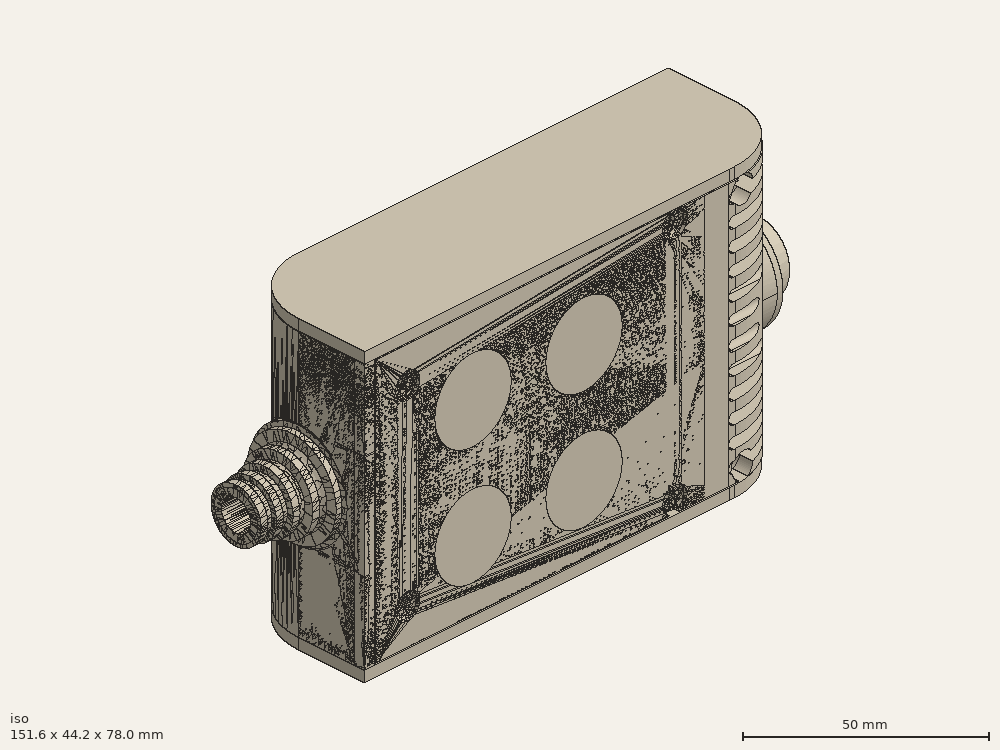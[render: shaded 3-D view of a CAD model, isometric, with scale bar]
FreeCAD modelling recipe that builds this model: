
FCSTD DOCUMENT  (FreeCAD 0.19R0.19.2)
Label: enclosure_186FCStd
License: All rights reserved
LicenseURL: http://en.wikipedia.org/wiki/All_rights_reserved
objects: Part::Revolution×152, Part::MultiFuse×146, Part::Feature×146, Sketcher::SketchObject×84, Part::Cut×70, Part::Cylinder×70, Part::Extrusion×67, Part::Fillet×58, Part::Box×36, App::MeasureDistance×4, PartDesign::Body×2, Image::ImagePlane×1
note: 831 computed .brp shape members not serialized (recipe doc carries the construction recipe); baked Part::Feature solids carry a one-line shape summary decoded from their .brp

FEATURE [Sketcher::SketchObject] Sketch  label="topSketch"
  FullyConstrained = true
  sketch-geometry (20):
    g0: LineSegment StartX=5.21097e-06 StartY=3 StartZ=0 EndX=5.21097e-06 EndY=19 EndZ=0
    g1: ArcOfCircle CenterX=19 CenterY=19 CenterZ=0 NormalX=0 NormalY=0 NormalZ=1 AngleXU=0 Radius=19 StartAngle=1.5708 EndAngle=3.14159
    g2: ArcOfCircle CenterX=19 CenterY=19 CenterZ=0 NormalX=0 NormalY=0 NormalZ=1 AngleXU=0 Radius=16 StartAngle=1.5708 EndAngle=3.14159
    g3: LineSegment StartX=114 StartY=35 StartZ=0 EndX=19 EndY=35 EndZ=0
    g4: LineSegment StartX=5.21097e-06 StartY=3 StartZ=0 EndX=5.21097e-06 EndY=0 EndZ=0
    g5: LineSegment StartX=3 StartY=0 StartZ=0 EndX=5.21097e-06 EndY=0 EndZ=0
    g6: LineSegment StartX=3 StartY=19 StartZ=0 EndX=3 EndY=0 EndZ=0
    g7: LineSegment StartX=19 StartY=38 StartZ=0 EndX=124 EndY=38 EndZ=0
    g8: Circle CenterX=119 CenterY=35 CenterZ=0 NormalX=0 NormalY=0 NormalZ=1 AngleXU=0 Radius=1
    g9: Circle CenterX=121 CenterY=35 CenterZ=0 NormalX=0 NormalY=0 NormalZ=1 AngleXU=0 Radius=1
    g10: Circle CenterX=121 CenterY=33 CenterZ=0 NormalX=0 NormalY=0 NormalZ=1 AngleXU=0 Radius=1
    g11: BSplineCurve PolesCount=3 KnotsCount=2 Degree=2 IsPeriodic=0
    g12: GeomPoint X=119 Y=35 Z=0
    g13: GeomPoint X=121 Y=33 Z=0
    g14: LineSegment StartX=119 StartY=35 StartZ=0 EndX=114 EndY=35 EndZ=0
    g15: ArcOfCircle CenterX=105 CenterY=19 CenterZ=0 NormalX=0 NormalY=0 NormalZ=1 AngleXU=0 Radius=19 StartAngle=5.7297 EndAngle=6.28319
    g16: ArcOfCircle CenterX=105 CenterY=19 CenterZ=0 NormalX=0 NormalY=0 NormalZ=1 AngleXU=0 Radius=16 StartAngle=5.60905 EndAngle=6.28319
    g17: LineSegment StartX=121 StartY=33 StartZ=0 EndX=121 EndY=19 EndZ=0
    g18: LineSegment StartX=124 StartY=38 StartZ=0 EndX=124 EndY=19 EndZ=0
    g19: LineSegment StartX=117.5 StartY=9.01251 StartZ=0 EndX=121.163 EndY=9.0125 EndZ=0
  constraints (46):
    c: Vertical(g0)
    c: Block(g0)
    c: Coincident(g1,g0)
    c: Block(g1)
    c: Coincident(g2,g1)
    c: Block(g2)
    c: Coincident(g3,g2)
    c: Horizontal(g3)
    c: Tangent(g3,g2)
    c: Coincident(g4,g0)
    c: Distance(g4) = 3
    c: Vertical(g4)
    c: Coincident(g5,g4)
    c: Horizontal(g5)
    c: Coincident(g6,g2)
    c: Coincident(g6,g5)
    c: Vertical(g6)
    c: Horizontal(g7)
    c: Distance(g7) = 105
    c: Coincident(g7,g1)
    c: Block(g3)
    c: Weight(g8) = 1
    c: Equal(g8,g9)
    c: Equal(g8,g10)
    c: InternalAlignment(g8,g11)
    c: InternalAlignment(g9,g11)
    c: InternalAlignment(g10,g11)
    c: InternalAlignment(g12,g11)
    c: InternalAlignment(g13,g11)
    c: Block(g11)
    c: Coincident(g14,g11)
    c: Coincident(g14,g3)
    c: Horizontal(g14)
    c: Block(g15)
    c: Coincident(g16,g15)
    c: Block(g16)
    c: Coincident(g17,g11)
    c: Coincident(g17,g16)
    c: Vertical(g17)
    c: Distance(g17) = 14
    c: Coincident(g18,g7)
    c: Coincident(g18,g15)
    c: Vertical(g18)
    c: Distance(g18) = 19
    c: Coincident(g19,g16)
    c: Coincident(g19,g15)
FEATURE [Sketcher::SketchObject] Sketch001  label="bottomSketch"
  FullyConstrained = true
  sketch-geometry (32):
    g0: LineSegment StartX=3.3 StartY=-6.03275e-07 StartZ=0 EndX=98 EndY=-6.03275e-07 EndZ=0
    g1: ArcOfCircle CenterX=98 CenterY=19 CenterZ=0 NormalX=0 NormalY=0 NormalZ=1 AngleXU=0 Radius=19 StartAngle=4.71239 EndAngle=5.71103
    g2: LineSegment StartX=6.3 StartY=8 StartZ=0 EndX=3.3 EndY=8 EndZ=0
    g3: LineSegment StartX=3.3 StartY=8 StartZ=0 EndX=3.3 EndY=-6.03275e-07 EndZ=0
    g4: ArcOfCircle CenterX=8.3 CenterY=5 CenterZ=0 NormalX=0 NormalY=0 NormalZ=1 AngleXU=0 Radius=2 StartAngle=3.14159 EndAngle=4.71239
    g5: LineSegment StartX=6.3 StartY=8 StartZ=0 EndX=6.3 EndY=5 EndZ=0
    g6: ArcOfCircle CenterX=98 CenterY=19 CenterZ=0 NormalX=0 NormalY=0 NormalZ=1 AngleXU=0 Radius=12.7 StartAngle=4.71239 EndAngle=6.28319
    g7: LineSegment StartX=94.7 StartY=3 StartZ=0 EndX=8.3 EndY=3 EndZ=0
    g8-g12: Circle x5 (B-spline internal-alignment scaffolding for g13; pole/knot coordinates omitted)
    g13: BSplineCurve PolesCount=5 KnotsCount=3 Degree=3 IsPeriodic=0
    g14: GeomPoint X=98 Y=6.3 Z=0
    g15: GeomPoint X=96.3938 Y=4.71946 Z=0
    g16: GeomPoint X=94.7 Y=3 Z=0
    g17-g23: Circle x7 (B-spline internal-alignment scaffolding for g24; pole/knot coordinates omitted)
    g24: BSplineCurve PolesCount=7 KnotsCount=5 Degree=3 IsPeriodic=0
    g25-g29: GeomPoint x5 (B-spline internal-alignment scaffolding for g24; pole/knot coordinates omitted)
    g30: ArcOfCircle CenterX=98 CenterY=19 CenterZ=0 NormalX=0 NormalY=0 NormalZ=1 AngleXU=0 Radius=15.7 StartAngle=5.81226 EndAngle=6.28319
    g31: LineSegment StartX=110.7 StartY=19 StartZ=0 EndX=113.7 EndY=19 EndZ=0
  constraints (41):
    c: Horizontal(g0)
    c: Coincident(g1,g0)
    c: Block(g1)
    c: Horizontal(g2)
    c: Distance(g2) = 3
    c: Coincident(g3,g2)
    c: Vertical(g3)
    c: Coincident(g3,g0)
    c: Block(g4)
    c: Block(g2)
    c: Coincident(g5,g2)
    c: Coincident(g5,g4)
    c: Vertical(g5)
    c: Coincident(g6,g1)
    c: Block(g6)
    c: Coincident(g7,g4)
    c: Horizontal(g7)
    c: Block(g0)
    c: Block(g7)
    c: Block(g3)
    c: Coincident(g13,g6)
    c: Weight(g8) = 1
    c: Equal(g8, g9-g12) x4
    c: Coincident(g13,g7)
    c: InternalAlignment(g8-g12 -> g13) x5
    c: InternalAlignment(g14,g13)
    c: InternalAlignment(g15,g13)
    c: InternalAlignment(g16,g13)
    c: Block(g13)
    c: Weight(g17) = 1
    c: Equal(g17, g18-g23) x6
    c: Coincident(g24,g1)
    c: InternalAlignment(g17-g23 -> g24) x7
    c: InternalAlignment(g25-g29 -> g24) x5
    c: Block(g24)
    c: Coincident(g30,g24)
    c: Coincident(g31,g6)
    c: Coincident(g31,g30)
    c: Horizontal(g31)
    c: Block(g31)
    c: Block(g30)
FEATURE [Part::Extrusion] Extrude  label="top"
  Base = -> Sketch
  Dir = (0,0,1)
  DirMode = 2
  FaceMakerClass = Part::FaceMakerBullseye
  LengthFwd = 72
  LengthRev = 0
  Solid = true
  Symmetric = false
FEATURE [Part::Extrusion] Extrude001  label="bottom"
  Base = -> Sketch001
  Dir = (0,0,1)
  DirMode = 2
  FaceMakerClass = Part::FaceMakerBullseye
  LengthFwd = 71.4
  LengthRev = 0
  Placement = pos=(0,0,0.3) rot=(0,0,1;0rad)
  Solid = true
  Symmetric = false
FEATURE [Sketcher::SketchObject] Sketch002  label="topSketch001"
  FullyConstrained = true
  sketch-geometry (8):
    g0: ArcOfCircle CenterX=19 CenterY=19.0975 CenterZ=0 NormalX=0 NormalY=0 NormalZ=1 AngleXU=0 Radius=18.9025 StartAngle=1.5708 EndAngle=3.14674
    g1: LineSegment StartX=0.0977805 StartY=19.0003 StartZ=0 EndX=0.0977805 EndY=0.000251602 EndZ=0
    g2: LineSegment StartX=19 StartY=38 StartZ=0 EndX=124 EndY=38 EndZ=0
    g3: LineSegment StartX=0.0977805 StartY=0.000251602 StartZ=0 EndX=105.098 EndY=0.000251602 EndZ=0
    g4: LineSegment StartX=124 StartY=38 StartZ=0 EndX=125.616 EndY=38 EndZ=0
    g5: LineSegment StartX=105.098 StartY=0.000251602 StartZ=0 EndX=106.713 EndY=0.000251602 EndZ=0
    g6: ArcOfCircle CenterX=106.616 CenterY=19 CenterZ=0 NormalX=0 NormalY=0 NormalZ=1 AngleXU=0 Radius=19 StartAngle=4.71754 EndAngle=6.28319
    g7: LineSegment StartX=125.616 StartY=38 StartZ=0 EndX=125.616 EndY=19 EndZ=0
  constraints (21):
    c: Block(g0)
    c: Coincident(g1,g0)
    c: Vertical(g1)
    c: Horizontal(g2)
    c: Distance(g2) = 105
    c: Coincident(g2,g0)
    c: Distance(g1) = 19
    c: Coincident(g3,g1)
    c: Horizontal(g3)
    c: Distance(g3) = 105
    c: Coincident(g4,g2)
    c: Horizontal(g4)
    c: Distance(g4) = 1.61553
    c: Horizontal(g5)
    c: Equal(g4,g5) = 1.61553
    c: Coincident(g5,g3)
    c: Block(g6)
    c: Coincident(g6,g5)
    c: Coincident(g7,g4)
    c: Coincident(g7,g6)
    c: Vertical(g7)
FEATURE [Part::Extrusion] Extrude002  label="sideA"
  Base = -> Sketch002
  Dir = (0,0,1)
  DirMode = 2
  FaceMakerClass = Part::FaceMakerBullseye
  LengthFwd = 3
  LengthRev = 0
  Placement = pos=(0,0,-3) rot=(0,0,1;0rad)
  Solid = true
  Symmetric = false
FEATURE [Sketcher::SketchObject] Sketch003  label="topSketch002"
  FullyConstrained = true
  sketch-geometry (6):
    g0: LineSegment StartX=19 StartY=38 StartZ=0 EndX=117 EndY=38 EndZ=0
    g1: ArcOfCircle CenterX=19 CenterY=19 CenterZ=0 NormalX=0 NormalY=0 NormalZ=1 AngleXU=0 Radius=19 StartAngle=1.5708 EndAngle=3.14159
    g2: LineSegment StartX=117 StartY=38 StartZ=0 EndX=117 EndY=19 EndZ=0
    g3: LineSegment StartX=98 StartY=1.0161e-12 StartZ=0 EndX=5.22862e-06 EndY=1.0161e-12 EndZ=0
    g4: LineSegment StartX=5.22862e-06 StartY=19 StartZ=0 EndX=5.22862e-06 EndY=1.0161e-12 EndZ=0
    g5: ArcOfCircle CenterX=98 CenterY=19 CenterZ=0 NormalX=0 NormalY=0 NormalZ=1 AngleXU=0 Radius=19 StartAngle=4.71239 EndAngle=6.28319
  constraints (16):
    c: Horizontal(g0)
    c: Distance(g0) = 98
    c: Coincident(g1,g0)
    c: Block(g1)
    c: Coincident(g2,g0)
    c: Vertical(g2)
    c: Distance(g2) = 19
    c: Horizontal(g3)
    c: Coincident(g4,g1)
    c: Vertical(g4)
    c: Coincident(g3,g4)
    c: Block(g3)
    c: Coincident(g5,g2)
    c: Coincident(g5,g3)
    c: Block(g0)
    c: Block(g5)
FEATURE [Sketcher::SketchObject] Sketch004
  FullyConstrained = true
  MapMode = 3
  Placement = pos=(0,0,0) rot=(1,0,0;1.5708rad)
  Support = -> [Extrude]
  sketch-geometry (8):
    g0: Circle CenterX=80.351 CenterY=-67.6202 CenterZ=0 NormalX=0 NormalY=0 NormalZ=1 AngleXU=0 Radius=2
    g1: Circle CenterX=80.351 CenterY=-67.6202 CenterZ=0 NormalX=0 NormalY=0 NormalZ=1 AngleXU=0 Radius=3
    g2: Circle CenterX=80.351 CenterY=-4.92017 CenterZ=0 NormalX=0 NormalY=0 NormalZ=1 AngleXU=0 Radius=2
    g3: Circle CenterX=80.351 CenterY=-4.92017 CenterZ=0 NormalX=0 NormalY=0 NormalZ=1 AngleXU=0 Radius=3
    g4: Circle CenterX=23.851 CenterY=-4.92017 CenterZ=0 NormalX=0 NormalY=0 NormalZ=1 AngleXU=0 Radius=2
    g5: Circle CenterX=23.851 CenterY=-4.92017 CenterZ=0 NormalX=0 NormalY=0 NormalZ=1 AngleXU=0 Radius=3
    g6: Circle CenterX=23.851 CenterY=-67.6202 CenterZ=0 NormalX=0 NormalY=0 NormalZ=1 AngleXU=0 Radius=2
    g7: Circle CenterX=23.851 CenterY=-67.6202 CenterZ=0 NormalX=0 NormalY=0 NormalZ=1 AngleXU=0 Radius=3
  constraints (8):
    c: Block(g3)
    c: Block(g2)
    c: Block(g1)
    c: Block(g0)
    c: Block(g6)
    c: Block(g7)
    c: Block(g4)
    c: Block(g5)
FEATURE [Part::Extrusion] Extrude004
  Base = -> Sketch004
  Dir = (0,-1,2e-16)
  DirMode = 2
  FaceMakerClass = Part::FaceMakerBullseye
  LengthFwd = 6
  LengthRev = 0
  Placement = pos=(0,9,0) rot=(0,0,1;0rad)
  Solid = true
  Symmetric = false
FEATURE [Sketcher::SketchObject] Sketch005
  FullyConstrained = true
  MapMode = 3
  Placement = pos=(0,0,0) rot=(1,0,0;1.5708rad)
  Support = -> [Extrude]
  sketch-geometry (8):
    g0: Circle CenterX=80.351 CenterY=-67.6202 CenterZ=0 NormalX=0 NormalY=0 NormalZ=1 AngleXU=0 Radius=3
    g1: Circle CenterX=80.351 CenterY=-4.92017 CenterZ=0 NormalX=0 NormalY=0 NormalZ=1 AngleXU=0 Radius=3
    g2: Circle CenterX=23.851 CenterY=-4.92017 CenterZ=0 NormalX=0 NormalY=0 NormalZ=1 AngleXU=0 Radius=3
    g3: Circle CenterX=23.851 CenterY=-67.6202 CenterZ=0 NormalX=0 NormalY=0 NormalZ=1 AngleXU=0 Radius=3
    g4: Circle CenterX=23.851 CenterY=-67.6202 CenterZ=0 NormalX=0 NormalY=0 NormalZ=1 AngleXU=0 Radius=5
    g5: Circle CenterX=80.351 CenterY=-67.6202 CenterZ=0 NormalX=0 NormalY=0 NormalZ=1 AngleXU=0 Radius=5
    g6: Circle CenterX=23.851 CenterY=-4.92017 CenterZ=0 NormalX=0 NormalY=0 NormalZ=1 AngleXU=0 Radius=5
    g7: Circle CenterX=80.351 CenterY=-4.92017 CenterZ=0 NormalX=0 NormalY=0 NormalZ=1 AngleXU=0 Radius=5
  constraints (8):
    c: Block(g1)
    c: Block(g0)
    c: Block(g3)
    c: Block(g2)
    c: Block(g5)
    c: Block(g4)
    c: Block(g6)
    c: Block(g7)
FEATURE [Part::Extrusion] Extrude005
  Base = -> Sketch005
  Dir = (0,-1,2e-16)
  DirMode = 2
  FaceMakerClass = Part::FaceMakerBullseye
  LengthFwd = 2
  LengthRev = 0
  Solid = true
  Symmetric = false
FEATURE [Sketcher::SketchObject] Sketch006
  FullyConstrained = true
  MapMode = 3
  Placement = pos=(0,0,0) rot=(1,0,0;1.5708rad)
  sketch-geometry (8):
    g0: Circle CenterX=80.351 CenterY=-67.6202 CenterZ=0 NormalX=0 NormalY=0 NormalZ=1 AngleXU=0 Radius=3
    g1: Circle CenterX=80.351 CenterY=-4.92017 CenterZ=0 NormalX=0 NormalY=0 NormalZ=1 AngleXU=0 Radius=3
    g2: Circle CenterX=23.851 CenterY=-4.92017 CenterZ=0 NormalX=0 NormalY=0 NormalZ=1 AngleXU=0 Radius=3
    g3: Circle CenterX=23.851 CenterY=-67.6202 CenterZ=0 NormalX=0 NormalY=0 NormalZ=1 AngleXU=0 Radius=3
    g4: Circle CenterX=23.851 CenterY=-67.6202 CenterZ=0 NormalX=0 NormalY=0 NormalZ=1 AngleXU=0 Radius=5
    g5: Circle CenterX=80.351 CenterY=-67.6202 CenterZ=0 NormalX=0 NormalY=0 NormalZ=1 AngleXU=0 Radius=5
    g6: Circle CenterX=23.851 CenterY=-4.92017 CenterZ=0 NormalX=0 NormalY=0 NormalZ=1 AngleXU=0 Radius=5
    g7: Circle CenterX=80.351 CenterY=-4.92017 CenterZ=0 NormalX=0 NormalY=0 NormalZ=1 AngleXU=0 Radius=5
  constraints (8):
    c: Block(g1)
    c: Block(g0)
    c: Block(g3)
    c: Block(g2)
    c: Block(g5)
    c: Block(g4)
    c: Block(g6)
    c: Block(g7)
FEATURE [Part::Extrusion] Extrude007
  Base = -> Sketch006
  Dir = (0,-1,2e-16)
  DirMode = 2
  FaceMakerClass = Part::FaceMakerBullseye
  LengthFwd = 2
  LengthRev = 0
  Solid = true
  Symmetric = false
FEATURE [Part::Fillet] Fillet
  Base = -> Extrude007
  Edges = 4 edges r=1.99: [Edge6,Edge12,Edge18,Edge24]
FEATURE [Part::Cut] Cut
  Base = -> Extrude005
  Placement = pos=(0,5,0) rot=(0,0,1;0rad)
  Tool = -> Fillet
FEATURE [Part::MultiFuse] Fusion  label="pCBScrews"
  Placement = pos=(-2.5,0,72.3) rot=(0,0,1;0rad)
  Shapes = -> [Extrude004,Cut]
FEATURE [App::MeasureDistance] Distance  label="Distance: 0.69 mm"
  Distance = 0.685967
  P1 = (24.0138,2.9647,0.3)
  P2 = (23.8901,3,-0.373787)
FEATURE [App::MeasureDistance] Distance001  label="Distance: 0.53 mm"
  Distance = 0.533607
  P1 = (80.2939,3,72.2334)
  P2 = (80.281,2.99661,71.7)
FEATURE [Part::Fillet] Fillet001
  Base = -> Extrude001
  Edges = 1 edges r=2.4: [Edge17]
FEATURE [Part::Fillet] Fillet002  label="bottom001"
  Base = -> Fillet001
  Edges = 1 edges r=2.4: [Edge36]
FEATURE [Part::Fillet] Fillet003  label="top001"
  Base = -> Extrude
  Edges = 1 edges r=2: [Edge1]
FEATURE [Sketcher::SketchObject] Sketch007
  FullyConstrained = true
  sketch-geometry (16):
    g0: LineSegment StartX=4 StartY=0 StartZ=0 EndX=4 EndY=2.4 EndZ=0
    g1: LineSegment StartX=4 StartY=2.4 StartZ=0 EndX=7 EndY=2.4 EndZ=0
    g2: LineSegment StartX=4 StartY=0 StartZ=0 EndX=5.7 EndY=0 EndZ=0
    g3: LineSegment StartX=5.7 StartY=0 StartZ=0 EndX=5.7 EndY=-5.6 EndZ=0
    g4-g8: Circle x5 (B-spline internal-alignment scaffolding for g9; pole/knot coordinates omitted)
    g9: BSplineCurve PolesCount=5 KnotsCount=3 Degree=3 IsPeriodic=0
    g10: GeomPoint X=7 Y=2.4 Z=0
    g11: GeomPoint X=10.4582 Y=-1.55472 Z=0
    g12: GeomPoint X=14 Y=-5.6 Z=0
    g13: LineSegment StartX=14 StartY=-5.6 StartZ=0 EndX=14 EndY=-14.1 EndZ=0
    g14: LineSegment StartX=14 StartY=-14.1 StartZ=0 EndX=6.5 EndY=-14.1 EndZ=0
    g15: LineSegment StartX=5.7 StartY=-5.6 StartZ=0 EndX=6.5 EndY=-14.1 EndZ=0
  constraints (28):
    c: Distance(g0) = 2.4
    c: Vertical(g0)
    c: Block(g0)
    c: Coincident(g1,g0)
    c: Horizontal(g1)
    c: Distance(g1) = 3
    c: Coincident(g2,g0)
    c: Horizontal(g2)
    c: Distance(g2) = 1.7
    c: Coincident(g3,g2)
    c: Vertical(g3)
    c: Distance(g3) = 5.6
    c: Coincident(g9,g1)
    c: Weight(g4) = 1
    c: Equal(g4, g5-g8) x4
    c: InternalAlignment(g4-g8 -> g9) x5
    c: InternalAlignment(g10,g9)
    c: InternalAlignment(g11,g9)
    c: InternalAlignment(g12,g9)
    c: Block(g9)
    c: Coincident(g13,g9)
    c: Vertical(g13)
    c: Distance(g13) = 8.5
    c: Coincident(g14,g13)
    c: Horizontal(g14)
    c: Distance(g14) = 7.5
    c: Coincident(g15,g3)
    c: Coincident(g15,g14)
FEATURE [Part::Feature] Face
  shape: bbox 10 x 16.5 x 2e-07 mm, 1 faces, 0 solids (baked)
FEATURE [Part::Revolution] Revolve  label="plugHousing"
  Angle = 360
  Axis = (0,1,0)
  Base = (0,0,0)
  FaceMakerClass = Part::FaceMakerBullseye
  Placement = pos=(0,0,36.15) rot=(0,0,1;0rad)
  Solid = false
  Source = -> Face
  Symmetric = false
FEATURE [Part::Feature] Face001
  shape: bbox 10 x 16.5 x 2e-07 mm, 1 faces, 0 solids (baked)
FEATURE [Part::Revolution] Revolve001  label="plugHousing001"
  Angle = 360
  Axis = (0,1,0)
  Base = (0,0,0)
  FaceMakerClass = Part::FaceMakerBullseye
  Placement = pos=(0,0,36.15) rot=(0,0,1;0rad)
  Solid = false
  Source = -> Face001
  Symmetric = false
FEATURE [Part::MultiFuse] Fusion001  label="plugHousing002"
  Placement = pos=(0,0,0) rot=(0,0,1;1.5708rad)
  Shapes = -> [Revolve001,Revolve]
FEATURE [Part::Feature] Face002
  shape: bbox 10 x 16.5 x 2e-07 mm, 1 faces, 0 solids (baked)
FEATURE [Part::Revolution] Revolve003  label="plugHousing005"
  Angle = 360
  Axis = (0,1,0)
  Base = (0,0,0)
  FaceMakerClass = Part::FaceMakerBullseye
  Placement = pos=(0,0,36.15) rot=(0,0,1;0rad)
  Solid = false
  Source = -> Face002
  Symmetric = false
FEATURE [Part::Feature] Face003
  shape: bbox 10 x 16.5 x 2e-07 mm, 1 faces, 0 solids (baked)
FEATURE [Part::Revolution] Revolve002  label="plugHousing003"
  Angle = 360
  Axis = (0,1,0)
  Base = (0,0,0)
  FaceMakerClass = Part::FaceMakerBullseye
  Placement = pos=(0,0,36.15) rot=(0,0,1;0rad)
  Solid = false
  Source = -> Face003
  Symmetric = false
FEATURE [Part::MultiFuse] Fusion002  label="plugHousing004"
  Placement = pos=(0,0,0) rot=(0,0,1;1.5708rad)
  Shapes = -> [Revolve002,Revolve003]
FEATURE [Part::MultiFuse] Fusion003  label="plugHousing006"
  Placement = pos=(0,19,0) rot=(0,0,1;3.14159rad)
  Shapes = -> [Fusion002,Fusion001]
FEATURE [Part::Feature] Face004
  shape: bbox 10 x 16.5 x 2e-07 mm, 1 faces, 0 solids (baked)
FEATURE [Part::Revolution] Revolve006  label="plugHousing010"
  Angle = 360
  Axis = (0,1,0)
  Base = (0,0,0)
  FaceMakerClass = Part::FaceMakerBullseye
  Placement = pos=(0,0,36.15) rot=(0,0,1;0rad)
  Solid = false
  Source = -> Face004
  Symmetric = false
FEATURE [Part::Feature] Face005
  shape: bbox 10 x 16.5 x 2e-07 mm, 1 faces, 0 solids (baked)
FEATURE [Part::Revolution] Revolve007  label="plugHousing011"
  Angle = 360
  Axis = (0,1,0)
  Base = (0,0,0)
  FaceMakerClass = Part::FaceMakerBullseye
  Placement = pos=(0,0,36.15) rot=(0,0,1;0rad)
  Solid = false
  Source = -> Face005
  Symmetric = false
FEATURE [Part::Feature] Face006
  shape: bbox 10 x 16.5 x 2e-07 mm, 1 faces, 0 solids (baked)
FEATURE [Part::Revolution] Revolve004  label="plugHousing007"
  Angle = 360
  Axis = (0,1,0)
  Base = (0,0,0)
  FaceMakerClass = Part::FaceMakerBullseye
  Placement = pos=(0,0,36.15) rot=(0,0,1;0rad)
  Solid = false
  Source = -> Face006
  Symmetric = false
FEATURE [Part::MultiFuse] Fusion004  label="plugHousing009"
  Placement = pos=(0,0,0) rot=(0,0,1;1.5708rad)
  Shapes = -> [Revolve004,Revolve007]
FEATURE [Part::Feature] Face007
  shape: bbox 10 x 16.5 x 2e-07 mm, 1 faces, 0 solids (baked)
FEATURE [Part::Revolution] Revolve005  label="plugHousing008"
  Angle = 360
  Axis = (0,1,0)
  Base = (0,0,0)
  FaceMakerClass = Part::FaceMakerBullseye
  Placement = pos=(0,0,36.15) rot=(0,0,1;0rad)
  Solid = false
  Source = -> Face007
  Symmetric = false
FEATURE [Part::MultiFuse] Fusion005  label="plugHousing012"
  Placement = pos=(0,0,0) rot=(0,0,1;1.5708rad)
  Shapes = -> [Revolve006,Revolve005]
FEATURE [Part::MultiFuse] Fusion006  label="plugHousing013"
  Placement = pos=(0,19,0) rot=(0,0,1;3.14159rad)
  Shapes = -> [Fusion005,Fusion004]
FEATURE [Part::MultiFuse] Fusion007  label="plugHousing014"
  Placement = pos=(122.621,0,-0.15) rot=(0,0,1;0rad)
  Shapes = -> [Fusion003,Fusion006]
FEATURE [Part::Cylinder] Cylinder002
  Angle = 360
  AttacherType = Attacher::AttachEngine3D
  Height = 20
  Placement = pos=(0,0,36.15) rot=(0,0,1;0rad)
  Radius = 4
FEATURE [Part::Cylinder] Cylinder003
  Angle = 360
  AttacherType = Attacher::AttachEngine3D
  Height = 10
  Placement = pos=(0,0,36.15) rot=(0,0,1;0rad)
  Radius = 4
FEATURE [Part::MultiFuse] Fusion009  label="removeToCreateHoleForPlugHousing"
  Placement = pos=(70,19,36.15) rot=(0,1,0;1.5708rad)
  Shapes = -> [Cylinder002,Cylinder003]
FEATURE [Part::Cylinder] Cylinder004
  Angle = 360
  AttacherType = Attacher::AttachEngine3D
  Height = 20
  Placement = pos=(0,0,36.15) rot=(0,0,1;0rad)
  Radius = 4
FEATURE [Part::Cylinder] Cylinder005
  Angle = 360
  AttacherType = Attacher::AttachEngine3D
  Height = 10
  Placement = pos=(0,0,36.15) rot=(0,0,1;0rad)
  Radius = 4
FEATURE [Part::MultiFuse] Fusion010  label="removeToCreateHoleForPlugHousing001"
  Placement = pos=(70,19,36.15) rot=(0,1,0;1.5708rad)
  Shapes = -> [Cylinder004,Cylinder005]
FEATURE [Part::Cut] Cut001
  Base = -> Fillet003
  Tool = -> Fusion010
FEATURE [Part::Cut] Cut002  label="Bottom"
  Base = -> Fillet002
  Tool = -> Fusion009
FEATURE [Part::Feature] Face008
  shape: bbox 10 x 16.5 x 2e-07 mm, 1 faces, 0 solids (baked)
FEATURE [Part::Revolution] Revolve011  label="plugHousing021"
  Angle = 360
  Axis = (0,1,0)
  Base = (0,0,0)
  FaceMakerClass = Part::FaceMakerBullseye
  Placement = pos=(0,0,36.15) rot=(0,0,1;0rad)
  Solid = false
  Source = -> Face008
  Symmetric = false
FEATURE [Part::Feature] Face009
  shape: bbox 10 x 16.5 x 2e-07 mm, 1 faces, 0 solids (baked)
FEATURE [Part::Revolution] Revolve012  label="plugHousing022"
  Angle = 360
  Axis = (0,1,0)
  Base = (0,0,0)
  FaceMakerClass = Part::FaceMakerBullseye
  Placement = pos=(0,0,36.15) rot=(0,0,1;0rad)
  Solid = false
  Source = -> Face009
  Symmetric = false
FEATURE [Part::Feature] Face010 .. Face013  x4 (patterned run collapsed; names and placements below)
  shape: bbox 10 x 16.5 x 2e-07 mm, 1 faces, 0 solids (baked)
FEATURE [Part::Revolution] Revolve015  label="plugHousing027"
  Angle = 360
  Axis = (0,1,0)
  Base = (0,0,0)
  FaceMakerClass = Part::FaceMakerBullseye
  Placement = pos=(0,0,36.15) rot=(0,0,1;0rad)
  Solid = false
  Source = -> Face013
  Symmetric = false
FEATURE [Part::Feature] Face014
  shape: bbox 10 x 16.5 x 2e-07 mm, 1 faces, 0 solids (baked)
FEATURE [Part::Feature] Face015
  shape: bbox 10 x 16.5 x 2e-07 mm, 1 faces, 0 solids (baked)
FEATURE [Part::Feature] Face016
  shape: bbox 10 x 16.5 x 2e-07 mm, 1 faces, 0 solids (baked)
FEATURE [Part::Revolution] Revolve019  label="plugHousing033"
  Angle = 360
  Axis = (0,1,0)
  Base = (0,0,0)
  FaceMakerClass = Part::FaceMakerBullseye
  Placement = pos=(0,0,36.15) rot=(0,0,1;0rad)
  Solid = false
  Source = -> Face016
  Symmetric = false
FEATURE [Part::Feature] Face017
  shape: bbox 10 x 16.5 x 2e-07 mm, 1 faces, 0 solids (baked)
FEATURE [Part::Revolution] Revolve020  label="plugHousing034"
  Angle = 360
  Axis = (0,1,0)
  Base = (0,0,0)
  FaceMakerClass = Part::FaceMakerBullseye
  Placement = pos=(0,0,36.15) rot=(0,0,1;0rad)
  Solid = false
  Source = -> Face017
  Symmetric = false
FEATURE [Part::Feature] Face018
  shape: bbox 10 x 16.5 x 2e-07 mm, 1 faces, 0 solids (baked)
FEATURE [Part::Revolution] Revolve016  label="plugHousing030"
  Angle = 360
  Axis = (0,1,0)
  Base = (0,0,0)
  FaceMakerClass = Part::FaceMakerBullseye
  Placement = pos=(0,0,36.15) rot=(0,0,1;0rad)
  Solid = false
  Source = -> Face018
  Symmetric = false
FEATURE [Part::MultiFuse] Fusion020  label="plugHousing038"
  Placement = pos=(0,0,0) rot=(0,0,1;1.5708rad)
  Shapes = -> [Revolve016,Revolve020]
FEATURE [Part::Feature] Face019
  shape: bbox 10 x 16.5 x 2e-07 mm, 1 faces, 0 solids (baked)
FEATURE [Part::Feature] Face020
  shape: bbox 10 x 16.5 x 2e-07 mm, 1 faces, 0 solids (baked)
FEATURE [Part::Revolution] Revolve017  label="plugHousing031"
  Angle = 360
  Axis = (0,1,0)
  Base = (0,0,0)
  FaceMakerClass = Part::FaceMakerBullseye
  Placement = pos=(0,0,36.15) rot=(0,0,1;0rad)
  Solid = false
  Source = -> Face020
  Symmetric = false
FEATURE [Part::MultiFuse] Fusion021  label="plugHousing039"
  Placement = pos=(0,0,0) rot=(0,0,1;1.5708rad)
  Shapes = -> [Revolve019,Revolve017]
FEATURE [Part::MultiFuse] Fusion023  label="plugHousing041"
  Placement = pos=(0,19,0) rot=(0,0,1;3.14159rad)
  Shapes = -> [Fusion021,Fusion020]
FEATURE [Part::Revolution] Revolve022  label="plugHousing043"
  Angle = 360
  Axis = (0,1,0)
  Base = (0,0,0)
  FaceMakerClass = Part::FaceMakerBullseye
  Placement = pos=(0,0,36.15) rot=(0,0,1;0rad)
  Solid = false
  Source = -> Face019
  Symmetric = false
FEATURE [Part::Feature] Face021
  shape: bbox 10 x 16.5 x 2e-07 mm, 1 faces, 0 solids (baked)
FEATURE [Part::Revolution] Revolve023  label="plugHousing044"
  Angle = 360
  Axis = (0,1,0)
  Base = (0,0,0)
  FaceMakerClass = Part::FaceMakerBullseye
  Placement = pos=(0,0,36.15) rot=(0,0,1;0rad)
  Solid = false
  Source = -> Face021
  Symmetric = false
FEATURE [Part::Feature] Face022
  shape: bbox 10 x 16.5 x 2e-07 mm, 1 faces, 0 solids (baked)
FEATURE [Part::Revolution] Revolve018  label="plugHousing032"
  Angle = 360
  Axis = (0,1,0)
  Base = (0,0,0)
  FaceMakerClass = Part::FaceMakerBullseye
  Placement = pos=(0,0,36.15) rot=(0,0,1;0rad)
  Solid = false
  Source = -> Face022
  Symmetric = false
FEATURE [Part::MultiFuse] Fusion022  label="plugHousing040"
  Placement = pos=(0,0,0) rot=(0,0,1;1.5708rad)
  Shapes = -> [Revolve018,Revolve023]
FEATURE [Part::Feature] Face023
  shape: bbox 10 x 16.5 x 2e-07 mm, 1 faces, 0 solids (baked)
FEATURE [Part::Revolution] Revolve021  label="plugHousing035"
  Angle = 360
  Axis = (0,1,0)
  Base = (0,0,0)
  FaceMakerClass = Part::FaceMakerBullseye
  Placement = pos=(0,0,36.15) rot=(0,0,1;0rad)
  Solid = false
  Source = -> Face023
  Symmetric = false
FEATURE [Part::MultiFuse] Fusion018  label="plugHousing036"
  Placement = pos=(0,0,0) rot=(0,0,1;1.5708rad)
  Shapes = -> [Revolve022,Revolve021]
FEATURE [Part::MultiFuse] Fusion019  label="plugHousing037"
  Placement = pos=(0,19,0) rot=(0,0,1;3.14159rad)
  Shapes = -> [Fusion018,Fusion022]
FEATURE [Part::MultiFuse] Fusion024  label="plugHousing042"
  Placement = pos=(122.621,0,-0.15) rot=(0,0,1;0rad)
  Shapes = -> [Fusion023,Fusion019]
FEATURE [Part::Cylinder] Cylinder006
  Angle = 360
  AttacherType = Attacher::AttachEngine3D
  Height = 20
  Placement = pos=(0,0,36.15) rot=(0,0,1;0rad)
  Radius = 14.3
FEATURE [Part::Cylinder] Cylinder007
  Angle = 360
  AttacherType = Attacher::AttachEngine3D
  Height = 10
  Placement = pos=(0,0,36.15) rot=(0,0,1;0rad)
  Radius = 4
FEATURE [Part::MultiFuse] Fusion026  label="removeToCreteHoleForPlugHousing"
  Placement = pos=(70,19,36) rot=(0,1,0;1.5708rad)
  Shapes = -> [Cylinder006,Cylinder007]
FEATURE [Part::Box] Box001  label="Cube001"
  AttacherType = Attacher::AttachEngine3D
  Height = 28
  Length = 3
  Placement = pos=(110.7,19,22) rot=(0,0,1;0rad)
  Width = 15.7
FEATURE [Part::Cut] Cut003  label="top002"
  Base = -> Cut001
  Tool = -> Fusion007
FEATURE [Part::Revolution] Revolve008  label="plugHousing015"
  Angle = 360
  Axis = (0,1,0)
  Base = (0,0,0)
  FaceMakerClass = Part::FaceMakerBullseye
  Placement = pos=(0,0,36.15) rot=(0,0,1;0rad)
  Solid = false
  Source = -> Face010
  Symmetric = false
FEATURE [Part::MultiFuse] Fusion013  label="plugHousing020"
  Placement = pos=(0,0,0) rot=(0,0,1;1.5708rad)
  Shapes = -> [Revolve008,Revolve012]
FEATURE [Part::Cut] Cut004  label="top003"
  Base = -> Cut003
  Placement = pos=(1,0,0) rot=(0,0,1;0rad)
  Tool = -> Fusion026
FEATURE [Part::Cylinder] Cylinder008
  Angle = 360
  AttacherType = Attacher::AttachEngine3D
  Height = 20
  Placement = pos=(0,0,36.15) rot=(0,0,1;0rad)
  Radius = 10.3
FEATURE [Part::Cylinder] Cylinder009
  Angle = 360
  AttacherType = Attacher::AttachEngine3D
  Height = 10
  Placement = pos=(0,0,36.15) rot=(0,0,1;0rad)
  Radius = 4
FEATURE [Part::MultiFuse] Fusion027  label="removeToCreteHoleForPlugHousing001"
  Placement = pos=(70,19,36) rot=(0,1,0;1.5708rad)
  Shapes = -> [Cylinder008,Cylinder009]
FEATURE [Part::Cut] Cut005  label="plugHousingTab"
  Base = -> Box001
  Tool = -> Fusion027
FEATURE [Part::MultiFuse] Fusion028  label="plugHousing045"
  Shapes = -> [Fusion024,Cut005]
FEATURE [Part::Box] Box002  label="Cube002"
  AttacherType = Attacher::AttachEngine3D
  Height = 28.8
  Length = 3
  Placement = pos=(107.3,28,21.6) rot=(0,0,1;0rad)
  Width = 7
FEATURE [Part::Box] Box003  label="Cube003"
  AttacherType = Attacher::AttachEngine3D
  Height = 3
  Length = 6.4
  Placement = pos=(107.3,28,18.6) rot=(0,0,1;0rad)
  Width = 7
FEATURE [Part::Box] Box004  label="Cube004"
  AttacherType = Attacher::AttachEngine3D
  Height = 3
  Length = 6.4
  Placement = pos=(107.3,28,50.4) rot=(0,0,1;0rad)
  Width = 7
FEATURE [Part::MultiFuse] Fusion029  label="plugHousingBracketHolder"
  Shapes = -> [Box004,Box002,Box003]
FEATURE [Part::Cylinder] Cylinder010
  Angle = 360
  AttacherType = Attacher::AttachEngine3D
  Height = 20
  Placement = pos=(0,0,36.15) rot=(0,0,1;0rad)
  Radius = 14.3
FEATURE [Part::Cylinder] Cylinder011
  Angle = 360
  AttacherType = Attacher::AttachEngine3D
  Height = 10
  Placement = pos=(0,0,36.15) rot=(0,0,1;0rad)
  Radius = 4
FEATURE [Part::MultiFuse] Fusion030  label="removeToCreteHoleForPlugHousing002"
  Placement = pos=(70,19,36) rot=(0,1,0;1.5708rad)
  Shapes = -> [Cylinder010,Cylinder011]
FEATURE [Part::Cut] Cut006  label="plugHousingBracketHolder001"
  Base = -> Fusion029
  Tool = -> Fusion030
FEATURE [Part::Cylinder] Cylinder012
  Angle = 360
  AttacherType = Attacher::AttachEngine3D
  Height = 20
  Placement = pos=(0,0,36.15) rot=(0,0,1;0rad)
  Radius = 7
FEATURE [Part::Cylinder] Cylinder013
  Angle = 360
  AttacherType = Attacher::AttachEngine3D
  Height = 10
  Placement = pos=(0,0,36.15) rot=(0,0,1;0rad)
  Radius = 4
FEATURE [Part::MultiFuse] Fusion032  label="removeToCreteHoleForPlugHousing003"
  Placement = pos=(70,19,36) rot=(0,1,0;1.5708rad)
  Shapes = -> [Cylinder012,Cylinder013]
FEATURE [Part::Cut] Cut007  label="bottom002"
  Base = -> Cut002
  Tool = -> Fusion032
FEATURE [Sketcher::SketchObject] Sketch008
  FullyConstrained = true
  sketch-geometry (54):
    g0: LineSegment StartX=-4.2 StartY=0 StartZ=0 EndX=-6.2 EndY=0 EndZ=0
    g1: LineSegment StartX=-14 StartY=-18 StartZ=0 EndX=-14 EndY=-26.5 EndZ=0
    g2: LineSegment StartX=-4.2 StartY=0 StartZ=0 EndX=-4.2 EndY=-13.4877 EndZ=0
    g3: Circle CenterX=-4.2 CenterY=-13.4877 CenterZ=0 NormalX=0 NormalY=0 NormalZ=1 AngleXU=0 Radius=1
    g4: Circle CenterX=-4.2 CenterY=-26.5 CenterZ=0 NormalX=0 NormalY=0 NormalZ=1 AngleXU=0 Radius=1
    g5: Circle CenterX=-8.2 CenterY=-26.5 CenterZ=0 NormalX=0 NormalY=0 NormalZ=1 AngleXU=0 Radius=1
    g6: BSplineCurve PolesCount=3 KnotsCount=2 Degree=2 IsPeriodic=0
    g7: GeomPoint X=-4.2 Y=-13.4877 Z=0
    g8: GeomPoint X=-8.2 Y=-26.5 Z=0
    g9: LineSegment StartX=-14 StartY=-26.5 StartZ=0 EndX=-8.2 EndY=-26.5 EndZ=0
    g10: LineSegment StartX=-10.15 StartY=-12 StartZ=0 EndX=-10.15 EndY=-14 EndZ=0
    g11: LineSegment StartX=-12.8401 StartY=-16 StartZ=0 EndX=-10.1571 EndY=-16 EndZ=0
    g12: LineSegment StartX=-10.15 StartY=-14 StartZ=0 EndX=-8.70761 EndY=-14 EndZ=0
    g13: LineSegment StartX=-12.8401 StartY=-16 StartZ=0 EndX=-12.8401 EndY=-17.6958 EndZ=0
    g14: LineSegment StartX=-10.15 StartY=-12 StartZ=0 EndX=-7.79258 EndY=-12 EndZ=0
    g15: Circle CenterX=-6.2215 CenterY=-2 CenterZ=0 NormalX=0 NormalY=0 NormalZ=1 AngleXU=0 Radius=1
    g16: Circle CenterX=-6.22762 CenterY=-2.58724 CenterZ=0 NormalX=0 NormalY=0 NormalZ=1 AngleXU=0 Radius=1
    g17: Circle CenterX=-6.32538 CenterY=-4 CenterZ=0 NormalX=0 NormalY=0 NormalZ=1 AngleXU=0 Radius=1
    g18: BSplineCurve PolesCount=3 KnotsCount=2 Degree=2 IsPeriodic=0
    g19: GeomPoint X=-6.2215 Y=-2 Z=0
    g20: GeomPoint X=-6.32538 Y=-4 Z=0
    g21: Circle CenterX=-6.48644 CenterY=-5.99526 CenterZ=0 NormalX=0 NormalY=0 NormalZ=1 AngleXU=0 Radius=1
    g22: Circle CenterX=-6.58486 CenterY=-6.99526 CenterZ=0 NormalX=0 NormalY=0 NormalZ=1 AngleXU=0 Radius=1
    g23: Circle CenterX=-6.77343 CenterY=-8 CenterZ=0 NormalX=0 NormalY=0 NormalZ=1 AngleXU=0 Radius=1
    g24: BSplineCurve PolesCount=3 KnotsCount=2 Degree=2 IsPeriodic=0
    g25: GeomPoint X=-6.48644 Y=-5.99526 Z=0
    g26: GeomPoint X=-6.77343 Y=-8 Z=0
    g27: Circle CenterX=-7.19003 CenterY=-10 CenterZ=0 NormalX=0 NormalY=0 NormalZ=1 AngleXU=0 Radius=1
    g28: Circle CenterX=-7.44407 CenterY=-11.0915 CenterZ=0 NormalX=0 NormalY=0 NormalZ=1 AngleXU=0 Radius=1
    g29: Circle CenterX=-7.79258 CenterY=-12 CenterZ=0 NormalX=0 NormalY=0 NormalZ=1 AngleXU=0 Radius=1
    g30: BSplineCurve PolesCount=3 KnotsCount=2 Degree=2 IsPeriodic=0
    g31: GeomPoint X=-7.19003 Y=-10 Z=0
    g32: GeomPoint X=-7.79258 Y=-12 Z=0
    g33: Circle CenterX=-8.70761 CenterY=-14 CenterZ=0 NormalX=0 NormalY=0 NormalZ=1 AngleXU=0 Radius=1
    g34: Circle CenterX=-9.33087 CenterY=-15.1837 CenterZ=0 NormalX=0 NormalY=0 NormalZ=1 AngleXU=0 Radius=1
    g35: Circle CenterX=-10.1571 CenterY=-16 CenterZ=0 NormalX=0 NormalY=0 NormalZ=1 AngleXU=0 Radius=1
    g36: BSplineCurve PolesCount=3 KnotsCount=2 Degree=2 IsPeriodic=0
    g37: GeomPoint X=-8.70761 Y=-14 Z=0
    g38: GeomPoint X=-10.1571 Y=-16 Z=0
    g39: Circle CenterX=-12.8401 CenterY=-17.6958 CenterZ=0 NormalX=0 NormalY=0 NormalZ=1 AngleXU=0 Radius=1
    g40: Circle CenterX=-13.3521 CenterY=-17.9027 CenterZ=0 NormalX=0 NormalY=0 NormalZ=1 AngleXU=0 Radius=1
    g41: Circle CenterX=-14 CenterY=-18 CenterZ=0 NormalX=0 NormalY=0 NormalZ=1 AngleXU=0 Radius=1
    g42: BSplineCurve PolesCount=3 KnotsCount=2 Degree=2 IsPeriodic=0
    g43: GeomPoint X=-12.8401 Y=-17.6958 Z=0
    g44: GeomPoint X=-14 Y=-18 Z=0
    g45: LineSegment StartX=-6.2 StartY=0 StartZ=0 EndX=-7.2 EndY=0 EndZ=0
    g46: LineSegment StartX=-7.2 StartY=0 StartZ=0 EndX=-7.2 EndY=-2 EndZ=0
    g47: LineSegment StartX=-7.2 StartY=-2 StartZ=0 EndX=-6.2215 EndY=-2 EndZ=0
    g48: LineSegment StartX=-6.32538 StartY=-4 StartZ=0 EndX=-7.65538 EndY=-4 EndZ=0
    g49: LineSegment StartX=-7.65538 StartY=-4 StartZ=0 EndX=-7.65538 EndY=-5.99526 EndZ=0
    g50: LineSegment StartX=-7.65538 StartY=-5.99526 StartZ=0 EndX=-6.48644 EndY=-5.99526 EndZ=0
    g51: LineSegment StartX=-6.77343 StartY=-8 StartZ=0 EndX=-8.43343 EndY=-8 EndZ=0
    g52: LineSegment StartX=-8.43343 StartY=-8 StartZ=0 EndX=-8.43343 EndY=-10 EndZ=0
    g53: LineSegment StartX=-8.43343 StartY=-10 StartZ=0 EndX=-7.19003 EndY=-10 EndZ=0
  constraints (112):
    c: Horizontal(g0)
    c: Distance(g0) = 2
    c: Block(g0)
    c: Vertical(g1)
    c: Coincident(g2,g0)
    c: Vertical(g2)
    c: Block(g2)
    c: Coincident(g6,g2)
    c: Weight(g3) = 1
    c: Equal(g3,g4)
    c: Equal(g3,g5)
    c: InternalAlignment(g3,g6)
    c: InternalAlignment(g4,g6)
    c: InternalAlignment(g5,g6)
    c: InternalAlignment(g7,g6)
    c: InternalAlignment(g8,g6)
    c: Block(g6)
    c: Coincident(g9,g1)
    c: Coincident(g9,g6)
    c: Horizontal(g9)
    c: Vertical(g10)
    c: Block(g10)
    c: Horizontal(g11)
    c: Block(g11)
    c: Coincident(g12,g10)
    c: Horizontal(g12)
    c: Block(g12)
    c: Coincident(g13,g11)
    c: Vertical(g13)
    c: Block(g13)
    c: Coincident(g14,g10)
    c: Horizontal(g14)
    c: Block(g14)
    c: Block(g9)
    c: Block(g1)
    c: Weight(g15) = 1
    c: Equal(g15,g16)
    c: Equal(g15,g17)
    c: InternalAlignment(g15,g18)
    c: InternalAlignment(g16,g18)
    c: InternalAlignment(g17,g18)
    c: InternalAlignment(g19,g18)
    c: InternalAlignment(g20,g18)
    c: Weight(g21) = 1
    c: Equal(g21,g22)
    c: Equal(g21,g23)
    c: InternalAlignment(g21,g24)
    c: InternalAlignment(g22,g24)
    c: InternalAlignment(g23,g24)
    c: InternalAlignment(g25,g24)
    c: InternalAlignment(g26,g24)
    c: Weight(g27) = 1
    c: Equal(g27,g28)
    c: Equal(g27,g29)
    c: Coincident(g30,g14)
    c: InternalAlignment(g27,g30)
    c: InternalAlignment(g28,g30)
    c: InternalAlignment(g29,g30)
    c: InternalAlignment(g31,g30)
    c: InternalAlignment(g32,g30)
    c: Coincident(g36,g12)
    c: Weight(g33) = 1
    c: Equal(g33,g34)
    c: Equal(g33,g35)
    c: Coincident(g36,g11)
    c: InternalAlignment(g33,g36)
    c: InternalAlignment(g34,g36)
    c: InternalAlignment(g35,g36)
    c: InternalAlignment(g37,g36)
    c: InternalAlignment(g38,g36)
    c: Coincident(g42,g13)
    c: Weight(g39) = 1
    c: Equal(g39,g40)
    c: Equal(g39,g41)
    c: Coincident(g42,g1)
    c: InternalAlignment(g39,g42)
    c: InternalAlignment(g40,g42)
    c: InternalAlignment(g41,g42)
    c: InternalAlignment(g43,g42)
    c: InternalAlignment(g44,g42)
    c: Block(g18)
    c: Block(g24)
    c: Block(g30)
    c: Block(g36)
    c: Block(g42)
    c: Horizontal(g45)
    c: Coincident(g45,g0)
    c: Vertical(g46)
    c: Coincident(g46,g45)
    c: Coincident(g47,g46)
    c: Coincident(g47,g18)
    c: Horizontal(g47)
    c: Block(g46)
    c: Coincident(g48,g18)
    c: Horizontal(g48)
    c: Distance(g48) = 1.33
    c: Vertical(g49)
    c: Coincident(g49,g48)
    c: Coincident(g50,g49)
    c: Coincident(g50,g24)
    c: Horizontal(g50)
    c: Tangent(g50,g22)
    c: Horizontal(g51)
    c: Coincident(g51,g24)
    c: Block(g51)
    c: Vertical(g52)
    c: Block(g52)
    c: Coincident(g52,g51)
    c: Coincident(g53,g52)
    c: Coincident(g53,g30)
    c: Horizontal(g53)
    c: Distance(g1) = 8.5
FEATURE [Part::Feature] Face024
  shape: bbox 9.8 x 26.5 x 2e-07 mm, 1 faces, 0 solids (baked)
FEATURE [Part::Revolution] Revolve024
  Angle = 360
  Axis = (0,1,0)
  Base = (0,0,0)
  FaceMakerClass = Part::FaceMakerBullseye
  Placement = pos=(0,0,0) rot=(0,0,1;1.5708rad)
  Solid = false
  Source = -> Face024
  Symmetric = false
FEATURE [Part::Feature] Face025
  shape: bbox 9.8 x 26.5 x 2e-07 mm, 1 faces, 0 solids (baked)
FEATURE [Part::Revolution] Revolve025
  Angle = 360
  Axis = (0,1,0)
  Base = (0,0,0)
  FaceMakerClass = Part::FaceMakerBullseye
  Placement = pos=(0,0,0) rot=(0,0,1;1.5708rad)
  Solid = false
  Source = -> Face025
  Symmetric = false
FEATURE [Part::MultiFuse] Fusion033
  Placement = pos=(-18,19,36) rot=(0,0,1;0rad)
  Shapes = -> [Revolve025,Revolve024]
FEATURE [Part::Cylinder] Cylinder014
  Angle = 360
  AttacherType = Attacher::AttachEngine3D
  Height = 20
  Placement = pos=(0,0,36.15) rot=(0,0,1;0rad)
  Radius = 14.3
FEATURE [Part::Cylinder] Cylinder015
  Angle = 360
  AttacherType = Attacher::AttachEngine3D
  Height = 10
  Placement = pos=(0,0,36.15) rot=(0,0,1;0rad)
  Radius = 4
FEATURE [Part::MultiFuse] Fusion034  label="removeToCreteHoleForPlugHousing004"
  Placement = pos=(-42,19,36) rot=(0,1,0;1.5708rad)
  Shapes = -> [Cylinder014,Cylinder015]
FEATURE [Part::Cut] Cut008  label="top004"
  Base = -> Cut004
  Placement = pos=(-1,0,0) rot=(0,0,1;0rad)
  Tool = -> Fusion034
FEATURE [Part::Box] Box005  label="Cube005"
  AttacherType = Attacher::AttachEngine3D
  Height = 28
  Length = 3
  Placement = pos=(110.7,19,22) rot=(0,0,1;0rad)
  Width = 15.7
FEATURE [Part::Cylinder] Cylinder016
  Angle = 360
  AttacherType = Attacher::AttachEngine3D
  Height = 10
  Placement = pos=(0,0,36.15) rot=(0,0,1;0rad)
  Radius = 4
FEATURE [Part::Cylinder] Cylinder017
  Angle = 360
  AttacherType = Attacher::AttachEngine3D
  Height = 20
  Placement = pos=(0,0,36.15) rot=(0,0,1;0rad)
  Radius = 10.3
FEATURE [Part::MultiFuse] Fusion035  label="removeToCreteHoleForPlugHousing005"
  Placement = pos=(70,19,36) rot=(0,1,0;1.5708rad)
  Shapes = -> [Cylinder017,Cylinder016]
FEATURE [Part::Cut] Cut009  label="plugHousingTab001"
  Base = -> Box005
  Placement = pos=(-107.4,-14,0) rot=(0,0,1;0rad)
  Tool = -> Fusion035
FEATURE [Part::Box] Box006  label="Cube006"
  AttacherType = Attacher::AttachEngine3D
  Height = 28
  Length = 3
  Placement = pos=(110.7,19,22) rot=(0,0,1;0rad)
  Width = 15.7
FEATURE [Part::Cylinder] Cylinder018
  Angle = 360
  AttacherType = Attacher::AttachEngine3D
  Height = 10
  Placement = pos=(0,0,36.15) rot=(0,0,1;0rad)
  Radius = 4
FEATURE [Part::Cylinder] Cylinder019
  Angle = 360
  AttacherType = Attacher::AttachEngine3D
  Height = 20
  Placement = pos=(0,0,36.15) rot=(0,0,1;0rad)
  Radius = 10.3
FEATURE [Part::MultiFuse] Fusion036  label="removeToCreteHoleForPlugHousing006"
  Placement = pos=(70,19,36) rot=(0,1,0;1.5708rad)
  Shapes = -> [Cylinder019,Cylinder018]
FEATURE [Part::Cut] Cut010  label="plugHousingTab002"
  Base = -> Box006
  Placement = pos=(-107.4,-14,0) rot=(0,0,1;0rad)
  Tool = -> Fusion036
FEATURE [Part::MultiFuse] Fusion037
  Placement = pos=(9.6,23,0) rot=(0,0,1;3.14159rad)
  Shapes = -> [Cut009,Cut010]
FEATURE [Part::Box] Box  label="Cube"
  AttacherType = Attacher::AttachEngine3D
  Height = 10
  Length = 3
  Placement = pos=(3.3,4,12) rot=(0,0,1;0rad)
  Width = 10
FEATURE [Part::Fillet] Fillet004
  Base = -> Fusion028
  Edges = 1 edges r=2: [Edge25]
FEATURE [Part::Fillet] Fillet005  label="plugHousing046"
  Base = -> Fillet004
  Edges = 1 edges r=2: [Edge8]
FEATURE [Part::Fillet] Fillet006
  Base = -> Box
  Edges = 1 edges r=2: [Edge11]
FEATURE [Part::Box] Box007  label="Cube007"
  AttacherType = Attacher::AttachEngine3D
  Height = 10
  Length = 3
  Placement = pos=(3.3,4,50) rot=(0,0,1;0rad)
  Width = 10
FEATURE [Part::Fillet] Fillet007
  Base = -> Box007
  Edges = 1 edges r=2: [Edge12]
FEATURE [Part::Box] Box008  label="Cube008"
  AttacherType = Attacher::AttachEngine3D
  Height = 28
  Length = 4
  Placement = pos=(5,0,22) rot=(0,0,1;0rad)
  Width = 10
FEATURE [Part::Fillet] Fillet008
  Base = -> Box008
  Edges = 1 edges r=1: [Edge7]
FEATURE [Part::Fillet] Fillet009
  Base = -> Fillet008
  Edges = 1 edges r=2: [Edge5]
FEATURE [Part::Fillet] Fillet010
  Base = -> Fillet009
  Edges = 1 edges r=2: [Edge2]
FEATURE [Sketcher::SketchObject] Sketch009  label="topSketch003"
  FullyConstrained = true
  sketch-geometry (4):
    g0: LineSegment StartX=16.8446 StartY=31.512 StartZ=0 EndX=16.3251 EndY=34.4666 EndZ=0
    g1: ArcOfCircle CenterX=19 CenterY=19.2524 CenterZ=0 NormalX=0 NormalY=0 NormalZ=1 AngleXU=0 Radius=15.4476 StartAngle=1.74483 EndAngle=2.72717
    g2: ArcOfCircle CenterX=19 CenterY=19.2524 CenterZ=0 NormalX=0 NormalY=0 NormalZ=1 AngleXU=0 Radius=12.4476 StartAngle=1.74483 EndAngle=2.73189
    g3: LineSegment StartX=4.86004 StartY=25.4725 StartZ=0 EndX=7.58253 EndY=24.2107 EndZ=0
  constraints (7):
    c: Block(g0)
    c: Coincident(g1,g0)
    c: Coincident(g2,g0)
    c: Coincident(g3,g1)
    c: Coincident(g3,g2)
    c: Block(g1)
    c: Block(g2)
FEATURE [Part::Extrusion] Extrude008
  Base = -> Sketch009
  Dir = (0,0,1)
  DirMode = 2
  FaceMakerClass = Part::FaceMakerBullseye
  LengthFwd = 10
  LengthRev = 0
  Placement = pos=(0,0,31) rot=(0,0,1;0rad)
  Solid = true
  Symmetric = false
FEATURE [Part::Cylinder] Cylinder020
  Angle = 360
  AttacherType = Attacher::AttachEngine3D
  Height = 20
  Placement = pos=(0,0,36.15) rot=(0,0,1;0rad)
  Radius = 8.2
FEATURE [Part::Cylinder] Cylinder021
  Angle = 360
  AttacherType = Attacher::AttachEngine3D
  Height = 10
  Placement = pos=(0,0,36.15) rot=(0,0,1;0rad)
  Radius = 4
FEATURE [Part::MultiFuse] Fusion038  label="removeToCreteHoleForPlugHousing007"
  Placement = pos=(-42,19,36) rot=(0,1,0;1.5708rad)
  Shapes = -> [Cylinder020,Cylinder021]
FEATURE [Part::Cut] Cut011
  Base = -> Extrude008
  Tool = -> Fusion038
FEATURE [Part::Fillet] Fillet011
  Base = -> Cut011
  Edges = 1 edges r=2: [Edge1]
FEATURE [Part::Fillet] Fillet012
  Base = -> Fillet011
  Edges = 1 edges r=2.5: [Edge1]
FEATURE [Part::Fillet] Fillet013
  Base = -> Fillet012
  Edges = 1 edges r=2.5: [Edge2]
FEATURE [Part::Box] Box010  label="Cube010"
  AttacherType = Attacher::AttachEngine3D
  Height = 16
  Length = 8
  Placement = pos=(12.7,31.52,28) rot=(0,0,1;0rad)
  Width = 4
FEATURE [Sketcher::SketchObject] Sketch010  label="topSketch004"
  FullyConstrained = true
  sketch-geometry (4):
    g0: LineSegment StartX=16.8446 StartY=31.512 StartZ=0 EndX=16.3251 EndY=34.4666 EndZ=0
    g1: ArcOfCircle CenterX=19 CenterY=19.2524 CenterZ=0 NormalX=0 NormalY=0 NormalZ=1 AngleXU=0 Radius=15.4476 StartAngle=1.74483 EndAngle=2.72717
    g2: ArcOfCircle CenterX=19 CenterY=19.2524 CenterZ=0 NormalX=0 NormalY=0 NormalZ=1 AngleXU=0 Radius=12.4476 StartAngle=1.74483 EndAngle=2.73189
    g3: LineSegment StartX=4.86004 StartY=25.4725 StartZ=0 EndX=7.58253 EndY=24.2107 EndZ=0
  constraints (7):
    c: Block(g0)
    c: Coincident(g1,g0)
    c: Coincident(g2,g0)
    c: Coincident(g3,g1)
    c: Coincident(g3,g2)
    c: Block(g1)
    c: Block(g2)
FEATURE [Part::Cylinder] Cylinder022
  Angle = 360
  AttacherType = Attacher::AttachEngine3D
  Height = 10
  Placement = pos=(0,0,36.15) rot=(0,0,1;0rad)
  Radius = 4
FEATURE [Sketcher::SketchObject] Sketch011  label="topSketch005"
  FullyConstrained = true
  sketch-geometry (4):
    g0: LineSegment StartX=16.8446 StartY=31.512 StartZ=0 EndX=16.3251 EndY=34.4666 EndZ=0
    g1: ArcOfCircle CenterX=19 CenterY=19.2524 CenterZ=0 NormalX=0 NormalY=0 NormalZ=1 AngleXU=0 Radius=15.4476 StartAngle=1.74483 EndAngle=2.72717
    g2: ArcOfCircle CenterX=19 CenterY=19.2524 CenterZ=0 NormalX=0 NormalY=0 NormalZ=1 AngleXU=0 Radius=12.4476 StartAngle=1.74483 EndAngle=2.73189
    g3: LineSegment StartX=4.86004 StartY=25.4725 StartZ=0 EndX=7.58253 EndY=24.2107 EndZ=0
  constraints (7):
    c: Block(g0)
    c: Coincident(g1,g0)
    c: Coincident(g2,g0)
    c: Coincident(g3,g1)
    c: Coincident(g3,g2)
    c: Block(g1)
    c: Block(g2)
FEATURE [Part::Extrusion] Extrude010
  Base = -> Sketch011
  Dir = (0,0,1)
  DirMode = 2
  FaceMakerClass = Part::FaceMakerBullseye
  LengthFwd = 10.6
  LengthRev = 0
  Placement = pos=(0,0,31) rot=(0,0,1;0rad)
  Solid = true
  Symmetric = false
FEATURE [Part::Cylinder] Cylinder023
  Angle = 360
  AttacherType = Attacher::AttachEngine3D
  Height = 20
  Placement = pos=(0,0,36.15) rot=(0,0,1;0rad)
  Radius = 8.2
FEATURE [Part::MultiFuse] Fusion039  label="removeToCreteHoleForPlugHousing008"
  Placement = pos=(-42,19,36) rot=(0,1,0;1.5708rad)
  Shapes = -> [Cylinder023,Cylinder022]
FEATURE [Part::Cut] Cut012
  Base = -> Extrude010
  Placement = pos=(0,0,-0.3) rot=(0,0,1;0rad)
  Tool = -> Fusion039
FEATURE [Part::Cut] Cut013
  Base = -> Box010
  Tool = -> Cut012
FEATURE [Part::Fillet] Fillet014
  Base = -> Cut013
  Edges = 1 edges r=0.7: [Edge13]
FEATURE [Part::Fillet] Fillet015
  Base = -> Fillet014
  Edges = 1 edges r=0.7: [Edge13]
FEATURE [Part::Fillet] Fillet016
  Base = -> Fillet015
  Edges = 1 edges r=0.7: [Edge16]
FEATURE [Part::Fillet] Fillet017
  Base = -> Fillet016
  Edges = 1 edges r=0.7: [Edge11]
FEATURE [Part::Fillet] Fillet018
  Base = -> Fillet017
  Edges = 1 edges r=0.7: [Edge10]
FEATURE [Part::Fillet] Fillet019
  Base = -> Fillet018
  Edges = 1 edges r=1.2: [Edge5]
FEATURE [Part::Fillet] Fillet020
  Base = -> Fillet019
  Edges = 1 edges r=1.2: [Edge12]
FEATURE [Part::Fillet] Fillet021
  Base = -> Fillet020
  Edges = 1 edges r=2: [Edge1]
  Placement = pos=(0.3,0,0) rot=(0,0,1;0rad)
FEATURE [Part::MultiFuse] Fusion040  label="top005"
  Shapes = -> [Cut008,Fillet021]
FEATURE [Part::MultiFuse] Fusion041  label="wireHolder"
  Shapes = -> [Fusion033,Fillet013]
FEATURE [Part::MultiFuse] Fusion042
  Shapes = -> [Fillet007,Fusion041]
FEATURE [Part::MultiFuse] Fusion043  label="wireHolder001"
  Shapes = -> [Fusion042,Fillet010]
FEATURE [Part::MultiFuse] Fusion044  label="wireHolder002"
  Shapes = -> [Fillet006,Fusion037,Fusion043]
FEATURE [Part::Feature] Face026
  shape: bbox 11 x 6 x 2e-07 mm, 1 faces, 0 solids (baked)
FEATURE [Part::Revolution] Revolve026
  Angle = 360
  Axis = (0,1,0)
  Base = (0,0,0)
  FaceMakerClass = Part::FaceMakerBullseye
  Placement = pos=(30.3,-1,19.7) rot=(0,0,1;0rad)
  Solid = false
  Source = -> Face026
  Symmetric = false
FEATURE [Sketcher::SketchObject] Sketch013  label="topSketch006"
  FullyConstrained = true
  sketch-geometry (13):
    g0: LineSegment StartX=117 StartY=19 StartZ=0 EndX=117 EndY=38 EndZ=0
    g1: ArcOfCircle CenterX=98 CenterY=19 CenterZ=0 NormalX=0 NormalY=0 NormalZ=1 AngleXU=0 Radius=19 StartAngle=5.7297 EndAngle=6.28319
    g2: LineSegment StartX=0 StartY=3 StartZ=0 EndX=0 EndY=19 EndZ=0
    g3: LineSegment StartX=19 StartY=38 StartZ=0 EndX=117 EndY=38 EndZ=0
    g4: ArcOfCircle CenterX=19 CenterY=19 CenterZ=0 NormalX=0 NormalY=0 NormalZ=1 AngleXU=0 Radius=19 StartAngle=1.5708 EndAngle=3.14159
    g5: ArcOfCircle CenterX=19 CenterY=19 CenterZ=0 NormalX=0 NormalY=0 NormalZ=1 AngleXU=0 Radius=16 StartAngle=1.5708 EndAngle=3.14159
    g6: ArcOfCircle CenterX=98 CenterY=19 CenterZ=0 NormalX=0 NormalY=0 NormalZ=1 AngleXU=0 Radius=16 StartAngle=5.60905 EndAngle=6.28319
    g7: LineSegment StartX=114 StartY=19 StartZ=0 EndX=114 EndY=35 EndZ=0
    g8: LineSegment StartX=110.5 StartY=9.01251 StartZ=0 EndX=114.163 EndY=9.01251 EndZ=0
    g9: LineSegment StartX=114 StartY=35 StartZ=0 EndX=19 EndY=35 EndZ=0
    g10: LineSegment StartX=0 StartY=3 StartZ=0 EndX=0 EndY=0 EndZ=0
    g11: LineSegment StartX=3 StartY=0 StartZ=0 EndX=0 EndY=0 EndZ=0
    g12: LineSegment StartX=3 StartY=19 StartZ=0 EndX=3 EndY=0 EndZ=0
  constraints (33):
    c: Vertical(g0)
    c: Distance(g0) = 19
    c: Block(g0)
    c: Coincident(g1,g0)
    c: Block(g1)
    c: Vertical(g2)
    c: Block(g2)
    c: Coincident(g3,g0)
    c: Horizontal(g3)
    c: Distance(g3) = 98
    c: Coincident(g4,g3)
    c: Coincident(g4,g2)
    c: Block(g4)
    c: Coincident(g5,g4)
    c: Coincident(g6,g1)
    c: Block(g6)
    c: Block(g5)
    c: Coincident(g7,g6)
    c: Vertical(g7)
    c: Coincident(g8,g6)
    c: Coincident(g8,g1)
    c: Coincident(g9,g7)
    c: Coincident(g9,g5)
    c: Horizontal(g9)
    c: Tangent(g9,g5)
    c: Coincident(g10,g2)
    c: Distance(g10) = 3
    c: Vertical(g10)
    c: Coincident(g11,g10)
    c: Horizontal(g11)
    c: Coincident(g12,g5)
    c: Coincident(g12,g11)
    c: Vertical(g12)
FEATURE [Part::Extrusion] Extrude011  label="top006"
  Base = -> Sketch013
  Dir = (0,0,1)
  DirMode = 2
  FaceMakerClass = Part::FaceMakerBullseye
  LengthFwd = 72
  LengthRev = 0
  Solid = true
  Symmetric = false
FEATURE [Sketcher::SketchObject] Sketch014
  FullyConstrained = true
  MapMode = 3
  Placement = pos=(0,0,0) rot=(1,0,0;1.5708rad)
  Support = -> [Extrude011]
  sketch-geometry (8):
    g0: Circle CenterX=80.351 CenterY=-67.6202 CenterZ=0 NormalX=0 NormalY=0 NormalZ=1 AngleXU=0 Radius=2
    g1: Circle CenterX=80.351 CenterY=-67.6202 CenterZ=0 NormalX=0 NormalY=0 NormalZ=1 AngleXU=0 Radius=3
    g2: Circle CenterX=80.351 CenterY=-4.92017 CenterZ=0 NormalX=0 NormalY=0 NormalZ=1 AngleXU=0 Radius=2
    g3: Circle CenterX=80.351 CenterY=-4.92017 CenterZ=0 NormalX=0 NormalY=0 NormalZ=1 AngleXU=0 Radius=3
    g4: Circle CenterX=23.851 CenterY=-4.92017 CenterZ=0 NormalX=0 NormalY=0 NormalZ=1 AngleXU=0 Radius=2
    g5: Circle CenterX=23.851 CenterY=-4.92017 CenterZ=0 NormalX=0 NormalY=0 NormalZ=1 AngleXU=0 Radius=3
    g6: Circle CenterX=23.851 CenterY=-67.6202 CenterZ=0 NormalX=0 NormalY=0 NormalZ=1 AngleXU=0 Radius=2
    g7: Circle CenterX=23.851 CenterY=-67.6202 CenterZ=0 NormalX=0 NormalY=0 NormalZ=1 AngleXU=0 Radius=3
  constraints (8):
    c: Block(g3)
    c: Block(g2)
    c: Block(g1)
    c: Block(g0)
    c: Block(g6)
    c: Block(g7)
    c: Block(g4)
    c: Block(g5)
FEATURE [Part::Feature] Face027
  shape: bbox 11 x 6 x 2e-07 mm, 1 faces, 0 solids (baked)
FEATURE [Part::Revolution] Revolve027
  Angle = 360
  Axis = (0,1,0)
  Base = (0,0,0)
  FaceMakerClass = Part::FaceMakerBullseye
  Placement = pos=(30.3,-1,51.7) rot=(0,0,1;0rad)
  Solid = false
  Source = -> Face027
  Symmetric = false
FEATURE [Part::Feature] Face028
  shape: bbox 11 x 6 x 2e-07 mm, 1 faces, 0 solids (baked)
FEATURE [Part::Revolution] Revolve028
  Angle = 360
  Axis = (0,1,0)
  Base = (0,0,0)
  FaceMakerClass = Part::FaceMakerBullseye
  Placement = pos=(62.3,-1,19.7) rot=(0,0,1;0rad)
  Solid = false
  Source = -> Face028
  Symmetric = false
FEATURE [Part::Feature] Face029
  shape: bbox 11 x 6 x 2e-07 mm, 1 faces, 0 solids (baked)
FEATURE [Part::Revolution] Revolve029
  Angle = 360
  Axis = (0,1,0)
  Base = (0,0,0)
  FaceMakerClass = Part::FaceMakerBullseye
  Placement = pos=(62.3,-1,51.7) rot=(0,0,1;0rad)
  Solid = false
  Source = -> Face029
  Symmetric = false
FEATURE [Part::Feature] Wire
  shape: bbox 11 x 5.2 x 2e-07 mm, 0 faces, 0 solids (baked)
FEATURE [Part::Revolution] Revolve030
  Angle = 360
  Axis = (0,1,0)
  Base = (0,0,0)
  FaceMakerClass = Part::FaceMakerBullseye
  Placement = pos=(30.3,38,19.7) rot=(0,0,1;0rad)
  Solid = true
  Source = -> Wire
  Symmetric = false
FEATURE [Part::Feature] Wire001
  shape: bbox 11 x 5.2 x 2e-07 mm, 0 faces, 0 solids (baked)
FEATURE [Part::Revolution] Revolve031
  Angle = 360
  Axis = (0,1,0)
  Base = (0,0,0)
  FaceMakerClass = Part::FaceMakerBullseye
  Placement = pos=(30.3,38,51.7) rot=(0,0,1;0rad)
  Solid = true
  Source = -> Wire001
  Symmetric = false
FEATURE [Part::Feature] Wire002
  shape: bbox 11 x 5.2 x 2e-07 mm, 0 faces, 0 solids (baked)
FEATURE [Part::Revolution] Revolve032
  Angle = 360
  Axis = (0,1,0)
  Base = (0,0,0)
  FaceMakerClass = Part::FaceMakerBullseye
  Placement = pos=(62.3,38,51.7) rot=(0,0,1;0rad)
  Solid = true
  Source = -> Wire002
  Symmetric = false
FEATURE [Part::Feature] Wire003
  shape: bbox 11 x 5.2 x 2e-07 mm, 0 faces, 0 solids (baked)
FEATURE [Part::Revolution] Revolve033
  Angle = 360
  Axis = (0,1,0)
  Base = (0,0,0)
  FaceMakerClass = Part::FaceMakerBullseye
  Placement = pos=(62.3,38,19.7) rot=(0,0,1;0rad)
  Solid = true
  Source = -> Wire003
  Symmetric = false
FEATURE [Part::MultiFuse] Fusion045  label="altRandScrewHousing"
  Shapes = -> [Revolve029,Revolve027,Revolve028,Revolve026]
FEATURE [Part::MultiFuse] Fusion046  label="fanScrewHousing"
  Shapes = -> [Revolve033,Revolve032,Revolve031,Revolve030]
FEATURE [Sketcher::SketchObject] Sketch015
  FullyConstrained = true
  sketch-geometry (17):
    g0: Circle CenterX=-3.5 CenterY=23.5 CenterZ=0 NormalX=0 NormalY=0 NormalZ=1 AngleXU=0 Radius=1
    g1: Circle CenterX=-1 CenterY=15.25 CenterZ=0 NormalX=0 NormalY=0 NormalZ=1 AngleXU=0 Radius=1
    g2: Circle CenterX=-3.5 CenterY=7 CenterZ=0 NormalX=0 NormalY=0 NormalZ=1 AngleXU=0 Radius=1
    g3: BSplineCurve PolesCount=3 KnotsCount=2 Degree=2 IsPeriodic=0
    g4: GeomPoint X=-3.5 Y=23.5 Z=0
    g5: GeomPoint X=-3.5 Y=7 Z=0
    g6: Circle CenterX=-4.8 CenterY=30.5 CenterZ=0 NormalX=0 NormalY=0 NormalZ=1 AngleXU=0 Radius=1
    g7: Circle CenterX=-3.5 CenterY=30.5 CenterZ=0 NormalX=0 NormalY=0 NormalZ=1 AngleXU=0 Radius=1
    g8: Circle CenterX=-3.5 CenterY=29.2 CenterZ=0 NormalX=0 NormalY=0 NormalZ=1 AngleXU=0 Radius=1
    g9: BSplineCurve PolesCount=3 KnotsCount=2 Degree=2 IsPeriodic=0
    g10: GeomPoint X=-4.8 Y=30.5 Z=0
    g11: GeomPoint X=-3.5 Y=29.2 Z=0
    g12: LineSegment StartX=-3.5 StartY=29.2 StartZ=0 EndX=-3.5 EndY=23.5 EndZ=0
    g13: LineSegment StartX=-4.8 StartY=30.5 StartZ=0 EndX=0 EndY=30.5 EndZ=0
    g14: LineSegment StartX=-3.5 StartY=0.3 StartZ=0 EndX=0 EndY=0.3 EndZ=0
    g15: LineSegment StartX=-3.5 StartY=0.3 StartZ=0 EndX=-3.5 EndY=7 EndZ=0
    g16: LineSegment StartX=0 StartY=0.3 StartZ=0 EndX=0 EndY=30.5 EndZ=0
  constraints (33):
    c: Weight(g0) = 1
    c: Equal(g0,g1)
    c: Equal(g0,g2)
    c: InternalAlignment(g0,g3)
    c: InternalAlignment(g1,g3)
    c: InternalAlignment(g2,g3)
    c: InternalAlignment(g4,g3)
    c: InternalAlignment(g5,g3)
    c: Block(g3)
    c: Weight(g6) = 1
    c: Equal(g6,g7)
    c: Equal(g6,g8)
    c: InternalAlignment(g6,g9)
    c: InternalAlignment(g7,g9)
    c: InternalAlignment(g8,g9)
    c: InternalAlignment(g10,g9)
    c: InternalAlignment(g11,g9)
    c: Block(g9)
    c: Coincident(g12,g9)
    c: Coincident(g12,g3)
    c: Vertical(g12)
    c: Coincident(g13,g9)
    c: Horizontal(g13)
    c: Distance(g13) = 4.8
    c: Horizontal(g14)
    c: Block(g14)
    c: Coincident(g15,g14)
    c: Coincident(g15,g3)
    c: Vertical(g15)
    c: Coincident(g16,g14)
    c: Coincident(g16,g13)
    c: Vertical(g16)
    c: Tangent(g16,g1)
FEATURE [Sketcher::SketchObject] Sketch016
  FullyConstrained = true
  sketch-geometry (16):
    g0: Circle CenterX=-3.5 CenterY=23.5 CenterZ=0 NormalX=0 NormalY=0 NormalZ=1 AngleXU=0 Radius=1
    g1: Circle CenterX=-1 CenterY=15.25 CenterZ=0 NormalX=0 NormalY=0 NormalZ=1 AngleXU=0 Radius=1
    g2: Circle CenterX=-3.5 CenterY=7 CenterZ=0 NormalX=0 NormalY=0 NormalZ=1 AngleXU=0 Radius=1
    g3: BSplineCurve PolesCount=3 KnotsCount=2 Degree=2 IsPeriodic=0
    g4: GeomPoint X=-3.5 Y=23.5 Z=0
    g5: GeomPoint X=-3.5 Y=7 Z=0
    g6: LineSegment StartX=-3.5 StartY=28.2 StartZ=0 EndX=-3.5 EndY=23.5 EndZ=0
    g7: LineSegment StartX=0 StartY=29.5 StartZ=0 EndX=0 EndY=30 EndZ=0
    g8: LineSegment StartX=-3.5 StartY=28.2 StartZ=0 EndX=-3.5 EndY=30 EndZ=0
    g9: LineSegment StartX=0 StartY=30 StartZ=0 EndX=0 EndY=30.5 EndZ=0
    g10: LineSegment StartX=0 StartY=30.5 StartZ=0 EndX=-3.5 EndY=30.5 EndZ=0
    g11: LineSegment StartX=-3.5 StartY=30.5 StartZ=0 EndX=-3.5 EndY=30 EndZ=0
    g12: LineSegment StartX=0 StartY=29.5 StartZ=0 EndX=0 EndY=5 EndZ=0
    g13: LineSegment StartX=-3.5 StartY=0.3 StartZ=0 EndX=-3.5 EndY=7 EndZ=0
    g14: LineSegment StartX=-3.5 StartY=0.3 StartZ=0 EndX=0 EndY=0.3 EndZ=0
    g15: LineSegment StartX=0 StartY=5 StartZ=0 EndX=0 EndY=0.3 EndZ=0
  constraints (39):
    c: Weight(g0) = 1
    c: Equal(g0,g1)
    c: Equal(g0,g2)
    c: InternalAlignment(g0,g3)
    c: InternalAlignment(g1,g3)
    c: InternalAlignment(g2,g3)
    c: InternalAlignment(g4,g3)
    c: InternalAlignment(g5,g3)
    c: Block(g3)
    c: Coincident(g6,g3)
    c: Vertical(g6)
    c: Vertical(g7)
    c: Distance(g7) = 0.5
    c: Coincident(g8,g6)
    c: Vertical(g8)
    c: Block(g6)
    c: Block(g7)
    c: Vertical(g9)
    c: Equal(g7,g9) = 0.5
    c: Block(g9)
    c: Coincident(g9,g7)
    c: Horizontal(g10)
    c: Coincident(g10,g9)
    c: Coincident(g11,g10)
    c: Coincident(g11,g8)
    c: Vertical(g11)
    c: Block(g11)
    c: Coincident(g12,g7)
    c: Vertical(g12)
    c: Coincident(g13,g3)
    c: Vertical(g13)
    c: Distance(g13) = 6.7
    c: Coincident(g14,g13)
    c: Horizontal(g14)
    c: Block(g14)
    c: Coincident(g15,g12)
    c: Coincident(g15,g14)
    c: Vertical(g15)
    c: Block(g15)
FEATURE [Sketcher::SketchObject] Sketch017
  FullyConstrained = true
  sketch-geometry (11):
    g0: LineSegment StartX=-3.5 StartY=1e-16 StartZ=0 EndX=-1.6 EndY=1e-16 EndZ=0
    g1: LineSegment StartX=-1.6 StartY=1e-16 StartZ=0 EndX=-1.6 EndY=1.5 EndZ=0
    g2: LineSegment StartX=-3.5 StartY=1.5 StartZ=0 EndX=-1.6 EndY=1.5 EndZ=0
    g3: LineSegment StartX=-3.5 StartY=1e-16 StartZ=0 EndX=-4.8 EndY=1e-16 EndZ=0
    g4: Circle CenterX=-3.5 CenterY=1.3 CenterZ=0 NormalX=0 NormalY=0 NormalZ=1 AngleXU=0 Radius=1
    g5: Circle CenterX=-3.5 CenterY=1e-16 CenterZ=0 NormalX=0 NormalY=0 NormalZ=1 AngleXU=0 Radius=1
    g6: Circle CenterX=-4.8 CenterY=1e-16 CenterZ=0 NormalX=0 NormalY=0 NormalZ=1 AngleXU=0 Radius=1
    g7: BSplineCurve PolesCount=3 KnotsCount=2 Degree=2 IsPeriodic=0
    g8: GeomPoint X=-3.5 Y=1.3 Z=0
    g9: GeomPoint X=-4.8 Y=1e-16 Z=0
    g10: LineSegment StartX=-3.5 StartY=1.3 StartZ=0 EndX=-3.5 EndY=1.5 EndZ=0
  constraints (24):
    c: Horizontal(g0)
    c: Distance(g0) = 1.9
    c: Block(g0)
    c: Coincident(g1,g0)
    c: Vertical(g1)
    c: Coincident(g2,g1)
    c: Horizontal(g2)
    c: Coincident(g3,g0)
    c: Horizontal(g3)
    c: Distance(g3) = 1.3
    c: Weight(g4) = 1
    c: Equal(g4,g5)
    c: Coincident(g5,g0)
    c: Equal(g4,g6)
    c: Coincident(g7,g3)
    c: InternalAlignment(g4,g7)
    c: InternalAlignment(g5,g7)
    c: InternalAlignment(g6,g7)
    c: InternalAlignment(g8,g7)
    c: InternalAlignment(g9,g7)
    c: Coincident(g10,g7)
    c: Coincident(g10,g2)
    c: Vertical(g10)
    c: Block(g10)
FEATURE [Part::Feature] Face035
  shape: bbox 3.2 x 1.5 x 2e-07 mm, 1 faces, 0 solids (baked)
FEATURE [Part::Revolution] Revolve039  label="backCaseScrewRetainer"
  Angle = 360
  Axis = (0,1,0)
  Base = (0,0,0)
  FaceMakerClass = Part::FaceMakerBullseye
  Placement = pos=(12.5,3,62) rot=(0,0,1;0rad)
  Solid = false
  Source = -> Face035
  Symmetric = false
FEATURE [Part::Feature] Face036
  shape: bbox 3.2 x 1.5 x 2e-07 mm, 1 faces, 0 solids (baked)
FEATURE [Part::Feature] Face039
  shape: bbox 4.8 x 30.2 x 2e-07 mm, 1 faces, 0 solids (baked)
FEATURE [Part::Revolution] Revolve043  label="frontCaseScrewPost002"
  Angle = 360
  Axis = (0,1,0)
  Base = (0,0,0)
  FaceMakerClass = Part::FaceMakerBullseye
  Placement = pos=(89.5,4.5,3.5) rot=(0,0,1;0rad)
  Solid = false
  Source = -> Face039
  Symmetric = false
FEATURE [Part::Feature] Face042
  shape: bbox 4.8 x 30.2 x 2e-07 mm, 1 faces, 0 solids (baked)
FEATURE [Part::Revolution] Revolve046  label="frontCaseScrewPost003"
  Angle = 360
  Axis = (0,1,0)
  Base = (0,0,0)
  FaceMakerClass = Part::FaceMakerBullseye
  Placement = pos=(89.5,4.5,68.5) rot=(0,0,1;0rad)
  Solid = false
  Source = -> Face042
  Symmetric = false
FEATURE [Part::Feature] Face043
  shape: bbox 3.2 x 1.5 x 2e-07 mm, 1 faces, 0 solids (baked)
FEATURE [Part::Revolution] Revolve047  label="frontCaseScrewRetainer002"
  Angle = 360
  Axis = (0,1,0)
  Base = (0,0,0)
  FaceMakerClass = Part::FaceMakerBullseye
  Placement = pos=(89.5,3,68.5) rot=(0,0,1;0rad)
  Solid = false
  Source = -> Face043
  Symmetric = false
FEATURE [Part::Feature] Face044
  shape: bbox 3.2 x 1.5 x 2e-07 mm, 1 faces, 0 solids (baked)
FEATURE [Part::Revolution] Revolve048  label="frontCaseScrewRetainer003"
  Angle = 360
  Axis = (0,1,0)
  Base = (0,0,0)
  FaceMakerClass = Part::FaceMakerBullseye
  Placement = pos=(89.5,3,3.5) rot=(0,0,1;0rad)
  Solid = false
  Source = -> Face044
  Symmetric = false
FEATURE [App::MeasureDistance] Distance002  label="Distance: 1.67 mm"
  Distance = 1.66921
  P1 = (99.2361,4.7524,71.7)
  P2 = (99.2347,6.42161,71.7)
FEATURE [Sketcher::SketchObject] Sketch018
  FullyConstrained = true
  sketch-geometry (7):
    g0: LineSegment StartX=0 StartY=0 StartZ=0 EndX=0 EndY=6 EndZ=0
    g1: Circle CenterX=0 CenterY=0 CenterZ=0 NormalX=0 NormalY=0 NormalZ=1 AngleXU=0 Radius=1
    g2: Circle CenterX=8 CenterY=6 CenterZ=0 NormalX=0 NormalY=0 NormalZ=1 AngleXU=0 Radius=1
    g3: BSplineCurve PolesCount=3 KnotsCount=2 Degree=2 IsPeriodic=0
    g4: GeomPoint X=0 Y=0 Z=0
    g5: GeomPoint X=8 Y=6 Z=0
    g6: LineSegment StartX=0 StartY=6 StartZ=0 EndX=8 EndY=6 EndZ=0
  constraints (14):
    c: Coincident(g0,g-1)
    c: Distance(g0) = 6
    c: Vertical(g0)
    c: Coincident(g3,g0)
    c: Weight(g1) = 1
    c: Equal(g1,g2)
    c: InternalAlignment(g1,g3)
    c: InternalAlignment(g2,g3)
    c: InternalAlignment(g4,g3)
    c: InternalAlignment(g5,g3)
    c: Block(g3)
    c: Coincident(g6,g0)
    c: Coincident(g6,g3)
    c: Horizontal(g6)
FEATURE [Part::Extrusion] Extrude012  label="caseScrewPillarBracket"
  Base = -> Sketch018
  Dir = (0,0,1)
  DirMode = 2
  FaceMakerClass = Part::FaceMakerBullseye
  LengthFwd = 2.4
  LengthRev = 0
  Placement = pos=(15.76,29,8.8) rot=(0,1,0;0rad)
  Solid = true
  Symmetric = false
FEATURE [Sketcher::SketchObject] Sketch019
  FullyConstrained = true
  sketch-geometry (7):
    g0: LineSegment StartX=0 StartY=0 StartZ=0 EndX=0 EndY=6 EndZ=0
    g1: Circle CenterX=0 CenterY=0 CenterZ=0 NormalX=0 NormalY=0 NormalZ=1 AngleXU=0 Radius=1
    g2: Circle CenterX=8 CenterY=6 CenterZ=0 NormalX=0 NormalY=0 NormalZ=1 AngleXU=0 Radius=1
    g3: BSplineCurve PolesCount=3 KnotsCount=2 Degree=2 IsPeriodic=0
    g4: GeomPoint X=0 Y=0 Z=0
    g5: GeomPoint X=8 Y=6 Z=0
    g6: LineSegment StartX=0 StartY=6 StartZ=0 EndX=8 EndY=6 EndZ=0
  constraints (14):
    c: Coincident(g0,g-1)
    c: Distance(g0) = 6
    c: Vertical(g0)
    c: Coincident(g3,g0)
    c: Weight(g1) = 1
    c: Equal(g1,g2)
    c: InternalAlignment(g1,g3)
    c: InternalAlignment(g2,g3)
    c: InternalAlignment(g4,g3)
    c: InternalAlignment(g5,g3)
    c: Block(g3)
    c: Coincident(g6,g0)
    c: Coincident(g6,g3)
    c: Horizontal(g6)
FEATURE [Part::Extrusion] Extrude013  label="caseScrewPillarBracket001"
  Base = -> Sketch019
  Dir = (0,0,1)
  DirMode = 2
  FaceMakerClass = Part::FaceMakerBullseye
  LengthFwd = 2.4
  LengthRev = 0
  Placement = pos=(15.76,29,60.8) rot=(0,0,1;0rad)
  Solid = true
  Symmetric = false
FEATURE [Sketcher::SketchObject] Sketch020
  FullyConstrained = true
  sketch-geometry (7):
    g0: LineSegment StartX=0 StartY=0 StartZ=0 EndX=0 EndY=6 EndZ=0
    g1: Circle CenterX=0 CenterY=0 CenterZ=0 NormalX=0 NormalY=0 NormalZ=1 AngleXU=0 Radius=1
    g2: Circle CenterX=8 CenterY=6 CenterZ=0 NormalX=0 NormalY=0 NormalZ=1 AngleXU=0 Radius=1
    g3: BSplineCurve PolesCount=3 KnotsCount=2 Degree=2 IsPeriodic=0
    g4: GeomPoint X=0 Y=0 Z=0
    g5: GeomPoint X=8 Y=6 Z=0
    g6: LineSegment StartX=0 StartY=6 StartZ=0 EndX=8 EndY=6 EndZ=0
  constraints (14):
    c: Coincident(g0,g-1)
    c: Distance(g0) = 6
    c: Vertical(g0)
    c: Coincident(g3,g0)
    c: Weight(g1) = 1
    c: Equal(g1,g2)
    c: InternalAlignment(g1,g3)
    c: InternalAlignment(g2,g3)
    c: InternalAlignment(g4,g3)
    c: InternalAlignment(g5,g3)
    c: Block(g3)
    c: Coincident(g6,g0)
    c: Coincident(g6,g3)
    c: Horizontal(g6)
FEATURE [Part::Extrusion] Extrude014  label="caseScrewPillarBracket002"
  Base = -> Sketch020
  Dir = (0,0,1)
  DirMode = 2
  FaceMakerClass = Part::FaceMakerBullseye
  LengthFwd = 2.4
  LengthRev = 0
  Placement = pos=(13.7,29,13.26) rot=(0,-1,0;1.5708rad)
  Solid = true
  Symmetric = false
FEATURE [Sketcher::SketchObject] Sketch021
  FullyConstrained = true
  sketch-geometry (7):
    g0: LineSegment StartX=0 StartY=0 StartZ=0 EndX=0 EndY=6 EndZ=0
    g1: Circle CenterX=0 CenterY=0 CenterZ=0 NormalX=0 NormalY=0 NormalZ=1 AngleXU=0 Radius=1
    g2: Circle CenterX=8 CenterY=6 CenterZ=0 NormalX=0 NormalY=0 NormalZ=1 AngleXU=0 Radius=1
    g3: BSplineCurve PolesCount=3 KnotsCount=2 Degree=2 IsPeriodic=0
    g4: GeomPoint X=0 Y=0 Z=0
    g5: GeomPoint X=8 Y=6 Z=0
    g6: LineSegment StartX=0 StartY=6 StartZ=0 EndX=8 EndY=6 EndZ=0
  constraints (14):
    c: Coincident(g0,g-1)
    c: Distance(g0) = 6
    c: Vertical(g0)
    c: Coincident(g3,g0)
    c: Weight(g1) = 1
    c: Equal(g1,g2)
    c: InternalAlignment(g1,g3)
    c: InternalAlignment(g2,g3)
    c: InternalAlignment(g4,g3)
    c: InternalAlignment(g5,g3)
    c: Block(g3)
    c: Coincident(g6,g0)
    c: Coincident(g6,g3)
    c: Horizontal(g6)
FEATURE [Part::Extrusion] Extrude015  label="caseScrewPillarBracket003"
  Base = -> Sketch021
  Dir = (0,0,1)
  DirMode = 2
  FaceMakerClass = Part::FaceMakerBullseye
  LengthFwd = 2.4
  LengthRev = 0
  Placement = pos=(11.3,29,58.74) rot=(0,1,0;1.5708rad)
  Solid = true
  Symmetric = false
FEATURE [Sketcher::SketchObject] Sketch022
  FullyConstrained = true
  sketch-geometry (7):
    g0: LineSegment StartX=0 StartY=0 StartZ=0 EndX=0 EndY=6 EndZ=0
    g1: Circle CenterX=0 CenterY=0 CenterZ=0 NormalX=0 NormalY=0 NormalZ=1 AngleXU=0 Radius=1
    g2: Circle CenterX=8 CenterY=6 CenterZ=0 NormalX=0 NormalY=0 NormalZ=1 AngleXU=0 Radius=1
    g3: BSplineCurve PolesCount=3 KnotsCount=2 Degree=2 IsPeriodic=0
    g4: GeomPoint X=0 Y=0 Z=0
    g5: GeomPoint X=8 Y=6 Z=0
    g6: LineSegment StartX=0 StartY=6 StartZ=0 EndX=8 EndY=6 EndZ=0
  constraints (14):
    c: Coincident(g0,g-1)
    c: Distance(g0) = 6
    c: Vertical(g0)
    c: Coincident(g3,g0)
    c: Weight(g1) = 1
    c: Equal(g1,g2)
    c: InternalAlignment(g1,g3)
    c: InternalAlignment(g2,g3)
    c: InternalAlignment(g4,g3)
    c: InternalAlignment(g5,g3)
    c: Block(g3)
    c: Coincident(g6,g0)
    c: Coincident(g6,g3)
    c: Horizontal(g6)
FEATURE [Part::Extrusion] Extrude016  label="caseScrewPillarBracket004"
  Base = -> Sketch022
  Dir = (0,0,1)
  DirMode = 2
  FaceMakerClass = Part::FaceMakerBullseye
  LengthFwd = 2.4
  LengthRev = 0
  Placement = pos=(88.3,29,65.23) rot=(0,1,0;1.5708rad)
  Solid = true
  Symmetric = false
FEATURE [Sketcher::SketchObject] Sketch023
  FullyConstrained = true
  sketch-geometry (7):
    g0: LineSegment StartX=0 StartY=0 StartZ=0 EndX=0 EndY=6 EndZ=0
    g1: Circle CenterX=0 CenterY=0 CenterZ=0 NormalX=0 NormalY=0 NormalZ=1 AngleXU=0 Radius=1
    g2: Circle CenterX=8 CenterY=6 CenterZ=0 NormalX=0 NormalY=0 NormalZ=1 AngleXU=0 Radius=1
    g3: BSplineCurve PolesCount=3 KnotsCount=2 Degree=2 IsPeriodic=0
    g4: GeomPoint X=0 Y=0 Z=0
    g5: GeomPoint X=8 Y=6 Z=0
    g6: LineSegment StartX=0 StartY=6 StartZ=0 EndX=8 EndY=6 EndZ=0
  constraints (14):
    c: Coincident(g0,g-1)
    c: Distance(g0) = 6
    c: Vertical(g0)
    c: Coincident(g3,g0)
    c: Weight(g1) = 1
    c: Equal(g1,g2)
    c: InternalAlignment(g1,g3)
    c: InternalAlignment(g2,g3)
    c: InternalAlignment(g4,g3)
    c: InternalAlignment(g5,g3)
    c: Block(g3)
    c: Coincident(g6,g0)
    c: Coincident(g6,g3)
    c: Horizontal(g6)
FEATURE [Part::Extrusion] Extrude017  label="caseScrewPillarBracket005"
  Base = -> Sketch023
  Dir = (0,0,1)
  DirMode = 2
  FaceMakerClass = Part::FaceMakerBullseye
  LengthFwd = 2.4
  LengthRev = 0
  Placement = pos=(90.7,29,6.77) rot=(0,-1,0;1.5708rad)
  Solid = true
  Symmetric = false
FEATURE [Sketcher::SketchObject] Sketch024
  FullyConstrained = true
  sketch-geometry (7):
    g0: LineSegment StartX=0 StartY=0 StartZ=0 EndX=0 EndY=6 EndZ=0
    g1: Circle CenterX=0 CenterY=0 CenterZ=0 NormalX=0 NormalY=0 NormalZ=1 AngleXU=0 Radius=1
    g2: Circle CenterX=8 CenterY=6 CenterZ=0 NormalX=0 NormalY=0 NormalZ=1 AngleXU=0 Radius=1
    g3: BSplineCurve PolesCount=3 KnotsCount=2 Degree=2 IsPeriodic=0
    g4: GeomPoint X=0 Y=0 Z=0
    g5: GeomPoint X=8 Y=6 Z=0
    g6: LineSegment StartX=0 StartY=6 StartZ=0 EndX=8 EndY=6 EndZ=0
  constraints (14):
    c: Coincident(g0,g-1)
    c: Distance(g0) = 6
    c: Vertical(g0)
    c: Coincident(g3,g0)
    c: Weight(g1) = 1
    c: Equal(g1,g2)
    c: InternalAlignment(g1,g3)
    c: InternalAlignment(g2,g3)
    c: InternalAlignment(g4,g3)
    c: InternalAlignment(g5,g3)
    c: Block(g3)
    c: Coincident(g6,g0)
    c: Coincident(g6,g3)
    c: Horizontal(g6)
FEATURE [Part::Extrusion] Extrude018  label="caseScrewPillarBracket006"
  Base = -> Sketch024
  Dir = (0,0,1)
  DirMode = 2
  FaceMakerClass = Part::FaceMakerBullseye
  LengthFwd = 2.4
  LengthRev = 0
  Placement = pos=(103.7,29,6.77) rot=(0,-1,0;1.5708rad)
  Solid = true
  Symmetric = false
FEATURE [Sketcher::SketchObject] Sketch025
  FullyConstrained = true
  sketch-geometry (7):
    g0: LineSegment StartX=0 StartY=0 StartZ=0 EndX=0 EndY=6 EndZ=0
    g1: Circle CenterX=0 CenterY=0 CenterZ=0 NormalX=0 NormalY=0 NormalZ=1 AngleXU=0 Radius=1
    g2: Circle CenterX=8 CenterY=6 CenterZ=0 NormalX=0 NormalY=0 NormalZ=1 AngleXU=0 Radius=1
    g3: BSplineCurve PolesCount=3 KnotsCount=2 Degree=2 IsPeriodic=0
    g4: GeomPoint X=0 Y=0 Z=0
    g5: GeomPoint X=8 Y=6 Z=0
    g6: LineSegment StartX=0 StartY=6 StartZ=0 EndX=8 EndY=6 EndZ=0
  constraints (14):
    c: Coincident(g0,g-1)
    c: Distance(g0) = 6
    c: Vertical(g0)
    c: Coincident(g3,g0)
    c: Weight(g1) = 1
    c: Equal(g1,g2)
    c: InternalAlignment(g1,g3)
    c: InternalAlignment(g2,g3)
    c: InternalAlignment(g4,g3)
    c: InternalAlignment(g5,g3)
    c: Block(g3)
    c: Coincident(g6,g0)
    c: Coincident(g6,g3)
    c: Horizontal(g6)
FEATURE [Part::Extrusion] Extrude019  label="caseScrewPillarBracket007"
  Base = -> Sketch025
  Dir = (0,0,1)
  DirMode = 2
  FaceMakerClass = Part::FaceMakerBullseye
  LengthFwd = 2.4
  LengthRev = 0
  Placement = pos=(101.3,29,65.23) rot=(0,1,0;1.5708rad)
  Solid = true
  Symmetric = false
FEATURE [Part::Box] Box011  label="frontCaseScrewPillarBracket"
  AttacherType = Attacher::AttachEngine3D
  Height = 2.4
  Length = 16
  Placement = pos=(87,28,2.3) rot=(0,0,1;0rad)
  Width = 7
FEATURE [Part::Box] Box012  label="frontCaseScrewPillarBracket001"
  AttacherType = Attacher::AttachEngine3D
  Height = 2.4
  Length = 16
  Placement = pos=(87,28,67.3) rot=(0,0,1;0rad)
  Width = 7
FEATURE [Sketcher::SketchObject] Sketch026
  FullyConstrained = true
  sketch-geometry (17):
    g0: Circle CenterX=-3.5 CenterY=23.5 CenterZ=0 NormalX=0 NormalY=0 NormalZ=1 AngleXU=0 Radius=1
    g1: Circle CenterX=-1 CenterY=15.25 CenterZ=0 NormalX=0 NormalY=0 NormalZ=1 AngleXU=0 Radius=1
    g2: Circle CenterX=-3.5 CenterY=7 CenterZ=0 NormalX=0 NormalY=0 NormalZ=1 AngleXU=0 Radius=1
    g3: BSplineCurve PolesCount=3 KnotsCount=2 Degree=2 IsPeriodic=0
    g4: GeomPoint X=-3.5 Y=23.5 Z=0
    g5: GeomPoint X=-3.5 Y=7 Z=0
    g6: Circle CenterX=-4.8 CenterY=30.5 CenterZ=0 NormalX=0 NormalY=0 NormalZ=1 AngleXU=0 Radius=1
    g7: Circle CenterX=-3.5 CenterY=30.5 CenterZ=0 NormalX=0 NormalY=0 NormalZ=1 AngleXU=0 Radius=1
    g8: Circle CenterX=-3.5 CenterY=29.2 CenterZ=0 NormalX=0 NormalY=0 NormalZ=1 AngleXU=0 Radius=1
    g9: BSplineCurve PolesCount=3 KnotsCount=2 Degree=2 IsPeriodic=0
    g10: GeomPoint X=-4.8 Y=30.5 Z=0
    g11: GeomPoint X=-3.5 Y=29.2 Z=0
    g12: LineSegment StartX=-3.5 StartY=29.2 StartZ=0 EndX=-3.5 EndY=23.5 EndZ=0
    g13: LineSegment StartX=-4.8 StartY=30.5 StartZ=0 EndX=0 EndY=30.5 EndZ=0
    g14: LineSegment StartX=-3.5 StartY=5 StartZ=0 EndX=-3.5 EndY=7 EndZ=0
    g15: LineSegment StartX=0 StartY=5 StartZ=0 EndX=0 EndY=30.5 EndZ=0
    g16: LineSegment StartX=-3.5 StartY=5 StartZ=0 EndX=0 EndY=5 EndZ=0
  constraints (33):
    c: Weight(g0) = 1
    c: Equal(g0,g1)
    c: Equal(g0,g2)
    c: InternalAlignment(g0,g3)
    c: InternalAlignment(g1,g3)
    c: InternalAlignment(g2,g3)
    c: InternalAlignment(g4,g3)
    c: InternalAlignment(g5,g3)
    c: Block(g3)
    c: Weight(g6) = 1
    c: Equal(g6,g7)
    c: Equal(g6,g8)
    c: InternalAlignment(g6,g9)
    c: InternalAlignment(g7,g9)
    c: InternalAlignment(g8,g9)
    c: InternalAlignment(g10,g9)
    c: InternalAlignment(g11,g9)
    c: Block(g9)
    c: Coincident(g12,g9)
    c: Coincident(g12,g3)
    c: Vertical(g12)
    c: Coincident(g13,g9)
    c: Horizontal(g13)
    c: Distance(g13) = 4.8
    c: Coincident(g14,g3)
    c: Vertical(g14)
    c: Coincident(g15,g13)
    c: Vertical(g15)
    c: Tangent(g15,g1)
    c: Distance(g14) = 2
    c: Coincident(g16,g14)
    c: Horizontal(g16)
    c: Coincident(g15,g16)
FEATURE [Part::Feature] Face050
  shape: bbox 4.8 x 25.5 x 2e-07 mm, 1 faces, 0 solids (baked)
FEATURE [Part::Revolution] Revolve054  label="moreFrontCaseScrewPost001"
  Angle = 360
  Axis = (0,1,0)
  Base = (0,0,0)
  FaceMakerClass = Part::FaceMakerBullseye
  Placement = pos=(102.5,4.5,3.5) rot=(0,0,1;0rad)
  Solid = false
  Source = -> Face050
  Symmetric = false
FEATURE [Part::Feature] Face051
  shape: bbox 4.8 x 25.5 x 2e-07 mm, 1 faces, 0 solids (baked)
FEATURE [Part::Revolution] Revolve055  label="moreFrontCaseScrewPost002"
  Angle = 360
  Axis = (0,1,0)
  Base = (0,0,0)
  FaceMakerClass = Part::FaceMakerBullseye
  Placement = pos=(102.5,4.5,68.5) rot=(0,0,1;0rad)
  Solid = false
  Source = -> Face051
  Symmetric = false
FEATURE [Sketcher::SketchObject] Sketch027
  FullyConstrained = true
  sketch-geometry (10):
    g0: LineSegment StartX=-1.6 StartY=4.7 StartZ=0 EndX=-1.6 EndY=1.7 EndZ=0
    g1: LineSegment StartX=-3.5 StartY=4.7 StartZ=0 EndX=-1.6 EndY=4.7 EndZ=0
    g2: LineSegment StartX=-1.6 StartY=1.7 StartZ=0 EndX=-1.6 EndY=1.5 EndZ=0
    g3: LineSegment StartX=-1.6 StartY=1.5 StartZ=0 EndX=-5.2 EndY=1.5 EndZ=0
    g4: Circle CenterX=-3.5 CenterY=4.7 CenterZ=0 NormalX=0 NormalY=0 NormalZ=1 AngleXU=0 Radius=1
    g5: Circle CenterX=-3.59627 CenterY=2.99743 CenterZ=0 NormalX=0 NormalY=0 NormalZ=1 AngleXU=0 Radius=1
    g6: Circle CenterX=-5.2 CenterY=1.5 CenterZ=0 NormalX=0 NormalY=0 NormalZ=1 AngleXU=0 Radius=1
    g7: BSplineCurve PolesCount=3 KnotsCount=2 Degree=2 IsPeriodic=0
    g8: GeomPoint X=-3.5 Y=4.7 Z=0
    g9: GeomPoint X=-5.2 Y=1.5 Z=0
  constraints (23):
    c: Vertical(g0)
    c: Distance(g0) = 3
    c: Coincident(g1,g0)
    c: Horizontal(g1)
    c: Block(g0)
    c: Block(g1)
    c: Coincident(g2,g0)
    c: Vertical(g2)
    c: Distance(g2) = 0.2
    c: Coincident(g3,g2)
    c: Horizontal(g3)
    c: Block(g3)
    c: Coincident(g7,g1)
    c: Weight(g4) = 1
    c: Equal(g4,g5)
    c: Equal(g4,g6)
    c: Coincident(g7,g3)
    c: InternalAlignment(g4,g7)
    c: InternalAlignment(g5,g7)
    c: InternalAlignment(g6,g7)
    c: InternalAlignment(g8,g7)
    c: InternalAlignment(g9,g7)
    c: Block(g7)
FEATURE [Sketcher::SketchObject] Sketch028
  FullyConstrained = true
  sketch-geometry (18):
    g0: LineSegment StartX=0 StartY=3e-16 StartZ=0 EndX=0 EndY=1.7 EndZ=0
    g1: LineSegment StartX=-3.5 StartY=0 StartZ=0 EndX=-3.5 EndY=0.9 EndZ=0
    g2: Circle CenterX=-2.7 CenterY=1.7 CenterZ=0 NormalX=0 NormalY=0 NormalZ=1 AngleXU=0 Radius=1
    g3: Circle CenterX=-3.5 CenterY=1.7 CenterZ=0 NormalX=0 NormalY=0 NormalZ=1 AngleXU=0 Radius=1
    g4: Circle CenterX=-3.5 CenterY=0.9 CenterZ=0 NormalX=0 NormalY=0 NormalZ=1 AngleXU=0 Radius=1
    g5: BSplineCurve PolesCount=3 KnotsCount=2 Degree=2 IsPeriodic=0
    g6: GeomPoint X=-2.7 Y=1.7 Z=0
    g7: GeomPoint X=-3.5 Y=0.9 Z=0
    g8: LineSegment StartX=-3.5 StartY=0 StartZ=0 EndX=-3.5 EndY=-7 EndZ=0
    g9: LineSegment StartX=0 StartY=3e-16 StartZ=0 EndX=0 EndY=-7 EndZ=0
    g10: LineSegment StartX=-3.5 StartY=-7 StartZ=0 EndX=0 EndY=-7 EndZ=0
    g11: LineSegment StartX=-2.7 StartY=1.7 StartZ=0 EndX=-1.6 EndY=1.7 EndZ=0
    g12: LineSegment StartX=0 StartY=1.7 StartZ=0 EndX=0 EndY=4.5 EndZ=0
    g13: LineSegment StartX=0 StartY=4.5 StartZ=0 EndX=0 EndY=10.8 EndZ=0
    g14: LineSegment StartX=0 StartY=10.8 StartZ=0 EndX=-2 EndY=10.8 EndZ=0
    g15: LineSegment StartX=-1.6 StartY=4.7 StartZ=0 EndX=-1.6 EndY=1.7 EndZ=0
    g16: LineSegment StartX=-1.6 StartY=4.7 StartZ=0 EndX=-2 EndY=4.7 EndZ=0
    g17: LineSegment StartX=-2 StartY=4.7 StartZ=0 EndX=-2 EndY=10.8 EndZ=0
  constraints (44):
    c: Vertical(g0)
    c: Vertical(g1)
    c: Distance(g1) = 0.9
    c: Block(g0)
    c: Distance(g0) = 1.7
    c: Weight(g2) = 1
    c: Equal(g2,g3)
    c: Equal(g2,g4)
    c: Coincident(g5,g1)
    c: InternalAlignment(g2,g5)
    c: InternalAlignment(g3,g5)
    c: InternalAlignment(g4,g5)
    c: InternalAlignment(g6,g5)
    c: InternalAlignment(g7,g5)
    c: Block(g5)
    c: Coincident(g8,g1)
    c: Vertical(g8)
    c: Distance(g8) = 7
    c: Vertical(g9)
    c: Equal(g8,g9) = 7
    c: Coincident(g9,g0)
    c: Coincident(g10,g8)
    c: Coincident(g10,g9)
    c: Horizontal(g10)
    c: Coincident(g11,g5)
    c: Horizontal(g11)
    c: Coincident(g12,g0)
    c: Vertical(g12)
    c: Distance(g12) = 2.8
    c: Coincident(g13,g12)
    c: Vertical(g13)
    c: Distance(g13) = 6.3
    c: Coincident(g14,g13)
    c: Horizontal(g14)
    c: Distance(g14) = 2
    c: Vertical(g15)
    c: Distance(g15) = 3
    c: Block(g11)
    c: Coincident(g15,g11)
    c: Coincident(g16,g15)
    c: Horizontal(g16)
    c: Coincident(g17,g16)
    c: Coincident(g17,g14)
    c: Vertical(g17)
FEATURE [Part::Revolution] Revolve040  label="backCaseScrewRetainer001"
  Angle = 360
  Axis = (0,1,0)
  Base = (0,0,0)
  FaceMakerClass = Part::FaceMakerBullseye
  Placement = pos=(12.5,3,10) rot=(0,0,1;0rad)
  Solid = false
  Source = -> Face036
  Symmetric = false
FEATURE [Part::Feature] Face055
  shape: bbox 3.5 x 30.2 x 2e-07 mm, 1 faces, 0 solids (baked)
FEATURE [Part::Revolution] Revolve059  label="backCaseScrewPost"
  Angle = 360
  Axis = (0,1,0)
  Base = (0,0,0)
  FaceMakerClass = Part::FaceMakerBullseye
  Placement = pos=(12.5,4.5,10) rot=(0,0,1;0rad)
  Solid = false
  Source = -> Face055
  Symmetric = false
FEATURE [Part::Feature] Face056
  shape: bbox 3.5 x 30.2 x 2e-07 mm, 1 faces, 0 solids (baked)
FEATURE [Part::Revolution] Revolve060  label="backCaseScrewPost001"
  Angle = 360
  Axis = (0,1,0)
  Base = (0,0,0)
  FaceMakerClass = Part::FaceMakerBullseye
  Placement = pos=(12.5,4.5,62) rot=(0,0,1;0rad)
  Solid = false
  Source = -> Face056
  Symmetric = false
FEATURE [Part::Feature] Face057
  shape: bbox 3.5 x 17.8 x 2e-07 mm, 1 faces, 0 solids (baked)
FEATURE [Part::Revolution] Revolve061  label="removeToCreateScrewAndThreadedInsertHole"
  Angle = 360
  Axis = (0,1,0)
  Base = (0,0,0)
  FaceMakerClass = Part::FaceMakerBullseye
  Placement = pos=(12.5,0,10) rot=(0,0,1;0rad)
  Solid = false
  Source = -> Face057
  Symmetric = false
FEATURE [Part::Feature] Face058
  shape: bbox 3.5 x 17.8 x 2e-07 mm, 1 faces, 0 solids (baked)
FEATURE [Part::Revolution] Revolve062  label="removeToCreateScrewAndThreadedInsertHole001"
  Angle = 360
  Axis = (0,1,0)
  Base = (0,0,0)
  FaceMakerClass = Part::FaceMakerBullseye
  Placement = pos=(12.5,0,62) rot=(0,0,1;0rad)
  Solid = false
  Source = -> Face058
  Symmetric = false
FEATURE [Part::Feature] Face059
  shape: bbox 3.5 x 17.8 x 2e-07 mm, 1 faces, 0 solids (baked)
FEATURE [Part::Revolution] Revolve063  label="removeToCreateScrewAndThreadedInsertHole002"
  Angle = 360
  Axis = (0,1,0)
  Base = (0,0,0)
  FaceMakerClass = Part::FaceMakerBullseye
  Placement = pos=(89.5,0,68.5) rot=(0,0,1;0rad)
  Solid = false
  Source = -> Face059
  Symmetric = false
FEATURE [Part::Feature] Face060
  shape: bbox 3.5 x 17.8 x 2e-07 mm, 1 faces, 0 solids (baked)
FEATURE [Part::Revolution] Revolve064  label="removeToCreateScrewAndThreadedInsertHole003"
  Angle = 360
  Axis = (0,1,0)
  Base = (0,0,0)
  FaceMakerClass = Part::FaceMakerBullseye
  Placement = pos=(89.5,0,3.5) rot=(0,0,1;0rad)
  Solid = false
  Source = -> Face060
  Symmetric = false
FEATURE [Part::Feature] Face061
  shape: bbox 3.5 x 17.8 x 2e-07 mm, 1 faces, 0 solids (baked)
FEATURE [Part::Revolution] Revolve065  label="removeToCreateScrewAndThreadedInsertHole004"
  Angle = 360
  Axis = (0,1,0)
  Base = (0,0,0)
  FaceMakerClass = Part::FaceMakerBullseye
  Placement = pos=(102.5,4.7,3.5) rot=(0,0,1;0rad)
  Solid = false
  Source = -> Face061
  Symmetric = false
FEATURE [Part::Feature] Face062
  shape: bbox 3.5 x 17.8 x 2e-07 mm, 1 faces, 0 solids (baked)
FEATURE [Part::Revolution] Revolve066  label="removeToCreateScrewAndThreadedInsertHole005"
  Angle = 360
  Axis = (0,1,0)
  Base = (0,0,0)
  FaceMakerClass = Part::FaceMakerBullseye
  Placement = pos=(102.5,4.7,68.5) rot=(0,0,1;0rad)
  Solid = false
  Source = -> Face062
  Symmetric = false
FEATURE [Part::MultiFuse] Fusion047  label="makeHoles"
  Shapes = -> [Revolve066,Revolve065,Revolve064,Revolve063,Revolve062,Revolve061]
FEATURE [Part::Feature] Face063
  shape: bbox 3.6 x 3.2 x 2e-07 mm, 1 faces, 0 solids (baked)
FEATURE [Part::Revolution] Revolve067  label="moreFrontCaseScrewRetainer002"
  Angle = 360
  Axis = (0,1,0)
  Base = (0,0,0)
  FaceMakerClass = Part::FaceMakerBullseye
  Placement = pos=(102.5,4.5,68.5) rot=(0,0,1;0rad)
  Solid = false
  Source = -> Face063
  Symmetric = false
FEATURE [Part::Feature] Face064
  shape: bbox 3.6 x 3.2 x 2e-07 mm, 1 faces, 0 solids (baked)
FEATURE [Part::Revolution] Revolve068  label="moreFrontCaseScrewRetainer003"
  Angle = 360
  Axis = (0,1,0)
  Base = (0,0,0)
  FaceMakerClass = Part::FaceMakerBullseye
  Placement = pos=(102.5,4.5,3.5) rot=(0,0,1;0rad)
  Solid = false
  Source = -> Face064
  Symmetric = false
FEATURE [Part::Feature] Face065
  shape: bbox 3.5 x 17.8 x 2e-07 mm, 1 faces, 0 solids (baked)
FEATURE [Part::Revolution] Revolve069  label="removeToCreateScrewAndThreadedInsertHole006"
  Angle = 360
  Axis = (0,1,0)
  Base = (0,0,0)
  FaceMakerClass = Part::FaceMakerBullseye
  Placement = pos=(12.5,0,10) rot=(0,0,1;0rad)
  Solid = false
  Source = -> Face065
  Symmetric = false
FEATURE [Part::Feature] Face066
  shape: bbox 3.5 x 17.8 x 2e-07 mm, 1 faces, 0 solids (baked)
FEATURE [Part::Revolution] Revolve070  label="removeToCreateScrewAndThreadedInsertHole007"
  Angle = 360
  Axis = (0,1,0)
  Base = (0,0,0)
  FaceMakerClass = Part::FaceMakerBullseye
  Placement = pos=(12.5,0,62) rot=(0,0,1;0rad)
  Solid = false
  Source = -> Face066
  Symmetric = false
FEATURE [Part::Feature] Face067
  shape: bbox 3.5 x 17.8 x 2e-07 mm, 1 faces, 0 solids (baked)
FEATURE [Part::Revolution] Revolve071  label="removeToCreateScrewAndThreadedInsertHole008"
  Angle = 360
  Axis = (0,1,0)
  Base = (0,0,0)
  FaceMakerClass = Part::FaceMakerBullseye
  Placement = pos=(89.5,0,68.5) rot=(0,0,1;0rad)
  Solid = false
  Source = -> Face067
  Symmetric = false
FEATURE [Part::Feature] Face068
  shape: bbox 3.5 x 17.8 x 2e-07 mm, 1 faces, 0 solids (baked)
FEATURE [Part::Revolution] Revolve072  label="removeToCreateScrewAndThreadedInsertHole009"
  Angle = 360
  Axis = (0,1,0)
  Base = (0,0,0)
  FaceMakerClass = Part::FaceMakerBullseye
  Placement = pos=(89.5,0,3.5) rot=(0,0,1;0rad)
  Solid = false
  Source = -> Face068
  Symmetric = false
FEATURE [Part::Feature] Face069
  shape: bbox 3.5 x 17.8 x 2e-07 mm, 1 faces, 0 solids (baked)
FEATURE [Part::Feature] Face070
  shape: bbox 3.5 x 17.8 x 2e-07 mm, 1 faces, 0 solids (baked)
FEATURE [Part::Revolution] Revolve073  label="removeToCreateScrewAndThreadedInsertHole010"
  Angle = 360
  Axis = (0,1,0)
  Base = (0,0,0)
  FaceMakerClass = Part::FaceMakerBullseye
  Placement = pos=(102.5,4.7,3.5) rot=(0,0,1;0rad)
  Solid = false
  Source = -> Face069
  Symmetric = false
FEATURE [Part::Revolution] Revolve074  label="removeToCreateScrewAndThreadedInsertHole011"
  Angle = 360
  Axis = (0,1,0)
  Base = (0,0,0)
  FaceMakerClass = Part::FaceMakerBullseye
  Placement = pos=(102.5,4.7,68.5) rot=(0,0,1;0rad)
  Solid = false
  Source = -> Face070
  Symmetric = false
FEATURE [Part::MultiFuse] Fusion048  label="makeHoles001"
  Shapes = -> [Revolve074,Revolve073,Revolve072,Revolve071,Revolve070,Revolve069]
FEATURE [Part::MultiFuse] Fusion049  label="caseScrewRetainers"
  Shapes = -> [Revolve067,Revolve068,Revolve048,Revolve047,Revolve039,Revolve040]
FEATURE [Part::Cut] Cut015  label="caseScrewRetainers001"
  Base = -> Fusion049
  Tool = -> Fusion048
FEATURE [Part::MultiFuse] Fusion050  label="casePillars"
  Shapes = -> [Revolve055,Revolve054,Revolve043,Revolve046,Revolve059,Revolve060]
FEATURE [Part::Feature] Face071 .. Face076  x6 (patterned run collapsed; names and placements below)
  shape: bbox 3.5 x 17.8 x 2e-07 mm, 1 faces, 0 solids (baked)
FEATURE [Part::Revolution] Revolve075  label="removeToCreateScrewAndThreadedInsertHole012"
  Angle = 360
  Axis = (0,1,0)
  Base = (0,0,0)
  FaceMakerClass = Part::FaceMakerBullseye
  Placement = pos=(12.5,0,10) rot=(0,0,1;0rad)
  Solid = false
  Source = -> Face071
  Symmetric = false
FEATURE [Part::Revolution] Revolve076  label="removeToCreateScrewAndThreadedInsertHole013"
  Angle = 360
  Axis = (0,1,0)
  Base = (0,0,0)
  FaceMakerClass = Part::FaceMakerBullseye
  Placement = pos=(12.5,0,62) rot=(0,0,1;0rad)
  Solid = false
  Source = -> Face072
  Symmetric = false
FEATURE [Part::Revolution] Revolve077  label="removeToCreateScrewAndThreadedInsertHole014"
  Angle = 360
  Axis = (0,1,0)
  Base = (0,0,0)
  FaceMakerClass = Part::FaceMakerBullseye
  Placement = pos=(89.5,0,68.5) rot=(0,0,1;0rad)
  Solid = false
  Source = -> Face073
  Symmetric = false
FEATURE [Part::Revolution] Revolve078  label="removeToCreateScrewAndThreadedInsertHole015"
  Angle = 360
  Axis = (0,1,0)
  Base = (0,0,0)
  FaceMakerClass = Part::FaceMakerBullseye
  Placement = pos=(89.5,0,3.5) rot=(0,0,1;0rad)
  Solid = false
  Source = -> Face074
  Symmetric = false
FEATURE [Part::Revolution] Revolve079  label="removeToCreateScrewAndThreadedInsertHole016"
  Angle = 360
  Axis = (0,1,0)
  Base = (0,0,0)
  FaceMakerClass = Part::FaceMakerBullseye
  Placement = pos=(102.5,4.7,3.5) rot=(0,0,1;0rad)
  Solid = false
  Source = -> Face075
  Symmetric = false
FEATURE [Part::Revolution] Revolve080  label="removeToCreateScrewAndThreadedInsertHole017"
  Angle = 360
  Axis = (0,1,0)
  Base = (0,0,0)
  FaceMakerClass = Part::FaceMakerBullseye
  Placement = pos=(102.5,4.7,68.5) rot=(0,0,1;0rad)
  Solid = false
  Source = -> Face076
  Symmetric = false
FEATURE [Part::MultiFuse] Fusion051  label="makeHoles002"
  Shapes = -> [Revolve080,Revolve079,Revolve078,Revolve077,Revolve076,Revolve075]
FEATURE [Part::Cut] Cut016  label="caesPillars"
  Base = -> Fusion050
  Tool = -> Fusion051
FEATURE [Part::Revolution] Revolve009  label="plugHousing016"
  Angle = 360
  Axis = (0,1,0)
  Base = (0,0,0)
  FaceMakerClass = Part::FaceMakerBullseye
  Placement = pos=(0,0,36.15) rot=(0,0,1;0rad)
  Solid = false
  Source = -> Face012
  Symmetric = false
FEATURE [Part::MultiFuse] Fusion014  label="plugHousing023"
  Placement = pos=(0,0,0) rot=(0,0,1;1.5708rad)
  Shapes = -> [Revolve011,Revolve009]
FEATURE [Part::Revolution] Revolve010  label="plugHousing017"
  Angle = 360
  Axis = (0,1,0)
  Base = (0,0,0)
  FaceMakerClass = Part::FaceMakerBullseye
  Placement = pos=(0,0,36.15) rot=(0,0,1;0rad)
  Solid = false
  Source = -> Face014
  Symmetric = false
FEATURE [Part::MultiFuse] Fusion015  label="plugHousing024"
  Placement = pos=(0,0,0) rot=(0,0,1;1.5708rad)
  Shapes = -> [Revolve010,Revolve015]
FEATURE [Part::Revolution] Revolve014  label="plugHousing026"
  Angle = 360
  Axis = (0,1,0)
  Base = (0,0,0)
  FaceMakerClass = Part::FaceMakerBullseye
  Placement = pos=(0,0,36.15) rot=(0,0,1;0rad)
  Solid = false
  Source = -> Face011
  Symmetric = false
FEATURE [Part::Revolution] Revolve013  label="plugHousing025"
  Angle = 360
  Axis = (0,1,0)
  Base = (0,0,0)
  FaceMakerClass = Part::FaceMakerBullseye
  Placement = pos=(0,0,36.15) rot=(0,0,1;0rad)
  Solid = false
  Source = -> Face015
  Symmetric = false
FEATURE [Part::MultiFuse] Fusion016  label="plugHousing028"
  Placement = pos=(0,19,0) rot=(0,0,1;3.14159rad)
  Shapes = -> [Fusion014,Fusion013]
FEATURE [Part::MultiFuse] Fusion011  label="plugHousing018"
  Placement = pos=(0,0,0) rot=(0,0,1;1.5708rad)
  Shapes = -> [Revolve014,Revolve013]
FEATURE [Part::MultiFuse] Fusion012  label="plugHousing019"
  Placement = pos=(0,19,0) rot=(0,0,1;3.14159rad)
  Shapes = -> [Fusion011,Fusion015]
FEATURE [Part::MultiFuse] Fusion017  label="plugHousing029"
  Placement = pos=(122.621,0,-0.15) rot=(0,0,1;0rad)
  Shapes = -> [Fusion016,Fusion012]
FEATURE [Part::MultiFuse] Fusion052  label="casePillarRetainers"
  Shapes = -> [Extrude012,Extrude013,Extrude014,Extrude015,Extrude016,Extrude017,Extrude018,Extrude019,Box011,Box012]
FEATURE [Part::Feature] Face077
  shape: bbox 3.5 x 17.8 x 2e-07 mm, 1 faces, 0 solids (baked)
FEATURE [Part::Revolution] Revolve081  label="removeToCreateScrewAndThreadedInsertHole018"
  Angle = 360
  Axis = (0,1,0)
  Base = (0,0,0)
  FaceMakerClass = Part::FaceMakerBullseye
  Placement = pos=(62.3,30.3,19.7) rot=(0,0,1;0rad)
  Solid = false
  Source = -> Face077
  Symmetric = false
FEATURE [Part::Feature] Face078
  shape: bbox 3.5 x 17.8 x 2e-07 mm, 1 faces, 0 solids (baked)
FEATURE [Part::Revolution] Revolve082  label="removeToCreateScrewAndThreadedInsertHole019"
  Angle = 360
  Axis = (0,1,0)
  Base = (0,0,0)
  FaceMakerClass = Part::FaceMakerBullseye
  Placement = pos=(62.3,30.3,51.7) rot=(0,0,1;0rad)
  Solid = false
  Source = -> Face078
  Symmetric = false
FEATURE [Part::Feature] Face079
  shape: bbox 3.5 x 17.8 x 2e-07 mm, 1 faces, 0 solids (baked)
FEATURE [Part::Revolution] Revolve083  label="removeToCreateScrewAndThreadedInsertHole020"
  Angle = 360
  Axis = (0,1,0)
  Base = (0,0,0)
  FaceMakerClass = Part::FaceMakerBullseye
  Placement = pos=(30.3,30.3,19.7) rot=(0,0,1;0rad)
  Solid = false
  Source = -> Face079
  Symmetric = false
FEATURE [Part::Feature] Face080
  shape: bbox 3.5 x 17.8 x 2e-07 mm, 1 faces, 0 solids (baked)
FEATURE [Part::Revolution] Revolve084  label="removeToCreateScrewAndThreadedInsertHole021"
  Angle = 360
  Axis = (0,1,0)
  Base = (0,0,0)
  FaceMakerClass = Part::FaceMakerBullseye
  Placement = pos=(30.3,30.3,51.7) rot=(0,0,1;0rad)
  Solid = false
  Source = -> Face080
  Symmetric = false
FEATURE [Part::MultiFuse] Fusion053  label="createThreadedInsertHolesForFan"
  Shapes = -> [Revolve081,Revolve082,Revolve083,Revolve084]
FEATURE [Part::Cut] Cut017  label="fanScrewHousing001"
  Base = -> Fusion046
  Tool = -> Fusion053
FEATURE [Part::Feature] Face081
  shape: bbox 3.5 x 17.8 x 2e-07 mm, 1 faces, 0 solids (baked)
FEATURE [Part::Revolution] Revolve085  label="removeToCreateScrewAndThreadedInsertHole022"
  Angle = 360
  Axis = (0,1,0)
  Base = (0,0,0)
  FaceMakerClass = Part::FaceMakerBullseye
  Placement = pos=(62.3,30.3,19.7) rot=(0,0,1;0rad)
  Solid = false
  Source = -> Face081
  Symmetric = false
FEATURE [Part::Feature] Face082
  shape: bbox 3.5 x 17.8 x 2e-07 mm, 1 faces, 0 solids (baked)
FEATURE [Part::Revolution] Revolve086  label="removeToCreateScrewAndThreadedInsertHole023"
  Angle = 360
  Axis = (0,1,0)
  Base = (0,0,0)
  FaceMakerClass = Part::FaceMakerBullseye
  Placement = pos=(62.3,30.3,51.7) rot=(0,0,1;0rad)
  Solid = false
  Source = -> Face082
  Symmetric = false
FEATURE [Part::Feature] Face083
  shape: bbox 3.5 x 17.8 x 2e-07 mm, 1 faces, 0 solids (baked)
FEATURE [Part::Revolution] Revolve087  label="removeToCreateScrewAndThreadedInsertHole024"
  Angle = 360
  Axis = (0,1,0)
  Base = (0,0,0)
  FaceMakerClass = Part::FaceMakerBullseye
  Placement = pos=(30.3,30.3,19.7) rot=(0,0,1;0rad)
  Solid = false
  Source = -> Face083
  Symmetric = false
FEATURE [Part::Feature] Face084
  shape: bbox 3.5 x 17.8 x 2e-07 mm, 1 faces, 0 solids (baked)
FEATURE [Part::Revolution] Revolve088  label="removeToCreateScrewAndThreadedInsertHole025"
  Angle = 360
  Axis = (0,1,0)
  Base = (0,0,0)
  FaceMakerClass = Part::FaceMakerBullseye
  Placement = pos=(30.3,30.3,51.7) rot=(0,0,1;0rad)
  Solid = false
  Source = -> Face084
  Symmetric = false
FEATURE [Part::MultiFuse] Fusion054  label="createThreadedInsertHolesForFan001"
  Shapes = -> [Revolve085,Revolve086,Revolve087,Revolve088]
FEATURE [Part::Cut] Cut018  label="top007"
  Base = -> Fusion040
  Tool = -> Fusion054
FEATURE [Sketcher::SketchObject] Sketch029
  FullyConstrained = false
  Placement = pos=(0,0,0) rot=(1,0,0;1.5708rad)
  sketch-geometry (24):
    g0: ArcOfCircle CenterX=-4 CenterY=-10.5 CenterZ=0 NormalX=0 NormalY=0 NormalZ=1 AngleXU=0 Radius=1.5 StartAngle=6e-16 EndAngle=3.14159
    g1: ArcOfCircle CenterX=-34.2 CenterY=-10.5 CenterZ=0 NormalX=0 NormalY=0 NormalZ=1 AngleXU=0 Radius=1.5 StartAngle=0 EndAngle=3.14159
    g2: ArcOfCircle CenterX=-34.2 CenterY=-27.7 CenterZ=0 NormalX=0 NormalY=0 NormalZ=1 AngleXU=0 Radius=1.5 StartAngle=3.14159 EndAngle=6.28319
    g3: ArcOfCircle CenterX=-4 CenterY=-27.7 CenterZ=0 NormalX=0 NormalY=0 NormalZ=1 AngleXU=0 Radius=1.5 StartAngle=3.1416 EndAngle=6.28319
    g4: ArcOfCircle CenterX=-10 CenterY=-4.3 CenterZ=0 NormalX=0 NormalY=0 NormalZ=1 AngleXU=0 Radius=1.5 StartAngle=2e-16 EndAngle=3.14159
    g5: ArcOfCircle CenterX=-16.1 CenterY=-1.8 CenterZ=0 NormalX=0 NormalY=0 NormalZ=1 AngleXU=0 Radius=1.5 StartAngle=5e-16 EndAngle=3.14159
    g6: ArcOfCircle CenterX=-22.1 CenterY=-1.8 CenterZ=0 NormalX=0 NormalY=0 NormalZ=1 AngleXU=0 Radius=1.5 StartAngle=5e-16 EndAngle=3.14159
    g7: ArcOfCircle CenterX=-28.2 CenterY=-4.3 CenterZ=0 NormalX=0 NormalY=0 NormalZ=1 AngleXU=0 Radius=1.5 StartAngle=2e-16 EndAngle=3.14159
    g8: ArcOfCircle CenterX=-10 CenterY=-33.9 CenterZ=0 NormalX=0 NormalY=0 NormalZ=1 AngleXU=0 Radius=1.5 StartAngle=3.14159 EndAngle=6.28319
    g9: ArcOfCircle CenterX=-16.1 CenterY=-36.4 CenterZ=0 NormalX=0 NormalY=0 NormalZ=1 AngleXU=0 Radius=1.5 StartAngle=3.14159 EndAngle=6.28319
    g10: ArcOfCircle CenterX=-22.1 CenterY=-36.4 CenterZ=0 NormalX=0 NormalY=0 NormalZ=1 AngleXU=0 Radius=1.5 StartAngle=3.14159 EndAngle=6.28319
    g11: ArcOfCircle CenterX=-28.2 CenterY=-33.9 CenterZ=0 NormalX=0 NormalY=0 NormalZ=1 AngleXU=0 Radius=1.5 StartAngle=3.14159 EndAngle=6.28319
    g12: LineSegment StartX=-35.7 StartY=-10.5 StartZ=0 EndX=-35.7 EndY=-27.7 EndZ=0
    g13: LineSegment StartX=-32.7 StartY=-10.5 StartZ=0 EndX=-32.7 EndY=-27.7 EndZ=0
    g14: LineSegment StartX=-29.7 StartY=-33.9 StartZ=0 EndX=-29.7 EndY=-4.3 EndZ=0
    g15: LineSegment StartX=-26.7 StartY=-33.9 StartZ=0 EndX=-26.7 EndY=-4.3 EndZ=0
    g16: LineSegment StartX=-2.5 StartY=-10.5 StartZ=0 EndX=-2.5 EndY=-27.7 EndZ=0
    g17: LineSegment StartX=-8.5 StartY=-4.3 StartZ=0 EndX=-8.5 EndY=-33.9 EndZ=0
    g18: LineSegment StartX=-5.5 StartY=-10.5 StartZ=0 EndX=-5.5 EndY=-27.7 EndZ=0
    g19: LineSegment StartX=-11.5 StartY=-4.3 StartZ=0 EndX=-11.5 EndY=-33.9 EndZ=0
    g20: LineSegment StartX=-14.6 StartY=-1.8 StartZ=0 EndX=-14.6 EndY=-36.4 EndZ=0
    g21: LineSegment StartX=-17.6 StartY=-1.8 StartZ=0 EndX=-17.6 EndY=-36.4 EndZ=0
    g22: LineSegment StartX=-20.6 StartY=-36.4 StartZ=0 EndX=-20.6 EndY=-1.8 EndZ=0
    g23: LineSegment StartX=-23.6 StartY=-1.8 StartZ=0 EndX=-23.6 EndY=-36.4 EndZ=0
  constraints (48):
    c: Block(g0)
    c: Block(g1)
    c: Block(g2)
    c: Block(g3)
    c: Block(g4)
    c: Block(g5)
    c: Block(g6)
    c: Block(g7)
    c: Block(g8)
    c: Block(g9)
    c: Block(g10)
    c: Block(g11)
    c: Coincident(g12,g1)
    c: Coincident(g12,g2)
    c: Vertical(g12)
    c: Coincident(g13,g1)
    c: Coincident(g13,g2)
    c: Vertical(g13)
    c: Coincident(g14,g11)
    c: Coincident(g14,g7)
    c: Vertical(g14)
    c: Coincident(g15,g11)
    c: Coincident(g15,g7)
    c: Vertical(g15)
    c: Coincident(g16,g0)
    c: Coincident(g16,g3)
    c: Vertical(g16)
    c: Coincident(g17,g4)
    c: Coincident(g17,g8)
    c: Vertical(g17)
    c: Coincident(g18,g0)
    c: Coincident(g18,g3)
    c: Vertical(g18)
    c: Coincident(g19,g4)
    c: Coincident(g19,g8)
    c: Vertical(g19)
    c: Coincident(g20,g5)
    c: Coincident(g20,g9)
    c: Vertical(g20)
    c: Coincident(g21,g5)
    c: Coincident(g21,g9)
    c: Vertical(g21)
    c: Coincident(g22,g10)
    c: Coincident(g22,g6)
    c: Vertical(g22)
    c: Coincident(g23,g6)
    c: Coincident(g23,g10)
    c: Vertical(g23)
FEATURE [Part::Extrusion] Extrude020  label="removeToCreateFanGrillHoles"
  Base = -> Sketch029
  Dir = (0,-1,6e-16)
  DirMode = 2
  FaceMakerClass = Part::FaceMakerBullseye
  LengthFwd = 10
  LengthRev = 0
  Placement = pos=(65.4,44,54.82) rot=(0,0,1;0rad)
  Solid = true
  Symmetric = false
FEATURE [Part::MultiFuse] Fusion055  label="top008"
  Shapes = -> [Cut017,Cut018]
FEATURE [Part::Cut] Cut019  label="top009"
  Base = -> Fusion055
  Tool = -> Extrude020
FEATURE [App::MeasureDistance] Distance003  label="Distance: 71.95 mm"
  Distance = 71.9513
  P1 = (117,38,72)
  P2 = (117,38,0.0487319)
FEATURE [Sketcher::SketchObject] Sketch030
  FullyConstrained = true
  Placement = pos=(117,19,0) rot=(0.57735,0.57735,0.57735;2.0944rad)
  sketch-geometry (48):
    g0: LineSegment StartX=-49.19 StartY=69.25 StartZ=0 EndX=-49.19 EndY=66.25 EndZ=0
    g1: LineSegment StartX=-49.19 StartY=63.5 StartZ=0 EndX=-49.19 EndY=60.5 EndZ=0
    g2: LineSegment StartX=-49.19 StartY=57.75 StartZ=0 EndX=-49.19 EndY=54.75 EndZ=0
    g3: LineSegment StartX=-49.19 StartY=52 StartZ=0 EndX=-49.19 EndY=49 EndZ=0
    g4: LineSegment StartX=-49.19 StartY=46.25 StartZ=0 EndX=-49.19 EndY=43.25 EndZ=0
    g5: LineSegment StartX=-49.19 StartY=40.5 StartZ=0 EndX=-49.19 EndY=37.5 EndZ=0
    g6: LineSegment StartX=-49.19 StartY=34.5 StartZ=0 EndX=-49.19 EndY=31.5 EndZ=0
    g7: LineSegment StartX=-49.19 StartY=28.75 StartZ=0 EndX=-49.19 EndY=25.75 EndZ=0
    g8: LineSegment StartX=-49.19 StartY=23 StartZ=0 EndX=-49.19 EndY=20 EndZ=0
    g9: LineSegment StartX=-49.19 StartY=17.25 StartZ=0 EndX=-49.19 EndY=14.25 EndZ=0
    g10: LineSegment StartX=-49.19 StartY=11.5 StartZ=0 EndX=-49.19 EndY=8.5 EndZ=0
    g11: LineSegment StartX=-49.19 StartY=5.75 StartZ=0 EndX=-49.19 EndY=2.75 EndZ=0
    g12: ArcOfCircle CenterX=-1.5 CenterY=67.75 CenterZ=0 NormalX=0 NormalY=0 NormalZ=1 AngleXU=0 Radius=1.5 StartAngle=4.71239 EndAngle=7.85398
    g13: ArcOfCircle CenterX=-1.5 CenterY=62 CenterZ=0 NormalX=0 NormalY=0 NormalZ=1 AngleXU=0 Radius=1.5 StartAngle=4.71239 EndAngle=7.85398
    g14: ArcOfCircle CenterX=-1.5 CenterY=56.25 CenterZ=0 NormalX=0 NormalY=0 NormalZ=1 AngleXU=0 Radius=1.5 StartAngle=4.71239 EndAngle=7.85398
    g15: ArcOfCircle CenterX=-11.49 CenterY=50.5 CenterZ=0 NormalX=0 NormalY=0 NormalZ=1 AngleXU=0 Radius=1.5 StartAngle=4.71239 EndAngle=7.85398
    g16: ArcOfCircle CenterX=-16.28 CenterY=44.75 CenterZ=0 NormalX=0 NormalY=0 NormalZ=1 AngleXU=0 Radius=1.5 StartAngle=4.71239 EndAngle=7.85398
    g17: ArcOfCircle CenterX=-18.2337 CenterY=39 CenterZ=0 NormalX=0 NormalY=0 NormalZ=1 AngleXU=0 Radius=1.5 StartAngle=4.71485 EndAngle=7.85398
    g18: ArcOfCircle CenterX=-16.2837 CenterY=27.25 CenterZ=0 NormalX=0 NormalY=0 NormalZ=1 AngleXU=0 Radius=1.5 StartAngle=4.71485 EndAngle=7.85398
    g19: ArcOfCircle CenterX=-18.2337 CenterY=33 CenterZ=0 NormalX=0 NormalY=0 NormalZ=1 AngleXU=0 Radius=1.5 StartAngle=4.71485 EndAngle=7.85398
    g20: ArcOfCircle CenterX=-11.49 CenterY=21.5 CenterZ=0 NormalX=0 NormalY=0 NormalZ=1 AngleXU=0 Radius=1.5 StartAngle=4.71239 EndAngle=7.85398
    g21: ArcOfCircle CenterX=-1.5 CenterY=4.25 CenterZ=0 NormalX=0 NormalY=0 NormalZ=1 AngleXU=0 Radius=1.5 StartAngle=4.71239 EndAngle=7.85398
    g22: ArcOfCircle CenterX=-1.5 CenterY=10 CenterZ=0 NormalX=0 NormalY=0 NormalZ=1 AngleXU=0 Radius=1.5 StartAngle=4.71239 EndAngle=7.85398
    g23: ArcOfCircle CenterX=-1.5 CenterY=15.75 CenterZ=0 NormalX=0 NormalY=0 NormalZ=1 AngleXU=0 Radius=1.5 StartAngle=4.71239 EndAngle=7.85398
    g24: LineSegment StartX=-49.19 StartY=69.25 StartZ=0 EndX=-1.5 EndY=69.25 EndZ=0
    g25: LineSegment StartX=-49.19 StartY=66.25 StartZ=0 EndX=-1.5 EndY=66.25 EndZ=0
    g26: LineSegment StartX=-49.19 StartY=63.5 StartZ=0 EndX=-1.5 EndY=63.5 EndZ=0
    g27: LineSegment StartX=-49.19 StartY=60.5 StartZ=0 EndX=-1.5 EndY=60.5 EndZ=0
    g28: LineSegment StartX=-49.19 StartY=57.75 StartZ=0 EndX=-1.5 EndY=57.75 EndZ=0
    g29: LineSegment StartX=-49.19 StartY=54.75 StartZ=0 EndX=-1.5 EndY=54.75 EndZ=0
    g30: LineSegment StartX=-49.19 StartY=52 StartZ=0 EndX=-11.49 EndY=52 EndZ=0
    g31: LineSegment StartX=-49.19 StartY=49 StartZ=0 EndX=-11.49 EndY=49 EndZ=0
    g32: LineSegment StartX=-49.19 StartY=46.25 StartZ=0 EndX=-16.28 EndY=46.25 EndZ=0
    g33: LineSegment StartX=-49.19 StartY=43.25 StartZ=0 EndX=-16.28 EndY=43.25 EndZ=0
    g34: LineSegment StartX=-49.19 StartY=40.5 StartZ=0 EndX=-18.2337 EndY=40.5 EndZ=0
    g35: LineSegment StartX=-49.19 StartY=37.5 StartZ=0 EndX=-18.23 EndY=37.5 EndZ=0
    g36: LineSegment StartX=-49.19 StartY=34.5 StartZ=0 EndX=-18.2337 EndY=34.5 EndZ=0
    g37: LineSegment StartX=-49.19 StartY=31.5 StartZ=0 EndX=-18.23 EndY=31.5 EndZ=0
    g38: LineSegment StartX=-49.19 StartY=28.75 StartZ=0 EndX=-16.2837 EndY=28.75 EndZ=0
    g39: LineSegment StartX=-49.19 StartY=25.75 StartZ=0 EndX=-16.28 EndY=25.75 EndZ=0
    g40: LineSegment StartX=-49.19 StartY=23 StartZ=0 EndX=-11.49 EndY=23 EndZ=0
    g41: LineSegment StartX=-49.19 StartY=20 StartZ=0 EndX=-11.49 EndY=20 EndZ=0
    g42: LineSegment StartX=-49.19 StartY=17.25 StartZ=0 EndX=-1.5 EndY=17.25 EndZ=0
    g43: LineSegment StartX=-49.19 StartY=14.25 StartZ=0 EndX=-1.5 EndY=14.25 EndZ=0
    g44: LineSegment StartX=-49.19 StartY=11.5 StartZ=0 EndX=-1.5 EndY=11.5 EndZ=0
    g45: LineSegment StartX=-49.19 StartY=8.5 StartZ=0 EndX=-1.5 EndY=8.5 EndZ=0
    g46: LineSegment StartX=-49.19 StartY=5.75 StartZ=0 EndX=-1.5 EndY=5.75 EndZ=0
    g47: LineSegment StartX=-49.19 StartY=2.75 StartZ=0 EndX=-1.5 EndY=2.75 EndZ=0
  constraints (120):
    c: Vertical(g0)
    c: Distance(g0) = 3
    c: Block(g0)
    c: Vertical(g1)
    c: Distance(g1) = 3
    c: Vertical(g2)
    c: Equal(g0,g2) = 3
    c: Block(g2)
    c: Vertical(g3)
    c: Equal(g1,g3) = 3
    c: Vertical(g4)
    c: Equal(g0,g4) = 3
    c: Block(g4)
    c: Vertical(g5)
    c: Equal(g1,g5) = 3
    c: Vertical(g6)
    c: Equal(g0,g6) = 3
    c: Block(g6)
    c: Vertical(g7)
    c: Equal(g1,g7) = 3
    c: Vertical(g8)
    c: Equal(g0,g8) = 3
    c: Block(g8)
    c: Vertical(g9)
    c: Equal(g1,g9) = 3
    c: Vertical(g10)
    c: Equal(g0,g10) = 3
    c: Block(g10)
    c: Vertical(g11)
    c: Equal(g1,g11) = 3
    c: Block(g12)
    c: Block(g13)
    c: Block(g14)
    c: Block(g15)
    c: Block(g16)
    c: Block(g17)
    c: Block(g18)
    c: Block(g19)
    c: Block(g20)
    c: Block(g21)
    c: Block(g22)
    c: Block(g23)
    c: Block(g11)
    c: Block(g9)
    c: Block(g7)
    c: Block(g5)
    c: Block(g3)
    c: Block(g1)
    c: Coincident(g24,g0)
    c: Coincident(g24,g12)
    c: Horizontal(g24)
    c: Coincident(g25,g0)
    c: Coincident(g25,g12)
    c: Horizontal(g25)
    c: Coincident(g26,g1)
    c: Coincident(g26,g13)
    c: Horizontal(g26)
    c: Coincident(g27,g1)
    c: Coincident(g27,g13)
    c: Horizontal(g27)
    c: Coincident(g28,g2)
    c: Coincident(g28,g14)
    c: Horizontal(g28)
    c: Coincident(g29,g2)
    c: Coincident(g29,g14)
    c: Horizontal(g29)
    c: Coincident(g30,g3)
    c: Coincident(g30,g15)
    c: Horizontal(g30)
    c: Coincident(g31,g3)
    c: Coincident(g31,g15)
    c: Horizontal(g31)
    c: Coincident(g32,g4)
    c: Coincident(g32,g16)
    c: Horizontal(g32)
    c: Coincident(g33,g4)
    c: Coincident(g33,g16)
    c: Horizontal(g33)
    c: Coincident(g34,g5)
    c: Coincident(g34,g17)
    c: Horizontal(g34)
    c: Coincident(g35,g5)
    c: Coincident(g35,g17)
    c: Horizontal(g35)
    c: Coincident(g36,g6)
    c: Coincident(g36,g19)
    c: Horizontal(g36)
    c: Coincident(g37,g6)
    c: Coincident(g37,g19)
    c: Horizontal(g37)
    c: Coincident(g38,g7)
    c: Coincident(g38,g18)
    c: Horizontal(g38)
    c: Coincident(g39,g7)
    c: Coincident(g39,g18)
    c: Horizontal(g39)
    c: Coincident(g40,g8)
    c: Coincident(g40,g20)
    c: Horizontal(g40)
    c: Coincident(g41,g8)
    c: Coincident(g41,g20)
    c: Horizontal(g41)
    c: Coincident(g42,g9)
    c: Coincident(g42,g23)
    c: Horizontal(g42)
    c: Coincident(g43,g9)
    c: Coincident(g43,g23)
    c: Horizontal(g43)
    c: Coincident(g44,g10)
    c: Coincident(g44,g22)
    c: Horizontal(g44)
    c: Coincident(g45,g10)
    c: Coincident(g45,g22)
    c: Horizontal(g45)
    c: Coincident(g46,g11)
    c: Coincident(g46,g21)
    c: Horizontal(g46)
    c: Coincident(g47,g11)
    c: Coincident(g47,g21)
    c: Horizontal(g47)
FEATURE [Sketcher::SketchObject] Sketch031
  FullyConstrained = true
  Placement = pos=(117,19,0) rot=(0.57735,0.57735,0.57735;2.0944rad)
  sketch-geometry (24):
    g0: ArcOfCircle CenterX=-49.19 CenterY=67.75 CenterZ=0 NormalX=0 NormalY=0 NormalZ=1 AngleXU=0 Radius=1.5 StartAngle=1.5708 EndAngle=4.71239
    g1: ArcOfCircle CenterX=-49.19 CenterY=62 CenterZ=0 NormalX=0 NormalY=0 NormalZ=1 AngleXU=0 Radius=1.5 StartAngle=1.5708 EndAngle=4.71239
    g2: ArcOfCircle CenterX=-49.19 CenterY=56.25 CenterZ=0 NormalX=0 NormalY=0 NormalZ=1 AngleXU=0 Radius=1.5 StartAngle=1.5708 EndAngle=4.71239
    g3: ArcOfCircle CenterX=-49.19 CenterY=50.5 CenterZ=0 NormalX=0 NormalY=0 NormalZ=1 AngleXU=0 Radius=1.5 StartAngle=1.5708 EndAngle=4.71239
    g4: ArcOfCircle CenterX=-49.19 CenterY=44.75 CenterZ=0 NormalX=0 NormalY=0 NormalZ=1 AngleXU=0 Radius=1.5 StartAngle=1.5708 EndAngle=4.71239
    g5: ArcOfCircle CenterX=-49.19 CenterY=39 CenterZ=0 NormalX=0 NormalY=0 NormalZ=1 AngleXU=0 Radius=1.5 StartAngle=1.5708 EndAngle=4.71239
    g6: ArcOfCircle CenterX=-49.19 CenterY=33 CenterZ=0 NormalX=0 NormalY=0 NormalZ=1 AngleXU=0 Radius=1.5 StartAngle=1.5708 EndAngle=4.71239
    g7: ArcOfCircle CenterX=-49.19 CenterY=27.25 CenterZ=0 NormalX=0 NormalY=0 NormalZ=1 AngleXU=0 Radius=1.5 StartAngle=1.5708 EndAngle=4.71239
    g8: ArcOfCircle CenterX=-49.19 CenterY=21.5 CenterZ=0 NormalX=0 NormalY=0 NormalZ=1 AngleXU=0 Radius=1.5 StartAngle=1.5708 EndAngle=4.71239
    g9: ArcOfCircle CenterX=-49.19 CenterY=15.75 CenterZ=0 NormalX=0 NormalY=0 NormalZ=1 AngleXU=0 Radius=1.5 StartAngle=1.5708 EndAngle=4.71239
    g10: ArcOfCircle CenterX=-49.19 CenterY=10 CenterZ=0 NormalX=0 NormalY=0 NormalZ=1 AngleXU=0 Radius=1.5 StartAngle=1.5708 EndAngle=4.71239
    g11: ArcOfCircle CenterX=-49.19 CenterY=4.25 CenterZ=0 NormalX=0 NormalY=0 NormalZ=1 AngleXU=0 Radius=1.5 StartAngle=1.5708 EndAngle=4.71239
    g12: LineSegment StartX=-49.19 StartY=69.25 StartZ=0 EndX=-49.19 EndY=66.25 EndZ=0
    g13: LineSegment StartX=-49.19 StartY=63.5 StartZ=0 EndX=-49.19 EndY=60.5 EndZ=0
    g14: LineSegment StartX=-49.19 StartY=57.75 StartZ=0 EndX=-49.19 EndY=54.75 EndZ=0
    g15: LineSegment StartX=-49.19 StartY=52 StartZ=0 EndX=-49.19 EndY=49 EndZ=0
    g16: LineSegment StartX=-49.19 StartY=46.25 StartZ=0 EndX=-49.19 EndY=43.25 EndZ=0
    g17: LineSegment StartX=-49.19 StartY=40.5 StartZ=0 EndX=-49.19 EndY=37.5 EndZ=0
    g18: LineSegment StartX=-49.19 StartY=34.5 StartZ=0 EndX=-49.19 EndY=31.5 EndZ=0
    g19: LineSegment StartX=-49.19 StartY=28.75 StartZ=0 EndX=-49.19 EndY=25.75 EndZ=0
    g20: LineSegment StartX=-49.19 StartY=23 StartZ=0 EndX=-49.19 EndY=20 EndZ=0
    g21: LineSegment StartX=-49.19 StartY=17.25 StartZ=0 EndX=-49.19 EndY=14.25 EndZ=0
    g22: LineSegment StartX=-49.19 StartY=11.5 StartZ=0 EndX=-49.19 EndY=8.5 EndZ=0
    g23: LineSegment StartX=-49.19 StartY=5.75 StartZ=0 EndX=-49.19 EndY=2.75 EndZ=0
  constraints (48):
    c: Block(g0)
    c: Block(g1)
    c: Block(g2)
    c: Block(g3)
    c: Block(g4)
    c: Block(g5)
    c: Block(g6)
    c: Block(g7)
    c: Block(g8)
    c: Block(g9)
    c: Block(g10)
    c: Block(g11)
    c: Coincident(g12,g0)
    c: Coincident(g12,g0)
    c: Vertical(g12)
    c: Vertical(g13)
    c: Coincident(g13,g1)
    c: Vertical(g14)
    c: Coincident(g14,g2)
    c: Vertical(g15)
    c: Coincident(g15,g3)
    c: Vertical(g16)
    c: Coincident(g16,g4)
    c: Vertical(g17)
    c: Coincident(g17,g5)
    c: Vertical(g18)
    c: Coincident(g18,g6)
    c: Vertical(g19)
    c: Coincident(g19,g7)
    c: Vertical(g20)
    c: Coincident(g20,g8)
    c: Vertical(g21)
    c: Coincident(g21,g9)
    c: Vertical(g22)
    c: Coincident(g22,g10)
    c: Vertical(g23)
    c: Coincident(g23,g11)
    c: Block(g23)
    c: Block(g22)
    c: Block(g21)
    c: Block(g20)
    c: Block(g13)
    c: Block(g14)
    c: Block(g15)
    c: Block(g16)
    c: Block(g17)
    c: Block(g18)
    c: Block(g19)
FEATURE [Part::Extrusion] Extrude022
  Base = -> Sketch030
  Dir = (1,-2e-16,2e-16)
  DirMode = 2
  FaceMakerClass = Part::FaceMakerBullseye
  LengthFwd = 19
  LengthRev = 0
  Placement = pos=(-19,0,0) rot=(0,0,1;0rad)
  Solid = true
  Symmetric = false
FEATURE [Part::Fillet] Fillet022
  Base = -> Extrude022
  Edges = 24 edges r=1.49: [Edge6,Edge11,Edge18,Edge23,Edge30,Edge35,Edge42,Edge47,Edge54,Edge59,Edge66,Edge71,Edge78,Edge83,Edge90,Edge95,Edge102,Edge107,Edge114,Edge119,Edge126,Edge131,Edge138,Edge143]
FEATURE [Part::Cut] Cut020  label="top010"
  Base = -> Cut019
  Tool = -> Fillet022
FEATURE [Sketcher::SketchObject] Sketch032
  FullyConstrained = true
  Placement = pos=(117,19,0) rot=(0.57735,0.57735,0.57735;2.0944rad)
  sketch-geometry (48):
    g0: LineSegment StartX=-49.19 StartY=69.25 StartZ=0 EndX=-49.19 EndY=66.25 EndZ=0
    g1: LineSegment StartX=-49.19 StartY=63.5 StartZ=0 EndX=-49.19 EndY=60.5 EndZ=0
    g2: LineSegment StartX=-49.19 StartY=57.75 StartZ=0 EndX=-49.19 EndY=54.75 EndZ=0
    g3: LineSegment StartX=-49.19 StartY=52 StartZ=0 EndX=-49.19 EndY=49 EndZ=0
    g4: LineSegment StartX=-49.19 StartY=46.25 StartZ=0 EndX=-49.19 EndY=43.25 EndZ=0
    g5: LineSegment StartX=-49.19 StartY=40.5 StartZ=0 EndX=-49.19 EndY=37.5 EndZ=0
    g6: LineSegment StartX=-49.19 StartY=34.5 StartZ=0 EndX=-49.19 EndY=31.5 EndZ=0
    g7: LineSegment StartX=-49.19 StartY=28.75 StartZ=0 EndX=-49.19 EndY=25.75 EndZ=0
    g8: LineSegment StartX=-49.19 StartY=23 StartZ=0 EndX=-49.19 EndY=20 EndZ=0
    g9: LineSegment StartX=-49.19 StartY=17.25 StartZ=0 EndX=-49.19 EndY=14.25 EndZ=0
    g10: LineSegment StartX=-49.19 StartY=11.5 StartZ=0 EndX=-49.19 EndY=8.5 EndZ=0
    g11: LineSegment StartX=-49.19 StartY=5.75 StartZ=0 EndX=-49.19 EndY=2.75 EndZ=0
    g12: ArcOfCircle CenterX=-1.5 CenterY=67.75 CenterZ=0 NormalX=0 NormalY=0 NormalZ=1 AngleXU=0 Radius=1.5 StartAngle=4.71239 EndAngle=7.85398
    g13: ArcOfCircle CenterX=-1.5 CenterY=62 CenterZ=0 NormalX=0 NormalY=0 NormalZ=1 AngleXU=0 Radius=1.5 StartAngle=4.71239 EndAngle=7.85398
    g14: ArcOfCircle CenterX=-1.5 CenterY=56.25 CenterZ=0 NormalX=0 NormalY=0 NormalZ=1 AngleXU=0 Radius=1.5 StartAngle=4.71239 EndAngle=7.85398
    g15: ArcOfCircle CenterX=-11.49 CenterY=50.5 CenterZ=0 NormalX=0 NormalY=0 NormalZ=1 AngleXU=0 Radius=1.5 StartAngle=4.71239 EndAngle=7.85398
    g16: ArcOfCircle CenterX=-16.28 CenterY=44.75 CenterZ=0 NormalX=0 NormalY=0 NormalZ=1 AngleXU=0 Radius=1.5 StartAngle=4.71239 EndAngle=7.85398
    g17: ArcOfCircle CenterX=-18.2337 CenterY=39 CenterZ=0 NormalX=0 NormalY=0 NormalZ=1 AngleXU=0 Radius=1.5 StartAngle=4.71485 EndAngle=7.85398
    g18: ArcOfCircle CenterX=-16.2837 CenterY=27.25 CenterZ=0 NormalX=0 NormalY=0 NormalZ=1 AngleXU=0 Radius=1.5 StartAngle=4.71485 EndAngle=7.85398
    g19: ArcOfCircle CenterX=-18.2337 CenterY=33 CenterZ=0 NormalX=0 NormalY=0 NormalZ=1 AngleXU=0 Radius=1.5 StartAngle=4.71485 EndAngle=7.85398
    g20: ArcOfCircle CenterX=-11.49 CenterY=21.5 CenterZ=0 NormalX=0 NormalY=0 NormalZ=1 AngleXU=0 Radius=1.5 StartAngle=4.71239 EndAngle=7.85398
    g21: ArcOfCircle CenterX=-1.5 CenterY=4.25 CenterZ=0 NormalX=0 NormalY=0 NormalZ=1 AngleXU=0 Radius=1.5 StartAngle=4.71239 EndAngle=7.85398
    g22: ArcOfCircle CenterX=-1.5 CenterY=10 CenterZ=0 NormalX=0 NormalY=0 NormalZ=1 AngleXU=0 Radius=1.5 StartAngle=4.71239 EndAngle=7.85398
    g23: ArcOfCircle CenterX=-1.5 CenterY=15.75 CenterZ=0 NormalX=0 NormalY=0 NormalZ=1 AngleXU=0 Radius=1.5 StartAngle=4.71239 EndAngle=7.85398
    g24: LineSegment StartX=-49.19 StartY=69.25 StartZ=0 EndX=-1.5 EndY=69.25 EndZ=0
    g25: LineSegment StartX=-49.19 StartY=66.25 StartZ=0 EndX=-1.5 EndY=66.25 EndZ=0
    g26: LineSegment StartX=-49.19 StartY=63.5 StartZ=0 EndX=-1.5 EndY=63.5 EndZ=0
    g27: LineSegment StartX=-49.19 StartY=60.5 StartZ=0 EndX=-1.5 EndY=60.5 EndZ=0
    g28: LineSegment StartX=-49.19 StartY=57.75 StartZ=0 EndX=-1.5 EndY=57.75 EndZ=0
    g29: LineSegment StartX=-49.19 StartY=54.75 StartZ=0 EndX=-1.5 EndY=54.75 EndZ=0
    g30: LineSegment StartX=-49.19 StartY=52 StartZ=0 EndX=-11.49 EndY=52 EndZ=0
    g31: LineSegment StartX=-49.19 StartY=49 StartZ=0 EndX=-11.49 EndY=49 EndZ=0
    g32: LineSegment StartX=-49.19 StartY=46.25 StartZ=0 EndX=-16.28 EndY=46.25 EndZ=0
    g33: LineSegment StartX=-49.19 StartY=43.25 StartZ=0 EndX=-16.28 EndY=43.25 EndZ=0
    g34: LineSegment StartX=-49.19 StartY=40.5 StartZ=0 EndX=-18.2337 EndY=40.5 EndZ=0
    g35: LineSegment StartX=-49.19 StartY=37.5 StartZ=0 EndX=-18.23 EndY=37.5 EndZ=0
    g36: LineSegment StartX=-49.19 StartY=34.5 StartZ=0 EndX=-18.2337 EndY=34.5 EndZ=0
    g37: LineSegment StartX=-49.19 StartY=31.5 StartZ=0 EndX=-18.23 EndY=31.5 EndZ=0
    g38: LineSegment StartX=-49.19 StartY=28.75 StartZ=0 EndX=-16.2837 EndY=28.75 EndZ=0
    g39: LineSegment StartX=-49.19 StartY=25.75 StartZ=0 EndX=-16.28 EndY=25.75 EndZ=0
    g40: LineSegment StartX=-49.19 StartY=23 StartZ=0 EndX=-11.49 EndY=23 EndZ=0
    g41: LineSegment StartX=-49.19 StartY=20 StartZ=0 EndX=-11.49 EndY=20 EndZ=0
    g42: LineSegment StartX=-49.19 StartY=17.25 StartZ=0 EndX=-1.5 EndY=17.25 EndZ=0
    g43: LineSegment StartX=-49.19 StartY=14.25 StartZ=0 EndX=-1.5 EndY=14.25 EndZ=0
    g44: LineSegment StartX=-49.19 StartY=11.5 StartZ=0 EndX=-1.5 EndY=11.5 EndZ=0
    g45: LineSegment StartX=-49.19 StartY=8.5 StartZ=0 EndX=-1.5 EndY=8.5 EndZ=0
    g46: LineSegment StartX=-49.19 StartY=5.75 StartZ=0 EndX=-1.5 EndY=5.75 EndZ=0
    g47: LineSegment StartX=-49.19 StartY=2.75 StartZ=0 EndX=-1.5 EndY=2.75 EndZ=0
  constraints (120):
    c: Vertical(g0)
    c: Distance(g0) = 3
    c: Block(g0)
    c: Vertical(g1)
    c: Distance(g1) = 3
    c: Vertical(g2)
    c: Equal(g0,g2) = 3
    c: Block(g2)
    c: Vertical(g3)
    c: Equal(g1,g3) = 3
    c: Vertical(g4)
    c: Equal(g0,g4) = 3
    c: Block(g4)
    c: Vertical(g5)
    c: Equal(g1,g5) = 3
    c: Vertical(g6)
    c: Equal(g0,g6) = 3
    c: Block(g6)
    c: Vertical(g7)
    c: Equal(g1,g7) = 3
    c: Vertical(g8)
    c: Equal(g0,g8) = 3
    c: Block(g8)
    c: Vertical(g9)
    c: Equal(g1,g9) = 3
    c: Vertical(g10)
    c: Equal(g0,g10) = 3
    c: Block(g10)
    c: Vertical(g11)
    c: Equal(g1,g11) = 3
    c: Block(g12)
    c: Block(g13)
    c: Block(g14)
    c: Block(g15)
    c: Block(g16)
    c: Block(g17)
    c: Block(g18)
    c: Block(g19)
    c: Block(g20)
    c: Block(g21)
    c: Block(g22)
    c: Block(g23)
    c: Block(g11)
    c: Block(g9)
    c: Block(g7)
    c: Block(g5)
    c: Block(g3)
    c: Block(g1)
    c: Coincident(g24,g0)
    c: Coincident(g24,g12)
    c: Horizontal(g24)
    c: Coincident(g25,g0)
    c: Coincident(g25,g12)
    c: Horizontal(g25)
    c: Coincident(g26,g1)
    c: Coincident(g26,g13)
    c: Horizontal(g26)
    c: Coincident(g27,g1)
    c: Coincident(g27,g13)
    c: Horizontal(g27)
    c: Coincident(g28,g2)
    c: Coincident(g28,g14)
    c: Horizontal(g28)
    c: Coincident(g29,g2)
    c: Coincident(g29,g14)
    c: Horizontal(g29)
    c: Coincident(g30,g3)
    c: Coincident(g30,g15)
    c: Horizontal(g30)
    c: Coincident(g31,g3)
    c: Coincident(g31,g15)
    c: Horizontal(g31)
    c: Coincident(g32,g4)
    c: Coincident(g32,g16)
    c: Horizontal(g32)
    c: Coincident(g33,g4)
    c: Coincident(g33,g16)
    c: Horizontal(g33)
    c: Coincident(g34,g5)
    c: Coincident(g34,g17)
    c: Horizontal(g34)
    c: Coincident(g35,g5)
    c: Coincident(g35,g17)
    c: Horizontal(g35)
    c: Coincident(g36,g6)
    c: Coincident(g36,g19)
    c: Horizontal(g36)
    c: Coincident(g37,g6)
    c: Coincident(g37,g19)
    c: Horizontal(g37)
    c: Coincident(g38,g7)
    c: Coincident(g38,g18)
    c: Horizontal(g38)
    c: Coincident(g39,g7)
    c: Coincident(g39,g18)
    c: Horizontal(g39)
    c: Coincident(g40,g8)
    c: Coincident(g40,g20)
    c: Horizontal(g40)
    c: Coincident(g41,g8)
    c: Coincident(g41,g20)
    c: Horizontal(g41)
    c: Coincident(g42,g9)
    c: Coincident(g42,g23)
    c: Horizontal(g42)
    c: Coincident(g43,g9)
    c: Coincident(g43,g23)
    c: Horizontal(g43)
    c: Coincident(g44,g10)
    c: Coincident(g44,g22)
    c: Horizontal(g44)
    c: Coincident(g45,g10)
    c: Coincident(g45,g22)
    c: Horizontal(g45)
    c: Coincident(g46,g11)
    c: Coincident(g46,g21)
    c: Horizontal(g46)
    c: Coincident(g47,g11)
    c: Coincident(g47,g21)
    c: Horizontal(g47)
FEATURE [Part::Extrusion] Extrude023
  Base = -> Sketch032
  Dir = (1,-2e-16,2e-16)
  DirMode = 2
  FaceMakerClass = Part::FaceMakerBullseye
  LengthFwd = 19
  LengthRev = 0
  Placement = pos=(-19,0,0) rot=(0,0,1;0rad)
  Solid = true
  Symmetric = false
FEATURE [Part::Fillet] Fillet023
  Base = -> Extrude023
  Edges = <same value as first occurrence — deduplicated (x6 in doc)>
  Placement = pos=(0,0.05,0) rot=(0,0,1;0rad)
FEATURE [Part::Cut] Cut014  label="bottom003"
  Base = -> Cut007
  Tool = -> Fusion047
FEATURE [Part::Cut] Cut021  label="bottom004"
  Base = -> Cut014
  Tool = -> Fillet023
FEATURE [Sketcher::SketchObject] Sketch033
  FullyConstrained = true
  Placement = pos=(117,19,0) rot=(0.57735,0.57735,0.57735;2.0944rad)
  sketch-geometry (8):
    g0: LineSegment StartX=-49.19 StartY=69.25 StartZ=0 EndX=-49.19 EndY=66.25 EndZ=0
    g1: LineSegment StartX=-49.19 StartY=5.75 StartZ=0 EndX=-49.19 EndY=2.75 EndZ=0
    g2: ArcOfCircle CenterX=-1.5 CenterY=67.75 CenterZ=0 NormalX=0 NormalY=0 NormalZ=1 AngleXU=0 Radius=1.5 StartAngle=4.71239 EndAngle=7.85398
    g3: ArcOfCircle CenterX=-1.5 CenterY=4.25 CenterZ=0 NormalX=0 NormalY=0 NormalZ=1 AngleXU=0 Radius=1.5 StartAngle=4.71239 EndAngle=7.85398
    g4: LineSegment StartX=-49.19 StartY=69.25 StartZ=0 EndX=-1.5 EndY=69.25 EndZ=0
    g5: LineSegment StartX=-49.19 StartY=66.25 StartZ=0 EndX=-1.5 EndY=66.25 EndZ=0
    g6: LineSegment StartX=-49.19 StartY=5.75 StartZ=0 EndX=-1.5 EndY=5.75 EndZ=0
    g7: LineSegment StartX=-49.19 StartY=2.75 StartZ=0 EndX=-1.5 EndY=2.75 EndZ=0
  constraints (19):
    c: Vertical(g0)
    c: Distance(g0) = 3
    c: Block(g0)
    c: Vertical(g1)
    c: Block(g2)
    c: Block(g3)
    c: Block(g1)
    c: Coincident(g4,g0)
    c: Coincident(g4,g2)
    c: Horizontal(g4)
    c: Coincident(g5,g0)
    c: Coincident(g5,g2)
    c: Horizontal(g5)
    c: Coincident(g6,g1)
    c: Coincident(g6,g3)
    c: Horizontal(g6)
    c: Coincident(g7,g1)
    c: Coincident(g7,g3)
    c: Horizontal(g7)
FEATURE [Sketcher::SketchObject] Sketch034
  FullyConstrained = true
  Placement = pos=(117,19,0) rot=(0.57735,0.57735,0.57735;2.0944rad)
  sketch-geometry (8):
    g0: LineSegment StartX=-49.19 StartY=63.5 StartZ=0 EndX=-49.19 EndY=60.5 EndZ=0
    g1: LineSegment StartX=-49.19 StartY=11.5 StartZ=0 EndX=-49.19 EndY=8.5 EndZ=0
    g2: ArcOfCircle CenterX=-1.5 CenterY=62 CenterZ=0 NormalX=0 NormalY=0 NormalZ=1 AngleXU=0 Radius=1.5 StartAngle=4.71239 EndAngle=7.85398
    g3: ArcOfCircle CenterX=-1.5 CenterY=10 CenterZ=0 NormalX=0 NormalY=0 NormalZ=1 AngleXU=0 Radius=1.5 StartAngle=4.71239 EndAngle=7.85398
    g4: LineSegment StartX=-49.19 StartY=63.5 StartZ=0 EndX=-1.5 EndY=63.5 EndZ=0
    g5: LineSegment StartX=-49.19 StartY=60.5 StartZ=0 EndX=-1.5 EndY=60.5 EndZ=0
    g6: LineSegment StartX=-49.19 StartY=11.5 StartZ=0 EndX=-1.5 EndY=11.5 EndZ=0
    g7: LineSegment StartX=-49.19 StartY=8.5 StartZ=0 EndX=-1.5 EndY=8.5 EndZ=0
  constraints (19):
    c: Vertical(g0)
    c: Distance(g0) = 3
    c: Vertical(g1)
    c: Block(g1)
    c: Block(g2)
    c: Block(g3)
    c: Block(g0)
    c: Coincident(g4,g0)
    c: Coincident(g4,g2)
    c: Horizontal(g4)
    c: Coincident(g5,g0)
    c: Coincident(g5,g2)
    c: Horizontal(g5)
    c: Coincident(g6,g1)
    c: Coincident(g6,g3)
    c: Horizontal(g6)
    c: Coincident(g7,g1)
    c: Coincident(g7,g3)
    c: Horizontal(g7)
FEATURE [Part::Extrusion] Extrude024
  Base = -> Sketch033
  Dir = (1,0,0)
  DirMode = 2
  FaceMakerClass = Part::FaceMakerBullseye
  LengthFwd = 10
  LengthRev = 0
  Solid = true
  Symmetric = false
FEATURE [Part::Extrusion] Extrude025
  Base = -> Sketch034
  Dir = (1,0,0)
  DirMode = 2
  FaceMakerClass = Part::FaceMakerBullseye
  LengthFwd = 10
  LengthRev = 0
  Solid = true
  Symmetric = false
FEATURE [Part::Fillet] Fillet024  label="removeFromtMoreFrontCaseScrewRetainers"
  Base = -> Extrude024
  Edges = 4 edges r=1.49: [Edge6,Edge11,Edge18,Edge23]
  Placement = pos=(-11,0,0) rot=(0,0,1;0rad)
FEATURE [Part::Fillet] Fillet025  label="removeFromtMoreFrontCaseScrewRetainers001"
  Base = -> Extrude025
  Edges = 4 edges r=1.49: [Edge6,Edge11,Edge18,Edge23]
  Placement = pos=(-19,0,0) rot=(0,0,1;0rad)
FEATURE [Part::Cut] Cut022
  Base = -> Cut015
  Tool = -> Fillet025
FEATURE [Part::Cut] Cut023  label="screwRetainers"
  Base = -> Cut022
  Tool = -> Fillet024
FEATURE [Part::MultiFuse] Fusion056  label="bottom005"
  Shapes = -> [Fusion044,Cut021]
FEATURE [Part::MultiFuse] Fusion057  label="casePillars001"
  Shapes = -> [Cut016,Fusion052]
FEATURE [Part::MultiFuse] Fusion058  label="bottom006"
  Shapes = -> [Fusion056,Cut023]
FEATURE [Part::MultiFuse] Fusion059  label="bottom007"
  Shapes = -> [Fusion058,Fillet005]
FEATURE [Part::MultiFuse] Fusion060  label="bottom008"
  Shapes = -> [Fusion059,Fusion]
FEATURE [Part::MultiFuse] Fusion061  label="top011"
  Shapes = -> [Cut006,Cut020]
FEATURE [Part::MultiFuse] Fusion062  label="top012"
  Shapes = -> [Fusion057,Fusion061]
FEATURE [Sketcher::SketchObject] Sketch035  label="topSketch007"
  FullyConstrained = true
  sketch-geometry (6):
    g0: LineSegment StartX=19 StartY=38 StartZ=0 EndX=117 EndY=38 EndZ=0
    g1: ArcOfCircle CenterX=19 CenterY=19 CenterZ=0 NormalX=0 NormalY=0 NormalZ=1 AngleXU=0 Radius=19 StartAngle=1.5708 EndAngle=3.14159
    g2: LineSegment StartX=117 StartY=38 StartZ=0 EndX=117 EndY=19 EndZ=0
    g3: LineSegment StartX=98 StartY=1.0161e-12 StartZ=0 EndX=5.22862e-06 EndY=1.0161e-12 EndZ=0
    g4: LineSegment StartX=5.22862e-06 StartY=19 StartZ=0 EndX=5.22862e-06 EndY=1.0161e-12 EndZ=0
    g5: ArcOfCircle CenterX=98 CenterY=19 CenterZ=0 NormalX=0 NormalY=0 NormalZ=1 AngleXU=0 Radius=19 StartAngle=4.71239 EndAngle=6.28319
  constraints (16):
    c: Horizontal(g0)
    c: Distance(g0) = 98
    c: Coincident(g1,g0)
    c: Block(g1)
    c: Coincident(g2,g0)
    c: Vertical(g2)
    c: Distance(g2) = 19
    c: Horizontal(g3)
    c: Coincident(g4,g1)
    c: Vertical(g4)
    c: Coincident(g3,g4)
    c: Block(g3)
    c: Coincident(g5,g2)
    c: Coincident(g5,g3)
    c: Block(g0)
    c: Block(g5)
FEATURE [Part::Extrusion] Extrude026  label="sideA001"
  Base = -> Sketch035
  Dir = (0,0,1)
  DirMode = 2
  FaceMakerClass = Part::FaceMakerBullseye
  LengthFwd = 3
  LengthRev = 0
  Placement = pos=(0,0,-2.7) rot=(0,0,1;0rad)
  Solid = true
  Symmetric = false
FEATURE [Sketcher::SketchObject] Sketch036  label="topSketch008"
  FullyConstrained = true
  sketch-geometry (6):
    g0: LineSegment StartX=19 StartY=38 StartZ=0 EndX=117 EndY=38 EndZ=0
    g1: ArcOfCircle CenterX=19 CenterY=19 CenterZ=0 NormalX=0 NormalY=0 NormalZ=1 AngleXU=0 Radius=19 StartAngle=1.5708 EndAngle=3.14159
    g2: LineSegment StartX=117 StartY=38 StartZ=0 EndX=117 EndY=19 EndZ=0
    g3: LineSegment StartX=98 StartY=1.0161e-12 StartZ=0 EndX=5.22862e-06 EndY=1.0161e-12 EndZ=0
    g4: LineSegment StartX=5.22862e-06 StartY=19 StartZ=0 EndX=5.22862e-06 EndY=1.0161e-12 EndZ=0
    g5: ArcOfCircle CenterX=98 CenterY=19 CenterZ=0 NormalX=0 NormalY=0 NormalZ=1 AngleXU=0 Radius=19 StartAngle=4.71239 EndAngle=6.28319
  constraints (16):
    c: Horizontal(g0)
    c: Distance(g0) = 98
    c: Coincident(g1,g0)
    c: Block(g1)
    c: Coincident(g2,g0)
    c: Vertical(g2)
    c: Distance(g2) = 19
    c: Horizontal(g3)
    c: Coincident(g4,g1)
    c: Vertical(g4)
    c: Coincident(g3,g4)
    c: Block(g3)
    c: Coincident(g5,g2)
    c: Coincident(g5,g3)
    c: Block(g0)
    c: Block(g5)
FEATURE [Part::Extrusion] Extrude027  label="sideB001"
  Base = -> Sketch036
  Dir = (0,0,1)
  DirMode = 2
  FaceMakerClass = Part::FaceMakerBullseye
  LengthFwd = 3
  LengthRev = 0
  Placement = pos=(0,0,71.7) rot=(0,0,1;0rad)
  Solid = true
  Symmetric = false
FEATURE [Part::MultiFuse] Fusion064  label="removeFromBottom"
  Shapes = -> [Extrude026,Extrude027]
FEATURE [Part::Cut] Cut024  label="bottom009"
  Base = -> Fusion060
  Tool = -> Fusion064
FEATURE [Sketcher::SketchObject] Sketch037  label="topSketch009"
  FullyConstrained = true
  sketch-geometry (8):
    g0: ArcOfCircle CenterX=19 CenterY=19.1201 CenterZ=0 NormalX=0 NormalY=0 NormalZ=1 AngleXU=0 Radius=18.8799 StartAngle=1.5708 EndAngle=3.14793
    g1: LineSegment StartX=0.120501 StartY=19.0004 StartZ=0 EndX=0.120501 EndY=0.000382114 EndZ=0
    g2: LineSegment StartX=19 StartY=38 StartZ=0 EndX=124 EndY=38 EndZ=0
    g3: LineSegment StartX=0.120501 StartY=0.000382114 StartZ=0 EndX=105.121 EndY=0.000382114 EndZ=0
    g4: LineSegment StartX=124 StartY=38 StartZ=0 EndX=125.616 EndY=38 EndZ=0
    g5: LineSegment StartX=105.121 StartY=0.000382114 StartZ=0 EndX=106.736 EndY=0.000382114 EndZ=0
    g6: ArcOfCircle CenterX=106.616 CenterY=19 CenterZ=0 NormalX=0 NormalY=0 NormalZ=1 AngleXU=0 Radius=19 StartAngle=4.71873 EndAngle=6.28319
    g7: LineSegment StartX=125.616 StartY=38 StartZ=0 EndX=125.616 EndY=19 EndZ=0
  constraints (21):
    c: Block(g0)
    c: Coincident(g1,g0)
    c: Vertical(g1)
    c: Horizontal(g2)
    c: Distance(g2) = 105
    c: Coincident(g2,g0)
    c: Distance(g1) = 19
    c: Coincident(g3,g1)
    c: Horizontal(g3)
    c: Distance(g3) = 105
    c: Coincident(g4,g2)
    c: Horizontal(g4)
    c: Distance(g4) = 1.61553
    c: Horizontal(g5)
    c: Equal(g4,g5) = 1.61553
    c: Coincident(g5,g3)
    c: Block(g6)
    c: Coincident(g6,g5)
    c: Coincident(g7,g4)
    c: Coincident(g7,g6)
    c: Vertical(g7)
FEATURE [Part::Extrusion] Extrude028  label="sideB"
  Base = -> Sketch037
  Dir = (0,0,1)
  DirMode = 2
  FaceMakerClass = Part::FaceMakerBullseye
  LengthFwd = 3
  LengthRev = 0
  Placement = pos=(0,0,72) rot=(0,0,1;0rad)
  Solid = true
  Symmetric = false
FEATURE [Sketcher::SketchObject] Sketch038  label="topSketch010"
  FullyConstrained = true
  sketch-geometry (22):
    g0: LineSegment StartX=5.21097e-06 StartY=3 StartZ=0 EndX=5.21097e-06 EndY=19 EndZ=0
    g1: ArcOfCircle CenterX=19 CenterY=19 CenterZ=0 NormalX=0 NormalY=0 NormalZ=1 AngleXU=0 Radius=19 StartAngle=1.5708 EndAngle=3.14159
    g2: ArcOfCircle CenterX=19 CenterY=19 CenterZ=0 NormalX=0 NormalY=0 NormalZ=1 AngleXU=0 Radius=16 StartAngle=1.5708 EndAngle=3.14159
    g3: LineSegment StartX=114 StartY=35 StartZ=0 EndX=19 EndY=35 EndZ=0
    g4: LineSegment StartX=5.21097e-06 StartY=3 StartZ=0 EndX=5.21097e-06 EndY=0 EndZ=0
    g5: LineSegment StartX=3 StartY=0 StartZ=0 EndX=5.21097e-06 EndY=0 EndZ=0
    g6: LineSegment StartX=3 StartY=19 StartZ=0 EndX=3 EndY=0 EndZ=0
    g7: LineSegment StartX=19 StartY=38 StartZ=0 EndX=124 EndY=38 EndZ=0
    g8: Circle CenterX=119 CenterY=35 CenterZ=0 NormalX=0 NormalY=0 NormalZ=1 AngleXU=0 Radius=1
    g9: Circle CenterX=121 CenterY=35 CenterZ=0 NormalX=0 NormalY=0 NormalZ=1 AngleXU=0 Radius=1
    g10: Circle CenterX=121 CenterY=33 CenterZ=0 NormalX=0 NormalY=0 NormalZ=1 AngleXU=0 Radius=1
    g11: BSplineCurve PolesCount=3 KnotsCount=2 Degree=2 IsPeriodic=0
    g12: GeomPoint X=119 Y=35 Z=0
    g13: GeomPoint X=121 Y=33 Z=0
    g14: LineSegment StartX=119 StartY=35 StartZ=0 EndX=114 EndY=35 EndZ=0
    g15: ArcOfCircle CenterX=105 CenterY=19 CenterZ=0 NormalX=0 NormalY=0 NormalZ=1 AngleXU=0 Radius=16 StartAngle=5.60905 EndAngle=6.28319
    g16: LineSegment StartX=121 StartY=33 StartZ=0 EndX=121 EndY=19 EndZ=0
    g17: LineSegment StartX=117.5 StartY=9.01251 StartZ=0 EndX=121.163 EndY=9.0125 EndZ=0
    g18: ArcOfCircle CenterX=105 CenterY=19 CenterZ=0 NormalX=0 NormalY=0 NormalZ=1 AngleXU=0 Radius=20.6155 StartAngle=5.7297 EndAngle=6.28319
    g19: LineSegment StartX=121.163 StartY=9.0125 StartZ=0 EndX=122.538 EndY=8.16329 EndZ=0
    g20: LineSegment StartX=124 StartY=38 StartZ=0 EndX=125.616 EndY=38 EndZ=0
    g21: LineSegment StartX=125.616 StartY=19 StartZ=0 EndX=125.616 EndY=38 EndZ=0
  constraints (49):
    c: Vertical(g0)
    c: Block(g0)
    c: Coincident(g1,g0)
    c: Block(g1)
    c: Coincident(g2,g1)
    c: Block(g2)
    c: Coincident(g3,g2)
    c: Horizontal(g3)
    c: Tangent(g3,g2)
    c: Coincident(g4,g0)
    c: Distance(g4) = 3
    c: Vertical(g4)
    c: Coincident(g5,g4)
    c: Horizontal(g5)
    c: Coincident(g6,g2)
    c: Coincident(g6,g5)
    c: Vertical(g6)
    c: Horizontal(g7)
    c: Distance(g7) = 105
    c: Coincident(g7,g1)
    c: Block(g3)
    c: Weight(g8) = 1
    c: Equal(g8,g9)
    c: Equal(g8,g10)
    c: InternalAlignment(g8,g11)
    c: InternalAlignment(g9,g11)
    c: InternalAlignment(g10,g11)
    c: InternalAlignment(g12,g11)
    c: InternalAlignment(g13,g11)
    c: Block(g11)
    c: Coincident(g14,g11)
    c: Coincident(g14,g3)
    c: Horizontal(g14)
    c: Block(g15)
    c: Coincident(g16,g11)
    c: Coincident(g16,g15)
    c: Vertical(g16)
    c: Distance(g16) = 14
    c: Coincident(g17,g15)
    c: Block(g18)
    c: Coincident(g19,g18)
    c: Coincident(g20,g7)
    c: Horizontal(g20)
    c: Vertical(g21)
    c: Coincident(g20,g21)
    c: Block(g20)
    c: Block(g21)
    c: Block(g19)
    c: Block(g17)
FEATURE [Part::Extrusion] Extrude029
  Base = -> Sketch038
  Dir = (0,0,1)
  DirMode = 2
  FaceMakerClass = Part::FaceMakerBullseye
  LengthFwd = 72
  LengthRev = 0
  Solid = true
  Symmetric = false
FEATURE [Part::Feature] Face085
  shape: bbox 4.8 x 25.5 x 2e-07 mm, 1 faces, 0 solids (baked)
FEATURE [Part::Revolution] Revolve089  label="moreFrontCaseScrewPost003"
  Angle = 360
  Axis = (0,1,0)
  Base = (0,0,0)
  FaceMakerClass = Part::FaceMakerBullseye
  Placement = pos=(109.5,4.5,3.5) rot=(0,0,1;0rad)
  Solid = false
  Source = -> Face085
  Symmetric = false
FEATURE [Part::Feature] Face086
  shape: bbox 4.8 x 25.5 x 2e-07 mm, 1 faces, 0 solids (baked)
FEATURE [Part::Revolution] Revolve090  label="moreFrontCaseScrewPost004"
  Angle = 360
  Axis = (0,1,0)
  Base = (0,0,0)
  FaceMakerClass = Part::FaceMakerBullseye
  Placement = pos=(109.5,4.5,68.5) rot=(0,0,1;0rad)
  Solid = false
  Source = -> Face086
  Symmetric = false
FEATURE [Part::Fillet] Fillet026  label="top013"
  Base = -> Extrude029
  Edges = 1 edges r=2: [Edge35]
FEATURE [Sketcher::SketchObject] Sketch039
  FullyConstrained = true
  sketch-geometry (7):
    g0: LineSegment StartX=0 StartY=0 StartZ=0 EndX=0 EndY=6 EndZ=0
    g1: Circle CenterX=0 CenterY=0 CenterZ=0 NormalX=0 NormalY=0 NormalZ=1 AngleXU=0 Radius=1
    g2: Circle CenterX=8 CenterY=6 CenterZ=0 NormalX=0 NormalY=0 NormalZ=1 AngleXU=0 Radius=1
    g3: BSplineCurve PolesCount=3 KnotsCount=2 Degree=2 IsPeriodic=0
    g4: GeomPoint X=0 Y=0 Z=0
    g5: GeomPoint X=8 Y=6 Z=0
    g6: LineSegment StartX=0 StartY=6 StartZ=0 EndX=8 EndY=6 EndZ=0
  constraints (14):
    c: Coincident(g0,g-1)
    c: Distance(g0) = 6
    c: Vertical(g0)
    c: Coincident(g3,g0)
    c: Weight(g1) = 1
    c: Equal(g1,g2)
    c: InternalAlignment(g1,g3)
    c: InternalAlignment(g2,g3)
    c: InternalAlignment(g4,g3)
    c: InternalAlignment(g5,g3)
    c: Block(g3)
    c: Coincident(g6,g0)
    c: Coincident(g6,g3)
    c: Horizontal(g6)
FEATURE [Sketcher::SketchObject] Sketch040
  FullyConstrained = true
  sketch-geometry (7):
    g0: LineSegment StartX=0 StartY=0 StartZ=0 EndX=0 EndY=6 EndZ=0
    g1: Circle CenterX=0 CenterY=0 CenterZ=0 NormalX=0 NormalY=0 NormalZ=1 AngleXU=0 Radius=1
    g2: Circle CenterX=8 CenterY=6 CenterZ=0 NormalX=0 NormalY=0 NormalZ=1 AngleXU=0 Radius=1
    g3: BSplineCurve PolesCount=3 KnotsCount=2 Degree=2 IsPeriodic=0
    g4: GeomPoint X=0 Y=0 Z=0
    g5: GeomPoint X=8 Y=6 Z=0
    g6: LineSegment StartX=0 StartY=6 StartZ=0 EndX=8 EndY=6 EndZ=0
  constraints (14):
    c: Coincident(g0,g-1)
    c: Distance(g0) = 6
    c: Vertical(g0)
    c: Coincident(g3,g0)
    c: Weight(g1) = 1
    c: Equal(g1,g2)
    c: InternalAlignment(g1,g3)
    c: InternalAlignment(g2,g3)
    c: InternalAlignment(g4,g3)
    c: InternalAlignment(g5,g3)
    c: Block(g3)
    c: Coincident(g6,g0)
    c: Coincident(g6,g3)
    c: Horizontal(g6)
FEATURE [Sketcher::SketchObject] Sketch041
  FullyConstrained = true
  sketch-geometry (7):
    g0: LineSegment StartX=0 StartY=0 StartZ=0 EndX=0 EndY=6 EndZ=0
    g1: Circle CenterX=0 CenterY=0 CenterZ=0 NormalX=0 NormalY=0 NormalZ=1 AngleXU=0 Radius=1
    g2: Circle CenterX=8 CenterY=6 CenterZ=0 NormalX=0 NormalY=0 NormalZ=1 AngleXU=0 Radius=1
    g3: BSplineCurve PolesCount=3 KnotsCount=2 Degree=2 IsPeriodic=0
    g4: GeomPoint X=0 Y=0 Z=0
    g5: GeomPoint X=8 Y=6 Z=0
    g6: LineSegment StartX=0 StartY=6 StartZ=0 EndX=8 EndY=6 EndZ=0
  constraints (14):
    c: Coincident(g0,g-1)
    c: Distance(g0) = 6
    c: Vertical(g0)
    c: Coincident(g3,g0)
    c: Weight(g1) = 1
    c: Equal(g1,g2)
    c: InternalAlignment(g1,g3)
    c: InternalAlignment(g2,g3)
    c: InternalAlignment(g4,g3)
    c: InternalAlignment(g5,g3)
    c: Block(g3)
    c: Coincident(g6,g0)
    c: Coincident(g6,g3)
    c: Horizontal(g6)
FEATURE [Sketcher::SketchObject] Sketch042
  FullyConstrained = true
  sketch-geometry (7):
    g0: LineSegment StartX=0 StartY=0 StartZ=0 EndX=0 EndY=6 EndZ=0
    g1: Circle CenterX=0 CenterY=0 CenterZ=0 NormalX=0 NormalY=0 NormalZ=1 AngleXU=0 Radius=1
    g2: Circle CenterX=8 CenterY=6 CenterZ=0 NormalX=0 NormalY=0 NormalZ=1 AngleXU=0 Radius=1
    g3: BSplineCurve PolesCount=3 KnotsCount=2 Degree=2 IsPeriodic=0
    g4: GeomPoint X=0 Y=0 Z=0
    g5: GeomPoint X=8 Y=6 Z=0
    g6: LineSegment StartX=0 StartY=6 StartZ=0 EndX=8 EndY=6 EndZ=0
  constraints (14):
    c: Coincident(g0,g-1)
    c: Distance(g0) = 6
    c: Vertical(g0)
    c: Coincident(g3,g0)
    c: Weight(g1) = 1
    c: Equal(g1,g2)
    c: InternalAlignment(g1,g3)
    c: InternalAlignment(g2,g3)
    c: InternalAlignment(g4,g3)
    c: InternalAlignment(g5,g3)
    c: Block(g3)
    c: Coincident(g6,g0)
    c: Coincident(g6,g3)
    c: Horizontal(g6)
FEATURE [Part::Extrusion] Extrude030  label="caseScrewPillarBracket008"
  Base = -> Sketch039
  Dir = (0,0,1)
  DirMode = 2
  FaceMakerClass = Part::FaceMakerBullseye
  LengthFwd = 2.4
  LengthRev = 0
  Placement = pos=(15.76,29,8.8) rot=(0,1,0;0rad)
  Solid = true
  Symmetric = false
FEATURE [Part::Extrusion] Extrude031  label="caseScrewPillarBracket009"
  Base = -> Sketch040
  Dir = (0,0,1)
  DirMode = 2
  FaceMakerClass = Part::FaceMakerBullseye
  LengthFwd = 2.4
  LengthRev = 0
  Placement = pos=(15.76,29,60.8) rot=(0,0,1;0rad)
  Solid = true
  Symmetric = false
FEATURE [Part::Extrusion] Extrude032  label="caseScrewPillarBracket010"
  Base = -> Sketch041
  Dir = (0,0,1)
  DirMode = 2
  FaceMakerClass = Part::FaceMakerBullseye
  LengthFwd = 2.4
  LengthRev = 0
  Placement = pos=(13.7,29,13.26) rot=(0,-1,0;1.5708rad)
  Solid = true
  Symmetric = false
FEATURE [Part::Extrusion] Extrude033  label="caseScrewPillarBracket011"
  Base = -> Sketch042
  Dir = (0,0,1)
  DirMode = 2
  FaceMakerClass = Part::FaceMakerBullseye
  LengthFwd = 2.4
  LengthRev = 0
  Placement = pos=(11.3,29,58.74) rot=(0,1,0;1.5708rad)
  Solid = true
  Symmetric = false
FEATURE [Sketcher::SketchObject] Sketch043
  FullyConstrained = true
  sketch-geometry (7):
    g0: LineSegment StartX=0 StartY=0 StartZ=0 EndX=0 EndY=6 EndZ=0
    g1: Circle CenterX=0 CenterY=0 CenterZ=0 NormalX=0 NormalY=0 NormalZ=1 AngleXU=0 Radius=1
    g2: Circle CenterX=8 CenterY=6 CenterZ=0 NormalX=0 NormalY=0 NormalZ=1 AngleXU=0 Radius=1
    g3: BSplineCurve PolesCount=3 KnotsCount=2 Degree=2 IsPeriodic=0
    g4: GeomPoint X=0 Y=0 Z=0
    g5: GeomPoint X=8 Y=6 Z=0
    g6: LineSegment StartX=0 StartY=6 StartZ=0 EndX=8 EndY=6 EndZ=0
  constraints (14):
    c: Coincident(g0,g-1)
    c: Distance(g0) = 6
    c: Vertical(g0)
    c: Coincident(g3,g0)
    c: Weight(g1) = 1
    c: Equal(g1,g2)
    c: InternalAlignment(g1,g3)
    c: InternalAlignment(g2,g3)
    c: InternalAlignment(g4,g3)
    c: InternalAlignment(g5,g3)
    c: Block(g3)
    c: Coincident(g6,g0)
    c: Coincident(g6,g3)
    c: Horizontal(g6)
FEATURE [Part::Extrusion] Extrude034  label="caseScrewPillarBracket012"
  Base = -> Sketch043
  Dir = (0,0,1)
  DirMode = 2
  FaceMakerClass = Part::FaceMakerBullseye
  LengthFwd = 2.4
  LengthRev = 0
  Placement = pos=(88.3,29,65.23) rot=(0,1,0;1.5708rad)
  Solid = true
  Symmetric = false
FEATURE [Sketcher::SketchObject] Sketch044
  FullyConstrained = true
  sketch-geometry (7):
    g0: LineSegment StartX=0 StartY=0 StartZ=0 EndX=0 EndY=6 EndZ=0
    g1: Circle CenterX=0 CenterY=0 CenterZ=0 NormalX=0 NormalY=0 NormalZ=1 AngleXU=0 Radius=1
    g2: Circle CenterX=8 CenterY=6 CenterZ=0 NormalX=0 NormalY=0 NormalZ=1 AngleXU=0 Radius=1
    g3: BSplineCurve PolesCount=3 KnotsCount=2 Degree=2 IsPeriodic=0
    g4: GeomPoint X=0 Y=0 Z=0
    g5: GeomPoint X=8 Y=6 Z=0
    g6: LineSegment StartX=0 StartY=6 StartZ=0 EndX=8 EndY=6 EndZ=0
  constraints (14):
    c: Coincident(g0,g-1)
    c: Distance(g0) = 6
    c: Vertical(g0)
    c: Coincident(g3,g0)
    c: Weight(g1) = 1
    c: Equal(g1,g2)
    c: InternalAlignment(g1,g3)
    c: InternalAlignment(g2,g3)
    c: InternalAlignment(g4,g3)
    c: InternalAlignment(g5,g3)
    c: Block(g3)
    c: Coincident(g6,g0)
    c: Coincident(g6,g3)
    c: Horizontal(g6)
FEATURE [Part::Extrusion] Extrude035  label="caseScrewPillarBracket013"
  Base = -> Sketch044
  Dir = (0,0,1)
  DirMode = 2
  FaceMakerClass = Part::FaceMakerBullseye
  LengthFwd = 2.4
  LengthRev = 0
  Placement = pos=(90.7,29,6.77) rot=(0,-1,0;1.5708rad)
  Solid = true
  Symmetric = false
FEATURE [Sketcher::SketchObject] Sketch045
  FullyConstrained = true
  sketch-geometry (7):
    g0: LineSegment StartX=0 StartY=0 StartZ=0 EndX=0 EndY=6 EndZ=0
    g1: Circle CenterX=0 CenterY=0 CenterZ=0 NormalX=0 NormalY=0 NormalZ=1 AngleXU=0 Radius=1
    g2: Circle CenterX=8 CenterY=6 CenterZ=0 NormalX=0 NormalY=0 NormalZ=1 AngleXU=0 Radius=1
    g3: BSplineCurve PolesCount=3 KnotsCount=2 Degree=2 IsPeriodic=0
    g4: GeomPoint X=0 Y=0 Z=0
    g5: GeomPoint X=8 Y=6 Z=0
    g6: LineSegment StartX=0 StartY=6 StartZ=0 EndX=8 EndY=6 EndZ=0
  constraints (14):
    c: Coincident(g0,g-1)
    c: Distance(g0) = 6
    c: Vertical(g0)
    c: Coincident(g3,g0)
    c: Weight(g1) = 1
    c: Equal(g1,g2)
    c: InternalAlignment(g1,g3)
    c: InternalAlignment(g2,g3)
    c: InternalAlignment(g4,g3)
    c: InternalAlignment(g5,g3)
    c: Block(g3)
    c: Coincident(g6,g0)
    c: Coincident(g6,g3)
    c: Horizontal(g6)
FEATURE [Sketcher::SketchObject] Sketch046
  FullyConstrained = true
  sketch-geometry (7):
    g0: LineSegment StartX=0 StartY=0 StartZ=0 EndX=0 EndY=6 EndZ=0
    g1: Circle CenterX=0 CenterY=0 CenterZ=0 NormalX=0 NormalY=0 NormalZ=1 AngleXU=0 Radius=1
    g2: Circle CenterX=8 CenterY=6 CenterZ=0 NormalX=0 NormalY=0 NormalZ=1 AngleXU=0 Radius=1
    g3: BSplineCurve PolesCount=3 KnotsCount=2 Degree=2 IsPeriodic=0
    g4: GeomPoint X=0 Y=0 Z=0
    g5: GeomPoint X=8 Y=6 Z=0
    g6: LineSegment StartX=0 StartY=6 StartZ=0 EndX=8 EndY=6 EndZ=0
  constraints (14):
    c: Coincident(g0,g-1)
    c: Distance(g0) = 6
    c: Vertical(g0)
    c: Coincident(g3,g0)
    c: Weight(g1) = 1
    c: Equal(g1,g2)
    c: InternalAlignment(g1,g3)
    c: InternalAlignment(g2,g3)
    c: InternalAlignment(g4,g3)
    c: InternalAlignment(g5,g3)
    c: Block(g3)
    c: Coincident(g6,g0)
    c: Coincident(g6,g3)
    c: Horizontal(g6)
FEATURE [Part::Extrusion] Extrude036  label="caseScrewPillarBracket014"
  Base = -> Sketch045
  Dir = (0,0,1)
  DirMode = 2
  FaceMakerClass = Part::FaceMakerBullseye
  LengthFwd = 2.4
  LengthRev = 0
  Placement = pos=(110.7,29,6.77) rot=(0,-1,0;1.5708rad)
  Solid = true
  Symmetric = false
FEATURE [Part::Extrusion] Extrude037  label="caseScrewPillarBracket015"
  Base = -> Sketch046
  Dir = (0,0,1)
  DirMode = 2
  FaceMakerClass = Part::FaceMakerBullseye
  LengthFwd = 2.4
  LengthRev = 0
  Placement = pos=(108.3,29,65.23) rot=(0,1,0;1.5708rad)
  Solid = true
  Symmetric = false
FEATURE [Part::Box] Box013  label="frontCaseScrewPillarBracket002"
  AttacherType = Attacher::AttachEngine3D
  Height = 2.4
  Length = 22
  Placement = pos=(87,28,2.3) rot=(0,0,1;0rad)
  Width = 7
FEATURE [Part::Box] Box014  label="frontCaseScrewPillarBracket003"
  AttacherType = Attacher::AttachEngine3D
  Height = 2.4
  Length = 22
  Placement = pos=(87,28,67.3) rot=(0,0,1;0rad)
  Width = 7
FEATURE [Part::Feature] Face087
  shape: bbox 4.8 x 30.2 x 2e-07 mm, 1 faces, 0 solids (baked)
FEATURE [Part::Revolution] Revolve091  label="frontCaseScrewPost004"
  Angle = 360
  Axis = (0,1,0)
  Base = (0,0,0)
  FaceMakerClass = Part::FaceMakerBullseye
  Placement = pos=(89.5,4.5,3.5) rot=(0,0,1;0rad)
  Solid = false
  Source = -> Face087
  Symmetric = false
FEATURE [Part::Feature] Face088
  shape: bbox 4.8 x 30.2 x 2e-07 mm, 1 faces, 0 solids (baked)
FEATURE [Part::Revolution] Revolve092  label="frontCaseScrewPost005"
  Angle = 360
  Axis = (0,1,0)
  Base = (0,0,0)
  FaceMakerClass = Part::FaceMakerBullseye
  Placement = pos=(89.5,4.5,68.5) rot=(0,0,1;0rad)
  Solid = false
  Source = -> Face088
  Symmetric = false
FEATURE [Part::Feature] Face089
  shape: bbox 3.5 x 30.2 x 2e-07 mm, 1 faces, 0 solids (baked)
FEATURE [Part::Revolution] Revolve093  label="backCaseScrewPost002"
  Angle = 360
  Axis = (0,1,0)
  Base = (0,0,0)
  FaceMakerClass = Part::FaceMakerBullseye
  Placement = pos=(12.5,4.5,10) rot=(0,0,1;0rad)
  Solid = false
  Source = -> Face089
  Symmetric = false
FEATURE [Part::Feature] Face090
  shape: bbox 3.5 x 30.2 x 2e-07 mm, 1 faces, 0 solids (baked)
FEATURE [Part::Revolution] Revolve094  label="backCaseScrewPost003"
  Angle = 360
  Axis = (0,1,0)
  Base = (0,0,0)
  FaceMakerClass = Part::FaceMakerBullseye
  Placement = pos=(12.5,4.5,62) rot=(0,0,1;0rad)
  Solid = false
  Source = -> Face090
  Symmetric = false
FEATURE [Part::Box] Box015  label="Cube011"
  AttacherType = Attacher::AttachEngine3D
  Height = 28.8
  Length = 3
  Placement = pos=(107.3,28,21.6) rot=(0,0,1;0rad)
  Width = 7
FEATURE [Part::Box] Box016  label="Cube012"
  AttacherType = Attacher::AttachEngine3D
  Height = 3
  Length = 7.4
  Placement = pos=(107.3,28,18.6) rot=(0,0,1;0rad)
  Width = 7
FEATURE [Part::Box] Box017  label="Cube013"
  AttacherType = Attacher::AttachEngine3D
  Height = 3
  Length = 7.4
  Placement = pos=(107.3,28,50.4) rot=(0,0,1;0rad)
  Width = 7
FEATURE [Part::Cylinder] Cylinder024
  Angle = 360
  AttacherType = Attacher::AttachEngine3D
  Height = 20
  Placement = pos=(0,0,36.15) rot=(0,0,1;0rad)
  Radius = 14.3
FEATURE [Part::Cylinder] Cylinder025
  Angle = 360
  AttacherType = Attacher::AttachEngine3D
  Height = 10
  Placement = pos=(0,0,36.15) rot=(0,0,1;0rad)
  Radius = 4
FEATURE [Part::MultiFuse] Fusion066  label="removeToCreteHoleForPlugHousing009"
  Placement = pos=(70,19,36) rot=(0,1,0;1.5708rad)
  Shapes = -> [Cylinder024,Cylinder025]
FEATURE [Part::MultiFuse] Fusion065  label="plugHousingBracketHolder002"
  Shapes = -> [Box017,Box015,Box016]
FEATURE [Part::Cut] Cut025  label="plugHousingBracketHolder003"
  Base = -> Fusion065
  Placement = pos=(7,0,0) rot=(0,0,1;0rad)
  Tool = -> Fusion066
FEATURE [Sketcher::SketchObject] Sketch047
  FullyConstrained = false
  Placement = pos=(0,0,0) rot=(1,0,0;1.5708rad)
  sketch-geometry (24):
    g0: ArcOfCircle CenterX=-4 CenterY=-10.5 CenterZ=0 NormalX=0 NormalY=0 NormalZ=1 AngleXU=0 Radius=1.5 StartAngle=6e-16 EndAngle=3.14159
    g1: ArcOfCircle CenterX=-34.2 CenterY=-10.5 CenterZ=0 NormalX=0 NormalY=0 NormalZ=1 AngleXU=0 Radius=1.5 StartAngle=0 EndAngle=3.14159
    g2: ArcOfCircle CenterX=-34.2 CenterY=-27.7 CenterZ=0 NormalX=0 NormalY=0 NormalZ=1 AngleXU=0 Radius=1.5 StartAngle=3.14159 EndAngle=6.28319
    g3: ArcOfCircle CenterX=-4 CenterY=-27.7 CenterZ=0 NormalX=0 NormalY=0 NormalZ=1 AngleXU=0 Radius=1.5 StartAngle=3.1416 EndAngle=6.28319
    g4: ArcOfCircle CenterX=-10 CenterY=-4.3 CenterZ=0 NormalX=0 NormalY=0 NormalZ=1 AngleXU=0 Radius=1.5 StartAngle=2e-16 EndAngle=3.14159
    g5: ArcOfCircle CenterX=-16.1 CenterY=-1.8 CenterZ=0 NormalX=0 NormalY=0 NormalZ=1 AngleXU=0 Radius=1.5 StartAngle=5e-16 EndAngle=3.14159
    g6: ArcOfCircle CenterX=-22.1 CenterY=-1.8 CenterZ=0 NormalX=0 NormalY=0 NormalZ=1 AngleXU=0 Radius=1.5 StartAngle=5e-16 EndAngle=3.14159
    g7: ArcOfCircle CenterX=-28.2 CenterY=-4.3 CenterZ=0 NormalX=0 NormalY=0 NormalZ=1 AngleXU=0 Radius=1.5 StartAngle=2e-16 EndAngle=3.14159
    g8: ArcOfCircle CenterX=-10 CenterY=-33.9 CenterZ=0 NormalX=0 NormalY=0 NormalZ=1 AngleXU=0 Radius=1.5 StartAngle=3.14159 EndAngle=6.28319
    g9: ArcOfCircle CenterX=-16.1 CenterY=-36.4 CenterZ=0 NormalX=0 NormalY=0 NormalZ=1 AngleXU=0 Radius=1.5 StartAngle=3.14159 EndAngle=6.28319
    g10: ArcOfCircle CenterX=-22.1 CenterY=-36.4 CenterZ=0 NormalX=0 NormalY=0 NormalZ=1 AngleXU=0 Radius=1.5 StartAngle=3.14159 EndAngle=6.28319
    g11: ArcOfCircle CenterX=-28.2 CenterY=-33.9 CenterZ=0 NormalX=0 NormalY=0 NormalZ=1 AngleXU=0 Radius=1.5 StartAngle=3.14159 EndAngle=6.28319
    g12: LineSegment StartX=-35.7 StartY=-10.5 StartZ=0 EndX=-35.7 EndY=-27.7 EndZ=0
    g13: LineSegment StartX=-32.7 StartY=-10.5 StartZ=0 EndX=-32.7 EndY=-27.7 EndZ=0
    g14: LineSegment StartX=-29.7 StartY=-33.9 StartZ=0 EndX=-29.7 EndY=-4.3 EndZ=0
    g15: LineSegment StartX=-26.7 StartY=-33.9 StartZ=0 EndX=-26.7 EndY=-4.3 EndZ=0
    g16: LineSegment StartX=-2.5 StartY=-10.5 StartZ=0 EndX=-2.5 EndY=-27.7 EndZ=0
    g17: LineSegment StartX=-8.5 StartY=-4.3 StartZ=0 EndX=-8.5 EndY=-33.9 EndZ=0
    g18: LineSegment StartX=-5.5 StartY=-10.5 StartZ=0 EndX=-5.5 EndY=-27.7 EndZ=0
    g19: LineSegment StartX=-11.5 StartY=-4.3 StartZ=0 EndX=-11.5 EndY=-33.9 EndZ=0
    g20: LineSegment StartX=-14.6 StartY=-1.8 StartZ=0 EndX=-14.6 EndY=-36.4 EndZ=0
    g21: LineSegment StartX=-17.6 StartY=-1.8 StartZ=0 EndX=-17.6 EndY=-36.4 EndZ=0
    g22: LineSegment StartX=-20.6 StartY=-36.4 StartZ=0 EndX=-20.6 EndY=-1.8 EndZ=0
    g23: LineSegment StartX=-23.6 StartY=-1.8 StartZ=0 EndX=-23.6 EndY=-36.4 EndZ=0
  constraints (48):
    c: Block(g0)
    c: Block(g1)
    c: Block(g2)
    c: Block(g3)
    c: Block(g4)
    c: Block(g5)
    c: Block(g6)
    c: Block(g7)
    c: Block(g8)
    c: Block(g9)
    c: Block(g10)
    c: Block(g11)
    c: Coincident(g12,g1)
    c: Coincident(g12,g2)
    c: Vertical(g12)
    c: Coincident(g13,g1)
    c: Coincident(g13,g2)
    c: Vertical(g13)
    c: Coincident(g14,g11)
    c: Coincident(g14,g7)
    c: Vertical(g14)
    c: Coincident(g15,g11)
    c: Coincident(g15,g7)
    c: Vertical(g15)
    c: Coincident(g16,g0)
    c: Coincident(g16,g3)
    c: Vertical(g16)
    c: Coincident(g17,g4)
    c: Coincident(g17,g8)
    c: Vertical(g17)
    c: Coincident(g18,g0)
    c: Coincident(g18,g3)
    c: Vertical(g18)
    c: Coincident(g19,g4)
    c: Coincident(g19,g8)
    c: Vertical(g19)
    c: Coincident(g20,g5)
    c: Coincident(g20,g9)
    c: Vertical(g20)
    c: Coincident(g21,g5)
    c: Coincident(g21,g9)
    c: Vertical(g21)
    c: Coincident(g22,g10)
    c: Coincident(g22,g6)
    c: Vertical(g22)
    c: Coincident(g23,g6)
    c: Coincident(g23,g10)
    c: Vertical(g23)
FEATURE [Part::Extrusion] Extrude038  label="removeToCreateFanGrillHoles001"
  Base = -> Sketch047
  Dir = (0,-1,6e-16)
  DirMode = 2
  FaceMakerClass = Part::FaceMakerBullseye
  LengthFwd = 10
  LengthRev = 0
  Placement = pos=(65.4,44,54.82) rot=(0,0,1;0rad)
  Solid = true
  Symmetric = false
FEATURE [Part::Feature] Wire004
  shape: bbox 11 x 5.2 x 2e-07 mm, 0 faces, 0 solids (baked)
FEATURE [Part::Revolution] Revolve095
  Angle = 360
  Axis = (0,1,0)
  Base = (0,0,0)
  FaceMakerClass = Part::FaceMakerBullseye
  Placement = pos=(30.3,38,19.7) rot=(0,0,1;0rad)
  Solid = true
  Source = -> Wire004
  Symmetric = false
FEATURE [Part::Feature] Wire005
  shape: bbox 11 x 5.2 x 2e-07 mm, 0 faces, 0 solids (baked)
FEATURE [Part::Revolution] Revolve096
  Angle = 360
  Axis = (0,1,0)
  Base = (0,0,0)
  FaceMakerClass = Part::FaceMakerBullseye
  Placement = pos=(30.3,38,51.7) rot=(0,0,1;0rad)
  Solid = true
  Source = -> Wire005
  Symmetric = false
FEATURE [Part::Feature] Wire006
  shape: bbox 11 x 5.2 x 2e-07 mm, 0 faces, 0 solids (baked)
FEATURE [Part::Revolution] Revolve097
  Angle = 360
  Axis = (0,1,0)
  Base = (0,0,0)
  FaceMakerClass = Part::FaceMakerBullseye
  Placement = pos=(62.3,38,51.7) rot=(0,0,1;0rad)
  Solid = true
  Source = -> Wire006
  Symmetric = false
FEATURE [Part::Feature] Wire007
  shape: bbox 11 x 5.2 x 2e-07 mm, 0 faces, 0 solids (baked)
FEATURE [Part::Revolution] Revolve098
  Angle = 360
  Axis = (0,1,0)
  Base = (0,0,0)
  FaceMakerClass = Part::FaceMakerBullseye
  Placement = pos=(62.3,38,19.7) rot=(0,0,1;0rad)
  Solid = true
  Source = -> Wire007
  Symmetric = false
FEATURE [Part::MultiFuse] Fusion067  label="fanScrewHousing002"
  Shapes = -> [Revolve098,Revolve097,Revolve096,Revolve095]
FEATURE [Part::Feature] Face091 .. Face094  x4 (patterned run collapsed; names and placements below)
  shape: bbox 3.5 x 17.8 x 2e-07 mm, 1 faces, 0 solids (baked)
FEATURE [Part::Revolution] Revolve099  label="removeToCreateScrewAndThreadedInsertHole026"
  Angle = 360
  Axis = (0,1,0)
  Base = (0,0,0)
  FaceMakerClass = Part::FaceMakerBullseye
  Placement = pos=(62.3,30.3,19.7) rot=(0,0,1;0rad)
  Solid = false
  Source = -> Face091
  Symmetric = false
FEATURE [Part::Revolution] Revolve100  label="removeToCreateScrewAndThreadedInsertHole027"
  Angle = 360
  Axis = (0,1,0)
  Base = (0,0,0)
  FaceMakerClass = Part::FaceMakerBullseye
  Placement = pos=(62.3,30.3,51.7) rot=(0,0,1;0rad)
  Solid = false
  Source = -> Face092
  Symmetric = false
FEATURE [Part::Revolution] Revolve101  label="removeToCreateScrewAndThreadedInsertHole028"
  Angle = 360
  Axis = (0,1,0)
  Base = (0,0,0)
  FaceMakerClass = Part::FaceMakerBullseye
  Placement = pos=(30.3,30.3,19.7) rot=(0,0,1;0rad)
  Solid = false
  Source = -> Face093
  Symmetric = false
FEATURE [Part::Revolution] Revolve102  label="removeToCreateScrewAndThreadedInsertHole029"
  Angle = 360
  Axis = (0,1,0)
  Base = (0,0,0)
  FaceMakerClass = Part::FaceMakerBullseye
  Placement = pos=(30.3,30.3,51.7) rot=(0,0,1;0rad)
  Solid = false
  Source = -> Face094
  Symmetric = false
FEATURE [Part::MultiFuse] Fusion068  label="createThreadedInsertHolesForFan002"
  Shapes = -> [Revolve099,Revolve100,Revolve101,Revolve102]
FEATURE [Part::Cut] Cut026  label="fanScrewHousing003"
  Base = -> Fusion067
  Tool = -> Fusion068
FEATURE [Sketcher::SketchObject] Sketch048
  FullyConstrained = false
  Placement = pos=(0,0,0) rot=(1,0,0;1.5708rad)
  sketch-geometry (24):
    g0: ArcOfCircle CenterX=-4 CenterY=-10.5 CenterZ=0 NormalX=0 NormalY=0 NormalZ=1 AngleXU=0 Radius=1.5 StartAngle=6e-16 EndAngle=3.14159
    g1: ArcOfCircle CenterX=-34.2 CenterY=-10.5 CenterZ=0 NormalX=0 NormalY=0 NormalZ=1 AngleXU=0 Radius=1.5 StartAngle=0 EndAngle=3.14159
    g2: ArcOfCircle CenterX=-34.2 CenterY=-27.7 CenterZ=0 NormalX=0 NormalY=0 NormalZ=1 AngleXU=0 Radius=1.5 StartAngle=3.14159 EndAngle=6.28319
    g3: ArcOfCircle CenterX=-4 CenterY=-27.7 CenterZ=0 NormalX=0 NormalY=0 NormalZ=1 AngleXU=0 Radius=1.5 StartAngle=3.1416 EndAngle=6.28319
    g4: ArcOfCircle CenterX=-10 CenterY=-4.3 CenterZ=0 NormalX=0 NormalY=0 NormalZ=1 AngleXU=0 Radius=1.5 StartAngle=2e-16 EndAngle=3.14159
    g5: ArcOfCircle CenterX=-16.1 CenterY=-1.8 CenterZ=0 NormalX=0 NormalY=0 NormalZ=1 AngleXU=0 Radius=1.5 StartAngle=5e-16 EndAngle=3.14159
    g6: ArcOfCircle CenterX=-22.1 CenterY=-1.8 CenterZ=0 NormalX=0 NormalY=0 NormalZ=1 AngleXU=0 Radius=1.5 StartAngle=5e-16 EndAngle=3.14159
    g7: ArcOfCircle CenterX=-28.2 CenterY=-4.3 CenterZ=0 NormalX=0 NormalY=0 NormalZ=1 AngleXU=0 Radius=1.5 StartAngle=2e-16 EndAngle=3.14159
    g8: ArcOfCircle CenterX=-10 CenterY=-33.9 CenterZ=0 NormalX=0 NormalY=0 NormalZ=1 AngleXU=0 Radius=1.5 StartAngle=3.14159 EndAngle=6.28319
    g9: ArcOfCircle CenterX=-16.1 CenterY=-36.4 CenterZ=0 NormalX=0 NormalY=0 NormalZ=1 AngleXU=0 Radius=1.5 StartAngle=3.14159 EndAngle=6.28319
    g10: ArcOfCircle CenterX=-22.1 CenterY=-36.4 CenterZ=0 NormalX=0 NormalY=0 NormalZ=1 AngleXU=0 Radius=1.5 StartAngle=3.14159 EndAngle=6.28319
    g11: ArcOfCircle CenterX=-28.2 CenterY=-33.9 CenterZ=0 NormalX=0 NormalY=0 NormalZ=1 AngleXU=0 Radius=1.5 StartAngle=3.14159 EndAngle=6.28319
    g12: LineSegment StartX=-35.7 StartY=-10.5 StartZ=0 EndX=-35.7 EndY=-27.7 EndZ=0
    g13: LineSegment StartX=-32.7 StartY=-10.5 StartZ=0 EndX=-32.7 EndY=-27.7 EndZ=0
    g14: LineSegment StartX=-29.7 StartY=-33.9 StartZ=0 EndX=-29.7 EndY=-4.3 EndZ=0
    g15: LineSegment StartX=-26.7 StartY=-33.9 StartZ=0 EndX=-26.7 EndY=-4.3 EndZ=0
    g16: LineSegment StartX=-2.5 StartY=-10.5 StartZ=0 EndX=-2.5 EndY=-27.7 EndZ=0
    g17: LineSegment StartX=-8.5 StartY=-4.3 StartZ=0 EndX=-8.5 EndY=-33.9 EndZ=0
    g18: LineSegment StartX=-5.5 StartY=-10.5 StartZ=0 EndX=-5.5 EndY=-27.7 EndZ=0
    g19: LineSegment StartX=-11.5 StartY=-4.3 StartZ=0 EndX=-11.5 EndY=-33.9 EndZ=0
    g20: LineSegment StartX=-14.6 StartY=-1.8 StartZ=0 EndX=-14.6 EndY=-36.4 EndZ=0
    g21: LineSegment StartX=-17.6 StartY=-1.8 StartZ=0 EndX=-17.6 EndY=-36.4 EndZ=0
    g22: LineSegment StartX=-20.6 StartY=-36.4 StartZ=0 EndX=-20.6 EndY=-1.8 EndZ=0
    g23: LineSegment StartX=-23.6 StartY=-1.8 StartZ=0 EndX=-23.6 EndY=-36.4 EndZ=0
  constraints (48):
    c: Block(g0)
    c: Block(g1)
    c: Block(g2)
    c: Block(g3)
    c: Block(g4)
    c: Block(g5)
    c: Block(g6)
    c: Block(g7)
    c: Block(g8)
    c: Block(g9)
    c: Block(g10)
    c: Block(g11)
    c: Coincident(g12,g1)
    c: Coincident(g12,g2)
    c: Vertical(g12)
    c: Coincident(g13,g1)
    c: Coincident(g13,g2)
    c: Vertical(g13)
    c: Coincident(g14,g11)
    c: Coincident(g14,g7)
    c: Vertical(g14)
    c: Coincident(g15,g11)
    c: Coincident(g15,g7)
    c: Vertical(g15)
    c: Coincident(g16,g0)
    c: Coincident(g16,g3)
    c: Vertical(g16)
    c: Coincident(g17,g4)
    c: Coincident(g17,g8)
    c: Vertical(g17)
    c: Coincident(g18,g0)
    c: Coincident(g18,g3)
    c: Vertical(g18)
    c: Coincident(g19,g4)
    c: Coincident(g19,g8)
    c: Vertical(g19)
    c: Coincident(g20,g5)
    c: Coincident(g20,g9)
    c: Vertical(g20)
    c: Coincident(g21,g5)
    c: Coincident(g21,g9)
    c: Vertical(g21)
    c: Coincident(g22,g10)
    c: Coincident(g22,g6)
    c: Vertical(g22)
    c: Coincident(g23,g6)
    c: Coincident(g23,g10)
    c: Vertical(g23)
FEATURE [Part::Extrusion] Extrude039  label="removeToCreateFanGrillHoles002"
  Base = -> Sketch048
  Dir = (0,-1,6e-16)
  DirMode = 2
  FaceMakerClass = Part::FaceMakerBullseye
  LengthFwd = 10
  LengthRev = 0
  Placement = pos=(65.4,44,54.82) rot=(0,0,1;0rad)
  Solid = true
  Symmetric = false
FEATURE [Part::Cut] Cut027  label="fanScrewHousing004"
  Base = -> Cut026
  Tool = -> Extrude038
FEATURE [Part::Cut] Cut028  label="top014"
  Base = -> Fillet026
  Tool = -> Extrude039
FEATURE [Part::Feature] Face095 .. Face098  x4 (patterned run collapsed; names and placements below)
  shape: bbox 3.5 x 17.8 x 2e-07 mm, 1 faces, 0 solids (baked)
FEATURE [Part::Revolution] Revolve103  label="removeToCreateScrewAndThreadedInsertHole030"
  Angle = 360
  Axis = (0,1,0)
  Base = (0,0,0)
  FaceMakerClass = Part::FaceMakerBullseye
  Placement = pos=(62.3,30.3,19.7) rot=(0,0,1;0rad)
  Solid = false
  Source = -> Face095
  Symmetric = false
FEATURE [Part::Revolution] Revolve104  label="removeToCreateScrewAndThreadedInsertHole031"
  Angle = 360
  Axis = (0,1,0)
  Base = (0,0,0)
  FaceMakerClass = Part::FaceMakerBullseye
  Placement = pos=(62.3,30.3,51.7) rot=(0,0,1;0rad)
  Solid = false
  Source = -> Face096
  Symmetric = false
FEATURE [Part::Revolution] Revolve105  label="removeToCreateScrewAndThreadedInsertHole032"
  Angle = 360
  Axis = (0,1,0)
  Base = (0,0,0)
  FaceMakerClass = Part::FaceMakerBullseye
  Placement = pos=(30.3,30.3,19.7) rot=(0,0,1;0rad)
  Solid = false
  Source = -> Face097
  Symmetric = false
FEATURE [Part::Revolution] Revolve106  label="removeToCreateScrewAndThreadedInsertHole033"
  Angle = 360
  Axis = (0,1,0)
  Base = (0,0,0)
  FaceMakerClass = Part::FaceMakerBullseye
  Placement = pos=(30.3,30.3,51.7) rot=(0,0,1;0rad)
  Solid = false
  Source = -> Face098
  Symmetric = false
FEATURE [Part::MultiFuse] Fusion069  label="createThreadedInsertHolesForFan003"
  Shapes = -> [Revolve103,Revolve104,Revolve105,Revolve106]
FEATURE [Part::Cut] Cut029  label="top015"
  Base = -> Cut028
  Tool = -> Fusion054
FEATURE [Part::Cut] Cut030  label="fanScrewHousing005"
  Base = -> Cut027
  Tool = -> Fusion069
FEATURE [Part::Cylinder] Cylinder026  label="removeToCreteHoleForPlugHousing010"
  Angle = 360
  AttacherType = Attacher::AttachEngine3D
  Height = 20
  Placement = pos=(-2,19,36) rot=(0,1,0;1.5708rad)
  Radius = 14.3
FEATURE [Part::Box] Box018  label="removeToCreteHoleForPlugHousing011"
  AttacherType = Attacher::AttachEngine3D
  Height = 28.6
  Length = 10
  Placement = pos=(-2,0,21.7) rot=(0,0,1;0rad)
  Width = 19
FEATURE [Part::Box] Box019  label="wireHolderBottomCaseBit"
  AttacherType = Attacher::AttachEngine3D
  Height = 28
  Length = 3
  Placement = pos=(0,0,22) rot=(0,0,1;0rad)
  Width = 21
FEATURE [Part::Cylinder] Cylinder027  label="removeToCreteHoleForPlugHousing012"
  Angle = 360
  AttacherType = Attacher::AttachEngine3D
  Height = 20
  Placement = pos=(-2,19,36) rot=(0,1,0;1.5708rad)
  Radius = 14.3
FEATURE [Part::Cut] Cut031  label="wireHolderBottomCaseBit001"
  Base = -> Box019
  Tool = -> Cylinder027
FEATURE [Part::MultiFuse] Fusion070  label="removeToCreteHoleForPlugHousing013"
  Shapes = -> [Box018,Cylinder026]
FEATURE [Part::Cut] Cut032  label="top016"
  Base = -> Cut029
  Tool = -> Fusion070
FEATURE [Part::Cylinder] Cylinder028
  Angle = 360
  AttacherType = Attacher::AttachEngine3D
  Height = 20
  Placement = pos=(0,0,36.15) rot=(0,0,1;0rad)
  Radius = 14.3
FEATURE [Part::Cylinder] Cylinder029
  Angle = 360
  AttacherType = Attacher::AttachEngine3D
  Height = 10
  Placement = pos=(0,0,36.15) rot=(0,0,1;0rad)
  Radius = 4
FEATURE [Part::MultiFuse] Fusion071  label="removeToCreteHoleForPlugHousing014"
  Placement = pos=(70,19,36) rot=(0,1,0;1.5708rad)
  Shapes = -> [Cylinder028,Cylinder029]
FEATURE [Sketcher::SketchObject] Sketch049  label="topSketch011"
  FullyConstrained = true
  sketch-geometry (4):
    g0: ArcOfCircle CenterX=105 CenterY=19 CenterZ=0 NormalX=0 NormalY=0 NormalZ=1 AngleXU=0 Radius=20.6155 StartAngle=5.54125 EndAngle=6.28319
    g1: ArcOfCircle CenterX=105 CenterY=19 CenterZ=0 NormalX=0 NormalY=0 NormalZ=1 AngleXU=0 Radius=13 StartAngle=5.54125 EndAngle=6.28319
    g2: LineSegment StartX=118 StartY=19 StartZ=0 EndX=125.616 EndY=19 EndZ=0
    g3: LineSegment StartX=114.583 StartY=10.2157 StartZ=0 EndX=120.197 EndY=5.06982 EndZ=0
  constraints (7):
    c: Block(g0)
    c: Block(g1)
    c: Coincident(g2,g1)
    c: Coincident(g2,g0)
    c: Horizontal(g2)
    c: Coincident(g3,g1)
    c: Coincident(g3,g0)
FEATURE [Part::Box] Box020  label="removeToCreteHoleForPlugHousing015"
  AttacherType = Attacher::AttachEngine3D
  Height = 28.6
  Length = 20
  Placement = pos=(106.15,0,21.7) rot=(0,0,1;0rad)
  Width = 19
FEATURE [Part::MultiFuse] Fusion072  label="removeToCreteHoleForPlugHousing016"
  Shapes = -> [Box020,Fusion071]
FEATURE [Part::Cut] Cut033  label="removeToCreteHoleForPlugHousing017"
  Base = -> Cut032
  Tool = -> Fusion072
FEATURE [Part::Cylinder] Cylinder030
  Angle = 360
  AttacherType = Attacher::AttachEngine3D
  Height = 20
  Placement = pos=(0,0,36.15) rot=(0,0,1;0rad)
  Radius = 14.3
FEATURE [Part::Cylinder] Cylinder031
  Angle = 360
  AttacherType = Attacher::AttachEngine3D
  Height = 10
  Placement = pos=(0,0,36.15) rot=(0,0,1;0rad)
  Radius = 4
FEATURE [Part::Box] Box021  label="removeToCreteHoleForPlugHousing019"
  AttacherType = Attacher::AttachEngine3D
  Height = 28.6
  Length = 20
  Placement = pos=(106.15,0,21.7) rot=(0,0,1;0rad)
  Width = 19
FEATURE [Part::MultiFuse] Fusion074  label="removeToCreteHoleForPlugHousing020"
  Placement = pos=(70,19,36) rot=(0,1,0;1.5708rad)
  Shapes = -> [Cylinder030,Cylinder031]
FEATURE [Part::MultiFuse] Fusion073  label="removeToCreteHoleForPlugHousing018"
  Placement = pos=(0,0,28.3) rot=(0,0,1;0rad)
  Shapes = -> [Box021,Fusion074]
FEATURE [Part::Cylinder] Cylinder032
  Angle = 360
  AttacherType = Attacher::AttachEngine3D
  Height = 20
  Placement = pos=(0,0,36.15) rot=(0,0,1;0rad)
  Radius = 14.3
FEATURE [Part::Cylinder] Cylinder033
  Angle = 360
  AttacherType = Attacher::AttachEngine3D
  Height = 10
  Placement = pos=(0,0,36.15) rot=(0,0,1;0rad)
  Radius = 4
FEATURE [Part::Box] Box022  label="removeToCreteHoleForPlugHousing021"
  AttacherType = Attacher::AttachEngine3D
  Height = 28.6
  Length = 20
  Placement = pos=(106.15,0,21.7) rot=(0,0,1;0rad)
  Width = 19
FEATURE [Part::MultiFuse] Fusion076  label="removeToCreteHoleForPlugHousing023"
  Placement = pos=(70,19,36) rot=(0,1,0;1.5708rad)
  Shapes = -> [Cylinder032,Cylinder033]
FEATURE [Part::MultiFuse] Fusion075  label="removeToCreteHoleForPlugHousing022"
  Placement = pos=(0,0,-28.3) rot=(0,0,1;0rad)
  Shapes = -> [Box022,Fusion076]
FEATURE [Part::MultiFuse] Fusion077  label="removeToCreatePlugHousingBottomBit"
  Shapes = -> [Fusion075,Fusion073]
FEATURE [Part::Cylinder] Cylinder034
  Angle = 360
  AttacherType = Attacher::AttachEngine3D
  Height = 20
  Placement = pos=(0,0,36.15) rot=(0,0,1;0rad)
  Radius = 14
FEATURE [Part::Cylinder] Cylinder035
  Angle = 360
  AttacherType = Attacher::AttachEngine3D
  Height = 10
  Placement = pos=(0,0,36.15) rot=(0,0,1;0rad)
  Radius = 4
FEATURE [Part::MultiFuse] Fusion078  label="removeToCreteHoleForPlugHousing024"
  Placement = pos=(70,19,36) rot=(0,1,0;1.5708rad)
  Shapes = -> [Cylinder034,Cylinder035]
FEATURE [Part::MultiFuse] Fusion079  label="removeToCreatePlugHousingBottomBit001"
  Shapes = -> [Fusion078,Fusion077]
FEATURE [Part::Extrusion] Extrude040  label="bottomPlugHousingBit"
  Base = -> Sketch049
  Dir = (0,0,1)
  DirMode = 2
  FaceMakerClass = Part::FaceMakerBullseye
  LengthFwd = 72
  LengthRev = 0
  Solid = true
  Symmetric = false
FEATURE [Part::Cut] Cut034  label="bottomPlugHousingBit001"
  Base = -> Extrude040
  Placement = pos=(-0.09,0,0) rot=(0,0,1;0rad)
  Tool = -> Fusion079
FEATURE [Part::Box] Box023  label="Cube014"
  AttacherType = Attacher::AttachEngine3D
  Height = 16
  Length = 8
  Placement = pos=(12.7,31.52,28) rot=(0,0,1;0rad)
  Width = 4
FEATURE [Part::Cylinder] Cylinder036
  Angle = 360
  AttacherType = Attacher::AttachEngine3D
  Height = 10
  Placement = pos=(0,0,36.15) rot=(0,0,1;0rad)
  Radius = 4
FEATURE [Part::Cylinder] Cylinder037
  Angle = 360
  AttacherType = Attacher::AttachEngine3D
  Height = 20
  Placement = pos=(0,0,36.15) rot=(0,0,1;0rad)
  Radius = 8.2
FEATURE [Part::MultiFuse] Fusion080  label="removeToCreteHoleForPlugHousing025"
  Placement = pos=(-42,19,36) rot=(0,1,0;1.5708rad)
  Shapes = -> [Cylinder037,Cylinder036]
FEATURE [Sketcher::SketchObject] Sketch050  label="topSketch012"
  FullyConstrained = true
  sketch-geometry (4):
    g0: LineSegment StartX=16.8446 StartY=31.512 StartZ=0 EndX=16.3251 EndY=34.4666 EndZ=0
    g1: ArcOfCircle CenterX=19 CenterY=19.2524 CenterZ=0 NormalX=0 NormalY=0 NormalZ=1 AngleXU=0 Radius=15.4476 StartAngle=1.74483 EndAngle=2.72717
    g2: ArcOfCircle CenterX=19 CenterY=19.2524 CenterZ=0 NormalX=0 NormalY=0 NormalZ=1 AngleXU=0 Radius=12.4476 StartAngle=1.74483 EndAngle=2.73189
    g3: LineSegment StartX=4.86004 StartY=25.4725 StartZ=0 EndX=7.58253 EndY=24.2107 EndZ=0
  constraints (7):
    c: Block(g0)
    c: Coincident(g1,g0)
    c: Coincident(g2,g0)
    c: Coincident(g3,g1)
    c: Coincident(g3,g2)
    c: Block(g1)
    c: Block(g2)
FEATURE [Part::Extrusion] Extrude041
  Base = -> Sketch050
  Dir = (0,0,1)
  DirMode = 2
  FaceMakerClass = Part::FaceMakerBullseye
  LengthFwd = 10.6
  LengthRev = 0
  Placement = pos=(0,0,31) rot=(0,0,1;0rad)
  Solid = true
  Symmetric = false
FEATURE [Part::Cut] Cut035
  Base = -> Extrude041
  Placement = pos=(0,0,-0.3) rot=(0,0,1;0rad)
  Tool = -> Fusion080
FEATURE [Part::Cut] Cut036
  Base = -> Box023
  Tool = -> Cut035
FEATURE [Part::Fillet] Fillet027
  Base = -> Cut036
  Edges = 1 edges r=0.7: [Edge13]
FEATURE [Part::Fillet] Fillet028
  Base = -> Fillet027
  Edges = 1 edges r=0.7: [Edge13]
FEATURE [Part::Fillet] Fillet029
  Base = -> Fillet028
  Edges = 1 edges r=0.7: [Edge16]
FEATURE [Part::Fillet] Fillet030
  Base = -> Fillet029
  Edges = 1 edges r=0.7: [Edge11]
FEATURE [Part::Fillet] Fillet031
  Base = -> Fillet030
  Edges = 1 edges r=0.7: [Edge10]
FEATURE [Part::Fillet] Fillet032
  Base = -> Fillet031
  Edges = 1 edges r=1.2: [Edge5]
FEATURE [Part::Fillet] Fillet033
  Base = -> Fillet032
  Edges = 1 edges r=1.2: [Edge12]
FEATURE [Part::Fillet] Fillet034  label="wireHousingRetainer"
  Base = -> Fillet033
  Edges = 1 edges r=2: [Edge1]
  Placement = pos=(0.3,0,0) rot=(0,0,1;0rad)
FEATURE [Part::Feature] Face099
  shape: bbox 3.5 x 17.8 x 2e-07 mm, 1 faces, 0 solids (baked)
FEATURE [Part::Revolution] Revolve107  label="removeToCreateScrewAndThreadedInsertHole034"
  Angle = 360
  Axis = (0,1,0)
  Base = (0,0,0)
  FaceMakerClass = Part::FaceMakerBullseye
  Placement = pos=(12.5,0,10) rot=(0,0,1;0rad)
  Solid = false
  Source = -> Face099
  Symmetric = false
FEATURE [Part::Feature] Face100
  shape: bbox 3.5 x 17.8 x 2e-07 mm, 1 faces, 0 solids (baked)
FEATURE [Part::Revolution] Revolve108  label="removeToCreateScrewAndThreadedInsertHole035"
  Angle = 360
  Axis = (0,1,0)
  Base = (0,0,0)
  FaceMakerClass = Part::FaceMakerBullseye
  Placement = pos=(12.5,0,62) rot=(0,0,1;0rad)
  Solid = false
  Source = -> Face100
  Symmetric = false
FEATURE [Part::Feature] Face101
  shape: bbox 3.5 x 17.8 x 2e-07 mm, 1 faces, 0 solids (baked)
FEATURE [Part::Revolution] Revolve109  label="removeToCreateScrewAndThreadedInsertHole036"
  Angle = 360
  Axis = (0,1,0)
  Base = (0,0,0)
  FaceMakerClass = Part::FaceMakerBullseye
  Placement = pos=(89.5,0,68.5) rot=(0,0,1;0rad)
  Solid = false
  Source = -> Face101
  Symmetric = false
FEATURE [Part::Feature] Face102
  shape: bbox 3.5 x 17.8 x 2e-07 mm, 1 faces, 0 solids (baked)
FEATURE [Part::Revolution] Revolve110  label="removeToCreateScrewAndThreadedInsertHole037"
  Angle = 360
  Axis = (0,1,0)
  Base = (0,0,0)
  FaceMakerClass = Part::FaceMakerBullseye
  Placement = pos=(89.5,0,3.5) rot=(0,0,1;0rad)
  Solid = false
  Source = -> Face102
  Symmetric = false
FEATURE [Part::Feature] Face103
  shape: bbox 3.5 x 17.8 x 2e-07 mm, 1 faces, 0 solids (baked)
FEATURE [Part::Revolution] Revolve111  label="removeToCreateScrewAndThreadedInsertHole038"
  Angle = 360
  Axis = (0,1,0)
  Base = (0,0,0)
  FaceMakerClass = Part::FaceMakerBullseye
  Placement = pos=(109.5,4.7,3.5) rot=(0,0,1;0rad)
  Solid = false
  Source = -> Face103
  Symmetric = false
FEATURE [Part::Feature] Face104
  shape: bbox 3.5 x 17.8 x 2e-07 mm, 1 faces, 0 solids (baked)
FEATURE [Part::Revolution] Revolve112  label="removeToCreateScrewAndThreadedInsertHole039"
  Angle = 360
  Axis = (0,1,0)
  Base = (0,0,0)
  FaceMakerClass = Part::FaceMakerBullseye
  Placement = pos=(109.5,4.7,68.5) rot=(0,0,1;0rad)
  Solid = false
  Source = -> Face104
  Symmetric = false
FEATURE [Part::MultiFuse] Fusion081  label="removeToCreateScrewAndThreadedInsertHole040"
  Shapes = -> [Revolve107,Revolve108,Revolve109,Revolve110,Revolve111,Revolve112]
FEATURE [Part::MultiFuse] Fusion082  label="casePillars002"
  Shapes = -> [Revolve094,Revolve092,Revolve090,Revolve089,Revolve091,Revolve093]
FEATURE [Part::Cut] Cut037  label="casePillars003"
  Base = -> Fusion082
  Tool = -> Fusion081
FEATURE [Sketcher::SketchObject] Sketch051
  FullyConstrained = true
  Placement = pos=(117,19,0) rot=(0.57735,0.57735,0.57735;2.0944rad)
  sketch-geometry (48):
    g0: LineSegment StartX=-49.19 StartY=69.25 StartZ=0 EndX=-49.19 EndY=66.25 EndZ=0
    g1: LineSegment StartX=-49.19 StartY=63.5 StartZ=0 EndX=-49.19 EndY=60.5 EndZ=0
    g2: LineSegment StartX=-49.19 StartY=57.75 StartZ=0 EndX=-49.19 EndY=54.75 EndZ=0
    g3: LineSegment StartX=-49.19 StartY=52 StartZ=0 EndX=-49.19 EndY=49 EndZ=0
    g4: LineSegment StartX=-49.19 StartY=46.25 StartZ=0 EndX=-49.19 EndY=43.25 EndZ=0
    g5: LineSegment StartX=-49.19 StartY=40.5 StartZ=0 EndX=-49.19 EndY=37.5 EndZ=0
    g6: LineSegment StartX=-49.19 StartY=34.5 StartZ=0 EndX=-49.19 EndY=31.5 EndZ=0
    g7: LineSegment StartX=-49.19 StartY=28.75 StartZ=0 EndX=-49.19 EndY=25.75 EndZ=0
    g8: LineSegment StartX=-49.19 StartY=23 StartZ=0 EndX=-49.19 EndY=20 EndZ=0
    g9: LineSegment StartX=-49.19 StartY=17.25 StartZ=0 EndX=-49.19 EndY=14.25 EndZ=0
    g10: LineSegment StartX=-49.19 StartY=11.5 StartZ=0 EndX=-49.19 EndY=8.5 EndZ=0
    g11: LineSegment StartX=-49.19 StartY=5.75 StartZ=0 EndX=-49.19 EndY=2.75 EndZ=0
    g12: ArcOfCircle CenterX=-1.5 CenterY=67.75 CenterZ=0 NormalX=0 NormalY=0 NormalZ=1 AngleXU=0 Radius=1.5 StartAngle=4.71239 EndAngle=7.85398
    g13: ArcOfCircle CenterX=-1.5 CenterY=62 CenterZ=0 NormalX=0 NormalY=0 NormalZ=1 AngleXU=0 Radius=1.5 StartAngle=4.71239 EndAngle=7.85398
    g14: ArcOfCircle CenterX=-1.5 CenterY=56.25 CenterZ=0 NormalX=0 NormalY=0 NormalZ=1 AngleXU=0 Radius=1.5 StartAngle=4.71239 EndAngle=7.85398
    g15: ArcOfCircle CenterX=-11.49 CenterY=50.5 CenterZ=0 NormalX=0 NormalY=0 NormalZ=1 AngleXU=0 Radius=1.5 StartAngle=4.71239 EndAngle=7.85398
    g16: ArcOfCircle CenterX=-16.28 CenterY=44.75 CenterZ=0 NormalX=0 NormalY=0 NormalZ=1 AngleXU=0 Radius=1.5 StartAngle=4.71239 EndAngle=7.85398
    g17: ArcOfCircle CenterX=-18.2337 CenterY=39 CenterZ=0 NormalX=0 NormalY=0 NormalZ=1 AngleXU=0 Radius=1.5 StartAngle=4.71485 EndAngle=7.85398
    g18: ArcOfCircle CenterX=-16.2837 CenterY=27.25 CenterZ=0 NormalX=0 NormalY=0 NormalZ=1 AngleXU=0 Radius=1.5 StartAngle=4.71485 EndAngle=7.85398
    g19: ArcOfCircle CenterX=-18.2337 CenterY=33 CenterZ=0 NormalX=0 NormalY=0 NormalZ=1 AngleXU=0 Radius=1.5 StartAngle=4.71485 EndAngle=7.85398
    g20: ArcOfCircle CenterX=-11.49 CenterY=21.5 CenterZ=0 NormalX=0 NormalY=0 NormalZ=1 AngleXU=0 Radius=1.5 StartAngle=4.71239 EndAngle=7.85398
    g21: ArcOfCircle CenterX=-1.5 CenterY=4.25 CenterZ=0 NormalX=0 NormalY=0 NormalZ=1 AngleXU=0 Radius=1.5 StartAngle=4.71239 EndAngle=7.85398
    g22: ArcOfCircle CenterX=-1.5 CenterY=10 CenterZ=0 NormalX=0 NormalY=0 NormalZ=1 AngleXU=0 Radius=1.5 StartAngle=4.71239 EndAngle=7.85398
    g23: ArcOfCircle CenterX=-1.5 CenterY=15.75 CenterZ=0 NormalX=0 NormalY=0 NormalZ=1 AngleXU=0 Radius=1.5 StartAngle=4.71239 EndAngle=7.85398
    g24: LineSegment StartX=-49.19 StartY=69.25 StartZ=0 EndX=-1.5 EndY=69.25 EndZ=0
    g25: LineSegment StartX=-49.19 StartY=66.25 StartZ=0 EndX=-1.5 EndY=66.25 EndZ=0
    g26: LineSegment StartX=-49.19 StartY=63.5 StartZ=0 EndX=-1.5 EndY=63.5 EndZ=0
    g27: LineSegment StartX=-49.19 StartY=60.5 StartZ=0 EndX=-1.5 EndY=60.5 EndZ=0
    g28: LineSegment StartX=-49.19 StartY=57.75 StartZ=0 EndX=-1.5 EndY=57.75 EndZ=0
    g29: LineSegment StartX=-49.19 StartY=54.75 StartZ=0 EndX=-1.5 EndY=54.75 EndZ=0
    g30: LineSegment StartX=-49.19 StartY=52 StartZ=0 EndX=-11.49 EndY=52 EndZ=0
    g31: LineSegment StartX=-49.19 StartY=49 StartZ=0 EndX=-11.49 EndY=49 EndZ=0
    g32: LineSegment StartX=-49.19 StartY=46.25 StartZ=0 EndX=-16.28 EndY=46.25 EndZ=0
    g33: LineSegment StartX=-49.19 StartY=43.25 StartZ=0 EndX=-16.28 EndY=43.25 EndZ=0
    g34: LineSegment StartX=-49.19 StartY=40.5 StartZ=0 EndX=-18.2337 EndY=40.5 EndZ=0
    g35: LineSegment StartX=-49.19 StartY=37.5 StartZ=0 EndX=-18.23 EndY=37.5 EndZ=0
    g36: LineSegment StartX=-49.19 StartY=34.5 StartZ=0 EndX=-18.2337 EndY=34.5 EndZ=0
    g37: LineSegment StartX=-49.19 StartY=31.5 StartZ=0 EndX=-18.23 EndY=31.5 EndZ=0
    g38: LineSegment StartX=-49.19 StartY=28.75 StartZ=0 EndX=-16.2837 EndY=28.75 EndZ=0
    g39: LineSegment StartX=-49.19 StartY=25.75 StartZ=0 EndX=-16.28 EndY=25.75 EndZ=0
    g40: LineSegment StartX=-49.19 StartY=23 StartZ=0 EndX=-11.49 EndY=23 EndZ=0
    g41: LineSegment StartX=-49.19 StartY=20 StartZ=0 EndX=-11.49 EndY=20 EndZ=0
    g42: LineSegment StartX=-49.19 StartY=17.25 StartZ=0 EndX=-1.5 EndY=17.25 EndZ=0
    g43: LineSegment StartX=-49.19 StartY=14.25 StartZ=0 EndX=-1.5 EndY=14.25 EndZ=0
    g44: LineSegment StartX=-49.19 StartY=11.5 StartZ=0 EndX=-1.5 EndY=11.5 EndZ=0
    g45: LineSegment StartX=-49.19 StartY=8.5 StartZ=0 EndX=-1.5 EndY=8.5 EndZ=0
    g46: LineSegment StartX=-49.19 StartY=5.75 StartZ=0 EndX=-1.5 EndY=5.75 EndZ=0
    g47: LineSegment StartX=-49.19 StartY=2.75 StartZ=0 EndX=-1.5 EndY=2.75 EndZ=0
  constraints (120):
    c: Vertical(g0)
    c: Distance(g0) = 3
    c: Block(g0)
    c: Vertical(g1)
    c: Distance(g1) = 3
    c: Vertical(g2)
    c: Equal(g0,g2) = 3
    c: Block(g2)
    c: Vertical(g3)
    c: Equal(g1,g3) = 3
    c: Vertical(g4)
    c: Equal(g0,g4) = 3
    c: Block(g4)
    c: Vertical(g5)
    c: Equal(g1,g5) = 3
    c: Vertical(g6)
    c: Equal(g0,g6) = 3
    c: Block(g6)
    c: Vertical(g7)
    c: Equal(g1,g7) = 3
    c: Vertical(g8)
    c: Equal(g0,g8) = 3
    c: Block(g8)
    c: Vertical(g9)
    c: Equal(g1,g9) = 3
    c: Vertical(g10)
    c: Equal(g0,g10) = 3
    c: Block(g10)
    c: Vertical(g11)
    c: Equal(g1,g11) = 3
    c: Block(g12)
    c: Block(g13)
    c: Block(g14)
    c: Block(g15)
    c: Block(g16)
    c: Block(g17)
    c: Block(g18)
    c: Block(g19)
    c: Block(g20)
    c: Block(g21)
    c: Block(g22)
    c: Block(g23)
    c: Block(g11)
    c: Block(g9)
    c: Block(g7)
    c: Block(g5)
    c: Block(g3)
    c: Block(g1)
    c: Coincident(g24,g0)
    c: Coincident(g24,g12)
    c: Horizontal(g24)
    c: Coincident(g25,g0)
    c: Coincident(g25,g12)
    c: Horizontal(g25)
    c: Coincident(g26,g1)
    c: Coincident(g26,g13)
    c: Horizontal(g26)
    c: Coincident(g27,g1)
    c: Coincident(g27,g13)
    c: Horizontal(g27)
    c: Coincident(g28,g2)
    c: Coincident(g28,g14)
    c: Horizontal(g28)
    c: Coincident(g29,g2)
    c: Coincident(g29,g14)
    c: Horizontal(g29)
    c: Coincident(g30,g3)
    c: Coincident(g30,g15)
    c: Horizontal(g30)
    c: Coincident(g31,g3)
    c: Coincident(g31,g15)
    c: Horizontal(g31)
    c: Coincident(g32,g4)
    c: Coincident(g32,g16)
    c: Horizontal(g32)
    c: Coincident(g33,g4)
    c: Coincident(g33,g16)
    c: Horizontal(g33)
    c: Coincident(g34,g5)
    c: Coincident(g34,g17)
    c: Horizontal(g34)
    c: Coincident(g35,g5)
    c: Coincident(g35,g17)
    c: Horizontal(g35)
    c: Coincident(g36,g6)
    c: Coincident(g36,g19)
    c: Horizontal(g36)
    c: Coincident(g37,g6)
    c: Coincident(g37,g19)
    c: Horizontal(g37)
    c: Coincident(g38,g7)
    c: Coincident(g38,g18)
    c: Horizontal(g38)
    c: Coincident(g39,g7)
    c: Coincident(g39,g18)
    c: Horizontal(g39)
    c: Coincident(g40,g8)
    c: Coincident(g40,g20)
    c: Horizontal(g40)
    c: Coincident(g41,g8)
    c: Coincident(g41,g20)
    c: Horizontal(g41)
    c: Coincident(g42,g9)
    c: Coincident(g42,g23)
    c: Horizontal(g42)
    c: Coincident(g43,g9)
    c: Coincident(g43,g23)
    c: Horizontal(g43)
    c: Coincident(g44,g10)
    c: Coincident(g44,g22)
    c: Horizontal(g44)
    c: Coincident(g45,g10)
    c: Coincident(g45,g22)
    c: Horizontal(g45)
    c: Coincident(g46,g11)
    c: Coincident(g46,g21)
    c: Horizontal(g46)
    c: Coincident(g47,g11)
    c: Coincident(g47,g21)
    c: Horizontal(g47)
FEATURE [Part::Extrusion] Extrude042
  Base = -> Sketch051
  Dir = (1,-2e-16,2e-16)
  DirMode = 2
  FaceMakerClass = Part::FaceMakerBullseye
  LengthFwd = 19
  LengthRev = 0
  Placement = pos=(-19,0,0) rot=(0,0,1;0rad)
  Solid = true
  Symmetric = false
FEATURE [Part::Fillet] Fillet035  label="removeToCreateVentalationHoles"
  Base = -> Extrude042
  Edges = <same value as first occurrence — deduplicated (x6 in doc)>
  Placement = pos=(7,0,0) rot=(0,0,1;0rad)
FEATURE [Part::Cut] Cut038  label="top017"
  Base = -> Cut033
  Tool = -> Fillet035
FEATURE [Sketcher::SketchObject] Sketch052  label="bottomSketch001"
  FullyConstrained = true
  sketch-geometry (45):
    g0: LineSegment StartX=6.29999 StartY=8 StartZ=0 EndX=3.29999 EndY=8 EndZ=0
    g1: LineSegment StartX=3.29999 StartY=8 StartZ=0 EndX=3.29999 EndY=-6.03275e-07 EndZ=0
    g2: ArcOfCircle CenterX=8.29999 CenterY=5 CenterZ=0 NormalX=0 NormalY=0 NormalZ=1 AngleXU=0 Radius=2 StartAngle=3.14159 EndAngle=4.71239
    g3: LineSegment StartX=6.29999 StartY=8 StartZ=0 EndX=6.29999 EndY=5 EndZ=0
    g4: ArcOfCircle CenterX=105 CenterY=19 CenterZ=0 NormalX=0 NormalY=0 NormalZ=1 AngleXU=0 Radius=12.7 StartAngle=4.71239 EndAngle=5.94289
    g5-g11: Circle x7 (B-spline internal-alignment scaffolding for g12; pole/knot coordinates omitted)
    g12: BSplineCurve PolesCount=7 KnotsCount=5 Degree=3 IsPeriodic=0
    g13-g17: GeomPoint x5 (B-spline internal-alignment scaffolding for g12; pole/knot coordinates omitted)
    g18: ArcOfCircle CenterX=105 CenterY=19 CenterZ=0 NormalX=0 NormalY=0 NormalZ=1 AngleXU=0 Radius=15.7 StartAngle=5.81226 EndAngle=6.28319
    g19: BSplineCurve PolesCount=5 KnotsCount=3 Degree=3 IsPeriodic=0
    g20: LineSegment StartX=8.29999 StartY=3 StartZ=0 EndX=101.7 EndY=3 EndZ=0
    g21: LineSegment StartX=3.29999 StartY=-6.03275e-07 StartZ=0 EndX=105 EndY=-6.03275e-07 EndZ=0
    g22: LineSegment StartX=120.974 StartY=8.71251 StartZ=0 EndX=122.332 EndY=7.83778 EndZ=0
    g23: LineSegment StartX=105 StartY=-6.03274e-07 StartZ=0 EndX=113 EndY=-6.03274e-07 EndZ=0
    g24: ArcOfCircle CenterX=105 CenterY=19 CenterZ=0 NormalX=0 NormalY=0 NormalZ=1 AngleXU=0 Radius=20.6155 StartAngle=5.11091 EndAngle=5.71103
    g25: ArcOfCircle CenterX=117.7 CenterY=19 CenterZ=0 NormalX=0 NormalY=0 NormalZ=1 AngleXU=0 Radius=3 StartAngle=1.2e-15 EndAngle=2.10468
    g26: Circle CenterX=116.345 CenterY=16.3232 CenterZ=0 NormalX=0 NormalY=0 NormalZ=1 AngleXU=0 Radius=1
    g27: Circle CenterX=117.24 CenterY=15.7584 CenterZ=0 NormalX=0 NormalY=0 NormalZ=1 AngleXU=0 Radius=1
    g28: Circle CenterX=116.972 CenterY=14.7612 CenterZ=0 NormalX=0 NormalY=0 NormalZ=1 AngleXU=0 Radius=1
    g29: BSplineCurve PolesCount=3 KnotsCount=2 Degree=2 IsPeriodic=0
    g30: GeomPoint X=116.345 Y=16.3232 Z=0
    g31: GeomPoint X=116.972 Y=14.7612 Z=0
    g32: Circle CenterX=115.828 CenterY=17.157 CenterZ=0 NormalX=0 NormalY=0 NormalZ=1 AngleXU=0 Radius=1
    g33: Circle CenterX=115.841 CenterY=16.639 CenterZ=0 NormalX=0 NormalY=0 NormalZ=1 AngleXU=0 Radius=1
    g34: Circle CenterX=116.345 CenterY=16.3232 CenterZ=0 NormalX=0 NormalY=0 NormalZ=1 AngleXU=0 Radius=1
    g35: BSplineCurve PolesCount=3 KnotsCount=2 Degree=2 IsPeriodic=0
    g36: GeomPoint X=115.828 Y=17.157 Z=0
    g37: GeomPoint X=116.345 Y=16.3232 Z=0
    g38: LineSegment StartX=115.828 StartY=17.157 StartZ=0 EndX=115.828 EndY=20.8307 EndZ=0
    g39: Circle CenterX=115.828 CenterY=20.8307 CenterZ=0 NormalX=0 NormalY=0 NormalZ=1 AngleXU=0 Radius=1
    g40: Circle CenterX=115.831 CenterY=21.3396 CenterZ=0 NormalX=0 NormalY=0 NormalZ=1 AngleXU=0 Radius=1
    g41: Circle CenterX=116.173 CenterY=21.5825 CenterZ=0 NormalX=0 NormalY=0 NormalZ=1 AngleXU=0 Radius=1
    g42: BSplineCurve PolesCount=3 KnotsCount=2 Degree=2 IsPeriodic=0
    g43: GeomPoint X=115.828 Y=20.8307 Z=0
    g44: GeomPoint X=116.173 Y=21.5825 Z=0
  constraints (70):
    c: Horizontal(g0)
    c: Distance(g0) = 3
    c: Coincident(g1,g0)
    c: Vertical(g1)
    c: Block(g2)
    c: Block(g0)
    c: Coincident(g3,g0)
    c: Coincident(g3,g2)
    c: Vertical(g3)
    c: Block(g1)
    c: Block(g4)
    c: Coincident(g19,g4)
    c: Block(g19)
    c: Equal(g5, g6-g11) x6
    c: InternalAlignment(g5-g11 -> g12) x7
    c: InternalAlignment(g13-g17 -> g12) x5
    c: Block(g12)
    c: Coincident(g18,g12)
    c: Block(g18)
    c: Coincident(g20,g2)
    c: Coincident(g20,g19)
    c: Horizontal(g20)
    c: Distance(g20) = 93.4
    c: Coincident(g21,g1)
    c: Horizontal(g21)
    c: Distance(g21) = 101.7
    c: Horizontal(g23)
    c: Distance(g23) = 8
    c: Coincident(g24,g23)
    c: Block(g23)
    c: Coincident(g22,g24)
    c: Block(g24)
    c: Block(g22)
    c: Distance(g22) = 1.61553
    c: Coincident(g25,g18)
    c: Block(g25)
    c: Weight(g26) = 1
    c: Equal(g26,g27)
    c: Equal(g26,g28)
    c: Coincident(g29,g4)
    c: InternalAlignment(g26,g29)
    c: InternalAlignment(g27,g29)
    c: InternalAlignment(g28,g29)
    c: InternalAlignment(g30,g29)
    c: InternalAlignment(g31,g29)
    c: Block(g29)
    c: Weight(g32) = 1
    c: Equal(g32,g33)
    c: Equal(g32,g34)
    c: Coincident(g35,g29)
    c: InternalAlignment(g32,g35)
    c: InternalAlignment(g33,g35)
    c: InternalAlignment(g34,g35)
    c: InternalAlignment(g36,g35)
    c: InternalAlignment(g37,g35)
    c: Block(g35)
    c: Coincident(g38,g35)
    c: Vertical(g38)
    c: Block(g38)
    c: Coincident(g42,g38)
    c: Weight(g39) = 1
    c: Equal(g39,g40)
    c: Equal(g39,g41)
    c: Coincident(g42,g25)
    c: InternalAlignment(g39,g42)
    c: InternalAlignment(g40,g42)
    c: InternalAlignment(g41,g42)
    c: InternalAlignment(g43,g42)
    c: InternalAlignment(g44,g42)
    c: Block(g42)
FEATURE [Part::Extrusion] Extrude043  label="bottom010"
  Base = -> Sketch052
  Dir = (0,0,1)
  DirMode = 2
  FaceMakerClass = Part::FaceMakerBullseye
  LengthFwd = 71.4
  LengthRev = 0
  Placement = pos=(0,0,0.3) rot=(0,0,1;0rad)
  Solid = true
  Symmetric = false
FEATURE [Sketcher::SketchObject] Sketch053  label="topSketch013"
  FullyConstrained = true
  sketch-geometry (22):
    g0: LineSegment StartX=5.21097e-06 StartY=3 StartZ=0 EndX=5.21097e-06 EndY=19 EndZ=0
    g1: ArcOfCircle CenterX=19 CenterY=19 CenterZ=0 NormalX=0 NormalY=0 NormalZ=1 AngleXU=0 Radius=19 StartAngle=1.5708 EndAngle=3.14159
    g2: ArcOfCircle CenterX=19 CenterY=19 CenterZ=0 NormalX=0 NormalY=0 NormalZ=1 AngleXU=0 Radius=16 StartAngle=1.5708 EndAngle=3.14159
    g3: LineSegment StartX=114 StartY=35 StartZ=0 EndX=19 EndY=35 EndZ=0
    g4: LineSegment StartX=5.21097e-06 StartY=3 StartZ=0 EndX=5.21097e-06 EndY=0 EndZ=0
    g5: LineSegment StartX=3 StartY=0 StartZ=0 EndX=5.21097e-06 EndY=0 EndZ=0
    g6: LineSegment StartX=3 StartY=19 StartZ=0 EndX=3 EndY=0 EndZ=0
    g7: LineSegment StartX=19 StartY=38 StartZ=0 EndX=124 EndY=38 EndZ=0
    g8: Circle CenterX=119 CenterY=35 CenterZ=0 NormalX=0 NormalY=0 NormalZ=1 AngleXU=0 Radius=1
    g9: Circle CenterX=121 CenterY=35 CenterZ=0 NormalX=0 NormalY=0 NormalZ=1 AngleXU=0 Radius=1
    g10: Circle CenterX=121 CenterY=33 CenterZ=0 NormalX=0 NormalY=0 NormalZ=1 AngleXU=0 Radius=1
    g11: BSplineCurve PolesCount=3 KnotsCount=2 Degree=2 IsPeriodic=0
    g12: GeomPoint X=119 Y=35 Z=0
    g13: GeomPoint X=121 Y=33 Z=0
    g14: LineSegment StartX=119 StartY=35 StartZ=0 EndX=114 EndY=35 EndZ=0
    g15: ArcOfCircle CenterX=105 CenterY=19 CenterZ=0 NormalX=0 NormalY=0 NormalZ=1 AngleXU=0 Radius=16 StartAngle=5.60905 EndAngle=6.28319
    g16: LineSegment StartX=121 StartY=33 StartZ=0 EndX=121 EndY=19 EndZ=0
    g17: LineSegment StartX=117.5 StartY=9.01251 StartZ=0 EndX=121.163 EndY=9.0125 EndZ=0
    g18: ArcOfCircle CenterX=105 CenterY=19 CenterZ=0 NormalX=0 NormalY=0 NormalZ=1 AngleXU=0 Radius=20.6155 StartAngle=5.7297 EndAngle=6.28319
    g19: LineSegment StartX=121.163 StartY=9.0125 StartZ=0 EndX=122.538 EndY=8.16329 EndZ=0
    g20: LineSegment StartX=124 StartY=38 StartZ=0 EndX=125.616 EndY=38 EndZ=0
    g21: LineSegment StartX=125.616 StartY=19 StartZ=0 EndX=125.616 EndY=38 EndZ=0
  constraints (50):
    c: Vertical(g0)
    c: Block(g0)
    c: Coincident(g1,g0)
    c: Block(g1)
    c: Coincident(g2,g1)
    c: Block(g2)
    c: Coincident(g3,g2)
    c: Horizontal(g3)
    c: Tangent(g3,g2)
    c: Coincident(g4,g0)
    c: Distance(g4) = 3
    c: Vertical(g4)
    c: Coincident(g5,g4)
    c: Horizontal(g5)
    c: Coincident(g6,g2)
    c: Coincident(g6,g5)
    c: Vertical(g6)
    c: Horizontal(g7)
    c: Distance(g7) = 105
    c: Coincident(g7,g1)
    c: Block(g3)
    c: Weight(g8) = 1
    c: Equal(g8,g9)
    c: Equal(g8,g10)
    c: InternalAlignment(g8,g11)
    c: InternalAlignment(g9,g11)
    c: InternalAlignment(g10,g11)
    c: InternalAlignment(g12,g11)
    c: InternalAlignment(g13,g11)
    c: Block(g11)
    c: Coincident(g14,g11)
    c: Coincident(g14,g3)
    c: Horizontal(g14)
    c: Block(g15)
    c: Coincident(g16,g11)
    c: Coincident(g16,g15)
    c: Vertical(g16)
    c: Distance(g16) = 14
    c: Coincident(g17,g15)
    c: Block(g18)
    c: Coincident(g19,g18)
    c: Coincident(g20,g7)
    c: Horizontal(g20)
    c: Vertical(g21)
    c: Coincident(g20,g21)
    c: Block(g20)
    c: Block(g21)
    c: Block(g19)
    c: Block(g17)
    c: Distance(g20) = 1.61553
FEATURE [Part::Extrusion] Extrude044
  Base = -> Sketch053
  Dir = (0,0,1)
  DirMode = 2
  FaceMakerClass = Part::FaceMakerBullseye
  LengthFwd = 72
  LengthRev = 0
  Solid = true
  Symmetric = false
FEATURE [Part::Fillet] Fillet036  label="top018"
  Base = -> Extrude044
  Edges = 1 edges r=2: [Edge41]
FEATURE [Sketcher::SketchObject] Sketch054
  FullyConstrained = false
  Placement = pos=(0,0,0) rot=(1,0,0;1.5708rad)
  sketch-geometry (24):
    g0: ArcOfCircle CenterX=-4 CenterY=-10.5 CenterZ=0 NormalX=0 NormalY=0 NormalZ=1 AngleXU=0 Radius=1.5 StartAngle=6e-16 EndAngle=3.14159
    g1: ArcOfCircle CenterX=-34.2 CenterY=-10.5 CenterZ=0 NormalX=0 NormalY=0 NormalZ=1 AngleXU=0 Radius=1.5 StartAngle=0 EndAngle=3.14159
    g2: ArcOfCircle CenterX=-34.2 CenterY=-27.7 CenterZ=0 NormalX=0 NormalY=0 NormalZ=1 AngleXU=0 Radius=1.5 StartAngle=3.14159 EndAngle=6.28319
    g3: ArcOfCircle CenterX=-4 CenterY=-27.7 CenterZ=0 NormalX=0 NormalY=0 NormalZ=1 AngleXU=0 Radius=1.5 StartAngle=3.1416 EndAngle=6.28319
    g4: ArcOfCircle CenterX=-10 CenterY=-4.3 CenterZ=0 NormalX=0 NormalY=0 NormalZ=1 AngleXU=0 Radius=1.5 StartAngle=2e-16 EndAngle=3.14159
    g5: ArcOfCircle CenterX=-16.1 CenterY=-1.8 CenterZ=0 NormalX=0 NormalY=0 NormalZ=1 AngleXU=0 Radius=1.5 StartAngle=5e-16 EndAngle=3.14159
    g6: ArcOfCircle CenterX=-22.1 CenterY=-1.8 CenterZ=0 NormalX=0 NormalY=0 NormalZ=1 AngleXU=0 Radius=1.5 StartAngle=5e-16 EndAngle=3.14159
    g7: ArcOfCircle CenterX=-28.2 CenterY=-4.3 CenterZ=0 NormalX=0 NormalY=0 NormalZ=1 AngleXU=0 Radius=1.5 StartAngle=2e-16 EndAngle=3.14159
    g8: ArcOfCircle CenterX=-10 CenterY=-33.9 CenterZ=0 NormalX=0 NormalY=0 NormalZ=1 AngleXU=0 Radius=1.5 StartAngle=3.14159 EndAngle=6.28319
    g9: ArcOfCircle CenterX=-16.1 CenterY=-36.4 CenterZ=0 NormalX=0 NormalY=0 NormalZ=1 AngleXU=0 Radius=1.5 StartAngle=3.14159 EndAngle=6.28319
    g10: ArcOfCircle CenterX=-22.1 CenterY=-36.4 CenterZ=0 NormalX=0 NormalY=0 NormalZ=1 AngleXU=0 Radius=1.5 StartAngle=3.14159 EndAngle=6.28319
    g11: ArcOfCircle CenterX=-28.2 CenterY=-33.9 CenterZ=0 NormalX=0 NormalY=0 NormalZ=1 AngleXU=0 Radius=1.5 StartAngle=3.14159 EndAngle=6.28319
    g12: LineSegment StartX=-35.7 StartY=-10.5 StartZ=0 EndX=-35.7 EndY=-27.7 EndZ=0
    g13: LineSegment StartX=-32.7 StartY=-10.5 StartZ=0 EndX=-32.7 EndY=-27.7 EndZ=0
    g14: LineSegment StartX=-29.7 StartY=-33.9 StartZ=0 EndX=-29.7 EndY=-4.3 EndZ=0
    g15: LineSegment StartX=-26.7 StartY=-33.9 StartZ=0 EndX=-26.7 EndY=-4.3 EndZ=0
    g16: LineSegment StartX=-2.5 StartY=-10.5 StartZ=0 EndX=-2.5 EndY=-27.7 EndZ=0
    g17: LineSegment StartX=-8.5 StartY=-4.3 StartZ=0 EndX=-8.5 EndY=-33.9 EndZ=0
    g18: LineSegment StartX=-5.5 StartY=-10.5 StartZ=0 EndX=-5.5 EndY=-27.7 EndZ=0
    g19: LineSegment StartX=-11.5 StartY=-4.3 StartZ=0 EndX=-11.5 EndY=-33.9 EndZ=0
    g20: LineSegment StartX=-14.6 StartY=-1.8 StartZ=0 EndX=-14.6 EndY=-36.4 EndZ=0
    g21: LineSegment StartX=-17.6 StartY=-1.8 StartZ=0 EndX=-17.6 EndY=-36.4 EndZ=0
    g22: LineSegment StartX=-20.6 StartY=-36.4 StartZ=0 EndX=-20.6 EndY=-1.8 EndZ=0
    g23: LineSegment StartX=-23.6 StartY=-1.8 StartZ=0 EndX=-23.6 EndY=-36.4 EndZ=0
  constraints (48):
    c: Block(g0)
    c: Block(g1)
    c: Block(g2)
    c: Block(g3)
    c: Block(g4)
    c: Block(g5)
    c: Block(g6)
    c: Block(g7)
    c: Block(g8)
    c: Block(g9)
    c: Block(g10)
    c: Block(g11)
    c: Coincident(g12,g1)
    c: Coincident(g12,g2)
    c: Vertical(g12)
    c: Coincident(g13,g1)
    c: Coincident(g13,g2)
    c: Vertical(g13)
    c: Coincident(g14,g11)
    c: Coincident(g14,g7)
    c: Vertical(g14)
    c: Coincident(g15,g11)
    c: Coincident(g15,g7)
    c: Vertical(g15)
    c: Coincident(g16,g0)
    c: Coincident(g16,g3)
    c: Vertical(g16)
    c: Coincident(g17,g4)
    c: Coincident(g17,g8)
    c: Vertical(g17)
    c: Coincident(g18,g0)
    c: Coincident(g18,g3)
    c: Vertical(g18)
    c: Coincident(g19,g4)
    c: Coincident(g19,g8)
    c: Vertical(g19)
    c: Coincident(g20,g5)
    c: Coincident(g20,g9)
    c: Vertical(g20)
    c: Coincident(g21,g5)
    c: Coincident(g21,g9)
    c: Vertical(g21)
    c: Coincident(g22,g10)
    c: Coincident(g22,g6)
    c: Vertical(g22)
    c: Coincident(g23,g6)
    c: Coincident(g23,g10)
    c: Vertical(g23)
FEATURE [Part::Extrusion] Extrude045  label="removeToCreateFanGrillHoles003"
  Base = -> Sketch054
  Dir = (0,-1,6e-16)
  DirMode = 2
  FaceMakerClass = Part::FaceMakerBullseye
  LengthFwd = 10
  LengthRev = 0
  Placement = pos=(65.4,44,54.82) rot=(0,0,1;0rad)
  Solid = true
  Symmetric = false
FEATURE [Part::Feature] Face105 .. Face108  x4 (patterned run collapsed; names and placements below)
  shape: bbox 3.5 x 17.8 x 2e-07 mm, 1 faces, 0 solids (baked)
FEATURE [Part::Revolution] Revolve113  label="removeToCreateScrewAndThreadedInsertHole041"
  Angle = 360
  Axis = (0,1,0)
  Base = (0,0,0)
  FaceMakerClass = Part::FaceMakerBullseye
  Placement = pos=(62.3,30.3,19.7) rot=(0,0,1;0rad)
  Solid = false
  Source = -> Face105
  Symmetric = false
FEATURE [Part::Revolution] Revolve114  label="removeToCreateScrewAndThreadedInsertHole042"
  Angle = 360
  Axis = (0,1,0)
  Base = (0,0,0)
  FaceMakerClass = Part::FaceMakerBullseye
  Placement = pos=(62.3,30.3,51.7) rot=(0,0,1;0rad)
  Solid = false
  Source = -> Face106
  Symmetric = false
FEATURE [Part::Revolution] Revolve115  label="removeToCreateScrewAndThreadedInsertHole043"
  Angle = 360
  Axis = (0,1,0)
  Base = (0,0,0)
  FaceMakerClass = Part::FaceMakerBullseye
  Placement = pos=(30.3,30.3,19.7) rot=(0,0,1;0rad)
  Solid = false
  Source = -> Face107
  Symmetric = false
FEATURE [Part::Revolution] Revolve116  label="removeToCreateScrewAndThreadedInsertHole044"
  Angle = 360
  Axis = (0,1,0)
  Base = (0,0,0)
  FaceMakerClass = Part::FaceMakerBullseye
  Placement = pos=(30.3,30.3,51.7) rot=(0,0,1;0rad)
  Solid = false
  Source = -> Face108
  Symmetric = false
FEATURE [Part::MultiFuse] Fusion083  label="createThreadedInsertHolesForFan004"
  Shapes = -> [Revolve113,Revolve114,Revolve115,Revolve116]
FEATURE [Part::Box] Box024  label="removeToCreteHoleForPlugHousing026"
  AttacherType = Attacher::AttachEngine3D
  Height = 28.6
  Length = 10
  Placement = pos=(-2,0,21.7) rot=(0,0,1;0rad)
  Width = 19
FEATURE [Part::Cylinder] Cylinder038  label="removeToCreteHoleForPlugHousing027"
  Angle = 360
  AttacherType = Attacher::AttachEngine3D
  Height = 20
  Placement = pos=(-2,19,36) rot=(0,1,0;1.5708rad)
  Radius = 14.3
FEATURE [Part::MultiFuse] Fusion084  label="removeToCreteHoleForPlugHousing028"
  Shapes = -> [Box024,Cylinder038]
FEATURE [Part::Cylinder] Cylinder039
  Angle = 360
  AttacherType = Attacher::AttachEngine3D
  Height = 20
  Placement = pos=(0,0,36.15) rot=(0,0,1;0rad)
  Radius = 14.3
FEATURE [Part::Cylinder] Cylinder040
  Angle = 360
  AttacherType = Attacher::AttachEngine3D
  Height = 10
  Placement = pos=(0,0,36.15) rot=(0,0,1;0rad)
  Radius = 4
FEATURE [Part::Box] Box025  label="removeToCreteHoleForPlugHousing030"
  AttacherType = Attacher::AttachEngine3D
  Height = 28.6
  Length = 20
  Placement = pos=(106.15,0,21.7) rot=(0,0,1;0rad)
  Width = 19
FEATURE [Part::MultiFuse] Fusion086  label="removeToCreteHoleForPlugHousing031"
  Placement = pos=(70,19,36) rot=(0,1,0;1.5708rad)
  Shapes = -> [Cylinder039,Cylinder040]
FEATURE [Part::MultiFuse] Fusion085  label="removeToCreteHoleForPlugHousing029"
  Shapes = -> [Box025,Fusion086]
FEATURE [Sketcher::SketchObject] Sketch055
  FullyConstrained = true
  Placement = pos=(117,19,0) rot=(0.57735,0.57735,0.57735;2.0944rad)
  sketch-geometry (48):
    g0: LineSegment StartX=-49.19 StartY=69.25 StartZ=0 EndX=-49.19 EndY=66.25 EndZ=0
    g1: LineSegment StartX=-49.19 StartY=63.5 StartZ=0 EndX=-49.19 EndY=60.5 EndZ=0
    g2: LineSegment StartX=-49.19 StartY=57.75 StartZ=0 EndX=-49.19 EndY=54.75 EndZ=0
    g3: LineSegment StartX=-49.19 StartY=52 StartZ=0 EndX=-49.19 EndY=49 EndZ=0
    g4: LineSegment StartX=-49.19 StartY=46.25 StartZ=0 EndX=-49.19 EndY=43.25 EndZ=0
    g5: LineSegment StartX=-49.19 StartY=40.5 StartZ=0 EndX=-49.19 EndY=37.5 EndZ=0
    g6: LineSegment StartX=-49.19 StartY=34.5 StartZ=0 EndX=-49.19 EndY=31.5 EndZ=0
    g7: LineSegment StartX=-49.19 StartY=28.75 StartZ=0 EndX=-49.19 EndY=25.75 EndZ=0
    g8: LineSegment StartX=-49.19 StartY=23 StartZ=0 EndX=-49.19 EndY=20 EndZ=0
    g9: LineSegment StartX=-49.19 StartY=17.25 StartZ=0 EndX=-49.19 EndY=14.25 EndZ=0
    g10: LineSegment StartX=-49.19 StartY=11.5 StartZ=0 EndX=-49.19 EndY=8.5 EndZ=0
    g11: LineSegment StartX=-49.19 StartY=5.75 StartZ=0 EndX=-49.19 EndY=2.75 EndZ=0
    g12: ArcOfCircle CenterX=-1.5 CenterY=67.75 CenterZ=0 NormalX=0 NormalY=0 NormalZ=1 AngleXU=0 Radius=1.5 StartAngle=4.71239 EndAngle=7.85398
    g13: ArcOfCircle CenterX=-1.5 CenterY=62 CenterZ=0 NormalX=0 NormalY=0 NormalZ=1 AngleXU=0 Radius=1.5 StartAngle=4.71239 EndAngle=7.85398
    g14: ArcOfCircle CenterX=-1.5 CenterY=56.25 CenterZ=0 NormalX=0 NormalY=0 NormalZ=1 AngleXU=0 Radius=1.5 StartAngle=4.71239 EndAngle=7.85398
    g15: ArcOfCircle CenterX=-11.49 CenterY=50.5 CenterZ=0 NormalX=0 NormalY=0 NormalZ=1 AngleXU=0 Radius=1.5 StartAngle=4.71239 EndAngle=7.85398
    g16: ArcOfCircle CenterX=-16.28 CenterY=44.75 CenterZ=0 NormalX=0 NormalY=0 NormalZ=1 AngleXU=0 Radius=1.5 StartAngle=4.71239 EndAngle=7.85398
    g17: ArcOfCircle CenterX=-18.2337 CenterY=39 CenterZ=0 NormalX=0 NormalY=0 NormalZ=1 AngleXU=0 Radius=1.5 StartAngle=4.71485 EndAngle=7.85398
    g18: ArcOfCircle CenterX=-16.2837 CenterY=27.25 CenterZ=0 NormalX=0 NormalY=0 NormalZ=1 AngleXU=0 Radius=1.5 StartAngle=4.71485 EndAngle=7.85398
    g19: ArcOfCircle CenterX=-18.2337 CenterY=33 CenterZ=0 NormalX=0 NormalY=0 NormalZ=1 AngleXU=0 Radius=1.5 StartAngle=4.71485 EndAngle=7.85398
    g20: ArcOfCircle CenterX=-11.49 CenterY=21.5 CenterZ=0 NormalX=0 NormalY=0 NormalZ=1 AngleXU=0 Radius=1.5 StartAngle=4.71239 EndAngle=7.85398
    g21: ArcOfCircle CenterX=-1.5 CenterY=4.25 CenterZ=0 NormalX=0 NormalY=0 NormalZ=1 AngleXU=0 Radius=1.5 StartAngle=4.71239 EndAngle=7.85398
    g22: ArcOfCircle CenterX=-1.5 CenterY=10 CenterZ=0 NormalX=0 NormalY=0 NormalZ=1 AngleXU=0 Radius=1.5 StartAngle=4.71239 EndAngle=7.85398
    g23: ArcOfCircle CenterX=-1.5 CenterY=15.75 CenterZ=0 NormalX=0 NormalY=0 NormalZ=1 AngleXU=0 Radius=1.5 StartAngle=4.71239 EndAngle=7.85398
    g24: LineSegment StartX=-49.19 StartY=69.25 StartZ=0 EndX=-1.5 EndY=69.25 EndZ=0
    g25: LineSegment StartX=-49.19 StartY=66.25 StartZ=0 EndX=-1.5 EndY=66.25 EndZ=0
    g26: LineSegment StartX=-49.19 StartY=63.5 StartZ=0 EndX=-1.5 EndY=63.5 EndZ=0
    g27: LineSegment StartX=-49.19 StartY=60.5 StartZ=0 EndX=-1.5 EndY=60.5 EndZ=0
    g28: LineSegment StartX=-49.19 StartY=57.75 StartZ=0 EndX=-1.5 EndY=57.75 EndZ=0
    g29: LineSegment StartX=-49.19 StartY=54.75 StartZ=0 EndX=-1.5 EndY=54.75 EndZ=0
    g30: LineSegment StartX=-49.19 StartY=52 StartZ=0 EndX=-11.49 EndY=52 EndZ=0
    g31: LineSegment StartX=-49.19 StartY=49 StartZ=0 EndX=-11.49 EndY=49 EndZ=0
    g32: LineSegment StartX=-49.19 StartY=46.25 StartZ=0 EndX=-16.28 EndY=46.25 EndZ=0
    g33: LineSegment StartX=-49.19 StartY=43.25 StartZ=0 EndX=-16.28 EndY=43.25 EndZ=0
    g34: LineSegment StartX=-49.19 StartY=40.5 StartZ=0 EndX=-18.2337 EndY=40.5 EndZ=0
    g35: LineSegment StartX=-49.19 StartY=37.5 StartZ=0 EndX=-18.23 EndY=37.5 EndZ=0
    g36: LineSegment StartX=-49.19 StartY=34.5 StartZ=0 EndX=-18.2337 EndY=34.5 EndZ=0
    g37: LineSegment StartX=-49.19 StartY=31.5 StartZ=0 EndX=-18.23 EndY=31.5 EndZ=0
    g38: LineSegment StartX=-49.19 StartY=28.75 StartZ=0 EndX=-16.2837 EndY=28.75 EndZ=0
    g39: LineSegment StartX=-49.19 StartY=25.75 StartZ=0 EndX=-16.28 EndY=25.75 EndZ=0
    g40: LineSegment StartX=-49.19 StartY=23 StartZ=0 EndX=-11.49 EndY=23 EndZ=0
    g41: LineSegment StartX=-49.19 StartY=20 StartZ=0 EndX=-11.49 EndY=20 EndZ=0
    g42: LineSegment StartX=-49.19 StartY=17.25 StartZ=0 EndX=-1.5 EndY=17.25 EndZ=0
    g43: LineSegment StartX=-49.19 StartY=14.25 StartZ=0 EndX=-1.5 EndY=14.25 EndZ=0
    g44: LineSegment StartX=-49.19 StartY=11.5 StartZ=0 EndX=-1.5 EndY=11.5 EndZ=0
    g45: LineSegment StartX=-49.19 StartY=8.5 StartZ=0 EndX=-1.5 EndY=8.5 EndZ=0
    g46: LineSegment StartX=-49.19 StartY=5.75 StartZ=0 EndX=-1.5 EndY=5.75 EndZ=0
    g47: LineSegment StartX=-49.19 StartY=2.75 StartZ=0 EndX=-1.5 EndY=2.75 EndZ=0
  constraints (120):
    c: Vertical(g0)
    c: Distance(g0) = 3
    c: Block(g0)
    c: Vertical(g1)
    c: Distance(g1) = 3
    c: Vertical(g2)
    c: Equal(g0,g2) = 3
    c: Block(g2)
    c: Vertical(g3)
    c: Equal(g1,g3) = 3
    c: Vertical(g4)
    c: Equal(g0,g4) = 3
    c: Block(g4)
    c: Vertical(g5)
    c: Equal(g1,g5) = 3
    c: Vertical(g6)
    c: Equal(g0,g6) = 3
    c: Block(g6)
    c: Vertical(g7)
    c: Equal(g1,g7) = 3
    c: Vertical(g8)
    c: Equal(g0,g8) = 3
    c: Block(g8)
    c: Vertical(g9)
    c: Equal(g1,g9) = 3
    c: Vertical(g10)
    c: Equal(g0,g10) = 3
    c: Block(g10)
    c: Vertical(g11)
    c: Equal(g1,g11) = 3
    c: Block(g12)
    c: Block(g13)
    c: Block(g14)
    c: Block(g15)
    c: Block(g16)
    c: Block(g17)
    c: Block(g18)
    c: Block(g19)
    c: Block(g20)
    c: Block(g21)
    c: Block(g22)
    c: Block(g23)
    c: Block(g11)
    c: Block(g9)
    c: Block(g7)
    c: Block(g5)
    c: Block(g3)
    c: Block(g1)
    c: Coincident(g24,g0)
    c: Coincident(g24,g12)
    c: Horizontal(g24)
    c: Coincident(g25,g0)
    c: Coincident(g25,g12)
    c: Horizontal(g25)
    c: Coincident(g26,g1)
    c: Coincident(g26,g13)
    c: Horizontal(g26)
    c: Coincident(g27,g1)
    c: Coincident(g27,g13)
    c: Horizontal(g27)
    c: Coincident(g28,g2)
    c: Coincident(g28,g14)
    c: Horizontal(g28)
    c: Coincident(g29,g2)
    c: Coincident(g29,g14)
    c: Horizontal(g29)
    c: Coincident(g30,g3)
    c: Coincident(g30,g15)
    c: Horizontal(g30)
    c: Coincident(g31,g3)
    c: Coincident(g31,g15)
    c: Horizontal(g31)
    c: Coincident(g32,g4)
    c: Coincident(g32,g16)
    c: Horizontal(g32)
    c: Coincident(g33,g4)
    c: Coincident(g33,g16)
    c: Horizontal(g33)
    c: Coincident(g34,g5)
    c: Coincident(g34,g17)
    c: Horizontal(g34)
    c: Coincident(g35,g5)
    c: Coincident(g35,g17)
    c: Horizontal(g35)
    c: Coincident(g36,g6)
    c: Coincident(g36,g19)
    c: Horizontal(g36)
    c: Coincident(g37,g6)
    c: Coincident(g37,g19)
    c: Horizontal(g37)
    c: Coincident(g38,g7)
    c: Coincident(g38,g18)
    c: Horizontal(g38)
    c: Coincident(g39,g7)
    c: Coincident(g39,g18)
    c: Horizontal(g39)
    c: Coincident(g40,g8)
    c: Coincident(g40,g20)
    c: Horizontal(g40)
    c: Coincident(g41,g8)
    c: Coincident(g41,g20)
    c: Horizontal(g41)
    c: Coincident(g42,g9)
    c: Coincident(g42,g23)
    c: Horizontal(g42)
    c: Coincident(g43,g9)
    c: Coincident(g43,g23)
    c: Horizontal(g43)
    c: Coincident(g44,g10)
    c: Coincident(g44,g22)
    c: Horizontal(g44)
    c: Coincident(g45,g10)
    c: Coincident(g45,g22)
    c: Horizontal(g45)
    c: Coincident(g46,g11)
    c: Coincident(g46,g21)
    c: Horizontal(g46)
    c: Coincident(g47,g11)
    c: Coincident(g47,g21)
    c: Horizontal(g47)
FEATURE [Part::Extrusion] Extrude046
  Base = -> Sketch055
  Dir = (1,0,0)
  DirMode = 2
  FaceMakerClass = Part::FaceMakerBullseye
  LengthFwd = 23
  LengthRev = 0
  Placement = pos=(-19,0,0) rot=(0,0,1;0rad)
  Solid = true
  Symmetric = false
FEATURE [Part::Fillet] Fillet038  label="removeToCreateVentalationHoles001"
  Base = -> Extrude046
  Edges = <same value as first occurrence — deduplicated (x6 in doc)>
  Placement = pos=(7,0,0) rot=(0,0,1;0rad)
FEATURE [Sketcher::SketchObject] Sketch056  label="topSketch014"
  FullyConstrained = true
  sketch-geometry (22):
    g0: LineSegment StartX=5.21097e-06 StartY=3 StartZ=0 EndX=5.21097e-06 EndY=19 EndZ=0
    g1: ArcOfCircle CenterX=19 CenterY=19 CenterZ=0 NormalX=0 NormalY=0 NormalZ=1 AngleXU=0 Radius=19 StartAngle=1.5708 EndAngle=3.14159
    g2: ArcOfCircle CenterX=19 CenterY=19 CenterZ=0 NormalX=0 NormalY=0 NormalZ=1 AngleXU=0 Radius=16 StartAngle=1.5708 EndAngle=3.14159
    g3: LineSegment StartX=114 StartY=35 StartZ=0 EndX=19 EndY=35 EndZ=0
    g4: LineSegment StartX=5.21097e-06 StartY=3 StartZ=0 EndX=5.21097e-06 EndY=0 EndZ=0
    g5: LineSegment StartX=3 StartY=0 StartZ=0 EndX=5.21097e-06 EndY=0 EndZ=0
    g6: LineSegment StartX=3 StartY=19 StartZ=0 EndX=3 EndY=0 EndZ=0
    g7: LineSegment StartX=19 StartY=38 StartZ=0 EndX=124 EndY=38 EndZ=0
    g8: Circle CenterX=119 CenterY=35 CenterZ=0 NormalX=0 NormalY=0 NormalZ=1 AngleXU=0 Radius=1
    g9: Circle CenterX=121 CenterY=35 CenterZ=0 NormalX=0 NormalY=0 NormalZ=1 AngleXU=0 Radius=1
    g10: Circle CenterX=121 CenterY=33 CenterZ=0 NormalX=0 NormalY=0 NormalZ=1 AngleXU=0 Radius=1
    g11: BSplineCurve PolesCount=3 KnotsCount=2 Degree=2 IsPeriodic=0
    g12: GeomPoint X=119 Y=35 Z=0
    g13: GeomPoint X=121 Y=33 Z=0
    g14: LineSegment StartX=119 StartY=35 StartZ=0 EndX=114 EndY=35 EndZ=0
    g15: ArcOfCircle CenterX=105 CenterY=19 CenterZ=0 NormalX=0 NormalY=0 NormalZ=1 AngleXU=0 Radius=16 StartAngle=5.60905 EndAngle=6.28319
    g16: LineSegment StartX=121 StartY=33 StartZ=0 EndX=121 EndY=19 EndZ=0
    g17: LineSegment StartX=117.5 StartY=9.01251 StartZ=0 EndX=121.163 EndY=9.0125 EndZ=0
    g18: ArcOfCircle CenterX=105 CenterY=19 CenterZ=0 NormalX=0 NormalY=0 NormalZ=1 AngleXU=0 Radius=20.6155 StartAngle=5.7297 EndAngle=6.28319
    g19: LineSegment StartX=121.163 StartY=9.0125 StartZ=0 EndX=122.538 EndY=8.16329 EndZ=0
    g20: LineSegment StartX=124 StartY=38 StartZ=0 EndX=125.616 EndY=38 EndZ=0
    g21: LineSegment StartX=125.616 StartY=19 StartZ=0 EndX=125.616 EndY=38 EndZ=0
  constraints (49):
    c: Vertical(g0)
    c: Block(g0)
    c: Coincident(g1,g0)
    c: Block(g1)
    c: Coincident(g2,g1)
    c: Block(g2)
    c: Coincident(g3,g2)
    c: Horizontal(g3)
    c: Tangent(g3,g2)
    c: Coincident(g4,g0)
    c: Distance(g4) = 3
    c: Vertical(g4)
    c: Coincident(g5,g4)
    c: Horizontal(g5)
    c: Coincident(g6,g2)
    c: Coincident(g6,g5)
    c: Vertical(g6)
    c: Horizontal(g7)
    c: Distance(g7) = 105
    c: Coincident(g7,g1)
    c: Block(g3)
    c: Weight(g8) = 1
    c: Equal(g8,g9)
    c: Equal(g8,g10)
    c: InternalAlignment(g8,g11)
    c: InternalAlignment(g9,g11)
    c: InternalAlignment(g10,g11)
    c: InternalAlignment(g12,g11)
    c: InternalAlignment(g13,g11)
    c: Block(g11)
    c: Coincident(g14,g11)
    c: Coincident(g14,g3)
    c: Horizontal(g14)
    c: Block(g15)
    c: Coincident(g16,g11)
    c: Coincident(g16,g15)
    c: Vertical(g16)
    c: Distance(g16) = 14
    c: Coincident(g17,g15)
    c: Block(g18)
    c: Coincident(g19,g18)
    c: Coincident(g20,g7)
    c: Horizontal(g20)
    c: Vertical(g21)
    c: Coincident(g20,g21)
    c: Block(g20)
    c: Block(g21)
    c: Block(g19)
    c: Block(g17)
FEATURE [Part::Box] Box026  label="removeToCreteHoleForPlugHousing032"
  AttacherType = Attacher::AttachEngine3D
  Height = 28.6
  Length = 10
  Placement = pos=(-2,0,21.7) rot=(0,0,1;0rad)
  Width = 19
FEATURE [Part::Feature] Face109 .. Face112  x4 (patterned run collapsed; names and placements below)
  shape: bbox 3.5 x 17.8 x 2e-07 mm, 1 faces, 0 solids (baked)
FEATURE [Part::Revolution] Revolve117  label="removeToCreateScrewAndThreadedInsertHole045"
  Angle = 360
  Axis = (0,1,0)
  Base = (0,0,0)
  FaceMakerClass = Part::FaceMakerBullseye
  Placement = pos=(62.3,30.3,19.7) rot=(0,0,1;0rad)
  Solid = false
  Source = -> Face109
  Symmetric = false
FEATURE [Part::Revolution] Revolve118  label="removeToCreateScrewAndThreadedInsertHole046"
  Angle = 360
  Axis = (0,1,0)
  Base = (0,0,0)
  FaceMakerClass = Part::FaceMakerBullseye
  Placement = pos=(62.3,30.3,51.7) rot=(0,0,1;0rad)
  Solid = false
  Source = -> Face110
  Symmetric = false
FEATURE [Part::Revolution] Revolve119  label="removeToCreateScrewAndThreadedInsertHole047"
  Angle = 360
  Axis = (0,1,0)
  Base = (0,0,0)
  FaceMakerClass = Part::FaceMakerBullseye
  Placement = pos=(30.3,30.3,19.7) rot=(0,0,1;0rad)
  Solid = false
  Source = -> Face111
  Symmetric = false
FEATURE [Part::Revolution] Revolve120  label="removeToCreateScrewAndThreadedInsertHole048"
  Angle = 360
  Axis = (0,1,0)
  Base = (0,0,0)
  FaceMakerClass = Part::FaceMakerBullseye
  Placement = pos=(30.3,30.3,51.7) rot=(0,0,1;0rad)
  Solid = false
  Source = -> Face112
  Symmetric = false
FEATURE [Part::MultiFuse] Fusion087  label="createThreadedInsertHolesForFan005"
  Shapes = -> [Revolve117,Revolve118,Revolve119,Revolve120]
FEATURE [Part::Extrusion] Extrude047
  Base = -> Sketch056
  Dir = (0,0,1)
  DirMode = 2
  FaceMakerClass = Part::FaceMakerBullseye
  LengthFwd = 72
  LengthRev = 0
  Solid = true
  Symmetric = false
FEATURE [Part::Fillet] Fillet039  label="top019"
  Base = -> Extrude047
  Edges = 1 edges r=2: [Edge35]
FEATURE [Sketcher::SketchObject] Sketch057
  FullyConstrained = false
  Placement = pos=(0,0,0) rot=(1,0,0;1.5708rad)
  sketch-geometry (24):
    g0: ArcOfCircle CenterX=-4 CenterY=-10.5 CenterZ=0 NormalX=0 NormalY=0 NormalZ=1 AngleXU=0 Radius=1.5 StartAngle=6e-16 EndAngle=3.14159
    g1: ArcOfCircle CenterX=-34.2 CenterY=-10.5 CenterZ=0 NormalX=0 NormalY=0 NormalZ=1 AngleXU=0 Radius=1.5 StartAngle=0 EndAngle=3.14159
    g2: ArcOfCircle CenterX=-34.2 CenterY=-27.7 CenterZ=0 NormalX=0 NormalY=0 NormalZ=1 AngleXU=0 Radius=1.5 StartAngle=3.14159 EndAngle=6.28319
    g3: ArcOfCircle CenterX=-4 CenterY=-27.7 CenterZ=0 NormalX=0 NormalY=0 NormalZ=1 AngleXU=0 Radius=1.5 StartAngle=3.1416 EndAngle=6.28319
    g4: ArcOfCircle CenterX=-10 CenterY=-4.3 CenterZ=0 NormalX=0 NormalY=0 NormalZ=1 AngleXU=0 Radius=1.5 StartAngle=2e-16 EndAngle=3.14159
    g5: ArcOfCircle CenterX=-16.1 CenterY=-1.8 CenterZ=0 NormalX=0 NormalY=0 NormalZ=1 AngleXU=0 Radius=1.5 StartAngle=5e-16 EndAngle=3.14159
    g6: ArcOfCircle CenterX=-22.1 CenterY=-1.8 CenterZ=0 NormalX=0 NormalY=0 NormalZ=1 AngleXU=0 Radius=1.5 StartAngle=5e-16 EndAngle=3.14159
    g7: ArcOfCircle CenterX=-28.2 CenterY=-4.3 CenterZ=0 NormalX=0 NormalY=0 NormalZ=1 AngleXU=0 Radius=1.5 StartAngle=2e-16 EndAngle=3.14159
    g8: ArcOfCircle CenterX=-10 CenterY=-33.9 CenterZ=0 NormalX=0 NormalY=0 NormalZ=1 AngleXU=0 Radius=1.5 StartAngle=3.14159 EndAngle=6.28319
    g9: ArcOfCircle CenterX=-16.1 CenterY=-36.4 CenterZ=0 NormalX=0 NormalY=0 NormalZ=1 AngleXU=0 Radius=1.5 StartAngle=3.14159 EndAngle=6.28319
    g10: ArcOfCircle CenterX=-22.1 CenterY=-36.4 CenterZ=0 NormalX=0 NormalY=0 NormalZ=1 AngleXU=0 Radius=1.5 StartAngle=3.14159 EndAngle=6.28319
    g11: ArcOfCircle CenterX=-28.2 CenterY=-33.9 CenterZ=0 NormalX=0 NormalY=0 NormalZ=1 AngleXU=0 Radius=1.5 StartAngle=3.14159 EndAngle=6.28319
    g12: LineSegment StartX=-35.7 StartY=-10.5 StartZ=0 EndX=-35.7 EndY=-27.7 EndZ=0
    g13: LineSegment StartX=-32.7 StartY=-10.5 StartZ=0 EndX=-32.7 EndY=-27.7 EndZ=0
    g14: LineSegment StartX=-29.7 StartY=-33.9 StartZ=0 EndX=-29.7 EndY=-4.3 EndZ=0
    g15: LineSegment StartX=-26.7 StartY=-33.9 StartZ=0 EndX=-26.7 EndY=-4.3 EndZ=0
    g16: LineSegment StartX=-2.5 StartY=-10.5 StartZ=0 EndX=-2.5 EndY=-27.7 EndZ=0
    g17: LineSegment StartX=-8.5 StartY=-4.3 StartZ=0 EndX=-8.5 EndY=-33.9 EndZ=0
    g18: LineSegment StartX=-5.5 StartY=-10.5 StartZ=0 EndX=-5.5 EndY=-27.7 EndZ=0
    g19: LineSegment StartX=-11.5 StartY=-4.3 StartZ=0 EndX=-11.5 EndY=-33.9 EndZ=0
    g20: LineSegment StartX=-14.6 StartY=-1.8 StartZ=0 EndX=-14.6 EndY=-36.4 EndZ=0
    g21: LineSegment StartX=-17.6 StartY=-1.8 StartZ=0 EndX=-17.6 EndY=-36.4 EndZ=0
    g22: LineSegment StartX=-20.6 StartY=-36.4 StartZ=0 EndX=-20.6 EndY=-1.8 EndZ=0
    g23: LineSegment StartX=-23.6 StartY=-1.8 StartZ=0 EndX=-23.6 EndY=-36.4 EndZ=0
  constraints (48):
    c: Block(g0)
    c: Block(g1)
    c: Block(g2)
    c: Block(g3)
    c: Block(g4)
    c: Block(g5)
    c: Block(g6)
    c: Block(g7)
    c: Block(g8)
    c: Block(g9)
    c: Block(g10)
    c: Block(g11)
    c: Coincident(g12,g1)
    c: Coincident(g12,g2)
    c: Vertical(g12)
    c: Coincident(g13,g1)
    c: Coincident(g13,g2)
    c: Vertical(g13)
    c: Coincident(g14,g11)
    c: Coincident(g14,g7)
    c: Vertical(g14)
    c: Coincident(g15,g11)
    c: Coincident(g15,g7)
    c: Vertical(g15)
    c: Coincident(g16,g0)
    c: Coincident(g16,g3)
    c: Vertical(g16)
    c: Coincident(g17,g4)
    c: Coincident(g17,g8)
    c: Vertical(g17)
    c: Coincident(g18,g0)
    c: Coincident(g18,g3)
    c: Vertical(g18)
    c: Coincident(g19,g4)
    c: Coincident(g19,g8)
    c: Vertical(g19)
    c: Coincident(g20,g5)
    c: Coincident(g20,g9)
    c: Vertical(g20)
    c: Coincident(g21,g5)
    c: Coincident(g21,g9)
    c: Vertical(g21)
    c: Coincident(g22,g10)
    c: Coincident(g22,g6)
    c: Vertical(g22)
    c: Coincident(g23,g6)
    c: Coincident(g23,g10)
    c: Vertical(g23)
FEATURE [Part::Extrusion] Extrude048  label="removeToCreateFanGrillHoles004"
  Base = -> Sketch057
  Dir = (0,-1,6e-16)
  DirMode = 2
  FaceMakerClass = Part::FaceMakerBullseye
  LengthFwd = 10
  LengthRev = 0
  Placement = pos=(65.4,44,54.82) rot=(0,0,1;0rad)
  Solid = true
  Symmetric = false
FEATURE [Part::Cut] Cut040  label="top021"
  Base = -> Fillet039
  Tool = -> Extrude048
FEATURE [Part::Cylinder] Cylinder041  label="removeToCreteHoleForPlugHousing034"
  Angle = 360
  AttacherType = Attacher::AttachEngine3D
  Height = 20
  Placement = pos=(-2,19,36) rot=(0,1,0;1.5708rad)
  Radius = 14.3
FEATURE [Part::MultiFuse] Fusion089  label="removeToCreteHoleForPlugHousing035"
  Shapes = -> [Box026,Cylinder041]
FEATURE [Part::Cylinder] Cylinder042
  Angle = 360
  AttacherType = Attacher::AttachEngine3D
  Height = 20
  Placement = pos=(0,0,36.15) rot=(0,0,1;0rad)
  Radius = 14.3
FEATURE [Part::Cylinder] Cylinder043
  Angle = 360
  AttacherType = Attacher::AttachEngine3D
  Height = 10
  Placement = pos=(0,0,36.15) rot=(0,0,1;0rad)
  Radius = 4
FEATURE [Part::Box] Box027  label="removeToCreteHoleForPlugHousing036"
  AttacherType = Attacher::AttachEngine3D
  Height = 28.6
  Length = 20
  Placement = pos=(106.15,0,21.7) rot=(0,0,1;0rad)
  Width = 19
FEATURE [Part::Cut] Cut041  label="top022"
  Base = -> Cut040
  Tool = -> Fusion087
FEATURE [Part::Cut] Cut039  label="top020"
  Base = -> Cut041
  Tool = -> Fusion089
FEATURE [Part::MultiFuse] Fusion090  label="removeToCreteHoleForPlugHousing037"
  Placement = pos=(70,19,36) rot=(0,1,0;1.5708rad)
  Shapes = -> [Cylinder042,Cylinder043]
FEATURE [Part::MultiFuse] Fusion088  label="removeToCreteHoleForPlugHousing033"
  Shapes = -> [Box027,Fusion090]
FEATURE [Part::Cut] Cut042  label="removeToCreteHoleForPlugHousing038"
  Base = -> Cut039
  Tool = -> Fusion088
FEATURE [Part::MultiFuse] Fusion091  label="removeFromTop"
  Shapes = -> [Fillet038,Fusion085,Fusion084,Fusion083,Extrude045]
FEATURE [Part::Cut] Cut043  label="REAL TOP ====="
  Base = -> Fillet036
  Tool = -> Fusion091
FEATURE [Part::MultiFuse] Fusion092  label="caseScrewPillarBracket016"
  Shapes = -> [Extrude030,Extrude031,Extrude032,Extrude033,Extrude034,Extrude035,Extrude036,Extrude037,Box013,Box014]
FEATURE [Sketcher::SketchObject] Sketch058  label="topSketch015"
  FullyConstrained = true
  sketch-geometry (20):
    g0: LineSegment StartX=5.21097e-06 StartY=3 StartZ=0 EndX=5.21097e-06 EndY=19 EndZ=0
    g1: ArcOfCircle CenterX=19 CenterY=19 CenterZ=0 NormalX=0 NormalY=0 NormalZ=1 AngleXU=0 Radius=19 StartAngle=1.5708 EndAngle=3.14159
    g2: ArcOfCircle CenterX=19 CenterY=19 CenterZ=0 NormalX=0 NormalY=0 NormalZ=1 AngleXU=0 Radius=16 StartAngle=1.5708 EndAngle=3.14159
    g3: LineSegment StartX=114 StartY=35 StartZ=0 EndX=19 EndY=35 EndZ=0
    g4: LineSegment StartX=5.21097e-06 StartY=3 StartZ=0 EndX=5.21097e-06 EndY=0 EndZ=0
    g5: LineSegment StartX=3 StartY=0 StartZ=0 EndX=5.21097e-06 EndY=0 EndZ=0
    g6: LineSegment StartX=3 StartY=19 StartZ=0 EndX=3 EndY=0 EndZ=0
    g7: LineSegment StartX=19 StartY=38 StartZ=0 EndX=124 EndY=38 EndZ=0
    g8: Circle CenterX=119 CenterY=35 CenterZ=0 NormalX=0 NormalY=0 NormalZ=1 AngleXU=0 Radius=1
    g9: Circle CenterX=121 CenterY=35 CenterZ=0 NormalX=0 NormalY=0 NormalZ=1 AngleXU=0 Radius=1
    g10: Circle CenterX=121 CenterY=33 CenterZ=0 NormalX=0 NormalY=0 NormalZ=1 AngleXU=0 Radius=1
    g11: BSplineCurve PolesCount=3 KnotsCount=2 Degree=2 IsPeriodic=0
    g12: GeomPoint X=119 Y=35 Z=0
    g13: GeomPoint X=121 Y=33 Z=0
    g14: LineSegment StartX=119 StartY=35 StartZ=0 EndX=114 EndY=35 EndZ=0
    g15: ArcOfCircle CenterX=105 CenterY=19 CenterZ=0 NormalX=0 NormalY=0 NormalZ=1 AngleXU=0 Radius=19 StartAngle=5.7297 EndAngle=6.28319
    g16: ArcOfCircle CenterX=105 CenterY=19 CenterZ=0 NormalX=0 NormalY=0 NormalZ=1 AngleXU=0 Radius=16 StartAngle=5.60905 EndAngle=6.28319
    g17: LineSegment StartX=121 StartY=33 StartZ=0 EndX=121 EndY=19 EndZ=0
    g18: LineSegment StartX=124 StartY=38 StartZ=0 EndX=124 EndY=19 EndZ=0
    g19: LineSegment StartX=117.5 StartY=9.01251 StartZ=0 EndX=121.163 EndY=9.0125 EndZ=0
  constraints (46):
    c: Vertical(g0)
    c: Block(g0)
    c: Coincident(g1,g0)
    c: Block(g1)
    c: Coincident(g2,g1)
    c: Block(g2)
    c: Coincident(g3,g2)
    c: Horizontal(g3)
    c: Tangent(g3,g2)
    c: Coincident(g4,g0)
    c: Distance(g4) = 3
    c: Vertical(g4)
    c: Coincident(g5,g4)
    c: Horizontal(g5)
    c: Coincident(g6,g2)
    c: Coincident(g6,g5)
    c: Vertical(g6)
    c: Horizontal(g7)
    c: Distance(g7) = 105
    c: Coincident(g7,g1)
    c: Block(g3)
    c: Weight(g8) = 1
    c: Equal(g8,g9)
    c: Equal(g8,g10)
    c: InternalAlignment(g8,g11)
    c: InternalAlignment(g9,g11)
    c: InternalAlignment(g10,g11)
    c: InternalAlignment(g12,g11)
    c: InternalAlignment(g13,g11)
    c: Block(g11)
    c: Coincident(g14,g11)
    c: Coincident(g14,g3)
    c: Horizontal(g14)
    c: Block(g15)
    c: Coincident(g16,g15)
    c: Block(g16)
    c: Coincident(g17,g11)
    c: Coincident(g17,g16)
    c: Vertical(g17)
    c: Distance(g17) = 14
    c: Coincident(g18,g7)
    c: Coincident(g18,g15)
    c: Vertical(g18)
    c: Distance(g18) = 19
    c: Coincident(g19,g16)
    c: Coincident(g19,g15)
FEATURE [Part::Extrusion] Extrude049  label="top023"
  Base = -> Sketch058
  Dir = (0,0,1)
  DirMode = 2
  FaceMakerClass = Part::FaceMakerBullseye
  LengthFwd = 72
  LengthRev = 0
  Solid = true
  Symmetric = false
FEATURE [Sketcher::SketchObject] Sketch059
  FullyConstrained = true
  MapMode = 3
  Placement = pos=(0,0,0) rot=(1,0,0;1.5708rad)
  Support = -> [Extrude049]
  sketch-geometry (8):
    g0: Circle CenterX=80.351 CenterY=-67.6202 CenterZ=0 NormalX=0 NormalY=0 NormalZ=1 AngleXU=0 Radius=2
    g1: Circle CenterX=80.351 CenterY=-67.6202 CenterZ=0 NormalX=0 NormalY=0 NormalZ=1 AngleXU=0 Radius=3
    g2: Circle CenterX=80.351 CenterY=-4.92017 CenterZ=0 NormalX=0 NormalY=0 NormalZ=1 AngleXU=0 Radius=2
    g3: Circle CenterX=80.351 CenterY=-4.92017 CenterZ=0 NormalX=0 NormalY=0 NormalZ=1 AngleXU=0 Radius=3
    g4: Circle CenterX=23.851 CenterY=-4.92017 CenterZ=0 NormalX=0 NormalY=0 NormalZ=1 AngleXU=0 Radius=2
    g5: Circle CenterX=23.851 CenterY=-4.92017 CenterZ=0 NormalX=0 NormalY=0 NormalZ=1 AngleXU=0 Radius=3
    g6: Circle CenterX=23.851 CenterY=-67.6202 CenterZ=0 NormalX=0 NormalY=0 NormalZ=1 AngleXU=0 Radius=2
    g7: Circle CenterX=23.851 CenterY=-67.6202 CenterZ=0 NormalX=0 NormalY=0 NormalZ=1 AngleXU=0 Radius=3
  constraints (8):
    c: Block(g3)
    c: Block(g2)
    c: Block(g1)
    c: Block(g0)
    c: Block(g6)
    c: Block(g7)
    c: Block(g4)
    c: Block(g5)
FEATURE [Sketcher::SketchObject] Sketch060
  FullyConstrained = true
  MapMode = 3
  Placement = pos=(0,0,0) rot=(1,0,0;1.5708rad)
  Support = -> [Extrude049]
  sketch-geometry (8):
    g0: Circle CenterX=80.351 CenterY=-67.6202 CenterZ=0 NormalX=0 NormalY=0 NormalZ=1 AngleXU=0 Radius=3
    g1: Circle CenterX=80.351 CenterY=-4.92017 CenterZ=0 NormalX=0 NormalY=0 NormalZ=1 AngleXU=0 Radius=3
    g2: Circle CenterX=23.851 CenterY=-4.92017 CenterZ=0 NormalX=0 NormalY=0 NormalZ=1 AngleXU=0 Radius=3
    g3: Circle CenterX=23.851 CenterY=-67.6202 CenterZ=0 NormalX=0 NormalY=0 NormalZ=1 AngleXU=0 Radius=3
    g4: Circle CenterX=23.851 CenterY=-67.6202 CenterZ=0 NormalX=0 NormalY=0 NormalZ=1 AngleXU=0 Radius=5
    g5: Circle CenterX=80.351 CenterY=-67.6202 CenterZ=0 NormalX=0 NormalY=0 NormalZ=1 AngleXU=0 Radius=5
    g6: Circle CenterX=23.851 CenterY=-4.92017 CenterZ=0 NormalX=0 NormalY=0 NormalZ=1 AngleXU=0 Radius=5
    g7: Circle CenterX=80.351 CenterY=-4.92017 CenterZ=0 NormalX=0 NormalY=0 NormalZ=1 AngleXU=0 Radius=5
  constraints (8):
    c: Block(g1)
    c: Block(g0)
    c: Block(g3)
    c: Block(g2)
    c: Block(g5)
    c: Block(g4)
    c: Block(g6)
    c: Block(g7)
FEATURE [Sketcher::SketchObject] Sketch061
  FullyConstrained = true
  MapMode = 3
  Placement = pos=(0,0,0) rot=(1,0,0;1.5708rad)
  sketch-geometry (8):
    g0: Circle CenterX=80.351 CenterY=-67.6202 CenterZ=0 NormalX=0 NormalY=0 NormalZ=1 AngleXU=0 Radius=3
    g1: Circle CenterX=80.351 CenterY=-4.92017 CenterZ=0 NormalX=0 NormalY=0 NormalZ=1 AngleXU=0 Radius=3
    g2: Circle CenterX=23.851 CenterY=-4.92017 CenterZ=0 NormalX=0 NormalY=0 NormalZ=1 AngleXU=0 Radius=3
    g3: Circle CenterX=23.851 CenterY=-67.6202 CenterZ=0 NormalX=0 NormalY=0 NormalZ=1 AngleXU=0 Radius=3
    g4: Circle CenterX=23.851 CenterY=-67.6202 CenterZ=0 NormalX=0 NormalY=0 NormalZ=1 AngleXU=0 Radius=5
    g5: Circle CenterX=80.351 CenterY=-67.6202 CenterZ=0 NormalX=0 NormalY=0 NormalZ=1 AngleXU=0 Radius=5
    g6: Circle CenterX=23.851 CenterY=-4.92017 CenterZ=0 NormalX=0 NormalY=0 NormalZ=1 AngleXU=0 Radius=5
    g7: Circle CenterX=80.351 CenterY=-4.92017 CenterZ=0 NormalX=0 NormalY=0 NormalZ=1 AngleXU=0 Radius=5
  constraints (8):
    c: Block(g1)
    c: Block(g0)
    c: Block(g3)
    c: Block(g2)
    c: Block(g5)
    c: Block(g4)
    c: Block(g6)
    c: Block(g7)
FEATURE [Sketcher::SketchObject] Sketch062  label="topSketch016"
  FullyConstrained = true
  sketch-geometry (20):
    g0: LineSegment StartX=5.21097e-06 StartY=3 StartZ=0 EndX=5.21097e-06 EndY=19 EndZ=0
    g1: ArcOfCircle CenterX=19 CenterY=19 CenterZ=0 NormalX=0 NormalY=0 NormalZ=1 AngleXU=0 Radius=19 StartAngle=1.5708 EndAngle=3.14159
    g2: ArcOfCircle CenterX=19 CenterY=19 CenterZ=0 NormalX=0 NormalY=0 NormalZ=1 AngleXU=0 Radius=16 StartAngle=1.5708 EndAngle=3.14159
    g3: LineSegment StartX=114 StartY=35 StartZ=0 EndX=19 EndY=35 EndZ=0
    g4: LineSegment StartX=5.21097e-06 StartY=3 StartZ=0 EndX=5.21097e-06 EndY=0 EndZ=0
    g5: LineSegment StartX=3 StartY=0 StartZ=0 EndX=5.21097e-06 EndY=0 EndZ=0
    g6: LineSegment StartX=3 StartY=19 StartZ=0 EndX=3 EndY=0 EndZ=0
    g7: LineSegment StartX=19 StartY=38 StartZ=0 EndX=124 EndY=38 EndZ=0
    g8: Circle CenterX=119 CenterY=35 CenterZ=0 NormalX=0 NormalY=0 NormalZ=1 AngleXU=0 Radius=1
    g9: Circle CenterX=121 CenterY=35 CenterZ=0 NormalX=0 NormalY=0 NormalZ=1 AngleXU=0 Radius=1
    g10: Circle CenterX=121 CenterY=33 CenterZ=0 NormalX=0 NormalY=0 NormalZ=1 AngleXU=0 Radius=1
    g11: BSplineCurve PolesCount=3 KnotsCount=2 Degree=2 IsPeriodic=0
    g12: GeomPoint X=119 Y=35 Z=0
    g13: GeomPoint X=121 Y=33 Z=0
    g14: LineSegment StartX=119 StartY=35 StartZ=0 EndX=114 EndY=35 EndZ=0
    g15: ArcOfCircle CenterX=105 CenterY=19 CenterZ=0 NormalX=0 NormalY=0 NormalZ=1 AngleXU=0 Radius=19 StartAngle=5.7297 EndAngle=6.28319
    g16: ArcOfCircle CenterX=105 CenterY=19 CenterZ=0 NormalX=0 NormalY=0 NormalZ=1 AngleXU=0 Radius=16 StartAngle=5.60905 EndAngle=6.28319
    g17: LineSegment StartX=121 StartY=33 StartZ=0 EndX=121 EndY=19 EndZ=0
    g18: LineSegment StartX=124 StartY=38 StartZ=0 EndX=124 EndY=19 EndZ=0
    g19: LineSegment StartX=117.5 StartY=9.01251 StartZ=0 EndX=121.163 EndY=9.0125 EndZ=0
  constraints (46):
    c: Vertical(g0)
    c: Block(g0)
    c: Coincident(g1,g0)
    c: Block(g1)
    c: Coincident(g2,g1)
    c: Block(g2)
    c: Coincident(g3,g2)
    c: Horizontal(g3)
    c: Tangent(g3,g2)
    c: Coincident(g4,g0)
    c: Distance(g4) = 3
    c: Vertical(g4)
    c: Coincident(g5,g4)
    c: Horizontal(g5)
    c: Coincident(g6,g2)
    c: Coincident(g6,g5)
    c: Vertical(g6)
    c: Horizontal(g7)
    c: Distance(g7) = 105
    c: Coincident(g7,g1)
    c: Block(g3)
    c: Weight(g8) = 1
    c: Equal(g8,g9)
    c: Equal(g8,g10)
    c: InternalAlignment(g8,g11)
    c: InternalAlignment(g9,g11)
    c: InternalAlignment(g10,g11)
    c: InternalAlignment(g12,g11)
    c: InternalAlignment(g13,g11)
    c: Block(g11)
    c: Coincident(g14,g11)
    c: Coincident(g14,g3)
    c: Horizontal(g14)
    c: Block(g15)
    c: Coincident(g16,g15)
    c: Block(g16)
    c: Coincident(g17,g11)
    c: Coincident(g17,g16)
    c: Vertical(g17)
    c: Distance(g17) = 14
    c: Coincident(g18,g7)
    c: Coincident(g18,g15)
    c: Vertical(g18)
    c: Distance(g18) = 19
    c: Coincident(g19,g16)
    c: Coincident(g19,g15)
FEATURE [Part::Extrusion] Extrude053  label="top024"
  Base = -> Sketch062
  Dir = (0,0,1)
  DirMode = 2
  FaceMakerClass = Part::FaceMakerBullseye
  LengthFwd = 72
  LengthRev = 0
  Solid = true
  Symmetric = false
FEATURE [Sketcher::SketchObject] Sketch063
  FullyConstrained = true
  MapMode = 3
  Placement = pos=(0,0,0) rot=(1,0,0;1.5708rad)
  Support = -> [Extrude053]
  sketch-geometry (8):
    g0: Circle CenterX=80.351 CenterY=-67.6202 CenterZ=0 NormalX=0 NormalY=0 NormalZ=1 AngleXU=0 Radius=2
    g1: Circle CenterX=80.351 CenterY=-67.6202 CenterZ=0 NormalX=0 NormalY=0 NormalZ=1 AngleXU=0 Radius=3
    g2: Circle CenterX=80.351 CenterY=-4.92017 CenterZ=0 NormalX=0 NormalY=0 NormalZ=1 AngleXU=0 Radius=2
    g3: Circle CenterX=80.351 CenterY=-4.92017 CenterZ=0 NormalX=0 NormalY=0 NormalZ=1 AngleXU=0 Radius=3
    g4: Circle CenterX=23.851 CenterY=-4.92017 CenterZ=0 NormalX=0 NormalY=0 NormalZ=1 AngleXU=0 Radius=2
    g5: Circle CenterX=23.851 CenterY=-4.92017 CenterZ=0 NormalX=0 NormalY=0 NormalZ=1 AngleXU=0 Radius=3
    g6: Circle CenterX=23.851 CenterY=-67.6202 CenterZ=0 NormalX=0 NormalY=0 NormalZ=1 AngleXU=0 Radius=2
    g7: Circle CenterX=23.851 CenterY=-67.6202 CenterZ=0 NormalX=0 NormalY=0 NormalZ=1 AngleXU=0 Radius=3
  constraints (8):
    c: Block(g3)
    c: Block(g2)
    c: Block(g1)
    c: Block(g0)
    c: Block(g6)
    c: Block(g7)
    c: Block(g4)
    c: Block(g5)
FEATURE [Part::Extrusion] Extrude054
  Base = -> Sketch063
  Dir = (0,-1,2e-16)
  DirMode = 2
  FaceMakerClass = Part::FaceMakerBullseye
  LengthFwd = 6
  LengthRev = 0
  Placement = pos=(0,9,0) rot=(0,0,1;0rad)
  Solid = true
  Symmetric = false
FEATURE [Sketcher::SketchObject] Sketch064  label="topSketch017"
  FullyConstrained = true
  sketch-geometry (20):
    g0: LineSegment StartX=5.21097e-06 StartY=3 StartZ=0 EndX=5.21097e-06 EndY=19 EndZ=0
    g1: ArcOfCircle CenterX=19 CenterY=19 CenterZ=0 NormalX=0 NormalY=0 NormalZ=1 AngleXU=0 Radius=19 StartAngle=1.5708 EndAngle=3.14159
    g2: ArcOfCircle CenterX=19 CenterY=19 CenterZ=0 NormalX=0 NormalY=0 NormalZ=1 AngleXU=0 Radius=16 StartAngle=1.5708 EndAngle=3.14159
    g3: LineSegment StartX=114 StartY=35 StartZ=0 EndX=19 EndY=35 EndZ=0
    g4: LineSegment StartX=5.21097e-06 StartY=3 StartZ=0 EndX=5.21097e-06 EndY=0 EndZ=0
    g5: LineSegment StartX=3 StartY=0 StartZ=0 EndX=5.21097e-06 EndY=0 EndZ=0
    g6: LineSegment StartX=3 StartY=19 StartZ=0 EndX=3 EndY=0 EndZ=0
    g7: LineSegment StartX=19 StartY=38 StartZ=0 EndX=124 EndY=38 EndZ=0
    g8: Circle CenterX=119 CenterY=35 CenterZ=0 NormalX=0 NormalY=0 NormalZ=1 AngleXU=0 Radius=1
    g9: Circle CenterX=121 CenterY=35 CenterZ=0 NormalX=0 NormalY=0 NormalZ=1 AngleXU=0 Radius=1
    g10: Circle CenterX=121 CenterY=33 CenterZ=0 NormalX=0 NormalY=0 NormalZ=1 AngleXU=0 Radius=1
    g11: BSplineCurve PolesCount=3 KnotsCount=2 Degree=2 IsPeriodic=0
    g12: GeomPoint X=119 Y=35 Z=0
    g13: GeomPoint X=121 Y=33 Z=0
    g14: LineSegment StartX=119 StartY=35 StartZ=0 EndX=114 EndY=35 EndZ=0
    g15: ArcOfCircle CenterX=105 CenterY=19 CenterZ=0 NormalX=0 NormalY=0 NormalZ=1 AngleXU=0 Radius=19 StartAngle=5.7297 EndAngle=6.28319
    g16: ArcOfCircle CenterX=105 CenterY=19 CenterZ=0 NormalX=0 NormalY=0 NormalZ=1 AngleXU=0 Radius=16 StartAngle=5.60905 EndAngle=6.28319
    g17: LineSegment StartX=121 StartY=33 StartZ=0 EndX=121 EndY=19 EndZ=0
    g18: LineSegment StartX=124 StartY=38 StartZ=0 EndX=124 EndY=19 EndZ=0
    g19: LineSegment StartX=117.5 StartY=9.01251 StartZ=0 EndX=121.163 EndY=9.0125 EndZ=0
  constraints (46):
    c: Vertical(g0)
    c: Block(g0)
    c: Coincident(g1,g0)
    c: Block(g1)
    c: Coincident(g2,g1)
    c: Block(g2)
    c: Coincident(g3,g2)
    c: Horizontal(g3)
    c: Tangent(g3,g2)
    c: Coincident(g4,g0)
    c: Distance(g4) = 3
    c: Vertical(g4)
    c: Coincident(g5,g4)
    c: Horizontal(g5)
    c: Coincident(g6,g2)
    c: Coincident(g6,g5)
    c: Vertical(g6)
    c: Horizontal(g7)
    c: Distance(g7) = 105
    c: Coincident(g7,g1)
    c: Block(g3)
    c: Weight(g8) = 1
    c: Equal(g8,g9)
    c: Equal(g8,g10)
    c: InternalAlignment(g8,g11)
    c: InternalAlignment(g9,g11)
    c: InternalAlignment(g10,g11)
    c: InternalAlignment(g12,g11)
    c: InternalAlignment(g13,g11)
    c: Block(g11)
    c: Coincident(g14,g11)
    c: Coincident(g14,g3)
    c: Horizontal(g14)
    c: Block(g15)
    c: Coincident(g16,g15)
    c: Block(g16)
    c: Coincident(g17,g11)
    c: Coincident(g17,g16)
    c: Vertical(g17)
    c: Distance(g17) = 14
    c: Coincident(g18,g7)
    c: Coincident(g18,g15)
    c: Vertical(g18)
    c: Distance(g18) = 19
    c: Coincident(g19,g16)
    c: Coincident(g19,g15)
FEATURE [Sketcher::SketchObject] Sketch065
  FullyConstrained = true
  MapMode = 3
  Placement = pos=(0,0,0) rot=(1,0,0;1.5708rad)
  sketch-geometry (8):
    g0: Circle CenterX=80.351 CenterY=-67.6202 CenterZ=0 NormalX=0 NormalY=0 NormalZ=1 AngleXU=0 Radius=3
    g1: Circle CenterX=80.351 CenterY=-4.92017 CenterZ=0 NormalX=0 NormalY=0 NormalZ=1 AngleXU=0 Radius=3
    g2: Circle CenterX=23.851 CenterY=-4.92017 CenterZ=0 NormalX=0 NormalY=0 NormalZ=1 AngleXU=0 Radius=3
    g3: Circle CenterX=23.851 CenterY=-67.6202 CenterZ=0 NormalX=0 NormalY=0 NormalZ=1 AngleXU=0 Radius=3
    g4: Circle CenterX=23.851 CenterY=-67.6202 CenterZ=0 NormalX=0 NormalY=0 NormalZ=1 AngleXU=0 Radius=5
    g5: Circle CenterX=80.351 CenterY=-67.6202 CenterZ=0 NormalX=0 NormalY=0 NormalZ=1 AngleXU=0 Radius=5
    g6: Circle CenterX=23.851 CenterY=-4.92017 CenterZ=0 NormalX=0 NormalY=0 NormalZ=1 AngleXU=0 Radius=5
    g7: Circle CenterX=80.351 CenterY=-4.92017 CenterZ=0 NormalX=0 NormalY=0 NormalZ=1 AngleXU=0 Radius=5
  constraints (8):
    c: Block(g1)
    c: Block(g0)
    c: Block(g3)
    c: Block(g2)
    c: Block(g5)
    c: Block(g4)
    c: Block(g6)
    c: Block(g7)
FEATURE [Part::Extrusion] Extrude056
  Base = -> Sketch065
  Dir = (0,-1,2e-16)
  DirMode = 2
  FaceMakerClass = Part::FaceMakerBullseye
  LengthFwd = 2
  LengthRev = 0
  Solid = true
  Symmetric = false
FEATURE [Part::Extrusion] Extrude057  label="top025"
  Base = -> Sketch064
  Dir = (0,0,1)
  DirMode = 2
  FaceMakerClass = Part::FaceMakerBullseye
  LengthFwd = 72
  LengthRev = 0
  Solid = true
  Symmetric = false
FEATURE [Sketcher::SketchObject] Sketch066
  FullyConstrained = true
  MapMode = 3
  Placement = pos=(0,0,0) rot=(1,0,0;1.5708rad)
  Support = -> [Extrude057]
  sketch-geometry (8):
    g0: Circle CenterX=80.351 CenterY=-67.6202 CenterZ=0 NormalX=0 NormalY=0 NormalZ=1 AngleXU=0 Radius=3
    g1: Circle CenterX=80.351 CenterY=-4.92017 CenterZ=0 NormalX=0 NormalY=0 NormalZ=1 AngleXU=0 Radius=3
    g2: Circle CenterX=23.851 CenterY=-4.92017 CenterZ=0 NormalX=0 NormalY=0 NormalZ=1 AngleXU=0 Radius=3
    g3: Circle CenterX=23.851 CenterY=-67.6202 CenterZ=0 NormalX=0 NormalY=0 NormalZ=1 AngleXU=0 Radius=3
    g4: Circle CenterX=23.851 CenterY=-67.6202 CenterZ=0 NormalX=0 NormalY=0 NormalZ=1 AngleXU=0 Radius=5
    g5: Circle CenterX=80.351 CenterY=-67.6202 CenterZ=0 NormalX=0 NormalY=0 NormalZ=1 AngleXU=0 Radius=5
    g6: Circle CenterX=23.851 CenterY=-4.92017 CenterZ=0 NormalX=0 NormalY=0 NormalZ=1 AngleXU=0 Radius=5
    g7: Circle CenterX=80.351 CenterY=-4.92017 CenterZ=0 NormalX=0 NormalY=0 NormalZ=1 AngleXU=0 Radius=5
  constraints (8):
    c: Block(g1)
    c: Block(g0)
    c: Block(g3)
    c: Block(g2)
    c: Block(g5)
    c: Block(g4)
    c: Block(g6)
    c: Block(g7)
FEATURE [Part::Extrusion] Extrude055
  Base = -> Sketch066
  Dir = (0,-1,2e-16)
  DirMode = 2
  FaceMakerClass = Part::FaceMakerBullseye
  LengthFwd = 2
  LengthRev = 0
  Solid = true
  Symmetric = false
FEATURE [Part::Fillet] Fillet041
  Base = -> Extrude056
  Edges = 4 edges r=1.99: [Edge6,Edge12,Edge18,Edge24]
FEATURE [Part::Cut] Cut045
  Base = -> Extrude055
  Placement = pos=(0,6,0) rot=(0,0,1;0rad)
  Tool = -> Fillet041
FEATURE [Part::MultiFuse] Fusion095  label="pcbScrewPillars"
  Placement = pos=(-3.2,-1,72.3) rot=(0,0,1;0rad)
  Shapes = -> [Cut045,Extrude054]
FEATURE [Part::Feature] Face113
  shape: bbox 3.2 x 1.5 x 2e-07 mm, 1 faces, 0 solids (baked)
FEATURE [Part::Revolution] Revolve121  label="backCaseScrewRetainer002"
  Angle = 360
  Axis = (0,1,0)
  Base = (0,0,0)
  FaceMakerClass = Part::FaceMakerBullseye
  Placement = pos=(12.5,3,62) rot=(0,0,1;0rad)
  Solid = false
  Source = -> Face113
  Symmetric = false
FEATURE [Part::Feature] Face114
  shape: bbox 3.2 x 1.5 x 2e-07 mm, 1 faces, 0 solids (baked)
FEATURE [Part::Feature] Face115
  shape: bbox 3.2 x 1.5 x 2e-07 mm, 1 faces, 0 solids (baked)
FEATURE [Part::Feature] Face116
  shape: bbox 3.2 x 1.5 x 2e-07 mm, 1 faces, 0 solids (baked)
FEATURE [Part::Revolution] Revolve122  label="frontCaseScrewRetainer004"
  Angle = 360
  Axis = (0,1,0)
  Base = (0,0,0)
  FaceMakerClass = Part::FaceMakerBullseye
  Placement = pos=(89.5,3,68.5) rot=(0,0,1;0rad)
  Solid = false
  Source = -> Face115
  Symmetric = false
FEATURE [Part::Revolution] Revolve123  label="frontCaseScrewRetainer005"
  Angle = 360
  Axis = (0,1,0)
  Base = (0,0,0)
  FaceMakerClass = Part::FaceMakerBullseye
  Placement = pos=(89.5,3,3.5) rot=(0,0,1;0rad)
  Solid = false
  Source = -> Face116
  Symmetric = false
FEATURE [Part::Revolution] Revolve124  label="backCaseScrewRetainer003"
  Angle = 360
  Axis = (0,1,0)
  Base = (0,0,0)
  FaceMakerClass = Part::FaceMakerBullseye
  Placement = pos=(12.5,3,10) rot=(0,0,1;0rad)
  Solid = false
  Source = -> Face114
  Symmetric = false
FEATURE [Part::Feature] Face117
  shape: bbox 3.6 x 3.2 x 2e-07 mm, 1 faces, 0 solids (baked)
FEATURE [Part::Revolution] Revolve125  label="moreFrontCaseScrewRetainer004"
  Angle = 360
  Axis = (0,1,0)
  Base = (0,0,0)
  FaceMakerClass = Part::FaceMakerBullseye
  Placement = pos=(109.5,4.5,68.5) rot=(0,0,1;0rad)
  Solid = false
  Source = -> Face117
  Symmetric = false
FEATURE [Part::Feature] Face118
  shape: bbox 3.6 x 3.2 x 2e-07 mm, 1 faces, 0 solids (baked)
FEATURE [Part::Revolution] Revolve126  label="moreFrontCaseScrewRetainer005"
  Angle = 360
  Axis = (0,1,0)
  Base = (0,0,0)
  FaceMakerClass = Part::FaceMakerBullseye
  Placement = pos=(109.5,4.5,3.5) rot=(0,0,1;0rad)
  Solid = false
  Source = -> Face118
  Symmetric = false
FEATURE [Part::MultiFuse] Fusion096  label="screwRetainers001"
  Shapes = -> [Revolve126,Revolve125,Revolve124,Revolve123,Revolve122,Revolve121]
FEATURE [Part::Feature] Face119
  shape: bbox 10 x 16.5 x 2e-07 mm, 1 faces, 0 solids (baked)
FEATURE [Part::Revolution] Revolve130  label="plugHousing050"
  Angle = 360
  Axis = (0,1,0)
  Base = (0,0,0)
  FaceMakerClass = Part::FaceMakerBullseye
  Placement = pos=(0,0,36.15) rot=(0,0,1;0rad)
  Solid = false
  Source = -> Face119
  Symmetric = false
FEATURE [Part::Feature] Face120
  shape: bbox 10 x 16.5 x 2e-07 mm, 1 faces, 0 solids (baked)
FEATURE [Part::Feature] Face121
  shape: bbox 10 x 16.5 x 2e-07 mm, 1 faces, 0 solids (baked)
FEATURE [Part::Revolution] Revolve127  label="plugHousing047"
  Angle = 360
  Axis = (0,1,0)
  Base = (0,0,0)
  FaceMakerClass = Part::FaceMakerBullseye
  Placement = pos=(0,0,36.15) rot=(0,0,1;0rad)
  Solid = false
  Source = -> Face121
  Symmetric = false
FEATURE [Part::Feature] Face122
  shape: bbox 10 x 16.5 x 2e-07 mm, 1 faces, 0 solids (baked)
FEATURE [Part::Feature] Face123
  shape: bbox 10 x 16.5 x 2e-07 mm, 1 faces, 0 solids (baked)
FEATURE [Part::Revolution] Revolve128  label="plugHousing048"
  Angle = 360
  Axis = (0,1,0)
  Base = (0,0,0)
  FaceMakerClass = Part::FaceMakerBullseye
  Placement = pos=(0,0,36.15) rot=(0,0,1;0rad)
  Solid = false
  Source = -> Face123
  Symmetric = false
FEATURE [Part::MultiFuse] Fusion100  label="plugHousing054"
  Placement = pos=(0,0,0) rot=(0,0,1;1.5708rad)
  Shapes = -> [Revolve130,Revolve128]
FEATURE [Part::Feature] Face124
  shape: bbox 10 x 16.5 x 2e-07 mm, 1 faces, 0 solids (baked)
FEATURE [Part::Feature] Face125
  shape: bbox 10 x 16.5 x 2e-07 mm, 1 faces, 0 solids (baked)
FEATURE [Part::Revolution] Revolve129  label="plugHousing049"
  Angle = 360
  Axis = (0,1,0)
  Base = (0,0,0)
  FaceMakerClass = Part::FaceMakerBullseye
  Placement = pos=(0,0,36.15) rot=(0,0,1;0rad)
  Solid = false
  Source = -> Face125
  Symmetric = false
FEATURE [Part::Feature] Face126
  shape: bbox 10 x 16.5 x 2e-07 mm, 1 faces, 0 solids (baked)
FEATURE [Part::Revolution] Revolve131  label="plugHousing058"
  Angle = 360
  Axis = (0,1,0)
  Base = (0,0,0)
  FaceMakerClass = Part::FaceMakerBullseye
  Placement = pos=(0,0,36.15) rot=(0,0,1;0rad)
  Solid = false
  Source = -> Face120
  Symmetric = false
FEATURE [Part::MultiFuse] Fusion099  label="plugHousing053"
  Placement = pos=(0,0,0) rot=(0,0,1;1.5708rad)
  Shapes = -> [Revolve127,Revolve131]
FEATURE [Part::MultiFuse] Fusion102  label="plugHousing056"
  Placement = pos=(0,19,0) rot=(0,0,1;3.14159rad)
  Shapes = -> [Fusion100,Fusion099]
FEATURE [Part::Revolution] Revolve132  label="plugHousing059"
  Angle = 360
  Axis = (0,1,0)
  Base = (0,0,0)
  FaceMakerClass = Part::FaceMakerBullseye
  Placement = pos=(0,0,36.15) rot=(0,0,1;0rad)
  Solid = false
  Source = -> Face126
  Symmetric = false
FEATURE [Part::Revolution] Revolve133  label="plugHousing060"
  Angle = 360
  Axis = (0,1,0)
  Base = (0,0,0)
  FaceMakerClass = Part::FaceMakerBullseye
  Placement = pos=(0,0,36.15) rot=(0,0,1;0rad)
  Solid = false
  Source = -> Face122
  Symmetric = false
FEATURE [Part::MultiFuse] Fusion097  label="plugHousing051"
  Placement = pos=(0,0,0) rot=(0,0,1;1.5708rad)
  Shapes = -> [Revolve133,Revolve132]
FEATURE [Part::Revolution] Revolve134  label="plugHousing061"
  Angle = 360
  Axis = (0,1,0)
  Base = (0,0,0)
  FaceMakerClass = Part::FaceMakerBullseye
  Placement = pos=(0,0,36.15) rot=(0,0,1;0rad)
  Solid = false
  Source = -> Face124
  Symmetric = false
FEATURE [Part::MultiFuse] Fusion101  label="plugHousing055"
  Placement = pos=(0,0,0) rot=(0,0,1;1.5708rad)
  Shapes = -> [Revolve129,Revolve134]
FEATURE [Part::MultiFuse] Fusion098  label="plugHousing052"
  Placement = pos=(0,19,0) rot=(0,0,1;3.14159rad)
  Shapes = -> [Fusion097,Fusion101]
FEATURE [Part::MultiFuse] Fusion103  label="plugHousing057"
  Placement = pos=(122.621,0,-0.15) rot=(0,0,1;0rad)
  Shapes = -> [Fusion102,Fusion098]
FEATURE [Part::Box] Box028  label="Cube015"
  AttacherType = Attacher::AttachEngine3D
  Height = 28
  Length = 3
  Placement = pos=(110.7,19,22) rot=(0,0,1;0rad)
  Width = 15.7
FEATURE [Part::Cylinder] Cylinder044
  Angle = 360
  AttacherType = Attacher::AttachEngine3D
  Height = 20
  Placement = pos=(0,0,36.15) rot=(0,0,1;0rad)
  Radius = 10.3
FEATURE [Part::Cylinder] Cylinder045
  Angle = 360
  AttacherType = Attacher::AttachEngine3D
  Height = 10
  Placement = pos=(0,0,36.15) rot=(0,0,1;0rad)
  Radius = 4
FEATURE [Part::MultiFuse] Fusion104  label="removeToCreteHoleForPlugHousing040"
  Placement = pos=(70,19,36) rot=(0,1,0;1.5708rad)
  Shapes = -> [Cylinder044,Cylinder045]
FEATURE [Part::Cut] Cut046  label="plugHousingTab003"
  Base = -> Box028
  Tool = -> Fusion104
FEATURE [Part::MultiFuse] Fusion105  label="plugHousing062"
  Shapes = -> [Fusion103,Cut046]
FEATURE [Part::Fillet] Fillet042
  Base = -> Fusion105
  Edges = 1 edges r=2: [Edge25]
FEATURE [Part::Fillet] Fillet043  label="plugHousing063"
  Base = -> Fillet042
  Edges = 1 edges r=2: [Edge8]
  Placement = pos=(7,0,0) rot=(0,0,1;0rad)
FEATURE [Part::Feature] Face127
  shape: bbox 10 x 16.5 x 2e-07 mm, 1 faces, 0 solids (baked)
FEATURE [Part::Feature] Face128
  shape: bbox 10 x 16.5 x 2e-07 mm, 1 faces, 0 solids (baked)
FEATURE [Part::Revolution] Revolve137  label="plugHousing070"
  Angle = 360
  Axis = (0,1,0)
  Base = (0,0,0)
  FaceMakerClass = Part::FaceMakerBullseye
  Placement = pos=(0,0,36.15) rot=(0,0,1;0rad)
  Solid = false
  Source = -> Face127
  Symmetric = false
FEATURE [Part::Revolution] Revolve140  label="plugHousing073"
  Angle = 360
  Axis = (0,1,0)
  Base = (0,0,0)
  FaceMakerClass = Part::FaceMakerBullseye
  Placement = pos=(0,0,36.15) rot=(0,0,1;0rad)
  Solid = false
  Source = -> Face128
  Symmetric = false
FEATURE [Part::Feature] Face129
  shape: bbox 10 x 16.5 x 2e-07 mm, 1 faces, 0 solids (baked)
FEATURE [Part::Revolution] Revolve138  label="plugHousing071"
  Angle = 360
  Axis = (0,1,0)
  Base = (0,0,0)
  FaceMakerClass = Part::FaceMakerBullseye
  Placement = pos=(0,0,36.15) rot=(0,0,1;0rad)
  Solid = false
  Source = -> Face129
  Symmetric = false
FEATURE [Part::Feature] Face130
  shape: bbox 10 x 16.5 x 2e-07 mm, 1 faces, 0 solids (baked)
FEATURE [Part::Revolution] Revolve139  label="plugHousing072"
  Angle = 360
  Axis = (0,1,0)
  Base = (0,0,0)
  FaceMakerClass = Part::FaceMakerBullseye
  Placement = pos=(0,0,36.15) rot=(0,0,1;0rad)
  Solid = false
  Source = -> Face130
  Symmetric = false
FEATURE [Part::Feature] Face131
  shape: bbox 10 x 16.5 x 2e-07 mm, 1 faces, 0 solids (baked)
FEATURE [Part::Revolution] Revolve135  label="plugHousing068"
  Angle = 360
  Axis = (0,1,0)
  Base = (0,0,0)
  FaceMakerClass = Part::FaceMakerBullseye
  Placement = pos=(0,0,36.15) rot=(0,0,1;0rad)
  Solid = false
  Source = -> Face131
  Symmetric = false
FEATURE [Part::MultiFuse] Fusion112  label="plugHousing078"
  Placement = pos=(0,0,0) rot=(0,0,1;1.5708rad)
  Shapes = -> [Revolve135,Revolve139]
FEATURE [Part::Feature] Face132
  shape: bbox 10 x 16.5 x 2e-07 mm, 1 faces, 0 solids (baked)
FEATURE [Part::Revolution] Revolve141  label="plugHousing074"
  Angle = 360
  Axis = (0,1,0)
  Base = (0,0,0)
  FaceMakerClass = Part::FaceMakerBullseye
  Placement = pos=(0,0,36.15) rot=(0,0,1;0rad)
  Solid = false
  Source = -> Face132
  Symmetric = false
FEATURE [Part::MultiFuse] Fusion110  label="plugHousing076"
  Placement = pos=(0,0,0) rot=(0,0,1;1.5708rad)
  Shapes = -> [Revolve141,Revolve140]
FEATURE [Part::Feature] Face133
  shape: bbox 10 x 16.5 x 2e-07 mm, 1 faces, 0 solids (baked)
FEATURE [Part::Revolution] Revolve136  label="plugHousing069"
  Angle = 360
  Axis = (0,1,0)
  Base = (0,0,0)
  FaceMakerClass = Part::FaceMakerBullseye
  Placement = pos=(0,0,36.15) rot=(0,0,1;0rad)
  Solid = false
  Source = -> Face133
  Symmetric = false
FEATURE [Part::MultiFuse] Fusion106  label="plugHousing064"
  Placement = pos=(0,0,0) rot=(0,0,1;1.5708rad)
  Shapes = -> [Revolve138,Revolve136]
FEATURE [Part::MultiFuse] Fusion108  label="plugHousing066"
  Placement = pos=(0,19,0) rot=(0,0,1;3.14159rad)
  Shapes = -> [Fusion106,Fusion112]
FEATURE [Part::Feature] Face134
  shape: bbox 10 x 16.5 x 2e-07 mm, 1 faces, 0 solids (baked)
FEATURE [Part::Revolution] Revolve142  label="plugHousing075"
  Angle = 360
  Axis = (0,1,0)
  Base = (0,0,0)
  FaceMakerClass = Part::FaceMakerBullseye
  Placement = pos=(0,0,36.15) rot=(0,0,1;0rad)
  Solid = false
  Source = -> Face134
  Symmetric = false
FEATURE [Part::MultiFuse] Fusion107  label="plugHousing065"
  Placement = pos=(0,0,0) rot=(0,0,1;1.5708rad)
  Shapes = -> [Revolve137,Revolve142]
FEATURE [Part::MultiFuse] Fusion111  label="plugHousing077"
  Placement = pos=(0,19,0) rot=(0,0,1;3.14159rad)
  Shapes = -> [Fusion110,Fusion107]
FEATURE [Part::MultiFuse] Fusion109  label="plugHousing067"
  Placement = pos=(131.236,0,-0.15) rot=(0,0,1;0rad)
  Shapes = -> [Fusion108,Fusion111]
FEATURE [Part::MultiFuse] Fusion113  label="plugHousing079"
  Shapes = -> [Fillet043,Fusion109]
FEATURE [Part::Feature] Face135
  shape: bbox 3.5 x 17.8 x 2e-07 mm, 1 faces, 0 solids (baked)
FEATURE [Part::Revolution] Revolve143  label="removeToCreateScrewAndThreadedInsertHole049"
  Angle = 360
  Axis = (0,1,0)
  Base = (0,0,0)
  FaceMakerClass = Part::FaceMakerBullseye
  Placement = pos=(12.5,0,10) rot=(0,0,1;0rad)
  Solid = false
  Source = -> Face135
  Symmetric = false
FEATURE [Part::Feature] Face136
  shape: bbox 3.5 x 17.8 x 2e-07 mm, 1 faces, 0 solids (baked)
FEATURE [Part::Revolution] Revolve144  label="removeToCreateScrewAndThreadedInsertHole050"
  Angle = 360
  Axis = (0,1,0)
  Base = (0,0,0)
  FaceMakerClass = Part::FaceMakerBullseye
  Placement = pos=(12.5,0,62) rot=(0,0,1;0rad)
  Solid = false
  Source = -> Face136
  Symmetric = false
FEATURE [Part::Feature] Face137
  shape: bbox 3.5 x 17.8 x 2e-07 mm, 1 faces, 0 solids (baked)
FEATURE [Part::Revolution] Revolve145  label="removeToCreateScrewAndThreadedInsertHole051"
  Angle = 360
  Axis = (0,1,0)
  Base = (0,0,0)
  FaceMakerClass = Part::FaceMakerBullseye
  Placement = pos=(89.5,0,68.5) rot=(0,0,1;0rad)
  Solid = false
  Source = -> Face137
  Symmetric = false
FEATURE [Part::Feature] Face138
  shape: bbox 3.5 x 17.8 x 2e-07 mm, 1 faces, 0 solids (baked)
FEATURE [Part::Revolution] Revolve146  label="removeToCreateScrewAndThreadedInsertHole052"
  Angle = 360
  Axis = (0,1,0)
  Base = (0,0,0)
  FaceMakerClass = Part::FaceMakerBullseye
  Placement = pos=(89.5,0,3.5) rot=(0,0,1;0rad)
  Solid = false
  Source = -> Face138
  Symmetric = false
FEATURE [Part::Feature] Face139
  shape: bbox 3.5 x 17.8 x 2e-07 mm, 1 faces, 0 solids (baked)
FEATURE [Part::Revolution] Revolve147  label="removeToCreateScrewAndThreadedInsertHole053"
  Angle = 360
  Axis = (0,1,0)
  Base = (0,0,0)
  FaceMakerClass = Part::FaceMakerBullseye
  Placement = pos=(109.5,4.7,3.5) rot=(0,0,1;0rad)
  Solid = false
  Source = -> Face139
  Symmetric = false
FEATURE [Part::Feature] Face140
  shape: bbox 3.5 x 17.8 x 2e-07 mm, 1 faces, 0 solids (baked)
FEATURE [Part::Revolution] Revolve148  label="removeToCreateScrewAndThreadedInsertHole054"
  Angle = 360
  Axis = (0,1,0)
  Base = (0,0,0)
  FaceMakerClass = Part::FaceMakerBullseye
  Placement = pos=(109.5,4.7,68.5) rot=(0,0,1;0rad)
  Solid = false
  Source = -> Face140
  Symmetric = false
FEATURE [Part::MultiFuse] Fusion114  label="removeToCreateScrewAndThreadedInsertHole055"
  Shapes = -> [Revolve148,Revolve147,Revolve146,Revolve145,Revolve144,Revolve143]
FEATURE [Part::Cut] Cut047  label="casePillars004"
  Base = -> Cut037
  Tool = -> Fusion114
FEATURE [Part::Feature] Face141
  shape: bbox 3.5 x 17.8 x 2e-07 mm, 1 faces, 0 solids (baked)
FEATURE [Part::Feature] Face142
  shape: bbox 3.5 x 17.8 x 2e-07 mm, 1 faces, 0 solids (baked)
FEATURE [Part::Feature] Face143
  shape: bbox 3.5 x 17.8 x 2e-07 mm, 1 faces, 0 solids (baked)
FEATURE [Part::Revolution] Revolve149  label="removeToCreateScrewAndThreadedInsertHole057"
  Angle = 360
  Axis = (0,1,0)
  Base = (0,0,0)
  FaceMakerClass = Part::FaceMakerBullseye
  Placement = pos=(12.5,0,10) rot=(0,0,1;0rad)
  Solid = false
  Source = -> Face141
  Symmetric = false
FEATURE [Part::Feature] Face144
  shape: bbox 3.5 x 17.8 x 2e-07 mm, 1 faces, 0 solids (baked)
FEATURE [Part::Feature] Face145
  shape: bbox 3.5 x 17.8 x 2e-07 mm, 1 faces, 0 solids (baked)
FEATURE [Part::Feature] Face146
  shape: bbox 3.5 x 17.8 x 2e-07 mm, 1 faces, 0 solids (baked)
FEATURE [Part::Revolution] Revolve150  label="removeToCreateScrewAndThreadedInsertHole058"
  Angle = 360
  Axis = (0,1,0)
  Base = (0,0,0)
  FaceMakerClass = Part::FaceMakerBullseye
  Placement = pos=(12.5,0,62) rot=(0,0,1;0rad)
  Solid = false
  Source = -> Face146
  Symmetric = false
FEATURE [Part::Revolution] Revolve151  label="removeToCreateScrewAndThreadedInsertHole059"
  Angle = 360
  Axis = (0,1,0)
  Base = (0,0,0)
  FaceMakerClass = Part::FaceMakerBullseye
  Placement = pos=(89.5,0,68.5) rot=(0,0,1;0rad)
  Solid = false
  Source = -> Face143
  Symmetric = false
FEATURE [Part::Revolution] Revolve152  label="removeToCreateScrewAndThreadedInsertHole060"
  Angle = 360
  Axis = (0,1,0)
  Base = (0,0,0)
  FaceMakerClass = Part::FaceMakerBullseye
  Placement = pos=(89.5,0,3.5) rot=(0,0,1;0rad)
  Solid = false
  Source = -> Face142
  Symmetric = false
FEATURE [Part::Revolution] Revolve153  label="removeToCreateScrewAndThreadedInsertHole061"
  Angle = 360
  Axis = (0,1,0)
  Base = (0,0,0)
  FaceMakerClass = Part::FaceMakerBullseye
  Placement = pos=(109.5,4.7,3.5) rot=(0,0,1;0rad)
  Solid = false
  Source = -> Face145
  Symmetric = false
FEATURE [Part::Revolution] Revolve154  label="removeToCreateScrewAndThreadedInsertHole062"
  Angle = 360
  Axis = (0,1,0)
  Base = (0,0,0)
  FaceMakerClass = Part::FaceMakerBullseye
  Placement = pos=(109.5,4.7,68.5) rot=(0,0,1;0rad)
  Solid = false
  Source = -> Face144
  Symmetric = false
FEATURE [Part::MultiFuse] Fusion115  label="removeToCreateScrewAndThreadedInsertHole056"
  Shapes = -> [Revolve154,Revolve153,Revolve152,Revolve151,Revolve150,Revolve149]
FEATURE [Part::Feature] Face147
  shape: bbox 9.8 x 26.5 x 2e-07 mm, 1 faces, 0 solids (baked)
FEATURE [Part::Revolution] Revolve155
  Angle = 360
  Axis = (0,1,0)
  Base = (0,0,0)
  FaceMakerClass = Part::FaceMakerBullseye
  Placement = pos=(0,0,0) rot=(0,0,1;1.5708rad)
  Solid = false
  Source = -> Face147
  Symmetric = false
FEATURE [Part::Feature] Face148
  shape: bbox 9.8 x 26.5 x 2e-07 mm, 1 faces, 0 solids (baked)
FEATURE [Part::Revolution] Revolve156
  Angle = 360
  Axis = (0,1,0)
  Base = (0,0,0)
  FaceMakerClass = Part::FaceMakerBullseye
  Placement = pos=(0,0,0) rot=(0,0,1;1.5708rad)
  Solid = false
  Source = -> Face148
  Symmetric = false
FEATURE [Part::MultiFuse] Fusion116
  Placement = pos=(-18,19,36) rot=(0,0,1;0rad)
  Shapes = -> [Revolve156,Revolve155]
FEATURE [Part::Box] Box029  label="Cube016"
  AttacherType = Attacher::AttachEngine3D
  Height = 28
  Length = 3
  Placement = pos=(110.7,19,22) rot=(0,0,1;0rad)
  Width = 15.7
FEATURE [Part::Cylinder] Cylinder046
  Angle = 360
  AttacherType = Attacher::AttachEngine3D
  Height = 10
  Placement = pos=(0,0,36.15) rot=(0,0,1;0rad)
  Radius = 4
FEATURE [Part::Cylinder] Cylinder047
  Angle = 360
  AttacherType = Attacher::AttachEngine3D
  Height = 20
  Placement = pos=(0,0,36.15) rot=(0,0,1;0rad)
  Radius = 10.3
FEATURE [Part::MultiFuse] Fusion117  label="removeToCreteHoleForPlugHousing041"
  Placement = pos=(70,19,36) rot=(0,1,0;1.5708rad)
  Shapes = -> [Cylinder047,Cylinder046]
FEATURE [Part::Cut] Cut049  label="plugHousingTab004"
  Base = -> Box029
  Placement = pos=(-107.4,-14,0) rot=(0,0,1;0rad)
  Tool = -> Fusion117
FEATURE [Part::Box] Box030  label="Cube017"
  AttacherType = Attacher::AttachEngine3D
  Height = 28
  Length = 3
  Placement = pos=(110.7,19,22) rot=(0,0,1;0rad)
  Width = 15.7
FEATURE [Part::Cylinder] Cylinder048
  Angle = 360
  AttacherType = Attacher::AttachEngine3D
  Height = 10
  Placement = pos=(0,0,36.15) rot=(0,0,1;0rad)
  Radius = 4
FEATURE [Part::Cylinder] Cylinder049
  Angle = 360
  AttacherType = Attacher::AttachEngine3D
  Height = 20
  Placement = pos=(0,0,36.15) rot=(0,0,1;0rad)
  Radius = 10.3
FEATURE [Part::MultiFuse] Fusion118  label="removeToCreteHoleForPlugHousing042"
  Placement = pos=(70,19,36) rot=(0,1,0;1.5708rad)
  Shapes = -> [Cylinder049,Cylinder048]
FEATURE [Part::Cut] Cut050  label="plugHousingTab005"
  Base = -> Box030
  Placement = pos=(-107.4,-14,0) rot=(0,0,1;0rad)
  Tool = -> Fusion118
FEATURE [Part::MultiFuse] Fusion119
  Placement = pos=(9.6,23,0) rot=(0,0,1;3.14159rad)
  Shapes = -> [Cut049,Cut050]
FEATURE [Part::Box] Box031  label="Cube018"
  AttacherType = Attacher::AttachEngine3D
  Height = 10
  Length = 3
  Placement = pos=(3.3,4,12) rot=(0,0,1;0rad)
  Width = 10
FEATURE [Part::Fillet] Fillet044
  Base = -> Box031
  Edges = 1 edges r=2: [Edge11]
FEATURE [Part::Box] Box032  label="Cube019"
  AttacherType = Attacher::AttachEngine3D
  Height = 10
  Length = 3
  Placement = pos=(3.3,4,50) rot=(0,0,1;0rad)
  Width = 10
FEATURE [Part::Fillet] Fillet045
  Base = -> Box032
  Edges = 1 edges r=2: [Edge12]
FEATURE [Part::Box] Box033  label="Cube020"
  AttacherType = Attacher::AttachEngine3D
  Height = 28
  Length = 4
  Placement = pos=(5,0,22) rot=(0,0,1;0rad)
  Width = 10
FEATURE [Part::Fillet] Fillet046
  Base = -> Box033
  Edges = 1 edges r=1: [Edge7]
FEATURE [Part::Fillet] Fillet047
  Base = -> Fillet046
  Edges = 1 edges r=2: [Edge5]
FEATURE [Part::Fillet] Fillet048
  Base = -> Fillet047
  Edges = 1 edges r=2: [Edge2]
FEATURE [Part::Cylinder] Cylinder050
  Angle = 360
  AttacherType = Attacher::AttachEngine3D
  Height = 20
  Placement = pos=(0,0,36.15) rot=(0,0,1;0rad)
  Radius = 8.2
FEATURE [Part::Cylinder] Cylinder051
  Angle = 360
  AttacherType = Attacher::AttachEngine3D
  Height = 10
  Placement = pos=(0,0,36.15) rot=(0,0,1;0rad)
  Radius = 4
FEATURE [Part::MultiFuse] Fusion120  label="removeToCreteHoleForPlugHousing043"
  Placement = pos=(-42,19,36) rot=(0,1,0;1.5708rad)
  Shapes = -> [Cylinder050,Cylinder051]
FEATURE [Sketcher::SketchObject] Sketch067  label="topSketch018"
  FullyConstrained = true
  sketch-geometry (4):
    g0: LineSegment StartX=16.8446 StartY=31.512 StartZ=0 EndX=16.3251 EndY=34.4666 EndZ=0
    g1: ArcOfCircle CenterX=19 CenterY=19.2524 CenterZ=0 NormalX=0 NormalY=0 NormalZ=1 AngleXU=0 Radius=15.4476 StartAngle=1.74483 EndAngle=2.72717
    g2: ArcOfCircle CenterX=19 CenterY=19.2524 CenterZ=0 NormalX=0 NormalY=0 NormalZ=1 AngleXU=0 Radius=12.4476 StartAngle=1.74483 EndAngle=2.73189
    g3: LineSegment StartX=4.86004 StartY=25.4725 StartZ=0 EndX=7.58253 EndY=24.2107 EndZ=0
  constraints (7):
    c: Block(g0)
    c: Coincident(g1,g0)
    c: Coincident(g2,g0)
    c: Coincident(g3,g1)
    c: Coincident(g3,g2)
    c: Block(g1)
    c: Block(g2)
FEATURE [Part::Extrusion] Extrude058
  Base = -> Sketch067
  Dir = (0,0,1)
  DirMode = 2
  FaceMakerClass = Part::FaceMakerBullseye
  LengthFwd = 10
  LengthRev = 0
  Placement = pos=(0,0,31) rot=(0,0,1;0rad)
  Solid = true
  Symmetric = false
FEATURE [Part::Cut] Cut051
  Base = -> Extrude058
  Tool = -> Fusion120
FEATURE [Part::Fillet] Fillet049
  Base = -> Cut051
  Edges = 1 edges r=2: [Edge1]
FEATURE [Part::Fillet] Fillet050
  Base = -> Fillet049
  Edges = 1 edges r=2.5: [Edge1]
FEATURE [Part::Fillet] Fillet051
  Base = -> Fillet050
  Edges = 1 edges r=2.5: [Edge2]
FEATURE [Part::MultiFuse] Fusion121  label="wireHolder003"
  Shapes = -> [Fusion116,Fillet051]
FEATURE [Part::MultiFuse] Fusion122
  Shapes = -> [Fillet045,Fusion121]
FEATURE [Part::MultiFuse] Fusion123  label="wireHolder004"
  Shapes = -> [Fusion122,Fillet048]
FEATURE [Part::MultiFuse] Fusion124  label="wireHolder005"
  Shapes = -> [Fillet044,Fusion119,Fusion123]
FEATURE [Sketcher::SketchObject] Sketch068  label="topSketch019"
  FullyConstrained = true
  sketch-geometry (6):
    g0: LineSegment StartX=19 StartY=38 StartZ=0 EndX=117 EndY=38 EndZ=0
    g1: ArcOfCircle CenterX=19 CenterY=19 CenterZ=0 NormalX=0 NormalY=0 NormalZ=1 AngleXU=0 Radius=19 StartAngle=1.5708 EndAngle=3.14159
    g2: LineSegment StartX=117 StartY=38 StartZ=0 EndX=117 EndY=19 EndZ=0
    g3: LineSegment StartX=98 StartY=1.0161e-12 StartZ=0 EndX=5.22862e-06 EndY=1.0161e-12 EndZ=0
    g4: LineSegment StartX=5.22862e-06 StartY=19 StartZ=0 EndX=5.22862e-06 EndY=1.0161e-12 EndZ=0
    g5: ArcOfCircle CenterX=98 CenterY=19 CenterZ=0 NormalX=0 NormalY=0 NormalZ=1 AngleXU=0 Radius=19 StartAngle=4.71239 EndAngle=6.28319
  constraints (16):
    c: Horizontal(g0)
    c: Distance(g0) = 98
    c: Coincident(g1,g0)
    c: Block(g1)
    c: Coincident(g2,g0)
    c: Vertical(g2)
    c: Distance(g2) = 19
    c: Horizontal(g3)
    c: Coincident(g4,g1)
    c: Vertical(g4)
    c: Coincident(g3,g4)
    c: Block(g3)
    c: Coincident(g5,g2)
    c: Coincident(g5,g3)
    c: Block(g0)
    c: Block(g5)
FEATURE [Part::Extrusion] Extrude059  label="sideA002"
  Base = -> Sketch068
  Dir = (0,0,1)
  DirMode = 2
  FaceMakerClass = Part::FaceMakerBullseye
  LengthFwd = 3
  LengthRev = 0
  Placement = pos=(0,0,-2.7) rot=(0,0,1;0rad)
  Solid = true
  Symmetric = false
FEATURE [Sketcher::SketchObject] Sketch069  label="topSketch020"
  FullyConstrained = true
  sketch-geometry (6):
    g0: LineSegment StartX=19 StartY=38 StartZ=0 EndX=117 EndY=38 EndZ=0
    g1: ArcOfCircle CenterX=19 CenterY=19 CenterZ=0 NormalX=0 NormalY=0 NormalZ=1 AngleXU=0 Radius=19 StartAngle=1.5708 EndAngle=3.14159
    g2: LineSegment StartX=117 StartY=38 StartZ=0 EndX=117 EndY=19 EndZ=0
    g3: LineSegment StartX=98 StartY=1.0161e-12 StartZ=0 EndX=5.22862e-06 EndY=1.0161e-12 EndZ=0
    g4: LineSegment StartX=5.22862e-06 StartY=19 StartZ=0 EndX=5.22862e-06 EndY=1.0161e-12 EndZ=0
    g5: ArcOfCircle CenterX=98 CenterY=19 CenterZ=0 NormalX=0 NormalY=0 NormalZ=1 AngleXU=0 Radius=19 StartAngle=4.71239 EndAngle=6.28319
  constraints (16):
    c: Horizontal(g0)
    c: Distance(g0) = 98
    c: Coincident(g1,g0)
    c: Block(g1)
    c: Coincident(g2,g0)
    c: Vertical(g2)
    c: Distance(g2) = 19
    c: Horizontal(g3)
    c: Coincident(g4,g1)
    c: Vertical(g4)
    c: Coincident(g3,g4)
    c: Block(g3)
    c: Coincident(g5,g2)
    c: Coincident(g5,g3)
    c: Block(g0)
    c: Block(g5)
FEATURE [Part::Extrusion] Extrude060  label="sideB002"
  Base = -> Sketch069
  Dir = (0,0,1)
  DirMode = 2
  FaceMakerClass = Part::FaceMakerBullseye
  LengthFwd = 3
  LengthRev = 0
  Placement = pos=(0,0,71.7) rot=(0,0,1;0rad)
  Solid = true
  Symmetric = false
FEATURE [Part::MultiFuse] Fusion127  label="removeFromBottom001"
  Placement = pos=(2,0,0) rot=(0,0,1;0rad)
  Shapes = -> [Extrude059,Extrude060]
FEATURE [Part::Cylinder] Cylinder052
  Angle = 360
  AttacherType = Attacher::AttachEngine3D
  Height = 20
  Placement = pos=(0,0,36.15) rot=(0,0,1;0rad)
  Radius = 14
FEATURE [Part::Cylinder] Cylinder053
  Angle = 360
  AttacherType = Attacher::AttachEngine3D
  Height = 10
  Placement = pos=(0,0,36.15) rot=(0,0,1;0rad)
  Radius = 4
FEATURE [Part::MultiFuse] Fusion128  label="removeToCreteHoleForPlugHousing044"
  Placement = pos=(70,19,36) rot=(0,1,0;1.5708rad)
  Shapes = -> [Cylinder052,Cylinder053]
FEATURE [Part::Cut] Cut052  label="bottom011"
  Base = -> Extrude043
  Tool = -> Fusion128
FEATURE [Part::Cut] Cut054  label="bottom012"
  Base = -> Cut052
  Tool = -> Fusion115
FEATURE [Sketcher::SketchObject] Sketch070
  FullyConstrained = true
  Placement = pos=(117,19,0) rot=(0.57735,0.57735,0.57735;2.0944rad)
  sketch-geometry (48):
    g0: LineSegment StartX=-49.19 StartY=69.25 StartZ=0 EndX=-49.19 EndY=66.25 EndZ=0
    g1: LineSegment StartX=-49.19 StartY=63.5 StartZ=0 EndX=-49.19 EndY=60.5 EndZ=0
    g2: LineSegment StartX=-49.19 StartY=57.75 StartZ=0 EndX=-49.19 EndY=54.75 EndZ=0
    g3: LineSegment StartX=-49.19 StartY=52 StartZ=0 EndX=-49.19 EndY=49 EndZ=0
    g4: LineSegment StartX=-49.19 StartY=46.25 StartZ=0 EndX=-49.19 EndY=43.25 EndZ=0
    g5: LineSegment StartX=-49.19 StartY=40.5 StartZ=0 EndX=-49.19 EndY=37.5 EndZ=0
    g6: LineSegment StartX=-49.19 StartY=34.5 StartZ=0 EndX=-49.19 EndY=31.5 EndZ=0
    g7: LineSegment StartX=-49.19 StartY=28.75 StartZ=0 EndX=-49.19 EndY=25.75 EndZ=0
    g8: LineSegment StartX=-49.19 StartY=23 StartZ=0 EndX=-49.19 EndY=20 EndZ=0
    g9: LineSegment StartX=-49.19 StartY=17.25 StartZ=0 EndX=-49.19 EndY=14.25 EndZ=0
    g10: LineSegment StartX=-49.19 StartY=11.5 StartZ=0 EndX=-49.19 EndY=8.5 EndZ=0
    g11: LineSegment StartX=-49.19 StartY=5.75 StartZ=0 EndX=-49.19 EndY=2.75 EndZ=0
    g12: ArcOfCircle CenterX=-1.5 CenterY=67.75 CenterZ=0 NormalX=0 NormalY=0 NormalZ=1 AngleXU=0 Radius=1.5 StartAngle=4.71239 EndAngle=7.85398
    g13: ArcOfCircle CenterX=-1.5 CenterY=62 CenterZ=0 NormalX=0 NormalY=0 NormalZ=1 AngleXU=0 Radius=1.5 StartAngle=4.71239 EndAngle=7.85398
    g14: ArcOfCircle CenterX=-1.5 CenterY=56.25 CenterZ=0 NormalX=0 NormalY=0 NormalZ=1 AngleXU=0 Radius=1.5 StartAngle=4.71239 EndAngle=7.85398
    g15: ArcOfCircle CenterX=-11.49 CenterY=50.5 CenterZ=0 NormalX=0 NormalY=0 NormalZ=1 AngleXU=0 Radius=1.5 StartAngle=4.71239 EndAngle=7.85398
    g16: ArcOfCircle CenterX=-16.28 CenterY=44.75 CenterZ=0 NormalX=0 NormalY=0 NormalZ=1 AngleXU=0 Radius=1.5 StartAngle=4.71239 EndAngle=7.85398
    g17: ArcOfCircle CenterX=-18.2337 CenterY=39 CenterZ=0 NormalX=0 NormalY=0 NormalZ=1 AngleXU=0 Radius=1.5 StartAngle=4.71485 EndAngle=7.85398
    g18: ArcOfCircle CenterX=-16.2837 CenterY=27.25 CenterZ=0 NormalX=0 NormalY=0 NormalZ=1 AngleXU=0 Radius=1.5 StartAngle=4.71485 EndAngle=7.85398
    g19: ArcOfCircle CenterX=-18.2337 CenterY=33 CenterZ=0 NormalX=0 NormalY=0 NormalZ=1 AngleXU=0 Radius=1.5 StartAngle=4.71485 EndAngle=7.85398
    g20: ArcOfCircle CenterX=-11.49 CenterY=21.5 CenterZ=0 NormalX=0 NormalY=0 NormalZ=1 AngleXU=0 Radius=1.5 StartAngle=4.71239 EndAngle=7.85398
    g21: ArcOfCircle CenterX=-1.5 CenterY=4.25 CenterZ=0 NormalX=0 NormalY=0 NormalZ=1 AngleXU=0 Radius=1.5 StartAngle=4.71239 EndAngle=7.85398
    g22: ArcOfCircle CenterX=-1.5 CenterY=10 CenterZ=0 NormalX=0 NormalY=0 NormalZ=1 AngleXU=0 Radius=1.5 StartAngle=4.71239 EndAngle=7.85398
    g23: ArcOfCircle CenterX=-1.5 CenterY=15.75 CenterZ=0 NormalX=0 NormalY=0 NormalZ=1 AngleXU=0 Radius=1.5 StartAngle=4.71239 EndAngle=7.85398
    g24: LineSegment StartX=-49.19 StartY=69.25 StartZ=0 EndX=-1.5 EndY=69.25 EndZ=0
    g25: LineSegment StartX=-49.19 StartY=66.25 StartZ=0 EndX=-1.5 EndY=66.25 EndZ=0
    g26: LineSegment StartX=-49.19 StartY=63.5 StartZ=0 EndX=-1.5 EndY=63.5 EndZ=0
    g27: LineSegment StartX=-49.19 StartY=60.5 StartZ=0 EndX=-1.5 EndY=60.5 EndZ=0
    g28: LineSegment StartX=-49.19 StartY=57.75 StartZ=0 EndX=-1.5 EndY=57.75 EndZ=0
    g29: LineSegment StartX=-49.19 StartY=54.75 StartZ=0 EndX=-1.5 EndY=54.75 EndZ=0
    g30: LineSegment StartX=-49.19 StartY=52 StartZ=0 EndX=-11.49 EndY=52 EndZ=0
    g31: LineSegment StartX=-49.19 StartY=49 StartZ=0 EndX=-11.49 EndY=49 EndZ=0
    g32: LineSegment StartX=-49.19 StartY=46.25 StartZ=0 EndX=-16.28 EndY=46.25 EndZ=0
    g33: LineSegment StartX=-49.19 StartY=43.25 StartZ=0 EndX=-16.28 EndY=43.25 EndZ=0
    g34: LineSegment StartX=-49.19 StartY=40.5 StartZ=0 EndX=-18.2337 EndY=40.5 EndZ=0
    g35: LineSegment StartX=-49.19 StartY=37.5 StartZ=0 EndX=-18.23 EndY=37.5 EndZ=0
    g36: LineSegment StartX=-49.19 StartY=34.5 StartZ=0 EndX=-18.2337 EndY=34.5 EndZ=0
    g37: LineSegment StartX=-49.19 StartY=31.5 StartZ=0 EndX=-18.23 EndY=31.5 EndZ=0
    g38: LineSegment StartX=-49.19 StartY=28.75 StartZ=0 EndX=-16.2837 EndY=28.75 EndZ=0
    g39: LineSegment StartX=-49.19 StartY=25.75 StartZ=0 EndX=-16.28 EndY=25.75 EndZ=0
    g40: LineSegment StartX=-49.19 StartY=23 StartZ=0 EndX=-11.49 EndY=23 EndZ=0
    g41: LineSegment StartX=-49.19 StartY=20 StartZ=0 EndX=-11.49 EndY=20 EndZ=0
    g42: LineSegment StartX=-49.19 StartY=17.25 StartZ=0 EndX=-1.5 EndY=17.25 EndZ=0
    g43: LineSegment StartX=-49.19 StartY=14.25 StartZ=0 EndX=-1.5 EndY=14.25 EndZ=0
    g44: LineSegment StartX=-49.19 StartY=11.5 StartZ=0 EndX=-1.5 EndY=11.5 EndZ=0
    g45: LineSegment StartX=-49.19 StartY=8.5 StartZ=0 EndX=-1.5 EndY=8.5 EndZ=0
    g46: LineSegment StartX=-49.19 StartY=5.75 StartZ=0 EndX=-1.5 EndY=5.75 EndZ=0
    g47: LineSegment StartX=-49.19 StartY=2.75 StartZ=0 EndX=-1.5 EndY=2.75 EndZ=0
  constraints (120):
    c: Vertical(g0)
    c: Distance(g0) = 3
    c: Block(g0)
    c: Vertical(g1)
    c: Distance(g1) = 3
    c: Vertical(g2)
    c: Equal(g0,g2) = 3
    c: Block(g2)
    c: Vertical(g3)
    c: Equal(g1,g3) = 3
    c: Vertical(g4)
    c: Equal(g0,g4) = 3
    c: Block(g4)
    c: Vertical(g5)
    c: Equal(g1,g5) = 3
    c: Vertical(g6)
    c: Equal(g0,g6) = 3
    c: Block(g6)
    c: Vertical(g7)
    c: Equal(g1,g7) = 3
    c: Vertical(g8)
    c: Equal(g0,g8) = 3
    c: Block(g8)
    c: Vertical(g9)
    c: Equal(g1,g9) = 3
    c: Vertical(g10)
    c: Equal(g0,g10) = 3
    c: Block(g10)
    c: Vertical(g11)
    c: Equal(g1,g11) = 3
    c: Block(g12)
    c: Block(g13)
    c: Block(g14)
    c: Block(g15)
    c: Block(g16)
    c: Block(g17)
    c: Block(g18)
    c: Block(g19)
    c: Block(g20)
    c: Block(g21)
    c: Block(g22)
    c: Block(g23)
    c: Block(g11)
    c: Block(g9)
    c: Block(g7)
    c: Block(g5)
    c: Block(g3)
    c: Block(g1)
    c: Coincident(g24,g0)
    c: Coincident(g24,g12)
    c: Horizontal(g24)
    c: Coincident(g25,g0)
    c: Coincident(g25,g12)
    c: Horizontal(g25)
    c: Coincident(g26,g1)
    c: Coincident(g26,g13)
    c: Horizontal(g26)
    c: Coincident(g27,g1)
    c: Coincident(g27,g13)
    c: Horizontal(g27)
    c: Coincident(g28,g2)
    c: Coincident(g28,g14)
    c: Horizontal(g28)
    c: Coincident(g29,g2)
    c: Coincident(g29,g14)
    c: Horizontal(g29)
    c: Coincident(g30,g3)
    c: Coincident(g30,g15)
    c: Horizontal(g30)
    c: Coincident(g31,g3)
    c: Coincident(g31,g15)
    c: Horizontal(g31)
    c: Coincident(g32,g4)
    c: Coincident(g32,g16)
    c: Horizontal(g32)
    c: Coincident(g33,g4)
    c: Coincident(g33,g16)
    c: Horizontal(g33)
    c: Coincident(g34,g5)
    c: Coincident(g34,g17)
    c: Horizontal(g34)
    c: Coincident(g35,g5)
    c: Coincident(g35,g17)
    c: Horizontal(g35)
    c: Coincident(g36,g6)
    c: Coincident(g36,g19)
    c: Horizontal(g36)
    c: Coincident(g37,g6)
    c: Coincident(g37,g19)
    c: Horizontal(g37)
    c: Coincident(g38,g7)
    c: Coincident(g38,g18)
    c: Horizontal(g38)
    c: Coincident(g39,g7)
    c: Coincident(g39,g18)
    c: Horizontal(g39)
    c: Coincident(g40,g8)
    c: Coincident(g40,g20)
    c: Horizontal(g40)
    c: Coincident(g41,g8)
    c: Coincident(g41,g20)
    c: Horizontal(g41)
    c: Coincident(g42,g9)
    c: Coincident(g42,g23)
    c: Horizontal(g42)
    c: Coincident(g43,g9)
    c: Coincident(g43,g23)
    c: Horizontal(g43)
    c: Coincident(g44,g10)
    c: Coincident(g44,g22)
    c: Horizontal(g44)
    c: Coincident(g45,g10)
    c: Coincident(g45,g22)
    c: Horizontal(g45)
    c: Coincident(g46,g11)
    c: Coincident(g46,g21)
    c: Horizontal(g46)
    c: Coincident(g47,g11)
    c: Coincident(g47,g21)
    c: Horizontal(g47)
FEATURE [Part::Extrusion] Extrude061
  Base = -> Sketch070
  Dir = (1,0,0)
  DirMode = 2
  FaceMakerClass = Part::FaceMakerBullseye
  LengthFwd = 23
  LengthRev = 0
  Placement = pos=(-19,0,0) rot=(0,0,1;0rad)
  Solid = true
  Symmetric = false
FEATURE [Part::Fillet] Fillet052  label="removeToCreateVentalationHoles002"
  Base = -> Extrude061
  Edges = <same value as first occurrence — deduplicated (x6 in doc)>
  Placement = pos=(7,0.02,0) rot=(0,0,1;0rad)
FEATURE [Part::MultiFuse] Fusion130  label="bottom013"
  Shapes = -> [Cut054,Cut034]
FEATURE [Part::Cut] Cut055
  Base = -> Fusion130
  Tool = -> Fillet052
FEATURE [Part::Cylinder] Cylinder054
  Angle = 360
  AttacherType = Attacher::AttachEngine3D
  Height = 20
  Placement = pos=(0,0,36.15) rot=(0,0,1;0rad)
  Radius = 4
FEATURE [Sketcher::SketchObject] Sketch071  label="bottomSketch002"
  FullyConstrained = true
  sketch-geometry (32):
    g0: LineSegment StartX=3.3 StartY=-6.03275e-07 StartZ=0 EndX=98 EndY=-6.03275e-07 EndZ=0
    g1: ArcOfCircle CenterX=98 CenterY=19 CenterZ=0 NormalX=0 NormalY=0 NormalZ=1 AngleXU=0 Radius=19 StartAngle=4.71239 EndAngle=5.71103
    g2: LineSegment StartX=6.3 StartY=8 StartZ=0 EndX=3.3 EndY=8 EndZ=0
    g3: LineSegment StartX=3.3 StartY=8 StartZ=0 EndX=3.3 EndY=-6.03275e-07 EndZ=0
    g4: ArcOfCircle CenterX=8.3 CenterY=5 CenterZ=0 NormalX=0 NormalY=0 NormalZ=1 AngleXU=0 Radius=2 StartAngle=3.14159 EndAngle=4.71239
    g5: LineSegment StartX=6.3 StartY=8 StartZ=0 EndX=6.3 EndY=5 EndZ=0
    g6: ArcOfCircle CenterX=98 CenterY=19 CenterZ=0 NormalX=0 NormalY=0 NormalZ=1 AngleXU=0 Radius=12.7 StartAngle=4.71239 EndAngle=6.28319
    g7: LineSegment StartX=94.7 StartY=3 StartZ=0 EndX=8.3 EndY=3 EndZ=0
    g8-g12: Circle x5 (B-spline internal-alignment scaffolding for g13; pole/knot coordinates omitted)
    g13: BSplineCurve PolesCount=5 KnotsCount=3 Degree=3 IsPeriodic=0
    g14: GeomPoint X=98 Y=6.3 Z=0
    g15: GeomPoint X=96.3938 Y=4.71946 Z=0
    g16: GeomPoint X=94.7 Y=3 Z=0
    g17-g23: Circle x7 (B-spline internal-alignment scaffolding for g24; pole/knot coordinates omitted)
    g24: BSplineCurve PolesCount=7 KnotsCount=5 Degree=3 IsPeriodic=0
    g25-g29: GeomPoint x5 (B-spline internal-alignment scaffolding for g24; pole/knot coordinates omitted)
    g30: ArcOfCircle CenterX=98 CenterY=19 CenterZ=0 NormalX=0 NormalY=0 NormalZ=1 AngleXU=0 Radius=15.7 StartAngle=5.81226 EndAngle=6.28319
    g31: LineSegment StartX=110.7 StartY=19 StartZ=0 EndX=113.7 EndY=19 EndZ=0
  constraints (41):
    c: Horizontal(g0)
    c: Coincident(g1,g0)
    c: Block(g1)
    c: Horizontal(g2)
    c: Distance(g2) = 3
    c: Coincident(g3,g2)
    c: Vertical(g3)
    c: Coincident(g3,g0)
    c: Block(g4)
    c: Block(g2)
    c: Coincident(g5,g2)
    c: Coincident(g5,g4)
    c: Vertical(g5)
    c: Coincident(g6,g1)
    c: Block(g6)
    c: Coincident(g7,g4)
    c: Horizontal(g7)
    c: Block(g0)
    c: Block(g7)
    c: Block(g3)
    c: Coincident(g13,g6)
    c: Weight(g8) = 1
    c: Equal(g8, g9-g12) x4
    c: Coincident(g13,g7)
    c: InternalAlignment(g8-g12 -> g13) x5
    c: InternalAlignment(g14,g13)
    c: InternalAlignment(g15,g13)
    c: InternalAlignment(g16,g13)
    c: Block(g13)
    c: Weight(g17) = 1
    c: Equal(g17, g18-g23) x6
    c: Coincident(g24,g1)
    c: InternalAlignment(g17-g23 -> g24) x7
    c: InternalAlignment(g25-g29 -> g24) x5
    c: Block(g24)
    c: Coincident(g30,g24)
    c: Coincident(g31,g6)
    c: Coincident(g31,g30)
    c: Horizontal(g31)
    c: Block(g31)
    c: Block(g30)
FEATURE [Part::Extrusion] Extrude062  label="bottom014"
  Base = -> Sketch071
  Dir = (0,0,1)
  DirMode = 2
  FaceMakerClass = Part::FaceMakerBullseye
  LengthFwd = 71.4
  LengthRev = 0
  Placement = pos=(0,0,0.3) rot=(0,0,1;0rad)
  Solid = true
  Symmetric = false
FEATURE [Part::Fillet] Fillet054
  Base = -> Extrude062
  Edges = 1 edges r=2.4: [Edge17]
FEATURE [Part::Fillet] Fillet055  label="bottom015"
  Base = -> Fillet054
  Edges = 1 edges r=2.4: [Edge36]
FEATURE [Part::Cylinder] Cylinder055
  Angle = 360
  AttacherType = Attacher::AttachEngine3D
  Height = 10
  Placement = pos=(0,0,36.15) rot=(0,0,1;0rad)
  Radius = 4
FEATURE [Part::MultiFuse] Fusion131  label="removeToCreateHoleForPlugHousing002"
  Placement = pos=(70,19,36.15) rot=(0,1,0;1.5708rad)
  Shapes = -> [Cylinder054,Cylinder055]
FEATURE [Part::Cut] Cut056  label="Bottom001"
  Base = -> Fillet055
  Placement = pos=(9,0,0) rot=(0,0,1;0rad)
  Tool = -> Fusion131
FEATURE [Part::Cut] Cut057
  Base = -> Cut055
  Tool = -> Cut056
FEATURE [Sketcher::SketchObject] Sketch072  label="topSketch021"
  FullyConstrained = true
  sketch-geometry (4):
    g0: ArcOfCircle CenterX=105 CenterY=19 CenterZ=0 NormalX=0 NormalY=0 NormalZ=1 AngleXU=0 Radius=20.6155 StartAngle=5.54125 EndAngle=6.28319
    g1: ArcOfCircle CenterX=105 CenterY=19 CenterZ=0 NormalX=0 NormalY=0 NormalZ=1 AngleXU=0 Radius=13 StartAngle=5.54125 EndAngle=6.28319
    g2: LineSegment StartX=118 StartY=19 StartZ=0 EndX=125.616 EndY=19 EndZ=0
    g3: LineSegment StartX=114.583 StartY=10.2157 StartZ=0 EndX=120.197 EndY=5.06982 EndZ=0
  constraints (7):
    c: Block(g0)
    c: Block(g1)
    c: Coincident(g2,g1)
    c: Coincident(g2,g0)
    c: Horizontal(g2)
    c: Coincident(g3,g1)
    c: Coincident(g3,g0)
FEATURE [Part::Extrusion] Extrude063  label="bottomPlugHousingBit003"
  Base = -> Sketch072
  Dir = (0,0,1)
  DirMode = 2
  FaceMakerClass = Part::FaceMakerBullseye
  LengthFwd = 72
  LengthRev = 0
  Solid = true
  Symmetric = false
FEATURE [Part::Cylinder] Cylinder056
  Angle = 360
  AttacherType = Attacher::AttachEngine3D
  Height = 20
  Placement = pos=(0,0,36.15) rot=(0,0,1;0rad)
  Radius = 14.3
FEATURE [Part::Cylinder] Cylinder057
  Angle = 360
  AttacherType = Attacher::AttachEngine3D
  Height = 10
  Placement = pos=(0,0,36.15) rot=(0,0,1;0rad)
  Radius = 4
FEATURE [Part::Box] Box034  label="removeToCreteHoleForPlugHousing047"
  AttacherType = Attacher::AttachEngine3D
  Height = 28.6
  Length = 20
  Placement = pos=(106.15,0,21.7) rot=(0,0,1;0rad)
  Width = 19
FEATURE [Part::Cylinder] Cylinder058
  Angle = 360
  AttacherType = Attacher::AttachEngine3D
  Height = 20
  Placement = pos=(0,0,36.15) rot=(0,0,1;0rad)
  Radius = 14.3
FEATURE [Part::Cylinder] Cylinder059
  Angle = 360
  AttacherType = Attacher::AttachEngine3D
  Height = 10
  Placement = pos=(0,0,36.15) rot=(0,0,1;0rad)
  Radius = 4
FEATURE [Part::MultiFuse] Fusion134  label="removeToCreteHoleForPlugHousing046"
  Placement = pos=(70,19,36) rot=(0,1,0;1.5708rad)
  Shapes = -> [Cylinder058,Cylinder059]
FEATURE [Part::Cylinder] Cylinder060
  Angle = 360
  AttacherType = Attacher::AttachEngine3D
  Height = 20
  Placement = pos=(0,0,36.15) rot=(0,0,1;0rad)
  Radius = 14
FEATURE [Part::Cylinder] Cylinder061
  Angle = 360
  AttacherType = Attacher::AttachEngine3D
  Height = 10
  Placement = pos=(0,0,36.15) rot=(0,0,1;0rad)
  Radius = 4
FEATURE [Part::MultiFuse] Fusion135  label="removeToCreteHoleForPlugHousing048"
  Placement = pos=(70,19,36) rot=(0,1,0;1.5708rad)
  Shapes = -> [Cylinder060,Cylinder061]
FEATURE [Part::Box] Box035  label="removeToCreteHoleForPlugHousing049"
  AttacherType = Attacher::AttachEngine3D
  Height = 28.6
  Length = 20
  Placement = pos=(106.15,0,21.7) rot=(0,0,1;0rad)
  Width = 19
FEATURE [Part::MultiFuse] Fusion133  label="removeToCreteHoleForPlugHousing045"
  Placement = pos=(0,0,-28.3) rot=(0,0,1;0rad)
  Shapes = -> [Box035,Fusion134]
FEATURE [Part::MultiFuse] Fusion138  label="removeToCreteHoleForPlugHousing051"
  Placement = pos=(70,19,36) rot=(0,1,0;1.5708rad)
  Shapes = -> [Cylinder056,Cylinder057]
FEATURE [Part::MultiFuse] Fusion137  label="removeToCreteHoleForPlugHousing050"
  Placement = pos=(0,0,28.3) rot=(0,0,1;0rad)
  Shapes = -> [Box034,Fusion138]
FEATURE [Part::MultiFuse] Fusion132  label="removeToCreatePlugHousingBottomBit002"
  Shapes = -> [Fusion133,Fusion137]
FEATURE [Part::MultiFuse] Fusion136  label="removeToCreatePlugHousingBottomBit003"
  Shapes = -> [Fusion135,Fusion132]
FEATURE [Part::Cut] Cut058  label="bottomPlugHousingBit002"
  Base = -> Extrude063
  Placement = pos=(-0.09,0,0) rot=(0,0,1;0rad)
  Tool = -> Fusion136
FEATURE [Sketcher::SketchObject] Sketch073  label="bottomSketch003"
  FullyConstrained = true
  sketch-geometry (45):
    g0: LineSegment StartX=6.29999 StartY=8 StartZ=0 EndX=3.29999 EndY=8 EndZ=0
    g1: LineSegment StartX=3.29999 StartY=8 StartZ=0 EndX=3.29999 EndY=-6.03275e-07 EndZ=0
    g2: ArcOfCircle CenterX=8.29999 CenterY=5 CenterZ=0 NormalX=0 NormalY=0 NormalZ=1 AngleXU=0 Radius=2 StartAngle=3.14159 EndAngle=4.71239
    g3: LineSegment StartX=6.29999 StartY=8 StartZ=0 EndX=6.29999 EndY=5 EndZ=0
    g4: ArcOfCircle CenterX=105 CenterY=19 CenterZ=0 NormalX=0 NormalY=0 NormalZ=1 AngleXU=0 Radius=12.7 StartAngle=4.71239 EndAngle=5.94289
    g5-g11: Circle x7 (B-spline internal-alignment scaffolding for g12; pole/knot coordinates omitted)
    g12: BSplineCurve PolesCount=7 KnotsCount=5 Degree=3 IsPeriodic=0
    g13-g17: GeomPoint x5 (B-spline internal-alignment scaffolding for g12; pole/knot coordinates omitted)
    g18: ArcOfCircle CenterX=105 CenterY=19 CenterZ=0 NormalX=0 NormalY=0 NormalZ=1 AngleXU=0 Radius=15.7 StartAngle=5.81226 EndAngle=6.28319
    g19: BSplineCurve PolesCount=5 KnotsCount=3 Degree=3 IsPeriodic=0
    g20: LineSegment StartX=8.29999 StartY=3 StartZ=0 EndX=101.7 EndY=3 EndZ=0
    g21: LineSegment StartX=3.29999 StartY=-6.03275e-07 StartZ=0 EndX=105 EndY=-6.03275e-07 EndZ=0
    g22: LineSegment StartX=120.974 StartY=8.71251 StartZ=0 EndX=122.332 EndY=7.83778 EndZ=0
    g23: LineSegment StartX=105 StartY=-6.03274e-07 StartZ=0 EndX=113 EndY=-6.03274e-07 EndZ=0
    g24: ArcOfCircle CenterX=105 CenterY=19 CenterZ=0 NormalX=0 NormalY=0 NormalZ=1 AngleXU=0 Radius=20.6155 StartAngle=5.11091 EndAngle=5.71103
    g25: ArcOfCircle CenterX=117.7 CenterY=19 CenterZ=0 NormalX=0 NormalY=0 NormalZ=1 AngleXU=0 Radius=3 StartAngle=1.2e-15 EndAngle=2.10468
    g26: Circle CenterX=116.345 CenterY=16.3232 CenterZ=0 NormalX=0 NormalY=0 NormalZ=1 AngleXU=0 Radius=1
    g27: Circle CenterX=117.24 CenterY=15.7584 CenterZ=0 NormalX=0 NormalY=0 NormalZ=1 AngleXU=0 Radius=1
    g28: Circle CenterX=116.972 CenterY=14.7612 CenterZ=0 NormalX=0 NormalY=0 NormalZ=1 AngleXU=0 Radius=1
    g29: BSplineCurve PolesCount=3 KnotsCount=2 Degree=2 IsPeriodic=0
    g30: GeomPoint X=116.345 Y=16.3232 Z=0
    g31: GeomPoint X=116.972 Y=14.7612 Z=0
    g32: Circle CenterX=115.828 CenterY=17.157 CenterZ=0 NormalX=0 NormalY=0 NormalZ=1 AngleXU=0 Radius=1
    g33: Circle CenterX=115.841 CenterY=16.639 CenterZ=0 NormalX=0 NormalY=0 NormalZ=1 AngleXU=0 Radius=1
    g34: Circle CenterX=116.345 CenterY=16.3232 CenterZ=0 NormalX=0 NormalY=0 NormalZ=1 AngleXU=0 Radius=1
    g35: BSplineCurve PolesCount=3 KnotsCount=2 Degree=2 IsPeriodic=0
    g36: GeomPoint X=115.828 Y=17.157 Z=0
    g37: GeomPoint X=116.345 Y=16.3232 Z=0
    g38: LineSegment StartX=115.828 StartY=17.157 StartZ=0 EndX=115.828 EndY=20.8307 EndZ=0
    g39: Circle CenterX=115.828 CenterY=20.8307 CenterZ=0 NormalX=0 NormalY=0 NormalZ=1 AngleXU=0 Radius=1
    g40: Circle CenterX=115.831 CenterY=21.3396 CenterZ=0 NormalX=0 NormalY=0 NormalZ=1 AngleXU=0 Radius=1
    g41: Circle CenterX=116.173 CenterY=21.5825 CenterZ=0 NormalX=0 NormalY=0 NormalZ=1 AngleXU=0 Radius=1
    g42: BSplineCurve PolesCount=3 KnotsCount=2 Degree=2 IsPeriodic=0
    g43: GeomPoint X=115.828 Y=20.8307 Z=0
    g44: GeomPoint X=116.173 Y=21.5825 Z=0
  constraints (70):
    c: Horizontal(g0)
    c: Distance(g0) = 3
    c: Coincident(g1,g0)
    c: Vertical(g1)
    c: Block(g2)
    c: Block(g0)
    c: Coincident(g3,g0)
    c: Coincident(g3,g2)
    c: Vertical(g3)
    c: Block(g1)
    c: Block(g4)
    c: Coincident(g19,g4)
    c: Block(g19)
    c: Equal(g5, g6-g11) x6
    c: InternalAlignment(g5-g11 -> g12) x7
    c: InternalAlignment(g13-g17 -> g12) x5
    c: Block(g12)
    c: Coincident(g18,g12)
    c: Block(g18)
    c: Coincident(g20,g2)
    c: Coincident(g20,g19)
    c: Horizontal(g20)
    c: Distance(g20) = 93.4
    c: Coincident(g21,g1)
    c: Horizontal(g21)
    c: Distance(g21) = 101.7
    c: Horizontal(g23)
    c: Distance(g23) = 8
    c: Coincident(g24,g23)
    c: Block(g23)
    c: Coincident(g22,g24)
    c: Block(g24)
    c: Block(g22)
    c: Distance(g22) = 1.61553
    c: Coincident(g25,g18)
    c: Block(g25)
    c: Weight(g26) = 1
    c: Equal(g26,g27)
    c: Equal(g26,g28)
    c: Coincident(g29,g4)
    c: InternalAlignment(g26,g29)
    c: InternalAlignment(g27,g29)
    c: InternalAlignment(g28,g29)
    c: InternalAlignment(g30,g29)
    c: InternalAlignment(g31,g29)
    c: Block(g29)
    c: Weight(g32) = 1
    c: Equal(g32,g33)
    c: Equal(g32,g34)
    c: Coincident(g35,g29)
    c: InternalAlignment(g32,g35)
    c: InternalAlignment(g33,g35)
    c: InternalAlignment(g34,g35)
    c: InternalAlignment(g36,g35)
    c: InternalAlignment(g37,g35)
    c: Block(g35)
    c: Coincident(g38,g35)
    c: Vertical(g38)
    c: Block(g38)
    c: Coincident(g42,g38)
    c: Weight(g39) = 1
    c: Equal(g39,g40)
    c: Equal(g39,g41)
    c: Coincident(g42,g25)
    c: InternalAlignment(g39,g42)
    c: InternalAlignment(g40,g42)
    c: InternalAlignment(g41,g42)
    c: InternalAlignment(g43,g42)
    c: InternalAlignment(g44,g42)
    c: Block(g42)
FEATURE [Part::Extrusion] Extrude064  label="bottom016"
  Base = -> Sketch073
  Dir = (0,0,1)
  DirMode = 2
  FaceMakerClass = Part::FaceMakerBullseye
  LengthFwd = 71.4
  LengthRev = 0
  Placement = pos=(0,0,0.3) rot=(0,0,1;0rad)
  Solid = true
  Symmetric = false
FEATURE [Part::Revolution] Revolve157  label="removeToCreateScrewAndThreadedInsertHole063"
  Angle = 360
  Axis = (0,1,0)
  Base = (0,0,0)
  FaceMakerClass = Part::FaceMakerBullseye
  Placement = pos=(12.5,0,10) rot=(0,0,1;0rad)
  Solid = false
  Source = -> Face141
  Symmetric = false
FEATURE [Sketcher::SketchObject] Sketch074
  FullyConstrained = true
  Placement = pos=(117,19,0) rot=(0.57735,0.57735,0.57735;2.0944rad)
  sketch-geometry (48):
    g0: LineSegment StartX=-49.19 StartY=69.25 StartZ=0 EndX=-49.19 EndY=66.25 EndZ=0
    g1: LineSegment StartX=-49.19 StartY=63.5 StartZ=0 EndX=-49.19 EndY=60.5 EndZ=0
    g2: LineSegment StartX=-49.19 StartY=57.75 StartZ=0 EndX=-49.19 EndY=54.75 EndZ=0
    g3: LineSegment StartX=-49.19 StartY=52 StartZ=0 EndX=-49.19 EndY=49 EndZ=0
    g4: LineSegment StartX=-49.19 StartY=46.25 StartZ=0 EndX=-49.19 EndY=43.25 EndZ=0
    g5: LineSegment StartX=-49.19 StartY=40.5 StartZ=0 EndX=-49.19 EndY=37.5 EndZ=0
    g6: LineSegment StartX=-49.19 StartY=34.5 StartZ=0 EndX=-49.19 EndY=31.5 EndZ=0
    g7: LineSegment StartX=-49.19 StartY=28.75 StartZ=0 EndX=-49.19 EndY=25.75 EndZ=0
    g8: LineSegment StartX=-49.19 StartY=23 StartZ=0 EndX=-49.19 EndY=20 EndZ=0
    g9: LineSegment StartX=-49.19 StartY=17.25 StartZ=0 EndX=-49.19 EndY=14.25 EndZ=0
    g10: LineSegment StartX=-49.19 StartY=11.5 StartZ=0 EndX=-49.19 EndY=8.5 EndZ=0
    g11: LineSegment StartX=-49.19 StartY=5.75 StartZ=0 EndX=-49.19 EndY=2.75 EndZ=0
    g12: ArcOfCircle CenterX=-1.5 CenterY=67.75 CenterZ=0 NormalX=0 NormalY=0 NormalZ=1 AngleXU=0 Radius=1.5 StartAngle=4.71239 EndAngle=7.85398
    g13: ArcOfCircle CenterX=-1.5 CenterY=62 CenterZ=0 NormalX=0 NormalY=0 NormalZ=1 AngleXU=0 Radius=1.5 StartAngle=4.71239 EndAngle=7.85398
    g14: ArcOfCircle CenterX=-1.5 CenterY=56.25 CenterZ=0 NormalX=0 NormalY=0 NormalZ=1 AngleXU=0 Radius=1.5 StartAngle=4.71239 EndAngle=7.85398
    g15: ArcOfCircle CenterX=-11.49 CenterY=50.5 CenterZ=0 NormalX=0 NormalY=0 NormalZ=1 AngleXU=0 Radius=1.5 StartAngle=4.71239 EndAngle=7.85398
    g16: ArcOfCircle CenterX=-16.28 CenterY=44.75 CenterZ=0 NormalX=0 NormalY=0 NormalZ=1 AngleXU=0 Radius=1.5 StartAngle=4.71239 EndAngle=7.85398
    g17: ArcOfCircle CenterX=-18.2337 CenterY=39 CenterZ=0 NormalX=0 NormalY=0 NormalZ=1 AngleXU=0 Radius=1.5 StartAngle=4.71485 EndAngle=7.85398
    g18: ArcOfCircle CenterX=-16.2837 CenterY=27.25 CenterZ=0 NormalX=0 NormalY=0 NormalZ=1 AngleXU=0 Radius=1.5 StartAngle=4.71485 EndAngle=7.85398
    g19: ArcOfCircle CenterX=-18.2337 CenterY=33 CenterZ=0 NormalX=0 NormalY=0 NormalZ=1 AngleXU=0 Radius=1.5 StartAngle=4.71485 EndAngle=7.85398
    g20: ArcOfCircle CenterX=-11.49 CenterY=21.5 CenterZ=0 NormalX=0 NormalY=0 NormalZ=1 AngleXU=0 Radius=1.5 StartAngle=4.71239 EndAngle=7.85398
    g21: ArcOfCircle CenterX=-1.5 CenterY=4.25 CenterZ=0 NormalX=0 NormalY=0 NormalZ=1 AngleXU=0 Radius=1.5 StartAngle=4.71239 EndAngle=7.85398
    g22: ArcOfCircle CenterX=-1.5 CenterY=10 CenterZ=0 NormalX=0 NormalY=0 NormalZ=1 AngleXU=0 Radius=1.5 StartAngle=4.71239 EndAngle=7.85398
    g23: ArcOfCircle CenterX=-1.5 CenterY=15.75 CenterZ=0 NormalX=0 NormalY=0 NormalZ=1 AngleXU=0 Radius=1.5 StartAngle=4.71239 EndAngle=7.85398
    g24: LineSegment StartX=-49.19 StartY=69.25 StartZ=0 EndX=-1.5 EndY=69.25 EndZ=0
    g25: LineSegment StartX=-49.19 StartY=66.25 StartZ=0 EndX=-1.5 EndY=66.25 EndZ=0
    g26: LineSegment StartX=-49.19 StartY=63.5 StartZ=0 EndX=-1.5 EndY=63.5 EndZ=0
    g27: LineSegment StartX=-49.19 StartY=60.5 StartZ=0 EndX=-1.5 EndY=60.5 EndZ=0
    g28: LineSegment StartX=-49.19 StartY=57.75 StartZ=0 EndX=-1.5 EndY=57.75 EndZ=0
    g29: LineSegment StartX=-49.19 StartY=54.75 StartZ=0 EndX=-1.5 EndY=54.75 EndZ=0
    g30: LineSegment StartX=-49.19 StartY=52 StartZ=0 EndX=-11.49 EndY=52 EndZ=0
    g31: LineSegment StartX=-49.19 StartY=49 StartZ=0 EndX=-11.49 EndY=49 EndZ=0
    g32: LineSegment StartX=-49.19 StartY=46.25 StartZ=0 EndX=-16.28 EndY=46.25 EndZ=0
    g33: LineSegment StartX=-49.19 StartY=43.25 StartZ=0 EndX=-16.28 EndY=43.25 EndZ=0
    g34: LineSegment StartX=-49.19 StartY=40.5 StartZ=0 EndX=-18.2337 EndY=40.5 EndZ=0
    g35: LineSegment StartX=-49.19 StartY=37.5 StartZ=0 EndX=-18.23 EndY=37.5 EndZ=0
    g36: LineSegment StartX=-49.19 StartY=34.5 StartZ=0 EndX=-18.2337 EndY=34.5 EndZ=0
    g37: LineSegment StartX=-49.19 StartY=31.5 StartZ=0 EndX=-18.23 EndY=31.5 EndZ=0
    g38: LineSegment StartX=-49.19 StartY=28.75 StartZ=0 EndX=-16.2837 EndY=28.75 EndZ=0
    g39: LineSegment StartX=-49.19 StartY=25.75 StartZ=0 EndX=-16.28 EndY=25.75 EndZ=0
    g40: LineSegment StartX=-49.19 StartY=23 StartZ=0 EndX=-11.49 EndY=23 EndZ=0
    g41: LineSegment StartX=-49.19 StartY=20 StartZ=0 EndX=-11.49 EndY=20 EndZ=0
    g42: LineSegment StartX=-49.19 StartY=17.25 StartZ=0 EndX=-1.5 EndY=17.25 EndZ=0
    g43: LineSegment StartX=-49.19 StartY=14.25 StartZ=0 EndX=-1.5 EndY=14.25 EndZ=0
    g44: LineSegment StartX=-49.19 StartY=11.5 StartZ=0 EndX=-1.5 EndY=11.5 EndZ=0
    g45: LineSegment StartX=-49.19 StartY=8.5 StartZ=0 EndX=-1.5 EndY=8.5 EndZ=0
    g46: LineSegment StartX=-49.19 StartY=5.75 StartZ=0 EndX=-1.5 EndY=5.75 EndZ=0
    g47: LineSegment StartX=-49.19 StartY=2.75 StartZ=0 EndX=-1.5 EndY=2.75 EndZ=0
  constraints (120):
    c: Vertical(g0)
    c: Distance(g0) = 3
    c: Block(g0)
    c: Vertical(g1)
    c: Distance(g1) = 3
    c: Vertical(g2)
    c: Equal(g0,g2) = 3
    c: Block(g2)
    c: Vertical(g3)
    c: Equal(g1,g3) = 3
    c: Vertical(g4)
    c: Equal(g0,g4) = 3
    c: Block(g4)
    c: Vertical(g5)
    c: Equal(g1,g5) = 3
    c: Vertical(g6)
    c: Equal(g0,g6) = 3
    c: Block(g6)
    c: Vertical(g7)
    c: Equal(g1,g7) = 3
    c: Vertical(g8)
    c: Equal(g0,g8) = 3
    c: Block(g8)
    c: Vertical(g9)
    c: Equal(g1,g9) = 3
    c: Vertical(g10)
    c: Equal(g0,g10) = 3
    c: Block(g10)
    c: Vertical(g11)
    c: Equal(g1,g11) = 3
    c: Block(g12)
    c: Block(g13)
    c: Block(g14)
    c: Block(g15)
    c: Block(g16)
    c: Block(g17)
    c: Block(g18)
    c: Block(g19)
    c: Block(g20)
    c: Block(g21)
    c: Block(g22)
    c: Block(g23)
    c: Block(g11)
    c: Block(g9)
    c: Block(g7)
    c: Block(g5)
    c: Block(g3)
    c: Block(g1)
    c: Coincident(g24,g0)
    c: Coincident(g24,g12)
    c: Horizontal(g24)
    c: Coincident(g25,g0)
    c: Coincident(g25,g12)
    c: Horizontal(g25)
    c: Coincident(g26,g1)
    c: Coincident(g26,g13)
    c: Horizontal(g26)
    c: Coincident(g27,g1)
    c: Coincident(g27,g13)
    c: Horizontal(g27)
    c: Coincident(g28,g2)
    c: Coincident(g28,g14)
    c: Horizontal(g28)
    c: Coincident(g29,g2)
    c: Coincident(g29,g14)
    c: Horizontal(g29)
    c: Coincident(g30,g3)
    c: Coincident(g30,g15)
    c: Horizontal(g30)
    c: Coincident(g31,g3)
    c: Coincident(g31,g15)
    c: Horizontal(g31)
    c: Coincident(g32,g4)
    c: Coincident(g32,g16)
    c: Horizontal(g32)
    c: Coincident(g33,g4)
    c: Coincident(g33,g16)
    c: Horizontal(g33)
    c: Coincident(g34,g5)
    c: Coincident(g34,g17)
    c: Horizontal(g34)
    c: Coincident(g35,g5)
    c: Coincident(g35,g17)
    c: Horizontal(g35)
    c: Coincident(g36,g6)
    c: Coincident(g36,g19)
    c: Horizontal(g36)
    c: Coincident(g37,g6)
    c: Coincident(g37,g19)
    c: Horizontal(g37)
    c: Coincident(g38,g7)
    c: Coincident(g38,g18)
    c: Horizontal(g38)
    c: Coincident(g39,g7)
    c: Coincident(g39,g18)
    c: Horizontal(g39)
    c: Coincident(g40,g8)
    c: Coincident(g40,g20)
    c: Horizontal(g40)
    c: Coincident(g41,g8)
    c: Coincident(g41,g20)
    c: Horizontal(g41)
    c: Coincident(g42,g9)
    c: Coincident(g42,g23)
    c: Horizontal(g42)
    c: Coincident(g43,g9)
    c: Coincident(g43,g23)
    c: Horizontal(g43)
    c: Coincident(g44,g10)
    c: Coincident(g44,g22)
    c: Horizontal(g44)
    c: Coincident(g45,g10)
    c: Coincident(g45,g22)
    c: Horizontal(g45)
    c: Coincident(g46,g11)
    c: Coincident(g46,g21)
    c: Horizontal(g46)
    c: Coincident(g47,g11)
    c: Coincident(g47,g21)
    c: Horizontal(g47)
FEATURE [Part::Extrusion] Extrude065
  Base = -> Sketch074
  Dir = (1,0,0)
  DirMode = 2
  FaceMakerClass = Part::FaceMakerBullseye
  LengthFwd = 23
  LengthRev = 0
  Placement = pos=(-19,0,0) rot=(0,0,1;0rad)
  Solid = true
  Symmetric = false
FEATURE [Part::Fillet] Fillet056  label="removeToCreateVentalationHoles003"
  Base = -> Extrude065
  Edges = <same value as first occurrence — deduplicated (x6 in doc)>
  Placement = pos=(7,0.02,0) rot=(0,0,1;0rad)
FEATURE [Part::Revolution] Revolve158  label="removeToCreateScrewAndThreadedInsertHole065"
  Angle = 360
  Axis = (0,1,0)
  Base = (0,0,0)
  FaceMakerClass = Part::FaceMakerBullseye
  Placement = pos=(12.5,0,62) rot=(0,0,1;0rad)
  Solid = false
  Source = -> Face146
  Symmetric = false
FEATURE [Part::Revolution] Revolve159  label="removeToCreateScrewAndThreadedInsertHole066"
  Angle = 360
  Axis = (0,1,0)
  Base = (0,0,0)
  FaceMakerClass = Part::FaceMakerBullseye
  Placement = pos=(89.5,0,68.5) rot=(0,0,1;0rad)
  Solid = false
  Source = -> Face143
  Symmetric = false
FEATURE [Part::Revolution] Revolve160  label="removeToCreateScrewAndThreadedInsertHole067"
  Angle = 360
  Axis = (0,1,0)
  Base = (0,0,0)
  FaceMakerClass = Part::FaceMakerBullseye
  Placement = pos=(89.5,0,3.5) rot=(0,0,1;0rad)
  Solid = false
  Source = -> Face142
  Symmetric = false
FEATURE [Part::Revolution] Revolve161  label="removeToCreateScrewAndThreadedInsertHole068"
  Angle = 360
  Axis = (0,1,0)
  Base = (0,0,0)
  FaceMakerClass = Part::FaceMakerBullseye
  Placement = pos=(109.5,4.7,3.5) rot=(0,0,1;0rad)
  Solid = false
  Source = -> Face145
  Symmetric = false
FEATURE [Part::Revolution] Revolve162  label="removeToCreateScrewAndThreadedInsertHole069"
  Angle = 360
  Axis = (0,1,0)
  Base = (0,0,0)
  FaceMakerClass = Part::FaceMakerBullseye
  Placement = pos=(109.5,4.7,68.5) rot=(0,0,1;0rad)
  Solid = false
  Source = -> Face144
  Symmetric = false
FEATURE [Part::MultiFuse] Fusion141  label="removeToCreateScrewAndThreadedInsertHole064"
  Shapes = -> [Revolve162,Revolve161,Revolve160,Revolve159,Revolve158,Revolve157]
FEATURE [Part::Cylinder] Cylinder062
  Angle = 360
  AttacherType = Attacher::AttachEngine3D
  Height = 20
  Placement = pos=(0,0,36.15) rot=(0,0,1;0rad)
  Radius = 14
FEATURE [Part::Cylinder] Cylinder063
  Angle = 360
  AttacherType = Attacher::AttachEngine3D
  Height = 10
  Placement = pos=(0,0,36.15) rot=(0,0,1;0rad)
  Radius = 4
FEATURE [Part::MultiFuse] Fusion139  label="removeToCreteHoleForPlugHousing052"
  Placement = pos=(70,19,36) rot=(0,1,0;1.5708rad)
  Shapes = -> [Cylinder062,Cylinder063]
FEATURE [Part::Cut] Cut060  label="bottom017"
  Base = -> Extrude064
  Tool = -> Fusion139
FEATURE [Part::Cut] Cut061  label="bottom019"
  Base = -> Cut060
  Tool = -> Fusion141
FEATURE [Part::MultiFuse] Fusion140  label="bottom018"
  Shapes = -> [Cut061,Cut058]
FEATURE [Part::Cut] Cut059  label="bottom020"
  Base = -> Fusion140
  Tool = -> Fillet056
FEATURE [Part::Box] Box036  label="Cube021"
  AttacherType = Attacher::AttachEngine3D
  Height = 80
  Length = 26
  Placement = pos=(0,-1,-5) rot=(0,0,1;0rad)
  Width = 11
FEATURE [Part::Cut] Cut062  label="removeFromBottom002"
  Base = -> Cut057
  Tool = -> Box036
FEATURE [Part::Cut] Cut063
  Base = -> Cut059
  Tool = -> Cut062
FEATURE [Part::Cut] Cut064  label="pcbStands"
  Base = -> Fusion095
  Tool = -> Fusion127
FEATURE [Sketcher::SketchObject] Sketch075  label="topSketch022"
  FullyConstrained = true
  sketch-geometry (6):
    g0: LineSegment StartX=19 StartY=38 StartZ=0 EndX=117 EndY=38 EndZ=0
    g1: ArcOfCircle CenterX=19 CenterY=19 CenterZ=0 NormalX=0 NormalY=0 NormalZ=1 AngleXU=0 Radius=19 StartAngle=1.5708 EndAngle=3.14159
    g2: LineSegment StartX=117 StartY=38 StartZ=0 EndX=117 EndY=19 EndZ=0
    g3: LineSegment StartX=98 StartY=1.0161e-12 StartZ=0 EndX=5.22862e-06 EndY=1.0161e-12 EndZ=0
    g4: LineSegment StartX=5.22862e-06 StartY=19 StartZ=0 EndX=5.22862e-06 EndY=1.0161e-12 EndZ=0
    g5: ArcOfCircle CenterX=98 CenterY=19 CenterZ=0 NormalX=0 NormalY=0 NormalZ=1 AngleXU=0 Radius=19 StartAngle=4.71239 EndAngle=6.28319
  constraints (16):
    c: Horizontal(g0)
    c: Distance(g0) = 98
    c: Coincident(g1,g0)
    c: Block(g1)
    c: Coincident(g2,g0)
    c: Vertical(g2)
    c: Distance(g2) = 19
    c: Horizontal(g3)
    c: Coincident(g4,g1)
    c: Vertical(g4)
    c: Coincident(g3,g4)
    c: Block(g3)
    c: Coincident(g5,g2)
    c: Coincident(g5,g3)
    c: Block(g0)
    c: Block(g5)
FEATURE [Part::Extrusion] Extrude067  label="sideB003"
  Base = -> Sketch075
  Dir = (0,0,1)
  DirMode = 2
  FaceMakerClass = Part::FaceMakerBullseye
  LengthFwd = 3
  LengthRev = 0
  Placement = pos=(0,0,71.7) rot=(0,0,1;0rad)
  Solid = true
  Symmetric = false
FEATURE [Sketcher::SketchObject] Sketch076  label="topSketch023"
  FullyConstrained = true
  sketch-geometry (6):
    g0: LineSegment StartX=19 StartY=38 StartZ=0 EndX=117 EndY=38 EndZ=0
    g1: ArcOfCircle CenterX=19 CenterY=19 CenterZ=0 NormalX=0 NormalY=0 NormalZ=1 AngleXU=0 Radius=19 StartAngle=1.5708 EndAngle=3.14159
    g2: LineSegment StartX=117 StartY=38 StartZ=0 EndX=117 EndY=19 EndZ=0
    g3: LineSegment StartX=98 StartY=1.0161e-12 StartZ=0 EndX=5.22862e-06 EndY=1.0161e-12 EndZ=0
    g4: LineSegment StartX=5.22862e-06 StartY=19 StartZ=0 EndX=5.22862e-06 EndY=1.0161e-12 EndZ=0
    g5: ArcOfCircle CenterX=98 CenterY=19 CenterZ=0 NormalX=0 NormalY=0 NormalZ=1 AngleXU=0 Radius=19 StartAngle=4.71239 EndAngle=6.28319
  constraints (16):
    c: Horizontal(g0)
    c: Distance(g0) = 98
    c: Coincident(g1,g0)
    c: Block(g1)
    c: Coincident(g2,g0)
    c: Vertical(g2)
    c: Distance(g2) = 19
    c: Horizontal(g3)
    c: Coincident(g4,g1)
    c: Vertical(g4)
    c: Coincident(g3,g4)
    c: Block(g3)
    c: Coincident(g5,g2)
    c: Coincident(g5,g3)
    c: Block(g0)
    c: Block(g5)
FEATURE [Part::Extrusion] Extrude066  label="sideA003"
  Base = -> Sketch076
  Dir = (0,0,1)
  DirMode = 2
  FaceMakerClass = Part::FaceMakerBullseye
  LengthFwd = 3
  LengthRev = 0
  Placement = pos=(0,0,-2.7) rot=(0,0,1;0rad)
  Solid = true
  Symmetric = false
FEATURE [Part::MultiFuse] Fusion142  label="removeFromBottom003"
  Placement = pos=(2,0,0) rot=(0,0,1;0rad)
  Shapes = -> [Extrude066,Extrude067]
FEATURE [Part::Cut] Cut065  label="screwRetainers002"
  Base = -> Fusion096
  Tool = -> Fusion142
FEATURE [Sketcher::SketchObject] Sketch077
  FullyConstrained = true
  Placement = pos=(117,19,0) rot=(0.57735,0.57735,0.57735;2.0944rad)
  sketch-geometry (8):
    g0: LineSegment StartX=-49.19 StartY=63.5 StartZ=0 EndX=-49.19 EndY=60.5 EndZ=0
    g1: LineSegment StartX=-49.19 StartY=11.5 StartZ=0 EndX=-49.19 EndY=8.5 EndZ=0
    g2: ArcOfCircle CenterX=-1.5 CenterY=62 CenterZ=0 NormalX=0 NormalY=0 NormalZ=1 AngleXU=0 Radius=1.5 StartAngle=4.71239 EndAngle=7.85398
    g3: ArcOfCircle CenterX=-1.5 CenterY=10 CenterZ=0 NormalX=0 NormalY=0 NormalZ=1 AngleXU=0 Radius=1.5 StartAngle=4.71239 EndAngle=7.85398
    g4: LineSegment StartX=-49.19 StartY=63.5 StartZ=0 EndX=-1.5 EndY=63.5 EndZ=0
    g5: LineSegment StartX=-49.19 StartY=60.5 StartZ=0 EndX=-1.5 EndY=60.5 EndZ=0
    g6: LineSegment StartX=-49.19 StartY=11.5 StartZ=0 EndX=-1.5 EndY=11.5 EndZ=0
    g7: LineSegment StartX=-49.19 StartY=8.5 StartZ=0 EndX=-1.5 EndY=8.5 EndZ=0
  constraints (19):
    c: Vertical(g0)
    c: Distance(g0) = 3
    c: Vertical(g1)
    c: Block(g1)
    c: Block(g2)
    c: Block(g3)
    c: Block(g0)
    c: Coincident(g4,g0)
    c: Coincident(g4,g2)
    c: Horizontal(g4)
    c: Coincident(g5,g0)
    c: Coincident(g5,g2)
    c: Horizontal(g5)
    c: Coincident(g6,g1)
    c: Coincident(g6,g3)
    c: Horizontal(g6)
    c: Coincident(g7,g1)
    c: Coincident(g7,g3)
    c: Horizontal(g7)
FEATURE [Part::Extrusion] Extrude068
  Base = -> Sketch077
  Dir = (1,0,0)
  DirMode = 2
  FaceMakerClass = Part::FaceMakerBullseye
  LengthFwd = 10
  LengthRev = 0
  Solid = true
  Symmetric = false
FEATURE [Part::Fillet] Fillet057  label="removeFromtMoreFrontCaseScrewRetainers002"
  Base = -> Extrude068
  Edges = 4 edges r=1.49: [Edge6,Edge11,Edge18,Edge23]
  Placement = pos=(-12,0,0) rot=(0,0,1;0rad)
FEATURE [Sketcher::SketchObject] Sketch078
  FullyConstrained = true
  Placement = pos=(117,19,0) rot=(0.57735,0.57735,0.57735;2.0944rad)
  sketch-geometry (8):
    g0: LineSegment StartX=-49.19 StartY=69.25 StartZ=0 EndX=-49.19 EndY=66.25 EndZ=0
    g1: LineSegment StartX=-49.19 StartY=5.75 StartZ=0 EndX=-49.19 EndY=2.75 EndZ=0
    g2: ArcOfCircle CenterX=-1.5 CenterY=67.75 CenterZ=0 NormalX=0 NormalY=0 NormalZ=1 AngleXU=0 Radius=1.5 StartAngle=4.71239 EndAngle=7.85398
    g3: ArcOfCircle CenterX=-1.5 CenterY=4.25 CenterZ=0 NormalX=0 NormalY=0 NormalZ=1 AngleXU=0 Radius=1.5 StartAngle=4.71239 EndAngle=7.85398
    g4: LineSegment StartX=-49.19 StartY=69.25 StartZ=0 EndX=-1.5 EndY=69.25 EndZ=0
    g5: LineSegment StartX=-49.19 StartY=66.25 StartZ=0 EndX=-1.5 EndY=66.25 EndZ=0
    g6: LineSegment StartX=-49.19 StartY=5.75 StartZ=0 EndX=-1.5 EndY=5.75 EndZ=0
    g7: LineSegment StartX=-49.19 StartY=2.75 StartZ=0 EndX=-1.5 EndY=2.75 EndZ=0
  constraints (19):
    c: Vertical(g0)
    c: Distance(g0) = 3
    c: Block(g0)
    c: Vertical(g1)
    c: Block(g2)
    c: Block(g3)
    c: Block(g1)
    c: Coincident(g4,g0)
    c: Coincident(g4,g2)
    c: Horizontal(g4)
    c: Coincident(g5,g0)
    c: Coincident(g5,g2)
    c: Horizontal(g5)
    c: Coincident(g6,g1)
    c: Coincident(g6,g3)
    c: Horizontal(g6)
    c: Coincident(g7,g1)
    c: Coincident(g7,g3)
    c: Horizontal(g7)
FEATURE [Part::Extrusion] Extrude069
  Base = -> Sketch078
  Dir = (1,0,0)
  DirMode = 2
  FaceMakerClass = Part::FaceMakerBullseye
  LengthFwd = 10
  LengthRev = 0
  Solid = true
  Symmetric = false
FEATURE [Part::Fillet] Fillet058  label="removeFromtMoreFrontCaseScrewRetainers003"
  Base = -> Extrude069
  Edges = 4 edges r=1.49: [Edge6,Edge11,Edge18,Edge23]
  Placement = pos=(-4,0,0) rot=(0,0,1;0rad)
FEATURE [Part::Cut] Cut066
  Base = -> Cut065
  Tool = -> Fillet058
FEATURE [Part::Cut] Cut067  label="screwPillars"
  Base = -> Cut066
  Tool = -> Fillet057
FEATURE [Part::MultiFuse] Fusion143  label="bottom021"
  Shapes = -> [Cut031,Cut063]
FEATURE [Part::Cylinder] Cylinder
  Angle = 360
  AttacherType = Attacher::AttachEngine3D
  Height = 10
  Placement = pos=(20.65,12,4.68) rot=(1,0,0;1.5708rad)
  Radius = 2
FEATURE [Part::Cylinder] Cylinder064
  Angle = 360
  AttacherType = Attacher::AttachEngine3D
  Height = 10
  Placement = pos=(20.65,12,67.38) rot=(1,0,0;1.5708rad)
  Radius = 2
FEATURE [Part::Cylinder] Cylinder065
  Angle = 360
  AttacherType = Attacher::AttachEngine3D
  Height = 10
  Placement = pos=(77.15,12,67.38) rot=(1,0,0;1.5708rad)
  Radius = 2
FEATURE [Part::Cylinder] Cylinder066
  Angle = 360
  AttacherType = Attacher::AttachEngine3D
  Height = 10
  Placement = pos=(77.15,12,4.68) rot=(1,0,0;1.5708rad)
  Radius = 2
FEATURE [Part::MultiFuse] Fusion144  label="removeFromThreadedInsertHousing"
  Shapes = -> [Cylinder065,Cylinder064,Cylinder,Cylinder066]
FEATURE [Part::Cut] Cut068  label="pcbStands001"
  Base = -> Cut064
  Tool = -> Fusion144
FEATURE [Part::MultiFuse] Fusion145
  Shapes = -> [Cut068,Fusion143]
FEATURE [Part::MultiFuse] Fusion146
  Shapes = -> [Fusion145]
FEATURE [Part::MultiFuse] Fusion147  label="bottom022"
  Shapes = -> [Cut067,Fusion146]
FEATURE [Part::MultiFuse] Fusion148  label="casePillars005"
  Shapes = -> [Cut047,Fusion092]
FEATURE [Part::MultiFuse] Fusion149  label="bottom023"
  Shapes = -> [Fusion124,Fusion113,Fusion147]
FEATURE [Part::MultiFuse] Fusion150  label="topBits"
  Shapes = -> [Cut025,Fusion148,Cut030,Fillet034]
FEATURE [Part::Feature] Face149 .. Face152  x4 (patterned run collapsed; names and placements below)
  shape: bbox 3.2 x 1.5 x 2e-07 mm, 1 faces, 0 solids (baked)
FEATURE [Part::Feature] Face153
  shape: bbox 3.6 x 3.2 x 2e-07 mm, 1 faces, 0 solids (baked)
FEATURE [Part::Feature] Face154
  shape: bbox 3.6 x 3.2 x 2e-07 mm, 1 faces, 0 solids (baked)
FEATURE [Sketcher::SketchObject] Sketch079  label="topSketch024"
  FullyConstrained = true
  sketch-geometry (6):
    g0: LineSegment StartX=19 StartY=38 StartZ=0 EndX=117 EndY=38 EndZ=0
    g1: ArcOfCircle CenterX=19 CenterY=19 CenterZ=0 NormalX=0 NormalY=0 NormalZ=1 AngleXU=0 Radius=19 StartAngle=1.5708 EndAngle=3.14159
    g2: LineSegment StartX=117 StartY=38 StartZ=0 EndX=117 EndY=19 EndZ=0
    g3: LineSegment StartX=98 StartY=1.0161e-12 StartZ=0 EndX=5.22862e-06 EndY=1.0161e-12 EndZ=0
    g4: LineSegment StartX=5.22862e-06 StartY=19 StartZ=0 EndX=5.22862e-06 EndY=1.0161e-12 EndZ=0
    g5: ArcOfCircle CenterX=98 CenterY=19 CenterZ=0 NormalX=0 NormalY=0 NormalZ=1 AngleXU=0 Radius=19 StartAngle=4.71239 EndAngle=6.28319
  constraints (16):
    c: Horizontal(g0)
    c: Distance(g0) = 98
    c: Coincident(g1,g0)
    c: Block(g1)
    c: Coincident(g2,g0)
    c: Vertical(g2)
    c: Distance(g2) = 19
    c: Horizontal(g3)
    c: Coincident(g4,g1)
    c: Vertical(g4)
    c: Coincident(g3,g4)
    c: Block(g3)
    c: Coincident(g5,g2)
    c: Coincident(g5,g3)
    c: Block(g0)
    c: Block(g5)
FEATURE [Sketcher::SketchObject] Sketch080  label="topSketch025"
  FullyConstrained = true
  sketch-geometry (6):
    g0: LineSegment StartX=19 StartY=38 StartZ=0 EndX=117 EndY=38 EndZ=0
    g1: ArcOfCircle CenterX=19 CenterY=19 CenterZ=0 NormalX=0 NormalY=0 NormalZ=1 AngleXU=0 Radius=19 StartAngle=1.5708 EndAngle=3.14159
    g2: LineSegment StartX=117 StartY=38 StartZ=0 EndX=117 EndY=19 EndZ=0
    g3: LineSegment StartX=98 StartY=1.0161e-12 StartZ=0 EndX=5.22862e-06 EndY=1.0161e-12 EndZ=0
    g4: LineSegment StartX=5.22862e-06 StartY=19 StartZ=0 EndX=5.22862e-06 EndY=1.0161e-12 EndZ=0
    g5: ArcOfCircle CenterX=98 CenterY=19 CenterZ=0 NormalX=0 NormalY=0 NormalZ=1 AngleXU=0 Radius=19 StartAngle=4.71239 EndAngle=6.28319
  constraints (16):
    c: Horizontal(g0)
    c: Distance(g0) = 98
    c: Coincident(g1,g0)
    c: Block(g1)
    c: Coincident(g2,g0)
    c: Vertical(g2)
    c: Distance(g2) = 19
    c: Horizontal(g3)
    c: Coincident(g4,g1)
    c: Vertical(g4)
    c: Coincident(g3,g4)
    c: Block(g3)
    c: Coincident(g5,g2)
    c: Coincident(g5,g3)
    c: Block(g0)
    c: Block(g5)
FEATURE [Part::Extrusion] Extrude070  label="sideA004"
  Base = -> Sketch080
  Dir = (0,0,1)
  DirMode = 2
  FaceMakerClass = Part::FaceMakerBullseye
  LengthFwd = 3
  LengthRev = 0
  Placement = pos=(0,0,-2.7) rot=(0,0,1;0rad)
  Solid = true
  Symmetric = false
FEATURE [Sketcher::SketchObject] Sketch081
  FullyConstrained = true
  Placement = pos=(117,19,0) rot=(0.57735,0.57735,0.57735;2.0944rad)
  sketch-geometry (8):
    g0: LineSegment StartX=-49.19 StartY=63.5 StartZ=0 EndX=-49.19 EndY=60.5 EndZ=0
    g1: LineSegment StartX=-49.19 StartY=11.5 StartZ=0 EndX=-49.19 EndY=8.5 EndZ=0
    g2: ArcOfCircle CenterX=-1.5 CenterY=62 CenterZ=0 NormalX=0 NormalY=0 NormalZ=1 AngleXU=0 Radius=1.5 StartAngle=4.71239 EndAngle=7.85398
    g3: ArcOfCircle CenterX=-1.5 CenterY=10 CenterZ=0 NormalX=0 NormalY=0 NormalZ=1 AngleXU=0 Radius=1.5 StartAngle=4.71239 EndAngle=7.85398
    g4: LineSegment StartX=-49.19 StartY=63.5 StartZ=0 EndX=-1.5 EndY=63.5 EndZ=0
    g5: LineSegment StartX=-49.19 StartY=60.5 StartZ=0 EndX=-1.5 EndY=60.5 EndZ=0
    g6: LineSegment StartX=-49.19 StartY=11.5 StartZ=0 EndX=-1.5 EndY=11.5 EndZ=0
    g7: LineSegment StartX=-49.19 StartY=8.5 StartZ=0 EndX=-1.5 EndY=8.5 EndZ=0
  constraints (19):
    c: Vertical(g0)
    c: Distance(g0) = 3
    c: Vertical(g1)
    c: Block(g1)
    c: Block(g2)
    c: Block(g3)
    c: Block(g0)
    c: Coincident(g4,g0)
    c: Coincident(g4,g2)
    c: Horizontal(g4)
    c: Coincident(g5,g0)
    c: Coincident(g5,g2)
    c: Horizontal(g5)
    c: Coincident(g6,g1)
    c: Coincident(g6,g3)
    c: Horizontal(g6)
    c: Coincident(g7,g1)
    c: Coincident(g7,g3)
    c: Horizontal(g7)
FEATURE [Part::Extrusion] Extrude071  label="sideB004"
  Base = -> Sketch079
  Dir = (0,0,1)
  DirMode = 2
  FaceMakerClass = Part::FaceMakerBullseye
  LengthFwd = 3
  LengthRev = 0
  Placement = pos=(0,0,71.7) rot=(0,0,1;0rad)
  Solid = true
  Symmetric = false
FEATURE [Part::MultiFuse] Fusion152  label="removeFromBottom004"
  Placement = pos=(2,0,0) rot=(0,0,1;0rad)
  Shapes = -> [Extrude070,Extrude071]
FEATURE [Part::Extrusion] Extrude072
  Base = -> Sketch081
  Dir = (1,0,0)
  DirMode = 2
  FaceMakerClass = Part::FaceMakerBullseye
  LengthFwd = 10
  LengthRev = 0
  Solid = true
  Symmetric = false
FEATURE [Part::Fillet] Fillet059  label="removeFromtMoreFrontCaseScrewRetainers004"
  Base = -> Extrude072
  Edges = 4 edges r=1.49: [Edge6,Edge11,Edge18,Edge23]
  Placement = pos=(-12,0,0) rot=(0,0,1;0rad)
FEATURE [Sketcher::SketchObject] Sketch082
  FullyConstrained = true
  Placement = pos=(117,19,0) rot=(0.57735,0.57735,0.57735;2.0944rad)
  sketch-geometry (8):
    g0: LineSegment StartX=-49.19 StartY=69.25 StartZ=0 EndX=-49.19 EndY=66.25 EndZ=0
    g1: LineSegment StartX=-49.19 StartY=5.75 StartZ=0 EndX=-49.19 EndY=2.75 EndZ=0
    g2: ArcOfCircle CenterX=-1.5 CenterY=67.75 CenterZ=0 NormalX=0 NormalY=0 NormalZ=1 AngleXU=0 Radius=1.5 StartAngle=4.71239 EndAngle=7.85398
    g3: ArcOfCircle CenterX=-1.5 CenterY=4.25 CenterZ=0 NormalX=0 NormalY=0 NormalZ=1 AngleXU=0 Radius=1.5 StartAngle=4.71239 EndAngle=7.85398
    g4: LineSegment StartX=-49.19 StartY=69.25 StartZ=0 EndX=-1.5 EndY=69.25 EndZ=0
    g5: LineSegment StartX=-49.19 StartY=66.25 StartZ=0 EndX=-1.5 EndY=66.25 EndZ=0
    g6: LineSegment StartX=-49.19 StartY=5.75 StartZ=0 EndX=-1.5 EndY=5.75 EndZ=0
    g7: LineSegment StartX=-49.19 StartY=2.75 StartZ=0 EndX=-1.5 EndY=2.75 EndZ=0
  constraints (19):
    c: Vertical(g0)
    c: Distance(g0) = 3
    c: Block(g0)
    c: Vertical(g1)
    c: Block(g2)
    c: Block(g3)
    c: Block(g1)
    c: Coincident(g4,g0)
    c: Coincident(g4,g2)
    c: Horizontal(g4)
    c: Coincident(g5,g0)
    c: Coincident(g5,g2)
    c: Horizontal(g5)
    c: Coincident(g6,g1)
    c: Coincident(g6,g3)
    c: Horizontal(g6)
    c: Coincident(g7,g1)
    c: Coincident(g7,g3)
    c: Horizontal(g7)
FEATURE [Part::Extrusion] Extrude073
  Base = -> Sketch082
  Dir = (1,0,0)
  DirMode = 2
  FaceMakerClass = Part::FaceMakerBullseye
  LengthFwd = 10
  LengthRev = 0
  Solid = true
  Symmetric = false
FEATURE [Part::Fillet] Fillet060  label="removeFromtMoreFrontCaseScrewRetainers005"
  Base = -> Extrude073
  Edges = 4 edges r=1.49: [Edge6,Edge11,Edge18,Edge23]
  Placement = pos=(-4,0,0) rot=(0,0,1;0rad)
FEATURE [Part::Revolution] Revolve163  label="backCaseScrewRetainer004"
  Angle = 360
  Axis = (0,1,0)
  Base = (0,0,0)
  FaceMakerClass = Part::FaceMakerBullseye
  Placement = pos=(12.5,3,62) rot=(0,0,1;0rad)
  Solid = false
  Source = -> Face149
  Symmetric = false
FEATURE [Part::Revolution] Revolve164  label="frontCaseScrewRetainer006"
  Angle = 360
  Axis = (0,1,0)
  Base = (0,0,0)
  FaceMakerClass = Part::FaceMakerBullseye
  Placement = pos=(89.5,3,68.5) rot=(0,0,1;0rad)
  Solid = false
  Source = -> Face151
  Symmetric = false
FEATURE [Part::Revolution] Revolve165  label="frontCaseScrewRetainer007"
  Angle = 360
  Axis = (0,1,0)
  Base = (0,0,0)
  FaceMakerClass = Part::FaceMakerBullseye
  Placement = pos=(89.5,3,3.5) rot=(0,0,1;0rad)
  Solid = false
  Source = -> Face152
  Symmetric = false
FEATURE [Part::Revolution] Revolve166  label="backCaseScrewRetainer005"
  Angle = 360
  Axis = (0,1,0)
  Base = (0,0,0)
  FaceMakerClass = Part::FaceMakerBullseye
  Placement = pos=(12.5,3,10) rot=(0,0,1;0rad)
  Solid = false
  Source = -> Face150
  Symmetric = false
FEATURE [Part::Revolution] Revolve167  label="moreFrontCaseScrewRetainer006"
  Angle = 360
  Axis = (0,1,0)
  Base = (0,0,0)
  FaceMakerClass = Part::FaceMakerBullseye
  Placement = pos=(109.5,4.5,68.5) rot=(0,0,1;0rad)
  Solid = false
  Source = -> Face153
  Symmetric = false
FEATURE [Part::Revolution] Revolve168  label="moreFrontCaseScrewRetainer007"
  Angle = 360
  Axis = (0,1,0)
  Base = (0,0,0)
  FaceMakerClass = Part::FaceMakerBullseye
  Placement = pos=(109.5,4.5,3.5) rot=(0,0,1;0rad)
  Solid = false
  Source = -> Face154
  Symmetric = false
FEATURE [Part::MultiFuse] Fusion151  label="screwRetainers003"
  Shapes = -> [Revolve168,Revolve167,Revolve166,Revolve165,Revolve164,Revolve163]
FEATURE [Part::Cut] Cut069  label="screwRetainers004"
  Base = -> Fusion151
  Tool = -> Fusion152
FEATURE [Part::Cut] Cut070
  Base = -> Cut069
  Tool = -> Fillet060
FEATURE [Part::Cut] Cut071  label="screwPillars001"
  Base = -> Cut070
  Tool = -> Fillet059
FEATURE [Part::MultiFuse] Fusion153  label="bottom024"
  Shapes = -> [Fusion149,Cut071]
FEATURE [Part::Cylinder] Cylinder067
  Angle = 360
  AttacherType = Attacher::AttachEngine3D
  Height = 10
  Placement = pos=(20.65,12,4.68) rot=(1,0,0;1.5708rad)
  Radius = 2
FEATURE [Part::Cylinder] Cylinder068
  Angle = 360
  AttacherType = Attacher::AttachEngine3D
  Height = 10
  Placement = pos=(20.65,12,67.38) rot=(1,0,0;1.5708rad)
  Radius = 2
FEATURE [Part::Cylinder] Cylinder069
  Angle = 360
  AttacherType = Attacher::AttachEngine3D
  Height = 10
  Placement = pos=(77.15,12,67.38) rot=(1,0,0;1.5708rad)
  Radius = 2
FEATURE [Part::Cylinder] Cylinder070
  Angle = 360
  AttacherType = Attacher::AttachEngine3D
  Height = 10
  Placement = pos=(77.15,12,4.68) rot=(1,0,0;1.5708rad)
  Radius = 2
FEATURE [Part::MultiFuse] Fusion154  label="removeFromThreadedInsertHousing001"
  Shapes = -> [Cylinder069,Cylinder068,Cylinder067,Cylinder070]
FEATURE [Part::Cut] Cut072  label="bottom025"
  Base = -> Fusion153
  Tool = -> Fusion154
FEATURE [Image::ImagePlane] ImagePlane
  XSize = 339
  YSize = 72
FEATURE [Sketcher::SketchObject] Sketch083
  FullyConstrained = false
  MapMode = 5
  Support = -> [XY_Plane]
  sketch-geometry (184):
    g0: LineSegment StartX=-151.619 StartY=28.8932 StartZ=0 EndX=-140.819 EndY=28.8932 EndZ=0
    g1: LineSegment StartX=-151.619 StartY=24.0313 StartZ=0 EndX=-151.619 EndY=28.8932 EndZ=0
    g2: LineSegment StartX=-140.819 StartY=17.7713 StartZ=0 EndX=-151.619 EndY=17.7713 EndZ=0
    g3: LineSegment StartX=-151.619 StartY=17.7713 StartZ=0 EndX=-151.619 EndY=22.6313 EndZ=0
    g4: LineSegment StartX=-151.619 StartY=22.6313 StartZ=0 EndX=-145.128 EndY=22.6313 EndZ=0
    g5: LineSegment StartX=-145.128 StartY=24.0313 StartZ=0 EndX=-140.819 EndY=28.8932 EndZ=0
    g6: LineSegment StartX=-145.128 StartY=22.6313 StartZ=0 EndX=-140.819 EndY=17.7713 EndZ=0
    g7: ArcOfCircle CenterX=-155.157 CenterY=23.3323 CenterZ=0 NormalX=0 NormalY=0 NormalZ=1 AngleXU=0 Radius=6.92354 StartAngle=1.03434 EndAngle=5.24885
    g8: ArcOfCircle CenterX=-155.157 CenterY=23.3323 CenterZ=0 NormalX=0 NormalY=0 NormalZ=1 AngleXU=0 Radius=12.6269 StartAngle=1.28675 EndAngle=4.99643
    g9: LineSegment StartX=-151.619 StartY=35.4532 StartZ=0 EndX=-151.619 EndY=29.2832 EndZ=0
    g10: LineSegment StartX=-151.619 StartY=17.3813 StartZ=0 EndX=-151.619 EndY=11.2113 EndZ=0
    g11-g21: Circle x11 (B-spline internal-alignment scaffolding for g22; pole/knot coordinates omitted)
    g22: BSplineCurve PolesCount=11 KnotsCount=9 Degree=3 IsPeriodic=0
    g23-g31: GeomPoint x9 (B-spline internal-alignment scaffolding for g22; pole/knot coordinates omitted)
    g32-g49: Circle x18 (B-spline internal-alignment scaffolding for g50; pole/knot coordinates omitted)
    g50: BSplineCurve PolesCount=18 KnotsCount=16 Degree=3 IsPeriodic=0
    g51-g66: GeomPoint x16 (B-spline internal-alignment scaffolding for g50; pole/knot coordinates omitted)
    g67: LineSegment StartX=-117.124 StartY=30.093 StartZ=0 EndX=-117.603 EndY=26.5272 EndZ=0
    g68: LineSegment StartX=-117.603 StartY=17.8472 StartZ=0 EndX=-117.124 EndY=14.2659 EndZ=0
    g69: Ellipse CenterX=-109.671 CenterY=20.025 CenterZ=0 NormalX=0 NormalY=0 NormalZ=1 MajorRadius=3.34798 MinorRadius=2.71052 AngleXU=-1.56793
    g70: GeomPoint X=-109.666 Y=18.0598 Z=0
    g71: GeomPoint X=-109.677 Y=21.9902 Z=0
    g72: Ellipse CenterX=-109.671 CenterY=20.0123 CenterZ=0 NormalX=0 NormalY=0 NormalZ=1 MajorRadius=6.93002 MinorRadius=6.36273 AngleXU=-3.13976
    g73: GeomPoint X=-112.417 Y=20.0073 Z=0
    g74: GeomPoint X=-106.925 Y=20.0173 Z=0
    g75: Ellipse CenterX=-51.7682 CenterY=20.1463 CenterZ=0 NormalX=0 NormalY=0 NormalZ=1 MajorRadius=3.19279 MinorRadius=2.71052 AngleXU=-1.52774
    g76: GeomPoint X=-51.6955 Y=18.4606 Z=0
    g77: GeomPoint X=-51.8408 Y=21.832 Z=0
    g78: GeomPoint X=-54.5142 Y=20.1413 Z=0
    g79: GeomPoint X=-49.0221 Y=20.1513 Z=0
    g80: Ellipse CenterX=-51.7682 CenterY=20.1463 CenterZ=0 NormalX=0 NormalY=0 NormalZ=1 MajorRadius=6.93002 MinorRadius=6.36273 AngleXU=-3.13976
    g81: Ellipse CenterX=-22.8436 CenterY=20.1783 CenterZ=0 NormalX=0 NormalY=0 NormalZ=1 MajorRadius=3.31512 MinorRadius=2.71052 AngleXU=-1.60214
    g82: GeomPoint X=-22.9034 Y=18.2706 Z=0
    g83: GeomPoint X=-22.7838 Y=22.0861 Z=0
    g84: GeomPoint X=-25.5897 Y=20.1733 Z=0
    g85: GeomPoint X=-20.0976 Y=20.1833 Z=0
    g86: Ellipse CenterX=-22.8436 CenterY=20.1783 CenterZ=0 NormalX=0 NormalY=0 NormalZ=1 MajorRadius=6.93002 MinorRadius=6.36273 AngleXU=-3.13976
    g87: LineSegment StartX=-101.889 StartY=14.1107 StartZ=0 EndX=-97.7455 EndY=14.1107 EndZ=0
    g88: LineSegment StartX=-93.8155 StartY=14.1107 StartZ=0 EndX=-89.6755 EndY=14.1107 EndZ=0
    g89: LineSegment StartX=-85.7455 StartY=14.1107 StartZ=0 EndX=-81.6055 EndY=14.1107 EndZ=0
    g90: LineSegment StartX=-101.889 StartY=14.1107 StartZ=0 EndX=-101.889 EndY=25.9907 EndZ=0
    g91: LineSegment StartX=-101.889 StartY=25.9907 StartZ=0 EndX=-97.8594 EndY=25.9907 EndZ=0
    g92: LineSegment StartX=-97.8594 StartY=25.9907 StartZ=0 EndX=-97.8594 EndY=24.0907 EndZ=0
    g93: LineSegment StartX=-97.7455 StartY=14.1107 StartZ=0 EndX=-97.7455 EndY=19.9107 EndZ=0
    g94: LineSegment StartX=-89.6755 StartY=14.1107 StartZ=0 EndX=-89.6755 EndY=19.9107 EndZ=0
    g95: LineSegment StartX=-93.8155 StartY=14.1107 StartZ=0 EndX=-93.8155 EndY=21.0107 EndZ=0
    g96-g106: Circle x11 (B-spline internal-alignment scaffolding for g107; pole/knot coordinates omitted)
    g107: BSplineCurve PolesCount=11 KnotsCount=9 Degree=3 IsPeriodic=0
    g108-g116: GeomPoint x9 (B-spline internal-alignment scaffolding for g107; pole/knot coordinates omitted)
    g117: BSplineCurve PolesCount=11 KnotsCount=9 Degree=3 IsPeriodic=0
    g118-g125: Circle x8 (B-spline internal-alignment scaffolding for g126; pole/knot coordinates omitted)
    g126: BSplineCurve PolesCount=8 KnotsCount=6 Degree=3 IsPeriodic=0
    g127-g132: GeomPoint x6 (B-spline internal-alignment scaffolding for g126; pole/knot coordinates omitted)
    g133: LineSegment StartX=-143.549 StartY=24.0313 StartZ=0 EndX=-143.549 EndY=28.8932 EndZ=0
    g134: BSplineCurve PolesCount=8 KnotsCount=6 Degree=3 IsPeriodic=0
    g135: LineSegment StartX=-85.7455 StartY=21.0107 StartZ=0 EndX=-85.7455 EndY=14.1107 EndZ=0
    g136: LineSegment StartX=-80.0879 StartY=14.1107 StartZ=0 EndX=-75.944 EndY=14.1107 EndZ=0
    g137: LineSegment StartX=-72.014 StartY=14.1107 StartZ=0 EndX=-67.874 EndY=14.1107 EndZ=0
    g138: LineSegment StartX=-63.944 StartY=14.1107 StartZ=0 EndX=-59.804 EndY=14.1107 EndZ=0
    g139: LineSegment StartX=-80.0879 StartY=14.1107 StartZ=0 EndX=-80.0879 EndY=25.9907 EndZ=0
    g140: LineSegment StartX=-80.0879 StartY=25.9907 StartZ=0 EndX=-76.0579 EndY=25.9907 EndZ=0
    g141: LineSegment StartX=-76.0579 StartY=25.9907 StartZ=0 EndX=-76.0579 EndY=24.0907 EndZ=0
    g142: LineSegment StartX=-75.944 StartY=14.1107 StartZ=0 EndX=-75.944 EndY=19.9107 EndZ=0
    g143: LineSegment StartX=-67.874 StartY=14.1107 StartZ=0 EndX=-67.874 EndY=19.9107 EndZ=0
    g144: LineSegment StartX=-72.014 StartY=14.1107 StartZ=0 EndX=-72.014 EndY=21.0107 EndZ=0
    g145-g149: Circle x5 (B-spline internal-alignment scaffolding for g150; pole/knot coordinates omitted)
    g150: BSplineCurve PolesCount=11 KnotsCount=9 Degree=3 IsPeriodic=0
    g151-g159: GeomPoint x9 (B-spline internal-alignment scaffolding for g150; pole/knot coordinates omitted)
    g160: BSplineCurve PolesCount=11 KnotsCount=9 Degree=3 IsPeriodic=0
    g161-g168: Circle x8 (B-spline internal-alignment scaffolding for g169; pole/knot coordinates omitted)
    g169: BSplineCurve PolesCount=8 KnotsCount=6 Degree=3 IsPeriodic=0
    g170-g175: GeomPoint x6 (B-spline internal-alignment scaffolding for g169; pole/knot coordinates omitted)
    g176: BSplineCurve PolesCount=8 KnotsCount=6 Degree=3 IsPeriodic=0
    g177: LineSegment StartX=-63.944 StartY=21.0107 StartZ=0 EndX=-63.944 EndY=14.1107 EndZ=0
    g178: LineSegment StartX=-59.804 StartY=14.1107 StartZ=0 EndX=-59.804 EndY=21.5868 EndZ=0
    g179: BSplineCurve PolesCount=4 KnotsCount=2 Degree=3 IsPeriodic=0
    g180: GeomPoint X=-59.804 Y=21.5868 Z=0
    g181: GeomPoint X=-60.2379 Y=24.0907 Z=0
    g182: LineSegment StartX=-81.6055 StartY=14.1107 StartZ=0 EndX=-81.6055 EndY=21.5868 EndZ=0
    g183: BSplineCurve PolesCount=4 KnotsCount=2 Degree=3 IsPeriodic=0
  constraints (161):
    c: Coincident(g1,g0)
    c: Horizontal(g0)
    c: Vertical(g1)
    c: Coincident(g2,g3)
    c: Coincident(g3,g4)
    c: Horizontal(g4)
    c: Horizontal(g2)
    c: Vertical(g3)
    c: Block(g1)
    c: Distance(g3) = 4.86
    c: Block(g4)
    c: Distance(g0) = 10.8
    c: Distance(g2) = 10.8
    c: Coincident(g5,g0)
    c: Coincident(g6,g4)
    c: Coincident(g6,g2)
    c: Block(g8)
    c: Block(g7)
    c: Coincident(g9,g8)
    c: Coincident(g9,g7)
    c: Vertical(g9)
    c: Coincident(g10,g7)
    c: Coincident(g10,g8)
    c: Vertical(g10)
    c: Weight(g11) = 1
    c: Equal(g11, g12-g21) x10
    c: InternalAlignment(g11-g21 -> g22) x11
    c: InternalAlignment(g23-g31 -> g22) x9
    c: Block(g22)
    c: Weight(g32) = 1
    c: Equal(g32, g33-g49) x17
    c: InternalAlignment(g32-g49 -> g50) x18
    c: InternalAlignment(g51-g66 -> g50) x16
    c: Block(g50)
    c: Coincident(g67,g50)
    c: Coincident(g67,g22)
    c: Coincident(g68,g22)
    c: Coincident(g68,g50)
    c: InternalAlignment(g70,g69)
    c: InternalAlignment(g71,g69)
    c: Block(g69)
    c: InternalAlignment(g73,g72)
    c: InternalAlignment(g74,g72)
    c: Block(g72)
    c: InternalAlignment(g76,g75)
    c: InternalAlignment(g77,g75)
    c: InternalAlignment(g78,g80)
    c: InternalAlignment(g79,g80)
    c: Block(g80)
    c: Coincident(g75,g80)
    c: Block(g75)
    c: InternalAlignment(g82,g81)
    c: InternalAlignment(g83,g81)
    c: InternalAlignment(g84,g86)
    c: InternalAlignment(g85,g86)
    c: Block(g86)
    c: Coincident(g81,g86)
    c: Block(g81)
    c: Horizontal(g87)
    c: Block(g87)
    c: Horizontal(g88)
    c: Distance(g88) = 4.14
    c: Horizontal(g89)
    c: Equal(g88,g89) = 4.14
    c: Block(g89)
    c: Block(g88)
    c: Coincident(g90,g87)
    c: Vertical(g90)
    c: Distance(g90) = 11.88
    c: Coincident(g91,g90)
    c: Horizontal(g91)
    c: Coincident(g92,g91)
    c: Vertical(g92)
    c: Distance(g91) = 4.03
    c: Distance(g92) = 1.9
    c: Coincident(g93,g87)
    c: Vertical(g93)
    c: Vertical(g94)
    c: Coincident(g94,g88)
    c: Distance(g93) = 5.8
    c: Distance(g94) = 5.8
    c: Vertical(g95)
    c: Coincident(g95,g88)
    c: Distance(g95) = 6.9
    c: Coincident(g107,g92)
    c: Weight(g96) = 1
    c: Equal(g96, g97-g106) x10
    c: InternalAlignment(g96-g106 -> g107) x11
    c: InternalAlignment(g108-g116 -> g107) x9
    c: Block(g107)
    c: Block(g117)
    c: Coincident(g126,g93)
    c: Weight(g118) = 1
    c: Equal(g118, g119-g125) x7
    c: Coincident(g126,g95)
    c: InternalAlignment(g118-g125 -> g126) x8
    c: InternalAlignment(g127-g132 -> g126) x6
    c: Vertical(g133)
    c: Block(g133)
    c: Coincident(g134,g94)
    c: Block(g126)
    c: Block(g134)
    c: Coincident(g135,g134)
    c: Coincident(g135,g89)
    c: Vertical(g135)
    c: Horizontal(g136)
    c: Block(g136)
    c: Horizontal(g137)
    c: Equal(g88,g137) = 4.14
    c: Horizontal(g138)
    c: Equal(g137,g138) = 4.14
    c: Block(g138)
    c: Block(g137)
    c: Coincident(g139,g136)
    c: Vertical(g139)
    c: Equal(g90,g139) = 11.88
    c: Coincident(g140,g139)
    c: Horizontal(g140)
    c: Coincident(g141,g140)
    c: Vertical(g141)
    c: Equal(g91,g140) = 4.03
    c: Equal(g92,g141) = 1.9
    c: Coincident(g142,g136)
    c: Vertical(g142)
    c: Vertical(g143)
    c: Coincident(g143,g137)
    c: Equal(g93,g142) = 5.8
    c: Equal(g94,g143) = 5.8
    c: Vertical(g144)
    c: Coincident(g144,g137)
    c: Equal(g95,g144) = 6.9
    c: Coincident(g150,g141)
    c: Equal(g96,g145) = 1
    c: Equal(g145, g146-g149) x4
    c: InternalAlignment(g145-g149 -> g150) x5
    c: InternalAlignment(g151-g159 -> g150) x9
    c: Block(g150)
    c: Block(g160)
    c: Coincident(g169,g142)
    c: Equal(g118,g161) = 1
    c: Equal(g161, g162-g168) x7
    c: Coincident(g169,g144)
    c: InternalAlignment(g161-g168 -> g169) x8
    c: InternalAlignment(g170-g175 -> g169) x6
    c: Coincident(g176,g143)
    c: Block(g169)
    c: Block(g176)
    c: Coincident(g177,g176)
    c: Coincident(g177,g138)
    c: Vertical(g177)
    c: Coincident(g178,g138)
    c: Vertical(g178)
    c: Coincident(g179,g178)
    c: Coincident(g179,g160)
    c: InternalAlignment(g180,g179)
    c: InternalAlignment(g181,g179)
    c: Block(g179)
    c: Vertical(g182)
    c: Coincident(g182,g89)
    c: Block(g183)
    c: Coincident(g183,g182)
FEATURE [PartDesign::Body] Body
  Group = -> [Sketch083]
  Origin = -> Origin
FEATURE [Sketcher::SketchObject] Sketch084
  FullyConstrained = true
  MapMode = 5
  Support = -> [XY_Plane001]
FEATURE [PartDesign::Body] Body001
  Group = -> [Sketch084]
  Origin = -> Origin001
